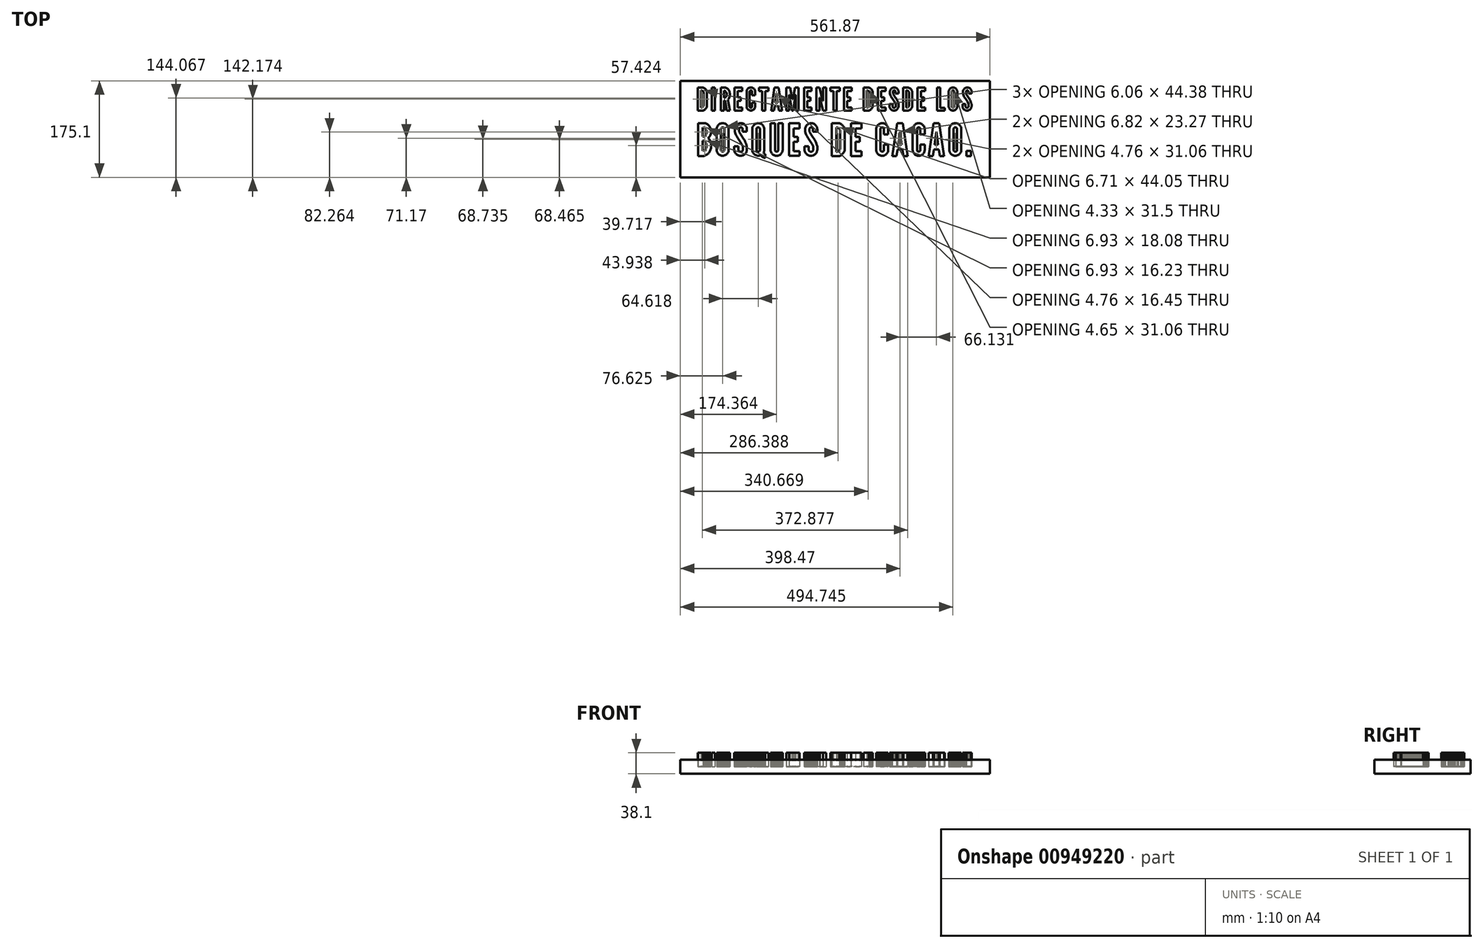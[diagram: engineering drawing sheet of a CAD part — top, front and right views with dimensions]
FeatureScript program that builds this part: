
annotation { "Feature Type Name" : "Feature", "Feature Type Description" : "" }
export const myFeature = defineFeature(function(context is Context, id is Id, definition is map)
    precondition{}
    {
        {
            var Q0;
            Q0=qCreatedBy(makeId("Top.planeOp"),FACE);
            var sketch = newSketch(context, id + "F0", { "sketchPlane" : qUnion([Q0])});
            skLineSegment(sketch, "E0", {"start": v(-116.2, -328.45) * mm, "end": v(-116.2, -376.5) * mm});
            skLineSegment(sketch, "E1", {"start": v(-116.2, -376.5) * mm, "end": v(-116.2, -377.7) * mm});
            skLineSegment(sketch, "E2", {"start": v(-116.2, -377.7) * mm, "end": v(-115.97, -378.89) * mm});
            skLineSegment(sketch, "E3", {"start": v(-115.97, -378.89) * mm, "end": v(-115.65, -379.97) * mm});
            skLineSegment(sketch, "E4", {"start": v(-115.65, -379.97) * mm, "end": v(-115.22, -381.05) * mm});
            skLineSegment(sketch, "E5", {"start": v(-115.22, -381.05) * mm, "end": v(-114.78, -382.02) * mm});
            skLineSegment(sketch, "E6", {"start": v(-114.78, -382.02) * mm, "end": v(-114.14, -383) * mm});
            skLineSegment(sketch, "E7", {"start": v(-114.14, -383) * mm, "end": v(-113.38, -383.86) * mm});
            skLineSegment(sketch, "E8", {"start": v(-113.38, -383.86) * mm, "end": v(-112.62, -384.73) * mm});
            skLineSegment(sketch, "E9", {"start": v(-112.62, -384.73) * mm, "end": v(-111.65, -385.49) * mm});
            skLineSegment(sketch, "E10", {"start": v(-111.65, -385.49) * mm, "end": v(-110.78, -386.03) * mm});
            skLineSegment(sketch, "E11", {"start": v(-110.78, -386.03) * mm, "end": v(-109.7, -386.57) * mm});
            skLineSegment(sketch, "E12", {"start": v(-109.7, -386.57) * mm, "end": v(-108.61, -387) * mm});
            skLineSegment(sketch, "E13", {"start": v(-108.61, -387) * mm, "end": v(-107.53, -387.33) * mm});
            skLineSegment(sketch, "E14", {"start": v(-107.53, -387.33) * mm, "end": v(-106.34, -387.44) * mm});
            skLineSegment(sketch, "E15", {"start": v(-106.34, -387.44) * mm, "end": v(-105.26, -387.54) * mm});
            skLineSegment(sketch, "E16", {"start": v(-105.26, -387.54) * mm, "end": v(-104.07, -387.44) * mm});
            skLineSegment(sketch, "E17", {"start": v(-104.07, -387.44) * mm, "end": v(-102.99, -387.33) * mm});
            skLineSegment(sketch, "E18", {"start": v(-102.99, -387.33) * mm, "end": v(-101.8, -387) * mm});
            skLineSegment(sketch, "E19", {"start": v(-101.8, -387) * mm, "end": v(-100.82, -386.57) * mm});
            skLineSegment(sketch, "E20", {"start": v(-100.82, -386.57) * mm, "end": v(-99.74, -386.03) * mm});
            skLineSegment(sketch, "E21", {"start": v(-99.74, -386.03) * mm, "end": v(-98.76, -385.49) * mm});
            skLineSegment(sketch, "E22", {"start": v(-98.76, -385.49) * mm, "end": v(-97.9, -384.73) * mm});
            skLineSegment(sketch, "E23", {"start": v(-97.9, -384.73) * mm, "end": v(-97.03, -383.86) * mm});
            skLineSegment(sketch, "E24", {"start": v(-97.03, -383.86) * mm, "end": v(-96.38, -383) * mm});
            skLineSegment(sketch, "E25", {"start": v(-96.38, -383) * mm, "end": v(-95.73, -382.02) * mm});
            skLineSegment(sketch, "E26", {"start": v(-95.73, -382.02) * mm, "end": v(-95.2, -381.05) * mm});
            skLineSegment(sketch, "E27", {"start": v(-95.2, -381.05) * mm, "end": v(-94.76, -379.97) * mm});
            skLineSegment(sketch, "E28", {"start": v(-94.76, -379.97) * mm, "end": v(-94.54, -378.89) * mm});
            skLineSegment(sketch, "E29", {"start": v(-94.54, -378.89) * mm, "end": v(-94.33, -377.7) * mm});
            skLineSegment(sketch, "E30", {"start": v(-94.33, -377.7) * mm, "end": v(-94.22, -376.5) * mm});
            skLineSegment(sketch, "E31", {"start": v(-94.22, -376.5) * mm, "end": v(-94.22, -328.45) * mm});
            skLineSegment(sketch, "E32", {"start": v(-94.22, -328.45) * mm, "end": v(-102.23, -328.45) * mm});
            skLineSegment(sketch, "E33", {"start": v(-102.23, -328.45) * mm, "end": v(-102.23, -377.15) * mm});
            skLineSegment(sketch, "E34", {"start": v(-108.3, -377.15) * mm, "end": v(-108.18, -377.8) * mm});
            skLineSegment(sketch, "E35", {"start": v(-108.18, -377.8) * mm, "end": v(-108.08, -378.34) * mm});
            skLineSegment(sketch, "E36", {"start": v(-108.08, -378.34) * mm, "end": v(-107.75, -378.89) * mm});
            skLineSegment(sketch, "E37", {"start": v(-107.75, -378.89) * mm, "end": v(-107.43, -379.32) * mm});
            skLineSegment(sketch, "E38", {"start": v(-107.43, -379.32) * mm, "end": v(-106.88, -379.75) * mm});
            skLineSegment(sketch, "E39", {"start": v(-106.88, -379.75) * mm, "end": v(-106.45, -379.97) * mm});
            skLineSegment(sketch, "E40", {"start": v(-106.45, -379.97) * mm, "end": v(-105.8, -380.18) * mm});
            skLineSegment(sketch, "E41", {"start": v(-105.8, -380.18) * mm, "end": v(-104.61, -380.18) * mm});
            skLineSegment(sketch, "E42", {"start": v(-104.61, -380.18) * mm, "end": v(-104.07, -379.97) * mm});
            skLineSegment(sketch, "E43", {"start": v(-104.07, -379.97) * mm, "end": v(-103.53, -379.75) * mm});
            skLineSegment(sketch, "E44", {"start": v(-103.53, -379.75) * mm, "end": v(-103.1, -379.32) * mm});
            skLineSegment(sketch, "E45", {"start": v(-103.1, -379.32) * mm, "end": v(-102.66, -378.89) * mm});
            skLineSegment(sketch, "E46", {"start": v(-102.66, -378.89) * mm, "end": v(-102.23, -377.8) * mm});
            skLineSegment(sketch, "E47", {"start": v(-102.23, -377.8) * mm, "end": v(-102.23, -377.15) * mm});
            skLineSegment(sketch, "E48", {"start": v(-108.3, -377.15) * mm, "end": v(-108.3, -328.45) * mm});
            skLineSegment(sketch, "E49", {"start": v(-108.3, -328.45) * mm, "end": v(-116.2, -328.45) * mm});
            skLineSegment(sketch, "E50", {"start": v(9.9, -341.44) * mm, "end": v(9.9, -375.1) * mm});
            skLineSegment(sketch, "E51", {"start": v(3.95, -380.3) * mm, "end": v(4.82, -380.18) * mm});
            skLineSegment(sketch, "E52", {"start": v(4.82, -380.18) * mm, "end": v(5.8, -379.97) * mm});
            skLineSegment(sketch, "E53", {"start": v(5.8, -379.97) * mm, "end": v(6.66, -379.54) * mm});
            skLineSegment(sketch, "E54", {"start": v(6.66, -379.54) * mm, "end": v(7.42, -379) * mm});
            skLineSegment(sketch, "E55", {"start": v(7.42, -379) * mm, "end": v(8.17, -378.45) * mm});
            skLineSegment(sketch, "E56", {"start": v(8.17, -378.45) * mm, "end": v(8.82, -377.7) * mm});
            skLineSegment(sketch, "E57", {"start": v(8.82, -377.7) * mm, "end": v(9.25, -376.94) * mm});
            skLineSegment(sketch, "E58", {"start": v(9.25, -376.94) * mm, "end": v(9.69, -376.07) * mm});
            skLineSegment(sketch, "E59", {"start": v(9.69, -376.07) * mm, "end": v(9.9, -375.1) * mm});
            skLineSegment(sketch, "E60", {"start": v(3.95, -380.3) * mm, "end": v(3.2, -380.3) * mm});
            skLineSegment(sketch, "E61", {"start": v(3.2, -380.3) * mm, "end": v(3.2, -336.24) * mm});
            skLineSegment(sketch, "E62", {"start": v(3.2, -336.24) * mm, "end": v(3.95, -336.24) * mm});
            skLineSegment(sketch, "E63", {"start": v(9.9, -341.44) * mm, "end": v(9.69, -340.46) * mm});
            skLineSegment(sketch, "E64", {"start": v(9.69, -340.46) * mm, "end": v(9.25, -339.6) * mm});
            skLineSegment(sketch, "E65", {"start": v(9.25, -339.6) * mm, "end": v(8.82, -338.84) * mm});
            skLineSegment(sketch, "E66", {"start": v(8.82, -338.84) * mm, "end": v(8.17, -338.08) * mm});
            skLineSegment(sketch, "E67", {"start": v(8.17, -338.08) * mm, "end": v(7.42, -337.43) * mm});
            skLineSegment(sketch, "E68", {"start": v(7.42, -337.43) * mm, "end": v(6.66, -337) * mm});
            skLineSegment(sketch, "E69", {"start": v(6.66, -337) * mm, "end": v(5.8, -336.56) * mm});
            skLineSegment(sketch, "E70", {"start": v(5.8, -336.56) * mm, "end": v(4.82, -336.35) * mm});
            skLineSegment(sketch, "E71", {"start": v(4.82, -336.35) * mm, "end": v(3.95, -336.24) * mm});
            skLineSegment(sketch, "E72", {"start": v(-5.36, -328.45) * mm, "end": v(-5.36, -387.98) * mm});
            skLineSegment(sketch, "E73", {"start": v(-5.36, -387.98) * mm, "end": v(8.6, -387.98) * mm});
            skLineSegment(sketch, "E74", {"start": v(8.6, -387.98) * mm, "end": v(9.9, -387.44) * mm});
            skLineSegment(sketch, "E75", {"start": v(9.9, -387.44) * mm, "end": v(11.2, -386.79) * mm});
            skLineSegment(sketch, "E76", {"start": v(11.2, -386.79) * mm, "end": v(12.4, -386.03) * mm});
            skLineSegment(sketch, "E77", {"start": v(12.4, -386.03) * mm, "end": v(13.48, -385.16) * mm});
            skLineSegment(sketch, "E78", {"start": v(13.48, -385.16) * mm, "end": v(14.45, -384.19) * mm});
            skLineSegment(sketch, "E79", {"start": v(14.45, -384.19) * mm, "end": v(15.42, -383.1) * mm});
            skLineSegment(sketch, "E80", {"start": v(15.42, -383.1) * mm, "end": v(16.3, -382.02) * mm});
            skLineSegment(sketch, "E81", {"start": v(16.3, -382.02) * mm, "end": v(16.94, -380.73) * mm});
            skLineSegment(sketch, "E82", {"start": v(16.94, -380.73) * mm, "end": v(17.59, -379.54) * mm});
            skLineSegment(sketch, "E83", {"start": v(17.59, -379.54) * mm, "end": v(18.13, -378.13) * mm});
            skLineSegment(sketch, "E84", {"start": v(18.13, -378.13) * mm, "end": v(18.46, -376.83) * mm});
            skLineSegment(sketch, "E85", {"start": v(18.46, -376.83) * mm, "end": v(18.46, -339.7) * mm});
            skLineSegment(sketch, "E86", {"start": v(18.46, -339.7) * mm, "end": v(18.13, -338.3) * mm});
            skLineSegment(sketch, "E87", {"start": v(18.13, -338.3) * mm, "end": v(17.59, -337) * mm});
            skLineSegment(sketch, "E88", {"start": v(17.59, -337) * mm, "end": v(16.94, -335.7) * mm});
            skLineSegment(sketch, "E89", {"start": v(16.94, -335.7) * mm, "end": v(16.3, -334.5) * mm});
            skLineSegment(sketch, "E90", {"start": v(16.3, -334.5) * mm, "end": v(15.42, -333.43) * mm});
            skLineSegment(sketch, "E91", {"start": v(15.42, -333.43) * mm, "end": v(14.45, -332.34) * mm});
            skLineSegment(sketch, "E92", {"start": v(14.45, -332.34) * mm, "end": v(13.48, -331.37) * mm});
            skLineSegment(sketch, "E93", {"start": v(13.48, -331.37) * mm, "end": v(12.4, -330.5) * mm});
            skLineSegment(sketch, "E94", {"start": v(12.4, -330.5) * mm, "end": v(11.2, -329.75) * mm});
            skLineSegment(sketch, "E95", {"start": v(11.2, -329.75) * mm, "end": v(9.9, -329.1) * mm});
            skLineSegment(sketch, "E96", {"start": v(9.9, -329.1) * mm, "end": v(8.6, -328.45) * mm});
            skLineSegment(sketch, "E97", {"start": v(8.6, -328.45) * mm, "end": v(-5.36, -328.45) * mm});
            skLineSegment(sketch, "E98", {"start": v(-135.57, -338.84) * mm, "end": v(-135.57, -377.15) * mm});
            skLineSegment(sketch, "E99", {"start": v(-141.63, -377.15) * mm, "end": v(-141.63, -377.8) * mm});
            skLineSegment(sketch, "E100", {"start": v(-141.63, -377.8) * mm, "end": v(-141.41, -378.34) * mm});
            skLineSegment(sketch, "E101", {"start": v(-141.41, -378.34) * mm, "end": v(-141.09, -378.89) * mm});
            skLineSegment(sketch, "E102", {"start": v(-141.09, -378.89) * mm, "end": v(-140.76, -379.32) * mm});
            skLineSegment(sketch, "E103", {"start": v(-140.76, -379.32) * mm, "end": v(-140.33, -379.75) * mm});
            skLineSegment(sketch, "E104", {"start": v(-140.33, -379.75) * mm, "end": v(-139.79, -379.97) * mm});
            skLineSegment(sketch, "E105", {"start": v(-139.79, -379.97) * mm, "end": v(-139.14, -380.18) * mm});
            skLineSegment(sketch, "E106", {"start": v(-139.14, -380.18) * mm, "end": v(-137.95, -380.18) * mm});
            skLineSegment(sketch, "E107", {"start": v(-137.95, -380.18) * mm, "end": v(-136.86, -379.75) * mm});
            skLineSegment(sketch, "E108", {"start": v(-136.86, -379.75) * mm, "end": v(-136, -378.89) * mm});
            skLineSegment(sketch, "E109", {"start": v(-136, -378.89) * mm, "end": v(-135.57, -377.8) * mm});
            skLineSegment(sketch, "E110", {"start": v(-135.57, -377.8) * mm, "end": v(-135.57, -377.15) * mm});
            skLineSegment(sketch, "E111", {"start": v(-141.63, -377.15) * mm, "end": v(-141.63, -338.84) * mm});
            skLineSegment(sketch, "E112", {"start": v(-135.57, -338.84) * mm, "end": v(-135.57, -338.3) * mm});
            skLineSegment(sketch, "E113", {"start": v(-135.57, -338.3) * mm, "end": v(-135.78, -337.65) * mm});
            skLineSegment(sketch, "E114", {"start": v(-135.78, -337.65) * mm, "end": v(-136, -337.21) * mm});
            skLineSegment(sketch, "E115", {"start": v(-136, -337.21) * mm, "end": v(-136.43, -336.67) * mm});
            skLineSegment(sketch, "E116", {"start": v(-136.43, -336.67) * mm, "end": v(-136.86, -336.35) * mm});
            skLineSegment(sketch, "E117", {"start": v(-136.86, -336.35) * mm, "end": v(-137.4, -336.02) * mm});
            skLineSegment(sketch, "E118", {"start": v(-137.4, -336.02) * mm, "end": v(-137.95, -335.91) * mm});
            skLineSegment(sketch, "E119", {"start": v(-137.95, -335.91) * mm, "end": v(-138.6, -335.8) * mm});
            skLineSegment(sketch, "E120", {"start": v(-138.6, -335.8) * mm, "end": v(-139.14, -335.91) * mm});
            skLineSegment(sketch, "E121", {"start": v(-139.14, -335.91) * mm, "end": v(-139.79, -336.02) * mm});
            skLineSegment(sketch, "E122", {"start": v(-139.79, -336.02) * mm, "end": v(-140.33, -336.35) * mm});
            skLineSegment(sketch, "E123", {"start": v(-140.33, -336.35) * mm, "end": v(-140.76, -336.67) * mm});
            skLineSegment(sketch, "E124", {"start": v(-140.76, -336.67) * mm, "end": v(-141.09, -337.21) * mm});
            skLineSegment(sketch, "E125", {"start": v(-141.09, -337.21) * mm, "end": v(-141.41, -337.65) * mm});
            skLineSegment(sketch, "E126", {"start": v(-141.41, -337.65) * mm, "end": v(-141.63, -338.3) * mm});
            skLineSegment(sketch, "E127", {"start": v(-141.63, -338.3) * mm, "end": v(-141.63, -338.84) * mm});
            skLineSegment(sketch, "E128", {"start": v(-149.53, -376.5) * mm, "end": v(-149.53, -339.49) * mm});
            skLineSegment(sketch, "E129", {"start": v(-127.55, -339.49) * mm, "end": v(-127.66, -338.3) * mm});
            skLineSegment(sketch, "E130", {"start": v(-127.66, -338.3) * mm, "end": v(-128.1, -336.13) * mm});
            skLineSegment(sketch, "E131", {"start": v(-128.1, -336.13) * mm, "end": v(-128.53, -335.05) * mm});
            skLineSegment(sketch, "E132", {"start": v(-128.53, -335.05) * mm, "end": v(-129.07, -333.97) * mm});
            skLineSegment(sketch, "E133", {"start": v(-129.07, -333.97) * mm, "end": v(-129.72, -333) * mm});
            skLineSegment(sketch, "E134", {"start": v(-129.72, -333) * mm, "end": v(-130.48, -332.13) * mm});
            skLineSegment(sketch, "E135", {"start": v(-130.48, -332.13) * mm, "end": v(-131.24, -331.37) * mm});
            skLineSegment(sketch, "E136", {"start": v(-131.24, -331.37) * mm, "end": v(-132.1, -330.61) * mm});
            skLineSegment(sketch, "E137", {"start": v(-132.1, -330.61) * mm, "end": v(-133.08, -329.96) * mm});
            skLineSegment(sketch, "E138", {"start": v(-133.08, -329.96) * mm, "end": v(-134.16, -329.42) * mm});
            skLineSegment(sketch, "E139", {"start": v(-134.16, -329.42) * mm, "end": v(-135.24, -328.99) * mm});
            skLineSegment(sketch, "E140", {"start": v(-135.24, -328.99) * mm, "end": v(-136.33, -328.77) * mm});
            skLineSegment(sketch, "E141", {"start": v(-136.33, -328.77) * mm, "end": v(-137.4, -328.56) * mm});
            skLineSegment(sketch, "E142", {"start": v(-137.4, -328.56) * mm, "end": v(-138.6, -328.45) * mm});
            skLineSegment(sketch, "E143", {"start": v(-138.6, -328.45) * mm, "end": v(-139.79, -328.56) * mm});
            skLineSegment(sketch, "E144", {"start": v(-139.79, -328.56) * mm, "end": v(-140.87, -328.77) * mm});
            skLineSegment(sketch, "E145", {"start": v(-140.87, -328.77) * mm, "end": v(-141.95, -328.99) * mm});
            skLineSegment(sketch, "E146", {"start": v(-141.95, -328.99) * mm, "end": v(-143.03, -329.42) * mm});
            skLineSegment(sketch, "E147", {"start": v(-143.03, -329.42) * mm, "end": v(-144.12, -329.96) * mm});
            skLineSegment(sketch, "E148", {"start": v(-144.12, -329.96) * mm, "end": v(-145.1, -330.61) * mm});
            skLineSegment(sketch, "E149", {"start": v(-145.1, -330.61) * mm, "end": v(-145.96, -331.37) * mm});
            skLineSegment(sketch, "E150", {"start": v(-145.96, -331.37) * mm, "end": v(-146.71, -332.13) * mm});
            skLineSegment(sketch, "E151", {"start": v(-146.71, -332.13) * mm, "end": v(-147.47, -333) * mm});
            skLineSegment(sketch, "E152", {"start": v(-147.47, -333) * mm, "end": v(-148.12, -333.97) * mm});
            skLineSegment(sketch, "E153", {"start": v(-148.12, -333.97) * mm, "end": v(-148.66, -335.05) * mm});
            skLineSegment(sketch, "E154", {"start": v(-148.66, -335.05) * mm, "end": v(-148.99, -336.13) * mm});
            skLineSegment(sketch, "E155", {"start": v(-148.99, -336.13) * mm, "end": v(-149.31, -337.21) * mm});
            skLineSegment(sketch, "E156", {"start": v(-149.31, -337.21) * mm, "end": v(-149.53, -338.3) * mm});
            skLineSegment(sketch, "E157", {"start": v(-149.53, -338.3) * mm, "end": v(-149.53, -339.49) * mm});
            skLineSegment(sketch, "E158", {"start": v(-127.55, -339.49) * mm, "end": v(-127.55, -376.5) * mm});
            skLineSegment(sketch, "E159", {"start": v(-129.29, -382.35) * mm, "end": v(-128.64, -381.27) * mm});
            skLineSegment(sketch, "E160", {"start": v(-128.64, -381.27) * mm, "end": v(-128.2, -380.08) * mm});
            skLineSegment(sketch, "E161", {"start": v(-128.2, -380.08) * mm, "end": v(-127.88, -379) * mm});
            skLineSegment(sketch, "E162", {"start": v(-127.88, -379) * mm, "end": v(-127.66, -377.8) * mm});
            skLineSegment(sketch, "E163", {"start": v(-127.66, -377.8) * mm, "end": v(-127.55, -376.5) * mm});
            skLineSegment(sketch, "E164", {"start": v(-129.29, -382.35) * mm, "end": v(-128.2, -383.43) * mm});
            skLineSegment(sketch, "E165", {"start": v(-128.2, -383.43) * mm, "end": v(-127.55, -383.97) * mm});
            skLineSegment(sketch, "E166", {"start": v(-127.55, -383.97) * mm, "end": v(-126.8, -384.3) * mm});
            skLineSegment(sketch, "E167", {"start": v(-126.8, -384.3) * mm, "end": v(-126.04, -384.51) * mm});
            skLineSegment(sketch, "E168", {"start": v(-126.04, -384.51) * mm, "end": v(-126.04, -391.55) * mm});
            skLineSegment(sketch, "E169", {"start": v(-134.05, -386.57) * mm, "end": v(-133.4, -387.44) * mm});
            skLineSegment(sketch, "E170", {"start": v(-133.4, -387.44) * mm, "end": v(-132.75, -388.3) * mm});
            skLineSegment(sketch, "E171", {"start": v(-132.75, -388.3) * mm, "end": v(-131.89, -389.06) * mm});
            skLineSegment(sketch, "E172", {"start": v(-131.89, -389.06) * mm, "end": v(-131.13, -389.7) * mm});
            skLineSegment(sketch, "E173", {"start": v(-131.13, -389.7) * mm, "end": v(-130.16, -390.25) * mm});
            skLineSegment(sketch, "E174", {"start": v(-130.16, -390.25) * mm, "end": v(-129.18, -390.8) * mm});
            skLineSegment(sketch, "E175", {"start": v(-129.18, -390.8) * mm, "end": v(-128.2, -391.12) * mm});
            skLineSegment(sketch, "E176", {"start": v(-128.2, -391.12) * mm, "end": v(-127.12, -391.33) * mm});
            skLineSegment(sketch, "E177", {"start": v(-127.12, -391.33) * mm, "end": v(-126.04, -391.55) * mm});
            skLineSegment(sketch, "E178", {"start": v(-149.53, -376.5) * mm, "end": v(-149.53, -377.7) * mm});
            skLineSegment(sketch, "E179", {"start": v(-149.53, -377.7) * mm, "end": v(-149.31, -378.89) * mm});
            skLineSegment(sketch, "E180", {"start": v(-149.31, -378.89) * mm, "end": v(-148.99, -379.97) * mm});
            skLineSegment(sketch, "E181", {"start": v(-148.99, -379.97) * mm, "end": v(-148.66, -381.05) * mm});
            skLineSegment(sketch, "E182", {"start": v(-148.66, -381.05) * mm, "end": v(-148.12, -382.02) * mm});
            skLineSegment(sketch, "E183", {"start": v(-148.12, -382.02) * mm, "end": v(-147.47, -383) * mm});
            skLineSegment(sketch, "E184", {"start": v(-147.47, -383) * mm, "end": v(-146.71, -383.97) * mm});
            skLineSegment(sketch, "E185", {"start": v(-146.71, -383.97) * mm, "end": v(-145.85, -384.73) * mm});
            skLineSegment(sketch, "E186", {"start": v(-145.85, -384.73) * mm, "end": v(-144.98, -385.49) * mm});
            skLineSegment(sketch, "E187", {"start": v(-144.98, -385.49) * mm, "end": v(-144, -386.14) * mm});
            skLineSegment(sketch, "E188", {"start": v(-144, -386.14) * mm, "end": v(-143.03, -386.57) * mm});
            skLineSegment(sketch, "E189", {"start": v(-143.03, -386.57) * mm, "end": v(-141.95, -387) * mm});
            skLineSegment(sketch, "E190", {"start": v(-141.95, -387) * mm, "end": v(-140.76, -387.33) * mm});
            skLineSegment(sketch, "E191", {"start": v(-140.76, -387.33) * mm, "end": v(-139.68, -387.44) * mm});
            skLineSegment(sketch, "E192", {"start": v(-139.68, -387.44) * mm, "end": v(-138.49, -387.54) * mm});
            skLineSegment(sketch, "E193", {"start": v(-138.49, -387.54) * mm, "end": v(-137.3, -387.44) * mm});
            skLineSegment(sketch, "E194", {"start": v(-137.3, -387.44) * mm, "end": v(-136.22, -387.33) * mm});
            skLineSegment(sketch, "E195", {"start": v(-136.22, -387.33) * mm, "end": v(-135.13, -387) * mm});
            skLineSegment(sketch, "E196", {"start": v(-135.13, -387) * mm, "end": v(-134.05, -386.57) * mm});
            skLineSegment(sketch, "E197", {"start": v(-167.06, -338.84) * mm, "end": v(-167.06, -343.7) * mm});
            skLineSegment(sketch, "E198", {"start": v(-167.06, -343.7) * mm, "end": v(-159.16, -343.7) * mm});
            skLineSegment(sketch, "E199", {"start": v(-159.16, -343.7) * mm, "end": v(-159.16, -339.49) * mm});
            skLineSegment(sketch, "E200", {"start": v(-159.16, -339.49) * mm, "end": v(-159.16, -338.3) * mm});
            skLineSegment(sketch, "E201", {"start": v(-159.16, -338.3) * mm, "end": v(-159.38, -337.21) * mm});
            skLineSegment(sketch, "E202", {"start": v(-159.38, -337.21) * mm, "end": v(-159.7, -336.13) * mm});
            skLineSegment(sketch, "E203", {"start": v(-159.7, -336.13) * mm, "end": v(-160.03, -335.05) * mm});
            skLineSegment(sketch, "E204", {"start": v(-160.03, -335.05) * mm, "end": v(-160.57, -333.97) * mm});
            skLineSegment(sketch, "E205", {"start": v(-160.57, -333.97) * mm, "end": v(-161.22, -333) * mm});
            skLineSegment(sketch, "E206", {"start": v(-161.22, -333) * mm, "end": v(-161.97, -332.13) * mm});
            skLineSegment(sketch, "E207", {"start": v(-161.97, -332.13) * mm, "end": v(-162.73, -331.37) * mm});
            skLineSegment(sketch, "E208", {"start": v(-162.73, -331.37) * mm, "end": v(-163.7, -330.61) * mm});
            skLineSegment(sketch, "E209", {"start": v(-163.7, -330.61) * mm, "end": v(-164.58, -329.96) * mm});
            skLineSegment(sketch, "E210", {"start": v(-164.58, -329.96) * mm, "end": v(-165.65, -329.42) * mm});
            skLineSegment(sketch, "E211", {"start": v(-165.65, -329.42) * mm, "end": v(-166.74, -328.99) * mm});
            skLineSegment(sketch, "E212", {"start": v(-166.74, -328.99) * mm, "end": v(-167.82, -328.77) * mm});
            skLineSegment(sketch, "E213", {"start": v(-167.82, -328.77) * mm, "end": v(-169.01, -328.56) * mm});
            skLineSegment(sketch, "E214", {"start": v(-169.01, -328.56) * mm, "end": v(-170.1, -328.45) * mm});
            skLineSegment(sketch, "E215", {"start": v(-170.1, -328.45) * mm, "end": v(-171.28, -328.56) * mm});
            skLineSegment(sketch, "E216", {"start": v(-171.28, -328.56) * mm, "end": v(-172.37, -328.77) * mm});
            skLineSegment(sketch, "E217", {"start": v(-172.37, -328.77) * mm, "end": v(-173.45, -328.99) * mm});
            skLineSegment(sketch, "E218", {"start": v(-173.45, -328.99) * mm, "end": v(-174.53, -329.42) * mm});
            skLineSegment(sketch, "E219", {"start": v(-174.53, -329.42) * mm, "end": v(-175.61, -329.96) * mm});
            skLineSegment(sketch, "E220", {"start": v(-175.61, -329.96) * mm, "end": v(-176.59, -330.61) * mm});
            skLineSegment(sketch, "E221", {"start": v(-176.59, -330.61) * mm, "end": v(-177.46, -331.37) * mm});
            skLineSegment(sketch, "E222", {"start": v(-177.46, -331.37) * mm, "end": v(-178.32, -332.13) * mm});
            skLineSegment(sketch, "E223", {"start": v(-178.32, -332.13) * mm, "end": v(-178.97, -333) * mm});
            skLineSegment(sketch, "E224", {"start": v(-178.97, -333) * mm, "end": v(-179.62, -333.97) * mm});
            skLineSegment(sketch, "E225", {"start": v(-179.62, -333.97) * mm, "end": v(-180.16, -335.05) * mm});
            skLineSegment(sketch, "E226", {"start": v(-180.16, -335.05) * mm, "end": v(-180.6, -336.13) * mm});
            skLineSegment(sketch, "E227", {"start": v(-180.6, -336.13) * mm, "end": v(-180.8, -337.21) * mm});
            skLineSegment(sketch, "E228", {"start": v(-180.8, -337.21) * mm, "end": v(-181.03, -338.3) * mm});
            skLineSegment(sketch, "E229", {"start": v(-181.03, -338.3) * mm, "end": v(-181.13, -339.49) * mm});
            skLineSegment(sketch, "E230", {"start": v(-181.13, -339.49) * mm, "end": v(-181.13, -343.7) * mm});
            skLineSegment(sketch, "E231", {"start": v(-181.13, -343.7) * mm, "end": v(-180.38, -346.09) * mm});
            skLineSegment(sketch, "E232", {"start": v(-180.38, -346.09) * mm, "end": v(-179.51, -348.36) * mm});
            skLineSegment(sketch, "E233", {"start": v(-179.51, -348.36) * mm, "end": v(-178.54, -350.63) * mm});
            skLineSegment(sketch, "E234", {"start": v(-178.54, -350.63) * mm, "end": v(-177.46, -352.8) * mm});
            skLineSegment(sketch, "E235", {"start": v(-177.46, -352.8) * mm, "end": v(-176.26, -354.96) * mm});
            skLineSegment(sketch, "E236", {"start": v(-176.26, -354.96) * mm, "end": v(-174.86, -357.02) * mm});
            skLineSegment(sketch, "E237", {"start": v(-174.86, -357.02) * mm, "end": v(-173.34, -358.97) * mm});
            skLineSegment(sketch, "E238", {"start": v(-166.52, -370.66) * mm, "end": v(-168.69, -366.65) * mm});
            skLineSegment(sketch, "E239", {"start": v(-168.69, -366.65) * mm, "end": v(-170.96, -362.87) * mm});
            skLineSegment(sketch, "E240", {"start": v(-170.96, -362.87) * mm, "end": v(-173.34, -358.97) * mm});
            skLineSegment(sketch, "E241", {"start": v(-166.52, -370.66) * mm, "end": v(-166.52, -376.18) * mm});
            skLineSegment(sketch, "E242", {"start": v(-174.53, -377.15) * mm, "end": v(-174.31, -377.8) * mm});
            skLineSegment(sketch, "E243", {"start": v(-174.31, -377.8) * mm, "end": v(-174, -378.45) * mm});
            skLineSegment(sketch, "E244", {"start": v(-174, -378.45) * mm, "end": v(-173.56, -379) * mm});
            skLineSegment(sketch, "E245", {"start": v(-173.56, -379) * mm, "end": v(-173.02, -379.43) * mm});
            skLineSegment(sketch, "E246", {"start": v(-173.02, -379.43) * mm, "end": v(-172.47, -379.86) * mm});
            skLineSegment(sketch, "E247", {"start": v(-172.47, -379.86) * mm, "end": v(-171.82, -380.08) * mm});
            skLineSegment(sketch, "E248", {"start": v(-171.82, -380.08) * mm, "end": v(-171.07, -380.3) * mm});
            skLineSegment(sketch, "E249", {"start": v(-171.07, -380.3) * mm, "end": v(-170.42, -380.3) * mm});
            skLineSegment(sketch, "E250", {"start": v(-170.42, -380.3) * mm, "end": v(-169.77, -380.18) * mm});
            skLineSegment(sketch, "E251", {"start": v(-169.77, -380.18) * mm, "end": v(-169.01, -379.97) * mm});
            skLineSegment(sketch, "E252", {"start": v(-169.01, -379.97) * mm, "end": v(-168.47, -379.75) * mm});
            skLineSegment(sketch, "E253", {"start": v(-168.47, -379.75) * mm, "end": v(-167.82, -379.32) * mm});
            skLineSegment(sketch, "E254", {"start": v(-167.82, -379.32) * mm, "end": v(-167.39, -378.78) * mm});
            skLineSegment(sketch, "E255", {"start": v(-167.39, -378.78) * mm, "end": v(-166.96, -378.23) * mm});
            skLineSegment(sketch, "E256", {"start": v(-166.96, -378.23) * mm, "end": v(-166.74, -377.59) * mm});
            skLineSegment(sketch, "E257", {"start": v(-166.74, -377.59) * mm, "end": v(-166.52, -376.94) * mm});
            skLineSegment(sketch, "E258", {"start": v(-166.52, -376.94) * mm, "end": v(-166.52, -376.18) * mm});
            skLineSegment(sketch, "E259", {"start": v(-174.53, -377.15) * mm, "end": v(-174.53, -370.66) * mm});
            skLineSegment(sketch, "E260", {"start": v(-174.53, -370.66) * mm, "end": v(-182.32, -370.66) * mm});
            skLineSegment(sketch, "E261", {"start": v(-182.32, -370.66) * mm, "end": v(-182.32, -376.5) * mm});
            skLineSegment(sketch, "E262", {"start": v(-182.32, -376.5) * mm, "end": v(-182.22, -377.8) * mm});
            skLineSegment(sketch, "E263", {"start": v(-182.22, -377.8) * mm, "end": v(-182, -379) * mm});
            skLineSegment(sketch, "E264", {"start": v(-182, -379) * mm, "end": v(-181.57, -380.08) * mm});
            skLineSegment(sketch, "E265", {"start": v(-181.57, -380.08) * mm, "end": v(-181.13, -381.27) * mm});
            skLineSegment(sketch, "E266", {"start": v(-181.13, -381.27) * mm, "end": v(-180.49, -382.24) * mm});
            skLineSegment(sketch, "E267", {"start": v(-180.49, -382.24) * mm, "end": v(-179.73, -383.21) * mm});
            skLineSegment(sketch, "E268", {"start": v(-179.73, -383.21) * mm, "end": v(-178.97, -384.19) * mm});
            skLineSegment(sketch, "E269", {"start": v(-178.97, -384.19) * mm, "end": v(-178.1, -384.95) * mm});
            skLineSegment(sketch, "E270", {"start": v(-178.1, -384.95) * mm, "end": v(-177.02, -385.7) * mm});
            skLineSegment(sketch, "E271", {"start": v(-177.02, -385.7) * mm, "end": v(-176.05, -386.25) * mm});
            skLineSegment(sketch, "E272", {"start": v(-176.05, -386.25) * mm, "end": v(-174.86, -386.79) * mm});
            skLineSegment(sketch, "E273", {"start": v(-174.86, -386.79) * mm, "end": v(-173.78, -387.11) * mm});
            skLineSegment(sketch, "E274", {"start": v(-173.78, -387.11) * mm, "end": v(-172.58, -387.44) * mm});
            skLineSegment(sketch, "E275", {"start": v(-172.58, -387.44) * mm, "end": v(-171.4, -387.54) * mm});
            skLineSegment(sketch, "E276", {"start": v(-171.4, -387.54) * mm, "end": v(-170.1, -387.54) * mm});
            skLineSegment(sketch, "E277", {"start": v(-170.1, -387.54) * mm, "end": v(-168.9, -387.44) * mm});
            skLineSegment(sketch, "E278", {"start": v(-168.9, -387.44) * mm, "end": v(-167.71, -387.11) * mm});
            skLineSegment(sketch, "E279", {"start": v(-167.71, -387.11) * mm, "end": v(-166.63, -386.79) * mm});
            skLineSegment(sketch, "E280", {"start": v(-166.63, -386.79) * mm, "end": v(-165.44, -386.25) * mm});
            skLineSegment(sketch, "E281", {"start": v(-165.44, -386.25) * mm, "end": v(-164.47, -385.7) * mm});
            skLineSegment(sketch, "E282", {"start": v(-164.47, -385.7) * mm, "end": v(-163.38, -384.95) * mm});
            skLineSegment(sketch, "E283", {"start": v(-163.38, -384.95) * mm, "end": v(-162.52, -384.19) * mm});
            skLineSegment(sketch, "E284", {"start": v(-162.52, -384.19) * mm, "end": v(-161.76, -383.21) * mm});
            skLineSegment(sketch, "E285", {"start": v(-161.76, -383.21) * mm, "end": v(-161, -382.24) * mm});
            skLineSegment(sketch, "E286", {"start": v(-161, -382.24) * mm, "end": v(-160.35, -381.27) * mm});
            skLineSegment(sketch, "E287", {"start": v(-160.35, -381.27) * mm, "end": v(-159.92, -380.08) * mm});
            skLineSegment(sketch, "E288", {"start": v(-159.92, -380.08) * mm, "end": v(-159.49, -379) * mm});
            skLineSegment(sketch, "E289", {"start": v(-159.49, -379) * mm, "end": v(-159.27, -377.8) * mm});
            skLineSegment(sketch, "E290", {"start": v(-159.27, -377.8) * mm, "end": v(-159.16, -376.5) * mm});
            skLineSegment(sketch, "E291", {"start": v(-159.16, -376.5) * mm, "end": v(-159.16, -370.66) * mm});
            skLineSegment(sketch, "E292", {"start": v(-159.16, -370.66) * mm, "end": v(-159.81, -368.06) * mm});
            skLineSegment(sketch, "E293", {"start": v(-159.81, -368.06) * mm, "end": v(-160.79, -365.57) * mm});
            skLineSegment(sketch, "E294", {"start": v(-160.79, -365.57) * mm, "end": v(-161.76, -363.2) * mm});
            skLineSegment(sketch, "E295", {"start": v(-161.76, -363.2) * mm, "end": v(-162.84, -360.8) * mm});
            skLineSegment(sketch, "E296", {"start": v(-162.84, -360.8) * mm, "end": v(-164.14, -358.54) * mm});
            skLineSegment(sketch, "E297", {"start": v(-164.14, -358.54) * mm, "end": v(-165.55, -356.37) * mm});
            skLineSegment(sketch, "E298", {"start": v(-165.55, -356.37) * mm, "end": v(-167.06, -354.2) * mm});
            skLineSegment(sketch, "E299", {"start": v(-173.12, -343.7) * mm, "end": v(-172.15, -345.87) * mm});
            skLineSegment(sketch, "E300", {"start": v(-172.15, -345.87) * mm, "end": v(-171.07, -348.04) * mm});
            skLineSegment(sketch, "E301", {"start": v(-171.07, -348.04) * mm, "end": v(-169.77, -350.2) * mm});
            skLineSegment(sketch, "E302", {"start": v(-169.77, -350.2) * mm, "end": v(-168.47, -352.26) * mm});
            skLineSegment(sketch, "E303", {"start": v(-168.47, -352.26) * mm, "end": v(-167.06, -354.2) * mm});
            skLineSegment(sketch, "E304", {"start": v(-173.12, -343.7) * mm, "end": v(-173.12, -338.84) * mm});
            skLineSegment(sketch, "E305", {"start": v(-167.06, -338.84) * mm, "end": v(-167.06, -338.3) * mm});
            skLineSegment(sketch, "E306", {"start": v(-167.06, -338.3) * mm, "end": v(-167.28, -337.65) * mm});
            skLineSegment(sketch, "E307", {"start": v(-167.28, -337.65) * mm, "end": v(-167.6, -337.21) * mm});
            skLineSegment(sketch, "E308", {"start": v(-167.6, -337.21) * mm, "end": v(-167.93, -336.67) * mm});
            skLineSegment(sketch, "E309", {"start": v(-167.93, -336.67) * mm, "end": v(-168.36, -336.35) * mm});
            skLineSegment(sketch, "E310", {"start": v(-168.36, -336.35) * mm, "end": v(-168.9, -336.02) * mm});
            skLineSegment(sketch, "E311", {"start": v(-168.9, -336.02) * mm, "end": v(-169.55, -335.91) * mm});
            skLineSegment(sketch, "E312", {"start": v(-169.55, -335.91) * mm, "end": v(-170.1, -335.8) * mm});
            skLineSegment(sketch, "E313", {"start": v(-170.1, -335.8) * mm, "end": v(-170.74, -335.91) * mm});
            skLineSegment(sketch, "E314", {"start": v(-170.74, -335.91) * mm, "end": v(-171.28, -336.02) * mm});
            skLineSegment(sketch, "E315", {"start": v(-171.28, -336.02) * mm, "end": v(-171.82, -336.35) * mm});
            skLineSegment(sketch, "E316", {"start": v(-171.82, -336.35) * mm, "end": v(-172.26, -336.67) * mm});
            skLineSegment(sketch, "E317", {"start": v(-172.26, -336.67) * mm, "end": v(-172.7, -337.21) * mm});
            skLineSegment(sketch, "E318", {"start": v(-172.7, -337.21) * mm, "end": v(-172.9, -337.65) * mm});
            skLineSegment(sketch, "E319", {"start": v(-172.9, -337.65) * mm, "end": v(-173.12, -338.3) * mm});
            skLineSegment(sketch, "E320", {"start": v(-173.12, -338.3) * mm, "end": v(-173.12, -338.84) * mm});
            skLineSegment(sketch, "E321", {"start": v(-39.34, -338.84) * mm, "end": v(-39.34, -343.7) * mm});
            skLineSegment(sketch, "E322", {"start": v(-39.34, -343.7) * mm, "end": v(-31.44, -343.7) * mm});
            skLineSegment(sketch, "E323", {"start": v(-31.44, -343.7) * mm, "end": v(-31.44, -339.49) * mm});
            skLineSegment(sketch, "E324", {"start": v(-31.44, -339.49) * mm, "end": v(-31.55, -338.3) * mm});
            skLineSegment(sketch, "E325", {"start": v(-31.55, -338.3) * mm, "end": v(-31.66, -337.21) * mm});
            skLineSegment(sketch, "E326", {"start": v(-31.66, -337.21) * mm, "end": v(-31.98, -336.13) * mm});
            skLineSegment(sketch, "E327", {"start": v(-31.98, -336.13) * mm, "end": v(-32.42, -335.05) * mm});
            skLineSegment(sketch, "E328", {"start": v(-32.42, -335.05) * mm, "end": v(-32.96, -333.97) * mm});
            skLineSegment(sketch, "E329", {"start": v(-32.96, -333.97) * mm, "end": v(-33.6, -333) * mm});
            skLineSegment(sketch, "E330", {"start": v(-33.6, -333) * mm, "end": v(-34.26, -332.13) * mm});
            skLineSegment(sketch, "E331", {"start": v(-34.26, -332.13) * mm, "end": v(-35.12, -331.37) * mm});
            skLineSegment(sketch, "E332", {"start": v(-35.12, -331.37) * mm, "end": v(-35.99, -330.61) * mm});
            skLineSegment(sketch, "E333", {"start": v(-35.99, -330.61) * mm, "end": v(-36.96, -329.96) * mm});
            skLineSegment(sketch, "E334", {"start": v(-36.96, -329.96) * mm, "end": v(-37.94, -329.42) * mm});
            skLineSegment(sketch, "E335", {"start": v(-37.94, -329.42) * mm, "end": v(-39.02, -328.99) * mm});
            skLineSegment(sketch, "E336", {"start": v(-39.02, -328.99) * mm, "end": v(-40.2, -328.77) * mm});
            skLineSegment(sketch, "E337", {"start": v(-40.2, -328.77) * mm, "end": v(-41.3, -328.56) * mm});
            skLineSegment(sketch, "E338", {"start": v(-41.3, -328.56) * mm, "end": v(-42.48, -328.45) * mm});
            skLineSegment(sketch, "E339", {"start": v(-42.48, -328.45) * mm, "end": v(-43.56, -328.56) * mm});
            skLineSegment(sketch, "E340", {"start": v(-43.56, -328.56) * mm, "end": v(-44.75, -328.77) * mm});
            skLineSegment(sketch, "E341", {"start": v(-44.75, -328.77) * mm, "end": v(-45.84, -328.99) * mm});
            skLineSegment(sketch, "E342", {"start": v(-45.84, -328.99) * mm, "end": v(-46.92, -329.42) * mm});
            skLineSegment(sketch, "E343", {"start": v(-46.92, -329.42) * mm, "end": v(-47.9, -329.96) * mm});
            skLineSegment(sketch, "E344", {"start": v(-47.9, -329.96) * mm, "end": v(-48.87, -330.61) * mm});
            skLineSegment(sketch, "E345", {"start": v(-48.87, -330.61) * mm, "end": v(-49.84, -331.37) * mm});
            skLineSegment(sketch, "E346", {"start": v(-49.84, -331.37) * mm, "end": v(-50.6, -332.13) * mm});
            skLineSegment(sketch, "E347", {"start": v(-50.6, -332.13) * mm, "end": v(-51.36, -333) * mm});
            skLineSegment(sketch, "E348", {"start": v(-51.36, -333) * mm, "end": v(-52, -333.97) * mm});
            skLineSegment(sketch, "E349", {"start": v(-52, -333.97) * mm, "end": v(-52.44, -335.05) * mm});
            skLineSegment(sketch, "E350", {"start": v(-52.44, -335.05) * mm, "end": v(-52.87, -336.13) * mm});
            skLineSegment(sketch, "E351", {"start": v(-52.87, -336.13) * mm, "end": v(-53.2, -337.21) * mm});
            skLineSegment(sketch, "E352", {"start": v(-53.2, -337.21) * mm, "end": v(-53.41, -338.3) * mm});
            skLineSegment(sketch, "E353", {"start": v(-53.41, -338.3) * mm, "end": v(-53.41, -339.49) * mm});
            skLineSegment(sketch, "E354", {"start": v(-53.41, -339.49) * mm, "end": v(-53.41, -343.7) * mm});
            skLineSegment(sketch, "E355", {"start": v(-53.41, -343.7) * mm, "end": v(-52.77, -346.09) * mm});
            skLineSegment(sketch, "E356", {"start": v(-52.77, -346.09) * mm, "end": v(-51.9, -348.36) * mm});
            skLineSegment(sketch, "E357", {"start": v(-51.9, -348.36) * mm, "end": v(-50.92, -350.63) * mm});
            skLineSegment(sketch, "E358", {"start": v(-50.92, -350.63) * mm, "end": v(-49.84, -352.8) * mm});
            skLineSegment(sketch, "E359", {"start": v(-49.84, -352.8) * mm, "end": v(-48.54, -354.96) * mm});
            skLineSegment(sketch, "E360", {"start": v(-48.54, -354.96) * mm, "end": v(-47.25, -357.02) * mm});
            skLineSegment(sketch, "E361", {"start": v(-47.25, -357.02) * mm, "end": v(-45.73, -358.97) * mm});
            skLineSegment(sketch, "E362", {"start": v(-38.8, -370.66) * mm, "end": v(-40.97, -366.65) * mm});
            skLineSegment(sketch, "E363", {"start": v(-40.97, -366.65) * mm, "end": v(-43.35, -362.87) * mm});
            skLineSegment(sketch, "E364", {"start": v(-43.35, -362.87) * mm, "end": v(-45.73, -358.97) * mm});
            skLineSegment(sketch, "E365", {"start": v(-38.8, -370.66) * mm, "end": v(-38.8, -376.18) * mm});
            skLineSegment(sketch, "E366", {"start": v(-46.81, -377.15) * mm, "end": v(-46.6, -377.8) * mm});
            skLineSegment(sketch, "E367", {"start": v(-46.6, -377.8) * mm, "end": v(-46.27, -378.45) * mm});
            skLineSegment(sketch, "E368", {"start": v(-46.27, -378.45) * mm, "end": v(-45.84, -379) * mm});
            skLineSegment(sketch, "E369", {"start": v(-45.84, -379) * mm, "end": v(-45.4, -379.43) * mm});
            skLineSegment(sketch, "E370", {"start": v(-45.4, -379.43) * mm, "end": v(-44.75, -379.86) * mm});
            skLineSegment(sketch, "E371", {"start": v(-44.75, -379.86) * mm, "end": v(-44.1, -380.08) * mm});
            skLineSegment(sketch, "E372", {"start": v(-44.1, -380.08) * mm, "end": v(-43.46, -380.3) * mm});
            skLineSegment(sketch, "E373", {"start": v(-43.46, -380.3) * mm, "end": v(-42.7, -380.3) * mm});
            skLineSegment(sketch, "E374", {"start": v(-42.7, -380.3) * mm, "end": v(-42.05, -380.18) * mm});
            skLineSegment(sketch, "E375", {"start": v(-42.05, -380.18) * mm, "end": v(-40.75, -379.75) * mm});
            skLineSegment(sketch, "E376", {"start": v(-40.75, -379.75) * mm, "end": v(-40.2, -379.32) * mm});
            skLineSegment(sketch, "E377", {"start": v(-40.2, -379.32) * mm, "end": v(-39.67, -378.78) * mm});
            skLineSegment(sketch, "E378", {"start": v(-39.67, -378.78) * mm, "end": v(-39.34, -378.23) * mm});
            skLineSegment(sketch, "E379", {"start": v(-39.34, -378.23) * mm, "end": v(-39.02, -377.59) * mm});
            skLineSegment(sketch, "E380", {"start": v(-39.02, -377.59) * mm, "end": v(-38.91, -376.94) * mm});
            skLineSegment(sketch, "E381", {"start": v(-38.91, -376.94) * mm, "end": v(-38.8, -376.18) * mm});
            skLineSegment(sketch, "E382", {"start": v(-46.81, -377.15) * mm, "end": v(-46.81, -370.66) * mm});
            skLineSegment(sketch, "E383", {"start": v(-46.81, -370.66) * mm, "end": v(-54.71, -370.66) * mm});
            skLineSegment(sketch, "E384", {"start": v(-54.71, -370.66) * mm, "end": v(-54.71, -376.5) * mm});
            skLineSegment(sketch, "E385", {"start": v(-54.71, -376.5) * mm, "end": v(-54.6, -377.8) * mm});
            skLineSegment(sketch, "E386", {"start": v(-54.6, -377.8) * mm, "end": v(-54.28, -379) * mm});
            skLineSegment(sketch, "E387", {"start": v(-54.28, -379) * mm, "end": v(-53.96, -380.08) * mm});
            skLineSegment(sketch, "E388", {"start": v(-53.96, -380.08) * mm, "end": v(-53.41, -381.27) * mm});
            skLineSegment(sketch, "E389", {"start": v(-53.41, -381.27) * mm, "end": v(-52.87, -382.24) * mm});
            skLineSegment(sketch, "E390", {"start": v(-52.87, -382.24) * mm, "end": v(-52.12, -383.21) * mm});
            skLineSegment(sketch, "E391", {"start": v(-52.12, -383.21) * mm, "end": v(-51.25, -384.19) * mm});
            skLineSegment(sketch, "E392", {"start": v(-51.25, -384.19) * mm, "end": v(-50.38, -384.95) * mm});
            skLineSegment(sketch, "E393", {"start": v(-50.38, -384.95) * mm, "end": v(-49.4, -385.7) * mm});
            skLineSegment(sketch, "E394", {"start": v(-49.4, -385.7) * mm, "end": v(-48.33, -386.25) * mm});
            skLineSegment(sketch, "E395", {"start": v(-48.33, -386.25) * mm, "end": v(-47.25, -386.79) * mm});
            skLineSegment(sketch, "E396", {"start": v(-47.25, -386.79) * mm, "end": v(-44.86, -387.44) * mm});
            skLineSegment(sketch, "E397", {"start": v(-44.86, -387.44) * mm, "end": v(-43.67, -387.54) * mm});
            skLineSegment(sketch, "E398", {"start": v(-43.67, -387.54) * mm, "end": v(-42.48, -387.54) * mm});
            skLineSegment(sketch, "E399", {"start": v(-42.48, -387.54) * mm, "end": v(-41.3, -387.44) * mm});
            skLineSegment(sketch, "E400", {"start": v(-41.3, -387.44) * mm, "end": v(-38.91, -386.79) * mm});
            skLineSegment(sketch, "E401", {"start": v(-38.91, -386.79) * mm, "end": v(-37.83, -386.25) * mm});
            skLineSegment(sketch, "E402", {"start": v(-37.83, -386.25) * mm, "end": v(-36.75, -385.7) * mm});
            skLineSegment(sketch, "E403", {"start": v(-36.75, -385.7) * mm, "end": v(-35.77, -384.95) * mm});
            skLineSegment(sketch, "E404", {"start": v(-35.77, -384.95) * mm, "end": v(-34.9, -384.19) * mm});
            skLineSegment(sketch, "E405", {"start": v(-34.9, -384.19) * mm, "end": v(-34.04, -383.21) * mm});
            skLineSegment(sketch, "E406", {"start": v(-34.04, -383.21) * mm, "end": v(-33.28, -382.24) * mm});
            skLineSegment(sketch, "E407", {"start": v(-33.28, -382.24) * mm, "end": v(-32.74, -381.27) * mm});
            skLineSegment(sketch, "E408", {"start": v(-32.74, -381.27) * mm, "end": v(-32.2, -380.08) * mm});
            skLineSegment(sketch, "E409", {"start": v(-32.2, -380.08) * mm, "end": v(-31.88, -379) * mm});
            skLineSegment(sketch, "E410", {"start": v(-31.88, -379) * mm, "end": v(-31.55, -377.8) * mm});
            skLineSegment(sketch, "E411", {"start": v(-31.55, -377.8) * mm, "end": v(-31.44, -376.5) * mm});
            skLineSegment(sketch, "E412", {"start": v(-31.44, -376.5) * mm, "end": v(-31.44, -370.66) * mm});
            skLineSegment(sketch, "E413", {"start": v(-31.44, -370.66) * mm, "end": v(-32.2, -368.06) * mm});
            skLineSegment(sketch, "E414", {"start": v(-32.2, -368.06) * mm, "end": v(-33.07, -365.57) * mm});
            skLineSegment(sketch, "E415", {"start": v(-33.07, -365.57) * mm, "end": v(-34.04, -363.2) * mm});
            skLineSegment(sketch, "E416", {"start": v(-34.04, -363.2) * mm, "end": v(-35.23, -360.8) * mm});
            skLineSegment(sketch, "E417", {"start": v(-35.23, -360.8) * mm, "end": v(-36.53, -358.54) * mm});
            skLineSegment(sketch, "E418", {"start": v(-36.53, -358.54) * mm, "end": v(-37.83, -356.37) * mm});
            skLineSegment(sketch, "E419", {"start": v(-37.83, -356.37) * mm, "end": v(-39.34, -354.2) * mm});
            skLineSegment(sketch, "E420", {"start": v(-45.51, -343.7) * mm, "end": v(-44.54, -345.87) * mm});
            skLineSegment(sketch, "E421", {"start": v(-44.54, -345.87) * mm, "end": v(-43.35, -348.04) * mm});
            skLineSegment(sketch, "E422", {"start": v(-43.35, -348.04) * mm, "end": v(-42.16, -350.2) * mm});
            skLineSegment(sketch, "E423", {"start": v(-42.16, -350.2) * mm, "end": v(-40.86, -352.26) * mm});
            skLineSegment(sketch, "E424", {"start": v(-40.86, -352.26) * mm, "end": v(-39.34, -354.2) * mm});
            skLineSegment(sketch, "E425", {"start": v(-45.51, -343.7) * mm, "end": v(-45.51, -338.84) * mm});
            skLineSegment(sketch, "E426", {"start": v(-39.34, -338.84) * mm, "end": v(-39.45, -338.3) * mm});
            skLineSegment(sketch, "E427", {"start": v(-39.45, -338.3) * mm, "end": v(-39.67, -337.65) * mm});
            skLineSegment(sketch, "E428", {"start": v(-39.67, -337.65) * mm, "end": v(-39.89, -337.21) * mm});
            skLineSegment(sketch, "E429", {"start": v(-39.89, -337.21) * mm, "end": v(-40.32, -336.67) * mm});
            skLineSegment(sketch, "E430", {"start": v(-40.32, -336.67) * mm, "end": v(-40.75, -336.35) * mm});
            skLineSegment(sketch, "E431", {"start": v(-40.75, -336.35) * mm, "end": v(-41.3, -336.02) * mm});
            skLineSegment(sketch, "E432", {"start": v(-41.3, -336.02) * mm, "end": v(-41.83, -335.91) * mm});
            skLineSegment(sketch, "E433", {"start": v(-41.83, -335.91) * mm, "end": v(-42.48, -335.8) * mm});
            skLineSegment(sketch, "E434", {"start": v(-42.48, -335.8) * mm, "end": v(-43.03, -335.91) * mm});
            skLineSegment(sketch, "E435", {"start": v(-43.03, -335.91) * mm, "end": v(-43.56, -336.02) * mm});
            skLineSegment(sketch, "E436", {"start": v(-43.56, -336.02) * mm, "end": v(-44.1, -336.35) * mm});
            skLineSegment(sketch, "E437", {"start": v(-44.1, -336.35) * mm, "end": v(-44.65, -336.67) * mm});
            skLineSegment(sketch, "E438", {"start": v(-44.65, -336.67) * mm, "end": v(-44.97, -337.21) * mm});
            skLineSegment(sketch, "E439", {"start": v(-44.97, -337.21) * mm, "end": v(-45.3, -337.65) * mm});
            skLineSegment(sketch, "E440", {"start": v(-45.3, -337.65) * mm, "end": v(-45.4, -338.3) * mm});
            skLineSegment(sketch, "E441", {"start": v(-45.4, -338.3) * mm, "end": v(-45.51, -338.84) * mm});
            skLineSegment(sketch, "E442", {"start": v(-234.06, -376.18) * mm, "end": v(-233.52, -374.88) * mm});
            skLineSegment(sketch, "E443", {"start": v(-233.52, -374.88) * mm, "end": v(-233.09, -373.47) * mm});
            skLineSegment(sketch, "E444", {"start": v(-233.09, -373.47) * mm, "end": v(-232.65, -372.07) * mm});
            skLineSegment(sketch, "E445", {"start": v(-232.65, -372.07) * mm, "end": v(-232.55, -370.66) * mm});
            skLineSegment(sketch, "E446", {"start": v(-232.55, -370.66) * mm, "end": v(-232.44, -369.25) * mm});
            skLineSegment(sketch, "E447", {"start": v(-232.44, -369.25) * mm, "end": v(-232.55, -367.84) * mm});
            skLineSegment(sketch, "E448", {"start": v(-232.55, -367.84) * mm, "end": v(-232.65, -366.44) * mm});
            skLineSegment(sketch, "E449", {"start": v(-232.65, -366.44) * mm, "end": v(-233.09, -365.03) * mm});
            skLineSegment(sketch, "E450", {"start": v(-233.09, -365.03) * mm, "end": v(-233.52, -363.73) * mm});
            skLineSegment(sketch, "E451", {"start": v(-233.52, -363.73) * mm, "end": v(-234.06, -362.43) * mm});
            skLineSegment(sketch, "E452", {"start": v(-239.37, -378.34) * mm, "end": v(-238.28, -378.13) * mm});
            skLineSegment(sketch, "E453", {"start": v(-238.28, -378.13) * mm, "end": v(-237.1, -377.91) * mm});
            skLineSegment(sketch, "E454", {"start": v(-237.1, -377.91) * mm, "end": v(-236.01, -377.48) * mm});
            skLineSegment(sketch, "E455", {"start": v(-236.01, -377.48) * mm, "end": v(-235.04, -376.83) * mm});
            skLineSegment(sketch, "E456", {"start": v(-235.04, -376.83) * mm, "end": v(-234.06, -376.18) * mm});
            skLineSegment(sketch, "E457", {"start": v(-239.37, -378.34) * mm, "end": v(-239.37, -360.27) * mm});
            skLineSegment(sketch, "E458", {"start": v(-234.06, -362.43) * mm, "end": v(-235.04, -361.68) * mm});
            skLineSegment(sketch, "E459", {"start": v(-235.04, -361.68) * mm, "end": v(-236.01, -361.13) * mm});
            skLineSegment(sketch, "E460", {"start": v(-236.01, -361.13) * mm, "end": v(-237.1, -360.7) * mm});
            skLineSegment(sketch, "E461", {"start": v(-237.1, -360.7) * mm, "end": v(-238.28, -360.38) * mm});
            skLineSegment(sketch, "E462", {"start": v(-238.28, -360.38) * mm, "end": v(-239.37, -360.27) * mm});
            skLineSegment(sketch, "E463", {"start": v(-234.06, -350.2) * mm, "end": v(-233.52, -349.12) * mm});
            skLineSegment(sketch, "E464", {"start": v(-233.52, -349.12) * mm, "end": v(-232.98, -348.04) * mm});
            skLineSegment(sketch, "E465", {"start": v(-232.98, -348.04) * mm, "end": v(-232.65, -346.85) * mm});
            skLineSegment(sketch, "E466", {"start": v(-232.65, -346.85) * mm, "end": v(-232.44, -345.66) * mm});
            skLineSegment(sketch, "E467", {"start": v(-232.44, -345.66) * mm, "end": v(-232.44, -343.17) * mm});
            skLineSegment(sketch, "E468", {"start": v(-232.44, -343.17) * mm, "end": v(-232.65, -341.98) * mm});
            skLineSegment(sketch, "E469", {"start": v(-232.65, -341.98) * mm, "end": v(-232.98, -340.79) * mm});
            skLineSegment(sketch, "E470", {"start": v(-232.98, -340.79) * mm, "end": v(-233.52, -339.6) * mm});
            skLineSegment(sketch, "E471", {"start": v(-233.52, -339.6) * mm, "end": v(-234.06, -338.62) * mm});
            skLineSegment(sketch, "E472", {"start": v(-239.37, -352.48) * mm, "end": v(-238.6, -352.58) * mm});
            skLineSegment(sketch, "E473", {"start": v(-238.6, -352.58) * mm, "end": v(-237.1, -352.37) * mm});
            skLineSegment(sketch, "E474", {"start": v(-237.1, -352.37) * mm, "end": v(-236.44, -352.15) * mm});
            skLineSegment(sketch, "E475", {"start": v(-236.44, -352.15) * mm, "end": v(-235.69, -351.82) * mm});
            skLineSegment(sketch, "E476", {"start": v(-235.69, -351.82) * mm, "end": v(-235.14, -351.4) * mm});
            skLineSegment(sketch, "E477", {"start": v(-235.14, -351.4) * mm, "end": v(-234.6, -350.85) * mm});
            skLineSegment(sketch, "E478", {"start": v(-234.6, -350.85) * mm, "end": v(-234.06, -350.2) * mm});
            skLineSegment(sketch, "E479", {"start": v(-239.37, -352.48) * mm, "end": v(-239.37, -336.35) * mm});
            skLineSegment(sketch, "E480", {"start": v(-234.06, -338.62) * mm, "end": v(-235.04, -337.86) * mm});
            skLineSegment(sketch, "E481", {"start": v(-235.04, -337.86) * mm, "end": v(-236.01, -337.32) * mm});
            skLineSegment(sketch, "E482", {"start": v(-236.01, -337.32) * mm, "end": v(-237.1, -336.78) * mm});
            skLineSegment(sketch, "E483", {"start": v(-237.1, -336.78) * mm, "end": v(-238.28, -336.56) * mm});
            skLineSegment(sketch, "E484", {"start": v(-238.28, -336.56) * mm, "end": v(-239.37, -336.35) * mm});
            skLineSegment(sketch, "E485", {"start": v(-247.7, -328.45) * mm, "end": v(-247.7, -387.98) * mm});
            skLineSegment(sketch, "E486", {"start": v(-247.7, -387.98) * mm, "end": v(-238.82, -387.98) * mm});
            skLineSegment(sketch, "E487", {"start": v(-238.82, -387.98) * mm, "end": v(-237.53, -387.87) * mm});
            skLineSegment(sketch, "E488", {"start": v(-237.53, -387.87) * mm, "end": v(-236.12, -387.54) * mm});
            skLineSegment(sketch, "E489", {"start": v(-236.12, -387.54) * mm, "end": v(-234.82, -387.11) * mm});
            skLineSegment(sketch, "E490", {"start": v(-234.82, -387.11) * mm, "end": v(-233.52, -386.57) * mm});
            skLineSegment(sketch, "E491", {"start": v(-233.52, -386.57) * mm, "end": v(-232.33, -385.92) * mm});
            skLineSegment(sketch, "E492", {"start": v(-232.33, -385.92) * mm, "end": v(-231.14, -385.16) * mm});
            skLineSegment(sketch, "E493", {"start": v(-231.14, -385.16) * mm, "end": v(-230.06, -384.3) * mm});
            skLineSegment(sketch, "E494", {"start": v(-230.06, -384.3) * mm, "end": v(-229.08, -383.32) * mm});
            skLineSegment(sketch, "E495", {"start": v(-229.08, -383.32) * mm, "end": v(-228.22, -382.24) * mm});
            skLineSegment(sketch, "E496", {"start": v(-228.22, -382.24) * mm, "end": v(-227.46, -381.16) * mm});
            skLineSegment(sketch, "E497", {"start": v(-227.46, -381.16) * mm, "end": v(-226.81, -379.97) * mm});
            skLineSegment(sketch, "E498", {"start": v(-226.81, -379.97) * mm, "end": v(-226.05, -378.34) * mm});
            skLineSegment(sketch, "E499", {"start": v(-226.05, -378.34) * mm, "end": v(-225.4, -376.83) * mm});
            skLineSegment(sketch, "E500", {"start": v(-225.4, -376.83) * mm, "end": v(-224.97, -375.2) * mm});
            skLineSegment(sketch, "E501", {"start": v(-224.97, -375.2) * mm, "end": v(-224.54, -373.47) * mm});
            skLineSegment(sketch, "E502", {"start": v(-224.54, -373.47) * mm, "end": v(-224.32, -371.85) * mm});
            skLineSegment(sketch, "E503", {"start": v(-224.32, -371.85) * mm, "end": v(-224.21, -370.12) * mm});
            skLineSegment(sketch, "E504", {"start": v(-224.21, -370.12) * mm, "end": v(-224.21, -368.39) * mm});
            skLineSegment(sketch, "E505", {"start": v(-224.21, -368.39) * mm, "end": v(-224.32, -366.76) * mm});
            skLineSegment(sketch, "E506", {"start": v(-224.32, -366.76) * mm, "end": v(-224.54, -365.03) * mm});
            skLineSegment(sketch, "E507", {"start": v(-224.54, -365.03) * mm, "end": v(-224.97, -363.4) * mm});
            skLineSegment(sketch, "E508", {"start": v(-224.97, -363.4) * mm, "end": v(-225.4, -361.78) * mm});
            skLineSegment(sketch, "E509", {"start": v(-225.4, -361.78) * mm, "end": v(-226.05, -360.16) * mm});
            skLineSegment(sketch, "E510", {"start": v(-226.05, -360.16) * mm, "end": v(-226.81, -358.64) * mm});
            skLineSegment(sketch, "E511", {"start": v(-226.81, -358.64) * mm, "end": v(-227.68, -357.45) * mm});
            skLineSegment(sketch, "E512", {"start": v(-227.68, -357.45) * mm, "end": v(-228.65, -356.48) * mm});
            skLineSegment(sketch, "E513", {"start": v(-228.65, -356.48) * mm, "end": v(-229.73, -355.5) * mm});
            skLineSegment(sketch, "E514", {"start": v(-229.73, -355.5) * mm, "end": v(-228.65, -354.53) * mm});
            skLineSegment(sketch, "E515", {"start": v(-228.65, -354.53) * mm, "end": v(-227.68, -353.56) * mm});
            skLineSegment(sketch, "E516", {"start": v(-227.68, -353.56) * mm, "end": v(-226.81, -352.37) * mm});
            skLineSegment(sketch, "E517", {"start": v(-226.81, -352.37) * mm, "end": v(-226.05, -351.18) * mm});
            skLineSegment(sketch, "E518", {"start": v(-226.05, -351.18) * mm, "end": v(-225.4, -349.88) * mm});
            skLineSegment(sketch, "E519", {"start": v(-225.4, -349.88) * mm, "end": v(-224.86, -348.47) * mm});
            skLineSegment(sketch, "E520", {"start": v(-224.86, -348.47) * mm, "end": v(-224.54, -347.06) * mm});
            skLineSegment(sketch, "E521", {"start": v(-224.54, -347.06) * mm, "end": v(-224.21, -345.66) * mm});
            skLineSegment(sketch, "E522", {"start": v(-224.21, -345.66) * mm, "end": v(-224.1, -344.25) * mm});
            skLineSegment(sketch, "E523", {"start": v(-224.1, -344.25) * mm, "end": v(-224.1, -342.84) * mm});
            skLineSegment(sketch, "E524", {"start": v(-224.1, -342.84) * mm, "end": v(-224.21, -341.33) * mm});
            skLineSegment(sketch, "E525", {"start": v(-224.21, -341.33) * mm, "end": v(-224.54, -339.92) * mm});
            skLineSegment(sketch, "E526", {"start": v(-224.54, -339.92) * mm, "end": v(-224.86, -338.51) * mm});
            skLineSegment(sketch, "E527", {"start": v(-224.86, -338.51) * mm, "end": v(-225.4, -337.21) * mm});
            skLineSegment(sketch, "E528", {"start": v(-225.4, -337.21) * mm, "end": v(-226.05, -335.91) * mm});
            skLineSegment(sketch, "E529", {"start": v(-226.05, -335.91) * mm, "end": v(-226.81, -334.62) * mm});
            skLineSegment(sketch, "E530", {"start": v(-226.81, -334.62) * mm, "end": v(-227.57, -333.53) * mm});
            skLineSegment(sketch, "E531", {"start": v(-227.57, -333.53) * mm, "end": v(-228.54, -332.45) * mm});
            skLineSegment(sketch, "E532", {"start": v(-228.54, -332.45) * mm, "end": v(-229.62, -331.37) * mm});
            skLineSegment(sketch, "E533", {"start": v(-229.62, -331.37) * mm, "end": v(-230.82, -330.5) * mm});
            skLineSegment(sketch, "E534", {"start": v(-230.82, -330.5) * mm, "end": v(-232, -329.75) * mm});
            skLineSegment(sketch, "E535", {"start": v(-232, -329.75) * mm, "end": v(-233.3, -329.1) * mm});
            skLineSegment(sketch, "E536", {"start": v(-233.3, -329.1) * mm, "end": v(-234.6, -328.45) * mm});
            skLineSegment(sketch, "E537", {"start": v(-234.6, -328.45) * mm, "end": v(-247.7, -328.45) * mm});
            skLineSegment(sketch, "E538", {"start": v(239.48, -378.67) * mm, "end": v(247.7, -378.67) * mm});
            skLineSegment(sketch, "E539", {"start": v(247.7, -378.67) * mm, "end": v(247.7, -387.98) * mm});
            skLineSegment(sketch, "E540", {"start": v(247.7, -387.98) * mm, "end": v(239.48, -387.98) * mm});
            skLineSegment(sketch, "E541", {"start": v(239.48, -387.98) * mm, "end": v(239.48, -378.67) * mm});
            skLineSegment(sketch, "E542", {"start": v(-237.74, -272.7) * mm, "end": v(-237.74, -296.4) * mm});
            skLineSegment(sketch, "E543", {"start": v(-241.96, -300.09) * mm, "end": v(-241.31, -299.98) * mm});
            skLineSegment(sketch, "E544", {"start": v(-241.31, -299.98) * mm, "end": v(-240.56, -299.76) * mm});
            skLineSegment(sketch, "E545", {"start": v(-240.56, -299.76) * mm, "end": v(-239.9, -299.44) * mm});
            skLineSegment(sketch, "E546", {"start": v(-239.9, -299.44) * mm, "end": v(-239.26, -299) * mm});
            skLineSegment(sketch, "E547", {"start": v(-239.26, -299) * mm, "end": v(-238.72, -298.46) * mm});
            skLineSegment(sketch, "E548", {"start": v(-238.72, -298.46) * mm, "end": v(-238.28, -297.81) * mm});
            skLineSegment(sketch, "E549", {"start": v(-238.28, -297.81) * mm, "end": v(-237.96, -297.17) * mm});
            skLineSegment(sketch, "E550", {"start": v(-237.96, -297.17) * mm, "end": v(-237.74, -296.4) * mm});
            skLineSegment(sketch, "E551", {"start": v(-241.96, -300.09) * mm, "end": v(-242.5, -300.09) * mm});
            skLineSegment(sketch, "E552", {"start": v(-242.5, -300.09) * mm, "end": v(-242.5, -269.02) * mm});
            skLineSegment(sketch, "E553", {"start": v(-242.5, -269.02) * mm, "end": v(-241.96, -269.02) * mm});
            skLineSegment(sketch, "E554", {"start": v(-237.74, -272.7) * mm, "end": v(-237.96, -271.95) * mm});
            skLineSegment(sketch, "E555", {"start": v(-237.96, -271.95) * mm, "end": v(-238.28, -271.3) * mm});
            skLineSegment(sketch, "E556", {"start": v(-238.28, -271.3) * mm, "end": v(-238.72, -270.65) * mm});
            skLineSegment(sketch, "E557", {"start": v(-238.72, -270.65) * mm, "end": v(-239.26, -270.1) * mm});
            skLineSegment(sketch, "E558", {"start": v(-239.26, -270.1) * mm, "end": v(-239.9, -269.67) * mm});
            skLineSegment(sketch, "E559", {"start": v(-239.9, -269.67) * mm, "end": v(-240.56, -269.35) * mm});
            skLineSegment(sketch, "E560", {"start": v(-240.56, -269.35) * mm, "end": v(-241.31, -269.13) * mm});
            skLineSegment(sketch, "E561", {"start": v(-241.31, -269.13) * mm, "end": v(-241.96, -269.02) * mm});
            skLineSegment(sketch, "E562", {"start": v(-248.57, -263.61) * mm, "end": v(-248.57, -305.5) * mm});
            skLineSegment(sketch, "E563", {"start": v(-248.57, -305.5) * mm, "end": v(-238.72, -305.5) * mm});
            skLineSegment(sketch, "E564", {"start": v(-238.72, -305.5) * mm, "end": v(-237.53, -305.07) * mm});
            skLineSegment(sketch, "E565", {"start": v(-237.53, -305.07) * mm, "end": v(-236.55, -304.42) * mm});
            skLineSegment(sketch, "E566", {"start": v(-236.55, -304.42) * mm, "end": v(-235.47, -303.77) * mm});
            skLineSegment(sketch, "E567", {"start": v(-235.47, -303.77) * mm, "end": v(-234.6, -302.9) * mm});
            skLineSegment(sketch, "E568", {"start": v(-234.6, -302.9) * mm, "end": v(-233.85, -302.04) * mm});
            skLineSegment(sketch, "E569", {"start": v(-233.85, -302.04) * mm, "end": v(-233.09, -301.06) * mm});
            skLineSegment(sketch, "E570", {"start": v(-233.09, -301.06) * mm, "end": v(-232.55, -299.98) * mm});
            skLineSegment(sketch, "E571", {"start": v(-232.55, -299.98) * mm, "end": v(-232, -298.79) * mm});
            skLineSegment(sketch, "E572", {"start": v(-232, -298.79) * mm, "end": v(-231.68, -297.7) * mm});
            skLineSegment(sketch, "E573", {"start": v(-231.68, -297.7) * mm, "end": v(-231.68, -271.4) * mm});
            skLineSegment(sketch, "E574", {"start": v(-231.68, -271.4) * mm, "end": v(-232, -270.32) * mm});
            skLineSegment(sketch, "E575", {"start": v(-232, -270.32) * mm, "end": v(-232.55, -269.13) * mm});
            skLineSegment(sketch, "E576", {"start": v(-232.55, -269.13) * mm, "end": v(-233.09, -268.05) * mm});
            skLineSegment(sketch, "E577", {"start": v(-233.09, -268.05) * mm, "end": v(-233.85, -267.08) * mm});
            skLineSegment(sketch, "E578", {"start": v(-233.85, -267.08) * mm, "end": v(-234.6, -266.2) * mm});
            skLineSegment(sketch, "E579", {"start": v(-234.6, -266.2) * mm, "end": v(-235.47, -265.34) * mm});
            skLineSegment(sketch, "E580", {"start": v(-235.47, -265.34) * mm, "end": v(-236.55, -264.7) * mm});
            skLineSegment(sketch, "E581", {"start": v(-236.55, -264.7) * mm, "end": v(-237.53, -264.04) * mm});
            skLineSegment(sketch, "E582", {"start": v(-237.53, -264.04) * mm, "end": v(-238.72, -263.61) * mm});
            skLineSegment(sketch, "E583", {"start": v(-238.72, -263.61) * mm, "end": v(-248.57, -263.61) * mm});
            skLineSegment(sketch, "E584", {"start": v(63.16, -272.7) * mm, "end": v(63.16, -296.4) * mm});
            skLineSegment(sketch, "E585", {"start": v(58.93, -300.09) * mm, "end": v(59.7, -299.98) * mm});
            skLineSegment(sketch, "E586", {"start": v(59.7, -299.98) * mm, "end": v(60.45, -299.76) * mm});
            skLineSegment(sketch, "E587", {"start": v(60.45, -299.76) * mm, "end": v(61.1, -299.44) * mm});
            skLineSegment(sketch, "E588", {"start": v(61.1, -299.44) * mm, "end": v(61.64, -299) * mm});
            skLineSegment(sketch, "E589", {"start": v(61.64, -299) * mm, "end": v(62.18, -298.46) * mm});
            skLineSegment(sketch, "E590", {"start": v(62.18, -298.46) * mm, "end": v(62.62, -297.81) * mm});
            skLineSegment(sketch, "E591", {"start": v(62.62, -297.81) * mm, "end": v(62.94, -297.17) * mm});
            skLineSegment(sketch, "E592", {"start": v(62.94, -297.17) * mm, "end": v(63.16, -296.4) * mm});
            skLineSegment(sketch, "E593", {"start": v(58.93, -300.09) * mm, "end": v(58.5, -300.09) * mm});
            skLineSegment(sketch, "E594", {"start": v(58.5, -300.09) * mm, "end": v(58.5, -269.02) * mm});
            skLineSegment(sketch, "E595", {"start": v(58.5, -269.02) * mm, "end": v(58.93, -269.02) * mm});
            skLineSegment(sketch, "E596", {"start": v(63.16, -272.7) * mm, "end": v(62.94, -271.95) * mm});
            skLineSegment(sketch, "E597", {"start": v(62.94, -271.95) * mm, "end": v(62.62, -271.3) * mm});
            skLineSegment(sketch, "E598", {"start": v(62.62, -271.3) * mm, "end": v(62.18, -270.65) * mm});
            skLineSegment(sketch, "E599", {"start": v(62.18, -270.65) * mm, "end": v(61.64, -270.1) * mm});
            skLineSegment(sketch, "E600", {"start": v(61.64, -270.1) * mm, "end": v(61.1, -269.67) * mm});
            skLineSegment(sketch, "E601", {"start": v(61.1, -269.67) * mm, "end": v(60.45, -269.35) * mm});
            skLineSegment(sketch, "E602", {"start": v(60.45, -269.35) * mm, "end": v(59.7, -269.13) * mm});
            skLineSegment(sketch, "E603", {"start": v(59.7, -269.13) * mm, "end": v(58.93, -269.02) * mm});
            skLineSegment(sketch, "E604", {"start": v(52.44, -263.61) * mm, "end": v(52.44, -305.5) * mm});
            skLineSegment(sketch, "E605", {"start": v(52.44, -305.5) * mm, "end": v(62.29, -305.5) * mm});
            skLineSegment(sketch, "E606", {"start": v(62.29, -305.5) * mm, "end": v(63.37, -305.07) * mm});
            skLineSegment(sketch, "E607", {"start": v(63.37, -305.07) * mm, "end": v(64.46, -304.42) * mm});
            skLineSegment(sketch, "E608", {"start": v(64.46, -304.42) * mm, "end": v(65.43, -303.77) * mm});
            skLineSegment(sketch, "E609", {"start": v(65.43, -303.77) * mm, "end": v(66.3, -302.9) * mm});
            skLineSegment(sketch, "E610", {"start": v(66.3, -302.9) * mm, "end": v(67.16, -302.04) * mm});
            skLineSegment(sketch, "E611", {"start": v(67.16, -302.04) * mm, "end": v(67.8, -301.06) * mm});
            skLineSegment(sketch, "E612", {"start": v(67.8, -301.06) * mm, "end": v(68.46, -299.98) * mm});
            skLineSegment(sketch, "E613", {"start": v(68.46, -299.98) * mm, "end": v(68.9, -298.79) * mm});
            skLineSegment(sketch, "E614", {"start": v(68.9, -298.79) * mm, "end": v(69.22, -297.7) * mm});
            skLineSegment(sketch, "E615", {"start": v(69.22, -297.7) * mm, "end": v(69.22, -271.4) * mm});
            skLineSegment(sketch, "E616", {"start": v(69.22, -271.4) * mm, "end": v(68.9, -270.32) * mm});
            skLineSegment(sketch, "E617", {"start": v(68.9, -270.32) * mm, "end": v(68.46, -269.13) * mm});
            skLineSegment(sketch, "E618", {"start": v(68.46, -269.13) * mm, "end": v(67.8, -268.05) * mm});
            skLineSegment(sketch, "E619", {"start": v(67.8, -268.05) * mm, "end": v(67.16, -267.08) * mm});
            skLineSegment(sketch, "E620", {"start": v(67.16, -267.08) * mm, "end": v(65.43, -265.34) * mm});
            skLineSegment(sketch, "E621", {"start": v(65.43, -265.34) * mm, "end": v(64.46, -264.7) * mm});
            skLineSegment(sketch, "E622", {"start": v(64.46, -264.7) * mm, "end": v(63.37, -264.04) * mm});
            skLineSegment(sketch, "E623", {"start": v(63.37, -264.04) * mm, "end": v(62.29, -263.61) * mm});
            skLineSegment(sketch, "E624", {"start": v(62.29, -263.61) * mm, "end": v(52.44, -263.61) * mm});
            skLineSegment(sketch, "E625", {"start": v(135.13, -272.7) * mm, "end": v(135.13, -296.4) * mm});
            skLineSegment(sketch, "E626", {"start": v(130.91, -300.09) * mm, "end": v(131.67, -299.98) * mm});
            skLineSegment(sketch, "E627", {"start": v(131.67, -299.98) * mm, "end": v(132.43, -299.76) * mm});
            skLineSegment(sketch, "E628", {"start": v(132.43, -299.76) * mm, "end": v(133.08, -299.44) * mm});
            skLineSegment(sketch, "E629", {"start": v(133.08, -299.44) * mm, "end": v(133.62, -299) * mm});
            skLineSegment(sketch, "E630", {"start": v(133.62, -299) * mm, "end": v(134.16, -298.46) * mm});
            skLineSegment(sketch, "E631", {"start": v(134.16, -298.46) * mm, "end": v(134.6, -297.81) * mm});
            skLineSegment(sketch, "E632", {"start": v(134.6, -297.81) * mm, "end": v(134.92, -297.17) * mm});
            skLineSegment(sketch, "E633", {"start": v(134.92, -297.17) * mm, "end": v(135.13, -296.4) * mm});
            skLineSegment(sketch, "E634", {"start": v(130.91, -300.09) * mm, "end": v(130.37, -300.09) * mm});
            skLineSegment(sketch, "E635", {"start": v(130.37, -300.09) * mm, "end": v(130.37, -269.02) * mm});
            skLineSegment(sketch, "E636", {"start": v(130.37, -269.02) * mm, "end": v(130.91, -269.02) * mm});
            skLineSegment(sketch, "E637", {"start": v(135.13, -272.7) * mm, "end": v(134.92, -271.95) * mm});
            skLineSegment(sketch, "E638", {"start": v(134.92, -271.95) * mm, "end": v(134.6, -271.3) * mm});
            skLineSegment(sketch, "E639", {"start": v(134.6, -271.3) * mm, "end": v(134.16, -270.65) * mm});
            skLineSegment(sketch, "E640", {"start": v(134.16, -270.65) * mm, "end": v(133.62, -270.1) * mm});
            skLineSegment(sketch, "E641", {"start": v(133.62, -270.1) * mm, "end": v(133.08, -269.67) * mm});
            skLineSegment(sketch, "E642", {"start": v(133.08, -269.67) * mm, "end": v(132.43, -269.35) * mm});
            skLineSegment(sketch, "E643", {"start": v(132.43, -269.35) * mm, "end": v(131.67, -269.13) * mm});
            skLineSegment(sketch, "E644", {"start": v(131.67, -269.13) * mm, "end": v(130.91, -269.02) * mm});
            skLineSegment(sketch, "E645", {"start": v(124.42, -263.61) * mm, "end": v(124.42, -305.5) * mm});
            skLineSegment(sketch, "E646", {"start": v(124.42, -305.5) * mm, "end": v(134.27, -305.5) * mm});
            skLineSegment(sketch, "E647", {"start": v(134.27, -305.5) * mm, "end": v(135.35, -305.07) * mm});
            skLineSegment(sketch, "E648", {"start": v(135.35, -305.07) * mm, "end": v(136.43, -304.42) * mm});
            skLineSegment(sketch, "E649", {"start": v(136.43, -304.42) * mm, "end": v(137.4, -303.77) * mm});
            skLineSegment(sketch, "E650", {"start": v(137.4, -303.77) * mm, "end": v(138.27, -302.9) * mm});
            skLineSegment(sketch, "E651", {"start": v(138.27, -302.9) * mm, "end": v(139.14, -302.04) * mm});
            skLineSegment(sketch, "E652", {"start": v(139.14, -302.04) * mm, "end": v(139.79, -301.06) * mm});
            skLineSegment(sketch, "E653", {"start": v(139.79, -301.06) * mm, "end": v(140.44, -299.98) * mm});
            skLineSegment(sketch, "E654", {"start": v(140.44, -299.98) * mm, "end": v(140.87, -298.79) * mm});
            skLineSegment(sketch, "E655", {"start": v(140.87, -298.79) * mm, "end": v(141.2, -297.7) * mm});
            skLineSegment(sketch, "E656", {"start": v(141.2, -297.7) * mm, "end": v(141.2, -271.4) * mm});
            skLineSegment(sketch, "E657", {"start": v(141.2, -271.4) * mm, "end": v(140.87, -270.32) * mm});
            skLineSegment(sketch, "E658", {"start": v(140.87, -270.32) * mm, "end": v(140.44, -269.13) * mm});
            skLineSegment(sketch, "E659", {"start": v(140.44, -269.13) * mm, "end": v(139.79, -268.05) * mm});
            skLineSegment(sketch, "E660", {"start": v(139.79, -268.05) * mm, "end": v(139.14, -267.08) * mm});
            skLineSegment(sketch, "E661", {"start": v(139.14, -267.08) * mm, "end": v(137.4, -265.34) * mm});
            skLineSegment(sketch, "E662", {"start": v(137.4, -265.34) * mm, "end": v(136.43, -264.7) * mm});
            skLineSegment(sketch, "E663", {"start": v(136.43, -264.7) * mm, "end": v(135.35, -264.04) * mm});
            skLineSegment(sketch, "E664", {"start": v(135.35, -264.04) * mm, "end": v(134.27, -263.61) * mm});
            skLineSegment(sketch, "E665", {"start": v(134.27, -263.61) * mm, "end": v(124.42, -263.61) * mm});
            skLineSegment(sketch, "E666", {"start": v(-223.02, -263.61) * mm, "end": v(-217.07, -263.61) * mm});
            skLineSegment(sketch, "E667", {"start": v(-217.07, -263.61) * mm, "end": v(-217.07, -305.5) * mm});
            skLineSegment(sketch, "E668", {"start": v(-217.07, -305.5) * mm, "end": v(-223.02, -305.5) * mm});
            skLineSegment(sketch, "E669", {"start": v(-223.02, -305.5) * mm, "end": v(-223.02, -263.61) * mm});
            skLineSegment(sketch, "E670", {"start": v(-197.15, -280.82) * mm, "end": v(-196.61, -279.85) * mm});
            skLineSegment(sketch, "E671", {"start": v(-196.61, -279.85) * mm, "end": v(-196.29, -278.76) * mm});
            skLineSegment(sketch, "E672", {"start": v(-196.29, -278.76) * mm, "end": v(-195.96, -277.68) * mm});
            skLineSegment(sketch, "E673", {"start": v(-195.96, -277.68) * mm, "end": v(-195.86, -276.5) * mm});
            skLineSegment(sketch, "E674", {"start": v(-195.86, -276.5) * mm, "end": v(-195.86, -275.4) * mm});
            skLineSegment(sketch, "E675", {"start": v(-195.86, -275.4) * mm, "end": v(-195.96, -274.22) * mm});
            skLineSegment(sketch, "E676", {"start": v(-195.96, -274.22) * mm, "end": v(-196.29, -273.14) * mm});
            skLineSegment(sketch, "E677", {"start": v(-196.29, -273.14) * mm, "end": v(-196.61, -272.05) * mm});
            skLineSegment(sketch, "E678", {"start": v(-196.61, -272.05) * mm, "end": v(-197.15, -271.08) * mm});
            skLineSegment(sketch, "E679", {"start": v(-200.83, -282.34) * mm, "end": v(-199.86, -282.23) * mm});
            skLineSegment(sketch, "E680", {"start": v(-199.86, -282.23) * mm, "end": v(-198.88, -281.9) * mm});
            skLineSegment(sketch, "E681", {"start": v(-198.88, -281.9) * mm, "end": v(-197.91, -281.47) * mm});
            skLineSegment(sketch, "E682", {"start": v(-197.91, -281.47) * mm, "end": v(-197.15, -280.82) * mm});
            skLineSegment(sketch, "E683", {"start": v(-200.83, -282.34) * mm, "end": v(-200.83, -269.57) * mm});
            skLineSegment(sketch, "E684", {"start": v(-197.15, -271.08) * mm, "end": v(-197.91, -270.43) * mm});
            skLineSegment(sketch, "E685", {"start": v(-197.91, -270.43) * mm, "end": v(-198.88, -270) * mm});
            skLineSegment(sketch, "E686", {"start": v(-198.88, -270) * mm, "end": v(-199.86, -269.67) * mm});
            skLineSegment(sketch, "E687", {"start": v(-199.86, -269.67) * mm, "end": v(-200.83, -269.57) * mm});
            skLineSegment(sketch, "E688", {"start": v(-200.83, -263.61) * mm, "end": v(-206.46, -263.61) * mm});
            skLineSegment(sketch, "E689", {"start": v(-206.46, -263.61) * mm, "end": v(-206.46, -305.5) * mm});
            skLineSegment(sketch, "E690", {"start": v(-206.46, -305.5) * mm, "end": v(-200.83, -305.5) * mm});
            skLineSegment(sketch, "E691", {"start": v(-200.83, -305.5) * mm, "end": v(-200.83, -287.2) * mm});
            skLineSegment(sketch, "E692", {"start": v(-200.83, -287.2) * mm, "end": v(-200.4, -287.42) * mm});
            skLineSegment(sketch, "E693", {"start": v(-200.4, -287.42) * mm, "end": v(-199.54, -287.42) * mm});
            skLineSegment(sketch, "E694", {"start": v(-199.54, -287.42) * mm, "end": v(-199.1, -287.2) * mm});
            skLineSegment(sketch, "E695", {"start": v(-199.1, -287.2) * mm, "end": v(-195.86, -305.5) * mm});
            skLineSegment(sketch, "E696", {"start": v(-195.86, -305.5) * mm, "end": v(-190, -305.5) * mm});
            skLineSegment(sketch, "E697", {"start": v(-190, -305.5) * mm, "end": v(-193.47, -285.58) * mm});
            skLineSegment(sketch, "E698", {"start": v(-193.47, -285.58) * mm, "end": v(-192.6, -284.4) * mm});
            skLineSegment(sketch, "E699", {"start": v(-192.6, -284.4) * mm, "end": v(-191.96, -283.1) * mm});
            skLineSegment(sketch, "E700", {"start": v(-191.96, -283.1) * mm, "end": v(-191.3, -281.8) * mm});
            skLineSegment(sketch, "E701", {"start": v(-191.3, -281.8) * mm, "end": v(-190.87, -280.39) * mm});
            skLineSegment(sketch, "E702", {"start": v(-190.87, -280.39) * mm, "end": v(-190.44, -278.87) * mm});
            skLineSegment(sketch, "E703", {"start": v(-190.44, -278.87) * mm, "end": v(-190.23, -277.47) * mm});
            skLineSegment(sketch, "E704", {"start": v(-190.23, -277.47) * mm, "end": v(-190.23, -274.44) * mm});
            skLineSegment(sketch, "E705", {"start": v(-190.23, -274.44) * mm, "end": v(-190.44, -273.03) * mm});
            skLineSegment(sketch, "E706", {"start": v(-190.44, -273.03) * mm, "end": v(-190.87, -271.51) * mm});
            skLineSegment(sketch, "E707", {"start": v(-190.87, -271.51) * mm, "end": v(-191.3, -270.1) * mm});
            skLineSegment(sketch, "E708", {"start": v(-191.3, -270.1) * mm, "end": v(-191.96, -268.8) * mm});
            skLineSegment(sketch, "E709", {"start": v(-191.96, -268.8) * mm, "end": v(-192.6, -267.5) * mm});
            skLineSegment(sketch, "E710", {"start": v(-192.6, -267.5) * mm, "end": v(-193.47, -266.32) * mm});
            skLineSegment(sketch, "E711", {"start": v(-193.47, -266.32) * mm, "end": v(-194.56, -265.56) * mm});
            skLineSegment(sketch, "E712", {"start": v(-194.56, -265.56) * mm, "end": v(-195.75, -264.91) * mm});
            skLineSegment(sketch, "E713", {"start": v(-195.75, -264.91) * mm, "end": v(-196.93, -264.37) * mm});
            skLineSegment(sketch, "E714", {"start": v(-196.93, -264.37) * mm, "end": v(-198.24, -263.94) * mm});
            skLineSegment(sketch, "E715", {"start": v(-198.24, -263.94) * mm, "end": v(-199.54, -263.72) * mm});
            skLineSegment(sketch, "E716", {"start": v(-199.54, -263.72) * mm, "end": v(-200.83, -263.61) * mm});
            skLineSegment(sketch, "E717", {"start": v(-167.82, -263.61) * mm, "end": v(-181.57, -263.61) * mm});
            skLineSegment(sketch, "E718", {"start": v(-181.57, -263.61) * mm, "end": v(-181.57, -305.5) * mm});
            skLineSegment(sketch, "E719", {"start": v(-181.57, -305.5) * mm, "end": v(-167.82, -305.5) * mm});
            skLineSegment(sketch, "E720", {"start": v(-167.82, -305.5) * mm, "end": v(-167.82, -299.65) * mm});
            skLineSegment(sketch, "E721", {"start": v(-167.82, -299.65) * mm, "end": v(-175.83, -299.65) * mm});
            skLineSegment(sketch, "E722", {"start": v(-175.83, -299.65) * mm, "end": v(-175.83, -287.64) * mm});
            skLineSegment(sketch, "E723", {"start": v(-175.83, -287.64) * mm, "end": v(-170.1, -287.64) * mm});
            skLineSegment(sketch, "E724", {"start": v(-170.1, -287.64) * mm, "end": v(-170.1, -281.36) * mm});
            skLineSegment(sketch, "E725", {"start": v(-170.1, -281.36) * mm, "end": v(-175.83, -281.36) * mm});
            skLineSegment(sketch, "E726", {"start": v(-175.83, -281.36) * mm, "end": v(-175.83, -270.32) * mm});
            skLineSegment(sketch, "E727", {"start": v(-175.83, -270.32) * mm, "end": v(-167.82, -270.32) * mm});
            skLineSegment(sketch, "E728", {"start": v(-167.82, -270.32) * mm, "end": v(-167.82, -263.61) * mm});
            skLineSegment(sketch, "E729", {"start": v(-41.72, -263.61) * mm, "end": v(-55.47, -263.61) * mm});
            skLineSegment(sketch, "E730", {"start": v(-55.47, -263.61) * mm, "end": v(-55.47, -305.5) * mm});
            skLineSegment(sketch, "E731", {"start": v(-55.47, -305.5) * mm, "end": v(-41.72, -305.5) * mm});
            skLineSegment(sketch, "E732", {"start": v(-41.72, -305.5) * mm, "end": v(-41.72, -299.65) * mm});
            skLineSegment(sketch, "E733", {"start": v(-41.72, -299.65) * mm, "end": v(-49.73, -299.65) * mm});
            skLineSegment(sketch, "E734", {"start": v(-49.73, -299.65) * mm, "end": v(-49.73, -287.64) * mm});
            skLineSegment(sketch, "E735", {"start": v(-49.73, -287.64) * mm, "end": v(-44, -287.64) * mm});
            skLineSegment(sketch, "E736", {"start": v(-44, -287.64) * mm, "end": v(-44, -281.36) * mm});
            skLineSegment(sketch, "E737", {"start": v(-44, -281.36) * mm, "end": v(-49.73, -281.36) * mm});
            skLineSegment(sketch, "E738", {"start": v(-49.73, -281.36) * mm, "end": v(-49.73, -270.32) * mm});
            skLineSegment(sketch, "E739", {"start": v(-49.73, -270.32) * mm, "end": v(-41.72, -270.32) * mm});
            skLineSegment(sketch, "E740", {"start": v(-41.72, -270.32) * mm, "end": v(-41.72, -263.61) * mm});
            skLineSegment(sketch, "E741", {"start": v(31.01, -263.61) * mm, "end": v(17.26, -263.61) * mm});
            skLineSegment(sketch, "E742", {"start": v(17.26, -263.61) * mm, "end": v(17.26, -305.5) * mm});
            skLineSegment(sketch, "E743", {"start": v(17.26, -305.5) * mm, "end": v(31.01, -305.5) * mm});
            skLineSegment(sketch, "E744", {"start": v(31.01, -305.5) * mm, "end": v(31.01, -299.65) * mm});
            skLineSegment(sketch, "E745", {"start": v(31.01, -299.65) * mm, "end": v(23, -299.65) * mm});
            skLineSegment(sketch, "E746", {"start": v(23, -299.65) * mm, "end": v(23, -287.64) * mm});
            skLineSegment(sketch, "E747", {"start": v(23, -287.64) * mm, "end": v(28.74, -287.64) * mm});
            skLineSegment(sketch, "E748", {"start": v(28.74, -287.64) * mm, "end": v(28.74, -281.36) * mm});
            skLineSegment(sketch, "E749", {"start": v(28.74, -281.36) * mm, "end": v(23, -281.36) * mm});
            skLineSegment(sketch, "E750", {"start": v(23, -281.36) * mm, "end": v(23, -270.32) * mm});
            skLineSegment(sketch, "E751", {"start": v(23, -270.32) * mm, "end": v(31.01, -270.32) * mm});
            skLineSegment(sketch, "E752", {"start": v(31.01, -270.32) * mm, "end": v(31.01, -263.61) * mm});
            skLineSegment(sketch, "E753", {"start": v(92.38, -263.61) * mm, "end": v(78.63, -263.61) * mm});
            skLineSegment(sketch, "E754", {"start": v(78.63, -263.61) * mm, "end": v(78.63, -305.5) * mm});
            skLineSegment(sketch, "E755", {"start": v(78.63, -305.5) * mm, "end": v(92.38, -305.5) * mm});
            skLineSegment(sketch, "E756", {"start": v(92.38, -305.5) * mm, "end": v(92.38, -299.65) * mm});
            skLineSegment(sketch, "E757", {"start": v(92.38, -299.65) * mm, "end": v(84.37, -299.65) * mm});
            skLineSegment(sketch, "E758", {"start": v(84.37, -299.65) * mm, "end": v(84.37, -287.64) * mm});
            skLineSegment(sketch, "E759", {"start": v(84.37, -287.64) * mm, "end": v(90.1, -287.64) * mm});
            skLineSegment(sketch, "E760", {"start": v(90.1, -287.64) * mm, "end": v(90.1, -281.36) * mm});
            skLineSegment(sketch, "E761", {"start": v(90.1, -281.36) * mm, "end": v(84.37, -281.36) * mm});
            skLineSegment(sketch, "E762", {"start": v(84.37, -281.36) * mm, "end": v(84.37, -270.32) * mm});
            skLineSegment(sketch, "E763", {"start": v(84.37, -270.32) * mm, "end": v(92.38, -270.32) * mm});
            skLineSegment(sketch, "E764", {"start": v(92.38, -270.32) * mm, "end": v(92.38, -263.61) * mm});
            skLineSegment(sketch, "E765", {"start": v(164.47, -263.61) * mm, "end": v(150.72, -263.61) * mm});
            skLineSegment(sketch, "E766", {"start": v(150.72, -263.61) * mm, "end": v(150.72, -305.5) * mm});
            skLineSegment(sketch, "E767", {"start": v(150.72, -305.5) * mm, "end": v(164.47, -305.5) * mm});
            skLineSegment(sketch, "E768", {"start": v(164.47, -305.5) * mm, "end": v(164.47, -299.65) * mm});
            skLineSegment(sketch, "E769", {"start": v(164.47, -299.65) * mm, "end": v(156.46, -299.65) * mm});
            skLineSegment(sketch, "E770", {"start": v(156.46, -299.65) * mm, "end": v(156.46, -287.64) * mm});
            skLineSegment(sketch, "E771", {"start": v(156.46, -287.64) * mm, "end": v(162.2, -287.64) * mm});
            skLineSegment(sketch, "E772", {"start": v(162.2, -287.64) * mm, "end": v(162.2, -281.36) * mm});
            skLineSegment(sketch, "E773", {"start": v(162.2, -281.36) * mm, "end": v(156.46, -281.36) * mm});
            skLineSegment(sketch, "E774", {"start": v(156.46, -281.36) * mm, "end": v(156.46, -270.32) * mm});
            skLineSegment(sketch, "E775", {"start": v(156.46, -270.32) * mm, "end": v(164.47, -270.32) * mm});
            skLineSegment(sketch, "E776", {"start": v(164.47, -270.32) * mm, "end": v(164.47, -263.61) * mm});
            skLineSegment(sketch, "E777", {"start": v(-159.7, -297.7) * mm, "end": v(-159.7, -298.79) * mm});
            skLineSegment(sketch, "E778", {"start": v(-159.7, -298.79) * mm, "end": v(-159.49, -299.76) * mm});
            skLineSegment(sketch, "E779", {"start": v(-159.49, -299.76) * mm, "end": v(-159.16, -300.74) * mm});
            skLineSegment(sketch, "E780", {"start": v(-159.16, -300.74) * mm, "end": v(-158.73, -301.6) * mm});
            skLineSegment(sketch, "E781", {"start": v(-158.73, -301.6) * mm, "end": v(-158.08, -302.47) * mm});
            skLineSegment(sketch, "E782", {"start": v(-158.08, -302.47) * mm, "end": v(-157.43, -303.23) * mm});
            skLineSegment(sketch, "E783", {"start": v(-157.43, -303.23) * mm, "end": v(-156.67, -303.98) * mm});
            skLineSegment(sketch, "E784", {"start": v(-156.67, -303.98) * mm, "end": v(-155.8, -304.53) * mm});
            skLineSegment(sketch, "E785", {"start": v(-155.8, -304.53) * mm, "end": v(-154.94, -304.96) * mm});
            skLineSegment(sketch, "E786", {"start": v(-154.94, -304.96) * mm, "end": v(-153.97, -305.28) * mm});
            skLineSegment(sketch, "E787", {"start": v(-153.97, -305.28) * mm, "end": v(-152.88, -305.5) * mm});
            skLineSegment(sketch, "E788", {"start": v(-152.88, -305.5) * mm, "end": v(-150.94, -305.5) * mm});
            skLineSegment(sketch, "E789", {"start": v(-150.94, -305.5) * mm, "end": v(-149.85, -305.28) * mm});
            skLineSegment(sketch, "E790", {"start": v(-149.85, -305.28) * mm, "end": v(-148.88, -304.96) * mm});
            skLineSegment(sketch, "E791", {"start": v(-148.88, -304.96) * mm, "end": v(-148.01, -304.53) * mm});
            skLineSegment(sketch, "E792", {"start": v(-148.01, -304.53) * mm, "end": v(-147.15, -303.98) * mm});
            skLineSegment(sketch, "E793", {"start": v(-147.15, -303.98) * mm, "end": v(-146.39, -303.23) * mm});
            skLineSegment(sketch, "E794", {"start": v(-146.39, -303.23) * mm, "end": v(-145.74, -302.47) * mm});
            skLineSegment(sketch, "E795", {"start": v(-145.74, -302.47) * mm, "end": v(-144.66, -300.74) * mm});
            skLineSegment(sketch, "E796", {"start": v(-144.66, -300.74) * mm, "end": v(-144.33, -299.76) * mm});
            skLineSegment(sketch, "E797", {"start": v(-144.33, -299.76) * mm, "end": v(-144.22, -298.79) * mm});
            skLineSegment(sketch, "E798", {"start": v(-144.22, -298.79) * mm, "end": v(-144.12, -297.7) * mm});
            skLineSegment(sketch, "E799", {"start": v(-144.12, -297.7) * mm, "end": v(-144.12, -291.21) * mm});
            skLineSegment(sketch, "E800", {"start": v(-144.12, -291.21) * mm, "end": v(-149.74, -291.21) * mm});
            skLineSegment(sketch, "E801", {"start": v(-149.74, -291.21) * mm, "end": v(-149.74, -298.14) * mm});
            skLineSegment(sketch, "E802", {"start": v(-154.07, -298.14) * mm, "end": v(-154.07, -298.68) * mm});
            skLineSegment(sketch, "E803", {"start": v(-154.07, -298.68) * mm, "end": v(-153.86, -299.11) * mm});
            skLineSegment(sketch, "E804", {"start": v(-153.86, -299.11) * mm, "end": v(-153.64, -299.55) * mm});
            skLineSegment(sketch, "E805", {"start": v(-153.64, -299.55) * mm, "end": v(-153.32, -299.87) * mm});
            skLineSegment(sketch, "E806", {"start": v(-153.32, -299.87) * mm, "end": v(-152.88, -300.09) * mm});
            skLineSegment(sketch, "E807", {"start": v(-152.88, -300.09) * mm, "end": v(-152.45, -300.3) * mm});
            skLineSegment(sketch, "E808", {"start": v(-152.45, -300.3) * mm, "end": v(-151.48, -300.3) * mm});
            skLineSegment(sketch, "E809", {"start": v(-151.48, -300.3) * mm, "end": v(-150.94, -300.09) * mm});
            skLineSegment(sketch, "E810", {"start": v(-150.94, -300.09) * mm, "end": v(-150.61, -299.87) * mm});
            skLineSegment(sketch, "E811", {"start": v(-150.61, -299.87) * mm, "end": v(-150.18, -299.55) * mm});
            skLineSegment(sketch, "E812", {"start": v(-150.18, -299.55) * mm, "end": v(-149.96, -299.11) * mm});
            skLineSegment(sketch, "E813", {"start": v(-149.96, -299.11) * mm, "end": v(-149.74, -298.68) * mm});
            skLineSegment(sketch, "E814", {"start": v(-149.74, -298.68) * mm, "end": v(-149.74, -298.14) * mm});
            skLineSegment(sketch, "E815", {"start": v(-154.07, -298.14) * mm, "end": v(-154.07, -270.97) * mm});
            skLineSegment(sketch, "E816", {"start": v(-149.74, -270.97) * mm, "end": v(-149.74, -270.43) * mm});
            skLineSegment(sketch, "E817", {"start": v(-149.74, -270.43) * mm, "end": v(-149.96, -270) * mm});
            skLineSegment(sketch, "E818", {"start": v(-149.96, -270) * mm, "end": v(-150.18, -269.57) * mm});
            skLineSegment(sketch, "E819", {"start": v(-150.18, -269.57) * mm, "end": v(-150.61, -269.24) * mm});
            skLineSegment(sketch, "E820", {"start": v(-150.61, -269.24) * mm, "end": v(-150.94, -269.02) * mm});
            skLineSegment(sketch, "E821", {"start": v(-150.94, -269.02) * mm, "end": v(-151.48, -268.8) * mm});
            skLineSegment(sketch, "E822", {"start": v(-151.48, -268.8) * mm, "end": v(-152.45, -268.8) * mm});
            skLineSegment(sketch, "E823", {"start": v(-152.45, -268.8) * mm, "end": v(-153.32, -269.24) * mm});
            skLineSegment(sketch, "E824", {"start": v(-153.32, -269.24) * mm, "end": v(-153.64, -269.57) * mm});
            skLineSegment(sketch, "E825", {"start": v(-153.64, -269.57) * mm, "end": v(-153.86, -270) * mm});
            skLineSegment(sketch, "E826", {"start": v(-153.86, -270) * mm, "end": v(-154.07, -270.43) * mm});
            skLineSegment(sketch, "E827", {"start": v(-154.07, -270.43) * mm, "end": v(-154.07, -270.97) * mm});
            skLineSegment(sketch, "E828", {"start": v(-149.74, -270.97) * mm, "end": v(-149.74, -277.9) * mm});
            skLineSegment(sketch, "E829", {"start": v(-149.74, -277.9) * mm, "end": v(-144.12, -277.9) * mm});
            skLineSegment(sketch, "E830", {"start": v(-144.12, -277.9) * mm, "end": v(-144.12, -271.4) * mm});
            skLineSegment(sketch, "E831", {"start": v(-144.12, -271.4) * mm, "end": v(-144.22, -270.32) * mm});
            skLineSegment(sketch, "E832", {"start": v(-144.22, -270.32) * mm, "end": v(-144.33, -269.35) * mm});
            skLineSegment(sketch, "E833", {"start": v(-144.33, -269.35) * mm, "end": v(-144.66, -268.37) * mm});
            skLineSegment(sketch, "E834", {"start": v(-144.66, -268.37) * mm, "end": v(-145.2, -267.5) * mm});
            skLineSegment(sketch, "E835", {"start": v(-145.2, -267.5) * mm, "end": v(-145.74, -266.64) * mm});
            skLineSegment(sketch, "E836", {"start": v(-145.74, -266.64) * mm, "end": v(-146.39, -265.88) * mm});
            skLineSegment(sketch, "E837", {"start": v(-146.39, -265.88) * mm, "end": v(-147.15, -265.13) * mm});
            skLineSegment(sketch, "E838", {"start": v(-147.15, -265.13) * mm, "end": v(-148.01, -264.59) * mm});
            skLineSegment(sketch, "E839", {"start": v(-148.01, -264.59) * mm, "end": v(-148.88, -264.15) * mm});
            skLineSegment(sketch, "E840", {"start": v(-148.88, -264.15) * mm, "end": v(-149.85, -263.83) * mm});
            skLineSegment(sketch, "E841", {"start": v(-149.85, -263.83) * mm, "end": v(-150.94, -263.61) * mm});
            skLineSegment(sketch, "E842", {"start": v(-150.94, -263.61) * mm, "end": v(-152.88, -263.61) * mm});
            skLineSegment(sketch, "E843", {"start": v(-152.88, -263.61) * mm, "end": v(-153.97, -263.83) * mm});
            skLineSegment(sketch, "E844", {"start": v(-153.97, -263.83) * mm, "end": v(-154.94, -264.15) * mm});
            skLineSegment(sketch, "E845", {"start": v(-154.94, -264.15) * mm, "end": v(-155.8, -264.59) * mm});
            skLineSegment(sketch, "E846", {"start": v(-155.8, -264.59) * mm, "end": v(-156.67, -265.13) * mm});
            skLineSegment(sketch, "E847", {"start": v(-156.67, -265.13) * mm, "end": v(-157.43, -265.88) * mm});
            skLineSegment(sketch, "E848", {"start": v(-157.43, -265.88) * mm, "end": v(-158.08, -266.64) * mm});
            skLineSegment(sketch, "E849", {"start": v(-158.08, -266.64) * mm, "end": v(-158.73, -267.5) * mm});
            skLineSegment(sketch, "E850", {"start": v(-158.73, -267.5) * mm, "end": v(-159.16, -268.37) * mm});
            skLineSegment(sketch, "E851", {"start": v(-159.16, -268.37) * mm, "end": v(-159.49, -269.35) * mm});
            skLineSegment(sketch, "E852", {"start": v(-159.49, -269.35) * mm, "end": v(-159.7, -270.32) * mm});
            skLineSegment(sketch, "E853", {"start": v(-159.7, -270.32) * mm, "end": v(-159.7, -271.4) * mm});
            skLineSegment(sketch, "E854", {"start": v(-159.7, -271.4) * mm, "end": v(-159.7, -297.7) * mm});
            skLineSegment(sketch, "E855", {"start": v(-119.87, -263.61) * mm, "end": v(-136.97, -263.61) * mm});
            skLineSegment(sketch, "E856", {"start": v(-136.97, -263.61) * mm, "end": v(-136.97, -270.32) * mm});
            skLineSegment(sketch, "E857", {"start": v(-136.97, -270.32) * mm, "end": v(-131.56, -270.32) * mm});
            skLineSegment(sketch, "E858", {"start": v(-131.56, -270.32) * mm, "end": v(-131.56, -305.5) * mm});
            skLineSegment(sketch, "E859", {"start": v(-131.56, -305.5) * mm, "end": v(-125.6, -305.5) * mm});
            skLineSegment(sketch, "E860", {"start": v(-125.6, -305.5) * mm, "end": v(-125.6, -270.32) * mm});
            skLineSegment(sketch, "E861", {"start": v(-125.6, -270.32) * mm, "end": v(-119.87, -270.32) * mm});
            skLineSegment(sketch, "E862", {"start": v(-119.87, -270.32) * mm, "end": v(-119.87, -263.61) * mm});
            skLineSegment(sketch, "E863", {"start": v(9.58, -263.61) * mm, "end": v(-7.52, -263.61) * mm});
            skLineSegment(sketch, "E864", {"start": v(-7.52, -263.61) * mm, "end": v(-7.52, -270.32) * mm});
            skLineSegment(sketch, "E865", {"start": v(-7.52, -270.32) * mm, "end": v(-2.1, -270.32) * mm});
            skLineSegment(sketch, "E866", {"start": v(-2.1, -270.32) * mm, "end": v(-2.1, -305.5) * mm});
            skLineSegment(sketch, "E867", {"start": v(-2.1, -305.5) * mm, "end": v(3.74, -305.5) * mm});
            skLineSegment(sketch, "E868", {"start": v(3.74, -305.5) * mm, "end": v(3.74, -270.32) * mm});
            skLineSegment(sketch, "E869", {"start": v(3.74, -270.32) * mm, "end": v(9.58, -270.32) * mm});
            skLineSegment(sketch, "E870", {"start": v(9.58, -270.32) * mm, "end": v(9.58, -263.61) * mm});
            skLineSegment(sketch, "E871", {"start": v(110.35, -270.97) * mm, "end": v(110.35, -274.33) * mm});
            skLineSegment(sketch, "E872", {"start": v(110.35, -274.33) * mm, "end": v(116.08, -274.33) * mm});
            skLineSegment(sketch, "E873", {"start": v(116.08, -274.33) * mm, "end": v(116.08, -271.4) * mm});
            skLineSegment(sketch, "E874", {"start": v(116.08, -271.4) * mm, "end": v(115.98, -270.32) * mm});
            skLineSegment(sketch, "E875", {"start": v(115.98, -270.32) * mm, "end": v(115.76, -269.35) * mm});
            skLineSegment(sketch, "E876", {"start": v(115.76, -269.35) * mm, "end": v(115.43, -268.37) * mm});
            skLineSegment(sketch, "E877", {"start": v(115.43, -268.37) * mm, "end": v(115, -267.5) * mm});
            skLineSegment(sketch, "E878", {"start": v(115, -267.5) * mm, "end": v(114.46, -266.64) * mm});
            skLineSegment(sketch, "E879", {"start": v(114.46, -266.64) * mm, "end": v(113.7, -265.88) * mm});
            skLineSegment(sketch, "E880", {"start": v(113.7, -265.88) * mm, "end": v(112.95, -265.24) * mm});
            skLineSegment(sketch, "E881", {"start": v(112.95, -265.24) * mm, "end": v(112.08, -264.59) * mm});
            skLineSegment(sketch, "E882", {"start": v(112.08, -264.59) * mm, "end": v(111.21, -264.15) * mm});
            skLineSegment(sketch, "E883", {"start": v(111.21, -264.15) * mm, "end": v(110.24, -263.83) * mm});
            skLineSegment(sketch, "E884", {"start": v(110.24, -263.83) * mm, "end": v(109.26, -263.61) * mm});
            skLineSegment(sketch, "E885", {"start": v(109.26, -263.61) * mm, "end": v(107.2, -263.61) * mm});
            skLineSegment(sketch, "E886", {"start": v(107.2, -263.61) * mm, "end": v(106.23, -263.83) * mm});
            skLineSegment(sketch, "E887", {"start": v(106.23, -263.83) * mm, "end": v(105.26, -264.15) * mm});
            skLineSegment(sketch, "E888", {"start": v(105.26, -264.15) * mm, "end": v(104.29, -264.59) * mm});
            skLineSegment(sketch, "E889", {"start": v(104.29, -264.59) * mm, "end": v(103.53, -265.24) * mm});
            skLineSegment(sketch, "E890", {"start": v(103.53, -265.24) * mm, "end": v(102.67, -265.88) * mm});
            skLineSegment(sketch, "E891", {"start": v(102.67, -265.88) * mm, "end": v(102.02, -266.64) * mm});
            skLineSegment(sketch, "E892", {"start": v(102.02, -266.64) * mm, "end": v(101.47, -267.5) * mm});
            skLineSegment(sketch, "E893", {"start": v(101.47, -267.5) * mm, "end": v(101.04, -268.37) * mm});
            skLineSegment(sketch, "E894", {"start": v(101.04, -268.37) * mm, "end": v(100.72, -269.35) * mm});
            skLineSegment(sketch, "E895", {"start": v(100.72, -269.35) * mm, "end": v(100.5, -270.32) * mm});
            skLineSegment(sketch, "E896", {"start": v(100.5, -270.32) * mm, "end": v(100.39, -271.4) * mm});
            skLineSegment(sketch, "E897", {"start": v(100.39, -271.4) * mm, "end": v(100.39, -274.33) * mm});
            skLineSegment(sketch, "E898", {"start": v(100.39, -274.33) * mm, "end": v(101.04, -276.28) * mm});
            skLineSegment(sketch, "E899", {"start": v(101.04, -276.28) * mm, "end": v(101.69, -278.22) * mm});
            skLineSegment(sketch, "E900", {"start": v(101.69, -278.22) * mm, "end": v(102.56, -280.06) * mm});
            skLineSegment(sketch, "E901", {"start": v(102.56, -280.06) * mm, "end": v(103.53, -281.9) * mm});
            skLineSegment(sketch, "E902", {"start": v(103.53, -281.9) * mm, "end": v(104.72, -283.64) * mm});
            skLineSegment(sketch, "E903", {"start": v(104.72, -283.64) * mm, "end": v(105.9, -285.26) * mm});
            skLineSegment(sketch, "E904", {"start": v(110.78, -293.49) * mm, "end": v(108.4, -289.37) * mm});
            skLineSegment(sketch, "E905", {"start": v(108.4, -289.37) * mm, "end": v(105.9, -285.26) * mm});
            skLineSegment(sketch, "E906", {"start": v(110.78, -293.49) * mm, "end": v(110.78, -297.49) * mm});
            skLineSegment(sketch, "E907", {"start": v(105.05, -298.14) * mm, "end": v(105.26, -298.68) * mm});
            skLineSegment(sketch, "E908", {"start": v(105.26, -298.68) * mm, "end": v(105.59, -299.22) * mm});
            skLineSegment(sketch, "E909", {"start": v(105.59, -299.22) * mm, "end": v(105.9, -299.65) * mm});
            skLineSegment(sketch, "E910", {"start": v(105.9, -299.65) * mm, "end": v(106.34, -299.98) * mm});
            skLineSegment(sketch, "E911", {"start": v(106.34, -299.98) * mm, "end": v(106.88, -300.2) * mm});
            skLineSegment(sketch, "E912", {"start": v(106.88, -300.2) * mm, "end": v(107.43, -300.3) * mm});
            skLineSegment(sketch, "E913", {"start": v(107.43, -300.3) * mm, "end": v(107.97, -300.41) * mm});
            skLineSegment(sketch, "E914", {"start": v(107.97, -300.41) * mm, "end": v(108.51, -300.3) * mm});
            skLineSegment(sketch, "E915", {"start": v(108.51, -300.3) * mm, "end": v(109.05, -300.2) * mm});
            skLineSegment(sketch, "E916", {"start": v(109.05, -300.2) * mm, "end": v(109.59, -299.87) * mm});
            skLineSegment(sketch, "E917", {"start": v(109.59, -299.87) * mm, "end": v(110.02, -299.55) * mm});
            skLineSegment(sketch, "E918", {"start": v(110.02, -299.55) * mm, "end": v(110.35, -299.11) * mm});
            skLineSegment(sketch, "E919", {"start": v(110.35, -299.11) * mm, "end": v(110.78, -298.03) * mm});
            skLineSegment(sketch, "E920", {"start": v(110.78, -298.03) * mm, "end": v(110.78, -297.49) * mm});
            skLineSegment(sketch, "E921", {"start": v(105.05, -298.14) * mm, "end": v(105.05, -293.49) * mm});
            skLineSegment(sketch, "E922", {"start": v(105.05, -293.49) * mm, "end": v(99.52, -293.49) * mm});
            skLineSegment(sketch, "E923", {"start": v(99.52, -293.49) * mm, "end": v(99.52, -297.7) * mm});
            skLineSegment(sketch, "E924", {"start": v(99.52, -297.7) * mm, "end": v(99.63, -298.68) * mm});
            skLineSegment(sketch, "E925", {"start": v(99.63, -298.68) * mm, "end": v(99.85, -299.65) * mm});
            skLineSegment(sketch, "E926", {"start": v(99.85, -299.65) * mm, "end": v(100.17, -300.63) * mm});
            skLineSegment(sketch, "E927", {"start": v(100.17, -300.63) * mm, "end": v(100.72, -301.5) * mm});
            skLineSegment(sketch, "E928", {"start": v(100.72, -301.5) * mm, "end": v(101.26, -302.36) * mm});
            skLineSegment(sketch, "E929", {"start": v(101.26, -302.36) * mm, "end": v(101.9, -303.12) * mm});
            skLineSegment(sketch, "E930", {"start": v(101.9, -303.12) * mm, "end": v(102.67, -303.77) * mm});
            skLineSegment(sketch, "E931", {"start": v(102.67, -303.77) * mm, "end": v(103.53, -304.3) * mm});
            skLineSegment(sketch, "E932", {"start": v(103.53, -304.3) * mm, "end": v(104.4, -304.85) * mm});
            skLineSegment(sketch, "E933", {"start": v(104.4, -304.85) * mm, "end": v(105.26, -305.18) * mm});
            skLineSegment(sketch, "E934", {"start": v(105.26, -305.18) * mm, "end": v(106.23, -305.4) * mm});
            skLineSegment(sketch, "E935", {"start": v(106.23, -305.4) * mm, "end": v(107.32, -305.5) * mm});
            skLineSegment(sketch, "E936", {"start": v(107.32, -305.5) * mm, "end": v(108.3, -305.5) * mm});
            skLineSegment(sketch, "E937", {"start": v(108.3, -305.5) * mm, "end": v(109.26, -305.4) * mm});
            skLineSegment(sketch, "E938", {"start": v(109.26, -305.4) * mm, "end": v(110.24, -305.18) * mm});
            skLineSegment(sketch, "E939", {"start": v(110.24, -305.18) * mm, "end": v(111.21, -304.85) * mm});
            skLineSegment(sketch, "E940", {"start": v(111.21, -304.85) * mm, "end": v(112.08, -304.3) * mm});
            skLineSegment(sketch, "E941", {"start": v(112.08, -304.3) * mm, "end": v(112.95, -303.77) * mm});
            skLineSegment(sketch, "E942", {"start": v(112.95, -303.77) * mm, "end": v(114.35, -302.36) * mm});
            skLineSegment(sketch, "E943", {"start": v(114.35, -302.36) * mm, "end": v(114.9, -301.5) * mm});
            skLineSegment(sketch, "E944", {"start": v(114.9, -301.5) * mm, "end": v(115.33, -300.63) * mm});
            skLineSegment(sketch, "E945", {"start": v(115.33, -300.63) * mm, "end": v(115.65, -299.65) * mm});
            skLineSegment(sketch, "E946", {"start": v(115.65, -299.65) * mm, "end": v(115.87, -298.68) * mm});
            skLineSegment(sketch, "E947", {"start": v(115.87, -298.68) * mm, "end": v(116.08, -297.7) * mm});
            skLineSegment(sketch, "E948", {"start": v(116.08, -297.7) * mm, "end": v(116.08, -293.49) * mm});
            skLineSegment(sketch, "E949", {"start": v(116.08, -293.49) * mm, "end": v(115.43, -291.43) * mm});
            skLineSegment(sketch, "E950", {"start": v(115.43, -291.43) * mm, "end": v(114.68, -289.37) * mm});
            skLineSegment(sketch, "E951", {"start": v(114.68, -289.37) * mm, "end": v(113.81, -287.42) * mm});
            skLineSegment(sketch, "E952", {"start": v(113.81, -287.42) * mm, "end": v(112.73, -285.48) * mm});
            skLineSegment(sketch, "E953", {"start": v(112.73, -285.48) * mm, "end": v(111.65, -283.64) * mm});
            skLineSegment(sketch, "E954", {"start": v(111.65, -283.64) * mm, "end": v(110.35, -281.9) * mm});
            skLineSegment(sketch, "E955", {"start": v(106.02, -274.33) * mm, "end": v(107, -276.38) * mm});
            skLineSegment(sketch, "E956", {"start": v(107, -276.38) * mm, "end": v(107.97, -278.22) * mm});
            skLineSegment(sketch, "E957", {"start": v(107.97, -278.22) * mm, "end": v(109.16, -280.06) * mm});
            skLineSegment(sketch, "E958", {"start": v(109.16, -280.06) * mm, "end": v(110.35, -281.9) * mm});
            skLineSegment(sketch, "E959", {"start": v(106.02, -274.33) * mm, "end": v(106.02, -270.97) * mm});
            skLineSegment(sketch, "E960", {"start": v(110.35, -270.97) * mm, "end": v(110.35, -270.43) * mm});
            skLineSegment(sketch, "E961", {"start": v(110.35, -270.43) * mm, "end": v(110.13, -270) * mm});
            skLineSegment(sketch, "E962", {"start": v(110.13, -270) * mm, "end": v(109.91, -269.57) * mm});
            skLineSegment(sketch, "E963", {"start": v(109.91, -269.57) * mm, "end": v(109.59, -269.24) * mm});
            skLineSegment(sketch, "E964", {"start": v(109.59, -269.24) * mm, "end": v(109.16, -269.02) * mm});
            skLineSegment(sketch, "E965", {"start": v(109.16, -269.02) * mm, "end": v(108.73, -268.8) * mm});
            skLineSegment(sketch, "E966", {"start": v(108.73, -268.8) * mm, "end": v(107.75, -268.8) * mm});
            skLineSegment(sketch, "E967", {"start": v(107.75, -268.8) * mm, "end": v(107.32, -269.02) * mm});
            skLineSegment(sketch, "E968", {"start": v(107.32, -269.02) * mm, "end": v(106.88, -269.24) * mm});
            skLineSegment(sketch, "E969", {"start": v(106.88, -269.24) * mm, "end": v(106.56, -269.57) * mm});
            skLineSegment(sketch, "E970", {"start": v(106.56, -269.57) * mm, "end": v(106.23, -270) * mm});
            skLineSegment(sketch, "E971", {"start": v(106.23, -270) * mm, "end": v(106.13, -270.43) * mm});
            skLineSegment(sketch, "E972", {"start": v(106.13, -270.43) * mm, "end": v(106.02, -270.97) * mm});
            skLineSegment(sketch, "E973", {"start": v(242.94, -270.97) * mm, "end": v(242.94, -274.33) * mm});
            skLineSegment(sketch, "E974", {"start": v(242.94, -274.33) * mm, "end": v(248.57, -274.33) * mm});
            skLineSegment(sketch, "E975", {"start": v(248.57, -274.33) * mm, "end": v(248.57, -271.4) * mm});
            skLineSegment(sketch, "E976", {"start": v(248.57, -271.4) * mm, "end": v(248.57, -270.32) * mm});
            skLineSegment(sketch, "E977", {"start": v(248.57, -270.32) * mm, "end": v(248.35, -269.35) * mm});
            skLineSegment(sketch, "E978", {"start": v(248.35, -269.35) * mm, "end": v(248.03, -268.37) * mm});
            skLineSegment(sketch, "E979", {"start": v(248.03, -268.37) * mm, "end": v(247.48, -267.5) * mm});
            skLineSegment(sketch, "E980", {"start": v(247.48, -267.5) * mm, "end": v(246.94, -266.64) * mm});
            skLineSegment(sketch, "E981", {"start": v(246.94, -266.64) * mm, "end": v(246.3, -265.88) * mm});
            skLineSegment(sketch, "E982", {"start": v(246.3, -265.88) * mm, "end": v(245.54, -265.24) * mm});
            skLineSegment(sketch, "E983", {"start": v(245.54, -265.24) * mm, "end": v(244.67, -264.59) * mm});
            skLineSegment(sketch, "E984", {"start": v(244.67, -264.59) * mm, "end": v(243.8, -264.15) * mm});
            skLineSegment(sketch, "E985", {"start": v(243.8, -264.15) * mm, "end": v(242.83, -263.83) * mm});
            skLineSegment(sketch, "E986", {"start": v(242.83, -263.83) * mm, "end": v(241.75, -263.61) * mm});
            skLineSegment(sketch, "E987", {"start": v(241.75, -263.61) * mm, "end": v(239.8, -263.61) * mm});
            skLineSegment(sketch, "E988", {"start": v(239.8, -263.61) * mm, "end": v(238.72, -263.83) * mm});
            skLineSegment(sketch, "E989", {"start": v(238.72, -263.83) * mm, "end": v(237.74, -264.15) * mm});
            skLineSegment(sketch, "E990", {"start": v(237.74, -264.15) * mm, "end": v(236.88, -264.59) * mm});
            skLineSegment(sketch, "E991", {"start": v(236.88, -264.59) * mm, "end": v(236.01, -265.24) * mm});
            skLineSegment(sketch, "E992", {"start": v(236.01, -265.24) * mm, "end": v(235.25, -265.88) * mm});
            skLineSegment(sketch, "E993", {"start": v(235.25, -265.88) * mm, "end": v(234.6, -266.64) * mm});
            skLineSegment(sketch, "E994", {"start": v(234.6, -266.64) * mm, "end": v(234.07, -267.5) * mm});
            skLineSegment(sketch, "E995", {"start": v(234.07, -267.5) * mm, "end": v(233.52, -268.37) * mm});
            skLineSegment(sketch, "E996", {"start": v(233.52, -268.37) * mm, "end": v(233.2, -269.35) * mm});
            skLineSegment(sketch, "E997", {"start": v(233.2, -269.35) * mm, "end": v(233.09, -270.32) * mm});
            skLineSegment(sketch, "E998", {"start": v(233.09, -270.32) * mm, "end": v(232.98, -271.4) * mm});
            skLineSegment(sketch, "E999", {"start": v(232.98, -271.4) * mm, "end": v(232.98, -274.33) * mm});
            skLineSegment(sketch, "E1000", {"start": v(232.98, -274.33) * mm, "end": v(233.52, -276.28) * mm});
            skLineSegment(sketch, "E1001", {"start": v(233.52, -276.28) * mm, "end": v(234.28, -278.22) * mm});
            skLineSegment(sketch, "E1002", {"start": v(234.28, -278.22) * mm, "end": v(235.14, -280.06) * mm});
            skLineSegment(sketch, "E1003", {"start": v(235.14, -280.06) * mm, "end": v(236.12, -281.9) * mm});
            skLineSegment(sketch, "E1004", {"start": v(236.12, -281.9) * mm, "end": v(237.2, -283.64) * mm});
            skLineSegment(sketch, "E1005", {"start": v(237.2, -283.64) * mm, "end": v(238.5, -285.26) * mm});
            skLineSegment(sketch, "E1006", {"start": v(243.37, -293.49) * mm, "end": v(241, -289.37) * mm});
            skLineSegment(sketch, "E1007", {"start": v(241, -289.37) * mm, "end": v(238.5, -285.26) * mm});
            skLineSegment(sketch, "E1008", {"start": v(243.37, -293.49) * mm, "end": v(243.37, -297.49) * mm});
            skLineSegment(sketch, "E1009", {"start": v(237.63, -298.14) * mm, "end": v(237.85, -298.68) * mm});
            skLineSegment(sketch, "E1010", {"start": v(237.85, -298.68) * mm, "end": v(238.07, -299.22) * mm});
            skLineSegment(sketch, "E1011", {"start": v(238.07, -299.22) * mm, "end": v(238.5, -299.65) * mm});
            skLineSegment(sketch, "E1012", {"start": v(238.5, -299.65) * mm, "end": v(238.93, -299.98) * mm});
            skLineSegment(sketch, "E1013", {"start": v(238.93, -299.98) * mm, "end": v(239.48, -300.2) * mm});
            skLineSegment(sketch, "E1014", {"start": v(239.48, -300.2) * mm, "end": v(240.02, -300.3) * mm});
            skLineSegment(sketch, "E1015", {"start": v(240.02, -300.3) * mm, "end": v(240.55, -300.41) * mm});
            skLineSegment(sketch, "E1016", {"start": v(240.55, -300.41) * mm, "end": v(241.1, -300.3) * mm});
            skLineSegment(sketch, "E1017", {"start": v(241.1, -300.3) * mm, "end": v(241.64, -300.2) * mm});
            skLineSegment(sketch, "E1018", {"start": v(241.64, -300.2) * mm, "end": v(242.07, -299.87) * mm});
            skLineSegment(sketch, "E1019", {"start": v(242.07, -299.87) * mm, "end": v(242.5, -299.55) * mm});
            skLineSegment(sketch, "E1020", {"start": v(242.5, -299.55) * mm, "end": v(242.94, -299.11) * mm});
            skLineSegment(sketch, "E1021", {"start": v(242.94, -299.11) * mm, "end": v(243.16, -298.57) * mm});
            skLineSegment(sketch, "E1022", {"start": v(243.16, -298.57) * mm, "end": v(243.37, -297.49) * mm});
            skLineSegment(sketch, "E1023", {"start": v(237.63, -298.14) * mm, "end": v(237.63, -293.49) * mm});
            skLineSegment(sketch, "E1024", {"start": v(237.63, -293.49) * mm, "end": v(232.12, -293.49) * mm});
            skLineSegment(sketch, "E1025", {"start": v(232.12, -293.49) * mm, "end": v(232.12, -297.7) * mm});
            skLineSegment(sketch, "E1026", {"start": v(232.12, -297.7) * mm, "end": v(232.22, -298.68) * mm});
            skLineSegment(sketch, "E1027", {"start": v(232.22, -298.68) * mm, "end": v(232.44, -299.65) * mm});
            skLineSegment(sketch, "E1028", {"start": v(232.44, -299.65) * mm, "end": v(232.76, -300.63) * mm});
            skLineSegment(sketch, "E1029", {"start": v(232.76, -300.63) * mm, "end": v(233.2, -301.5) * mm});
            skLineSegment(sketch, "E1030", {"start": v(233.2, -301.5) * mm, "end": v(233.85, -302.36) * mm});
            skLineSegment(sketch, "E1031", {"start": v(233.85, -302.36) * mm, "end": v(234.5, -303.12) * mm});
            skLineSegment(sketch, "E1032", {"start": v(234.5, -303.12) * mm, "end": v(235.25, -303.77) * mm});
            skLineSegment(sketch, "E1033", {"start": v(235.25, -303.77) * mm, "end": v(236.01, -304.3) * mm});
            skLineSegment(sketch, "E1034", {"start": v(236.01, -304.3) * mm, "end": v(236.88, -304.85) * mm});
            skLineSegment(sketch, "E1035", {"start": v(236.88, -304.85) * mm, "end": v(237.85, -305.18) * mm});
            skLineSegment(sketch, "E1036", {"start": v(237.85, -305.18) * mm, "end": v(238.83, -305.4) * mm});
            skLineSegment(sketch, "E1037", {"start": v(238.83, -305.4) * mm, "end": v(239.8, -305.5) * mm});
            skLineSegment(sketch, "E1038", {"start": v(239.8, -305.5) * mm, "end": v(240.77, -305.5) * mm});
            skLineSegment(sketch, "E1039", {"start": v(240.77, -305.5) * mm, "end": v(241.86, -305.4) * mm});
            skLineSegment(sketch, "E1040", {"start": v(241.86, -305.4) * mm, "end": v(242.83, -305.18) * mm});
            skLineSegment(sketch, "E1041", {"start": v(242.83, -305.18) * mm, "end": v(243.7, -304.85) * mm});
            skLineSegment(sketch, "E1042", {"start": v(243.7, -304.85) * mm, "end": v(244.67, -304.3) * mm});
            skLineSegment(sketch, "E1043", {"start": v(244.67, -304.3) * mm, "end": v(245.43, -303.77) * mm});
            skLineSegment(sketch, "E1044", {"start": v(245.43, -303.77) * mm, "end": v(246.19, -303.12) * mm});
            skLineSegment(sketch, "E1045", {"start": v(246.19, -303.12) * mm, "end": v(246.83, -302.36) * mm});
            skLineSegment(sketch, "E1046", {"start": v(246.83, -302.36) * mm, "end": v(247.38, -301.5) * mm});
            skLineSegment(sketch, "E1047", {"start": v(247.38, -301.5) * mm, "end": v(247.92, -300.63) * mm});
            skLineSegment(sketch, "E1048", {"start": v(247.92, -300.63) * mm, "end": v(248.24, -299.65) * mm});
            skLineSegment(sketch, "E1049", {"start": v(248.24, -299.65) * mm, "end": v(248.46, -298.68) * mm});
            skLineSegment(sketch, "E1050", {"start": v(248.46, -298.68) * mm, "end": v(248.57, -297.7) * mm});
            skLineSegment(sketch, "E1051", {"start": v(248.57, -297.7) * mm, "end": v(248.57, -293.49) * mm});
            skLineSegment(sketch, "E1052", {"start": v(248.57, -293.49) * mm, "end": v(247.92, -291.43) * mm});
            skLineSegment(sketch, "E1053", {"start": v(247.92, -291.43) * mm, "end": v(247.16, -289.37) * mm});
            skLineSegment(sketch, "E1054", {"start": v(247.16, -289.37) * mm, "end": v(246.3, -287.42) * mm});
            skLineSegment(sketch, "E1055", {"start": v(246.3, -287.42) * mm, "end": v(245.32, -285.48) * mm});
            skLineSegment(sketch, "E1056", {"start": v(245.32, -285.48) * mm, "end": v(244.24, -283.64) * mm});
            skLineSegment(sketch, "E1057", {"start": v(244.24, -283.64) * mm, "end": v(242.94, -281.9) * mm});
            skLineSegment(sketch, "E1058", {"start": v(238.6, -274.33) * mm, "end": v(239.48, -276.38) * mm});
            skLineSegment(sketch, "E1059", {"start": v(239.48, -276.38) * mm, "end": v(240.55, -278.22) * mm});
            skLineSegment(sketch, "E1060", {"start": v(240.55, -278.22) * mm, "end": v(241.64, -280.06) * mm});
            skLineSegment(sketch, "E1061", {"start": v(241.64, -280.06) * mm, "end": v(242.94, -281.9) * mm});
            skLineSegment(sketch, "E1062", {"start": v(238.6, -274.33) * mm, "end": v(238.6, -270.97) * mm});
            skLineSegment(sketch, "E1063", {"start": v(242.94, -270.97) * mm, "end": v(242.94, -270.43) * mm});
            skLineSegment(sketch, "E1064", {"start": v(242.94, -270.43) * mm, "end": v(242.72, -270) * mm});
            skLineSegment(sketch, "E1065", {"start": v(242.72, -270) * mm, "end": v(242.5, -269.57) * mm});
            skLineSegment(sketch, "E1066", {"start": v(242.5, -269.57) * mm, "end": v(242.18, -269.24) * mm});
            skLineSegment(sketch, "E1067", {"start": v(242.18, -269.24) * mm, "end": v(241.75, -269.02) * mm});
            skLineSegment(sketch, "E1068", {"start": v(241.75, -269.02) * mm, "end": v(241.2, -268.8) * mm});
            skLineSegment(sketch, "E1069", {"start": v(241.2, -268.8) * mm, "end": v(240.34, -268.8) * mm});
            skLineSegment(sketch, "E1070", {"start": v(240.34, -268.8) * mm, "end": v(239.8, -269.02) * mm});
            skLineSegment(sketch, "E1071", {"start": v(239.8, -269.02) * mm, "end": v(239.48, -269.24) * mm});
            skLineSegment(sketch, "E1072", {"start": v(239.48, -269.24) * mm, "end": v(239.04, -269.57) * mm});
            skLineSegment(sketch, "E1073", {"start": v(239.04, -269.57) * mm, "end": v(238.83, -270) * mm});
            skLineSegment(sketch, "E1074", {"start": v(238.83, -270) * mm, "end": v(238.6, -270.43) * mm});
            skLineSegment(sketch, "E1075", {"start": v(238.6, -270.43) * mm, "end": v(238.6, -270.97) * mm});
            skLineSegment(sketch, "E1076", {"start": v(-105.48, -274.44) * mm, "end": v(-103.1, -290.89) * mm});
            skLineSegment(sketch, "E1077", {"start": v(-103.1, -290.89) * mm, "end": v(-107.86, -290.89) * mm});
            skLineSegment(sketch, "E1078", {"start": v(-107.86, -290.89) * mm, "end": v(-105.48, -274.44) * mm});
            skLineSegment(sketch, "E1079", {"start": v(-101.8, -263.61) * mm, "end": v(-109.16, -263.61) * mm});
            skLineSegment(sketch, "E1080", {"start": v(-109.16, -263.61) * mm, "end": v(-115.22, -305.5) * mm});
            skLineSegment(sketch, "E1081", {"start": v(-115.22, -305.5) * mm, "end": v(-110.02, -305.5) * mm});
            skLineSegment(sketch, "E1082", {"start": v(-110.02, -305.5) * mm, "end": v(-108.72, -297.27) * mm});
            skLineSegment(sketch, "E1083", {"start": v(-108.72, -297.27) * mm, "end": v(-102.12, -297.27) * mm});
            skLineSegment(sketch, "E1084", {"start": v(-102.12, -297.27) * mm, "end": v(-100.93, -305.5) * mm});
            skLineSegment(sketch, "E1085", {"start": v(-100.93, -305.5) * mm, "end": v(-95.63, -305.5) * mm});
            skLineSegment(sketch, "E1086", {"start": v(-95.63, -305.5) * mm, "end": v(-101.8, -263.61) * mm});
            skLineSegment(sketch, "E1087", {"start": v(191.74, -263.61) * mm, "end": v(185.9, -263.61) * mm});
            skLineSegment(sketch, "E1088", {"start": v(185.9, -263.61) * mm, "end": v(185.9, -305.5) * mm});
            skLineSegment(sketch, "E1089", {"start": v(185.9, -305.5) * mm, "end": v(199.75, -305.5) * mm});
            skLineSegment(sketch, "E1090", {"start": v(199.75, -305.5) * mm, "end": v(199.75, -300.3) * mm});
            skLineSegment(sketch, "E1091", {"start": v(199.75, -300.3) * mm, "end": v(191.74, -300.3) * mm});
            skLineSegment(sketch, "E1092", {"start": v(191.74, -300.3) * mm, "end": v(191.74, -263.61) * mm});
            skLineSegment(sketch, "E1093", {"start": v(217.07, -270.97) * mm, "end": v(217.07, -298.14) * mm});
            skLineSegment(sketch, "E1094", {"start": v(212.74, -298.14) * mm, "end": v(212.74, -298.68) * mm});
            skLineSegment(sketch, "E1095", {"start": v(212.74, -298.68) * mm, "end": v(212.96, -299.11) * mm});
            skLineSegment(sketch, "E1096", {"start": v(212.96, -299.11) * mm, "end": v(213.17, -299.55) * mm});
            skLineSegment(sketch, "E1097", {"start": v(213.17, -299.55) * mm, "end": v(213.6, -299.87) * mm});
            skLineSegment(sketch, "E1098", {"start": v(213.6, -299.87) * mm, "end": v(213.93, -300.09) * mm});
            skLineSegment(sketch, "E1099", {"start": v(213.93, -300.09) * mm, "end": v(214.47, -300.3) * mm});
            skLineSegment(sketch, "E1100", {"start": v(214.47, -300.3) * mm, "end": v(215.45, -300.3) * mm});
            skLineSegment(sketch, "E1101", {"start": v(215.45, -300.3) * mm, "end": v(215.88, -300.09) * mm});
            skLineSegment(sketch, "E1102", {"start": v(215.88, -300.09) * mm, "end": v(216.31, -299.87) * mm});
            skLineSegment(sketch, "E1103", {"start": v(216.31, -299.87) * mm, "end": v(216.64, -299.55) * mm});
            skLineSegment(sketch, "E1104", {"start": v(216.64, -299.55) * mm, "end": v(216.85, -299.11) * mm});
            skLineSegment(sketch, "E1105", {"start": v(216.85, -299.11) * mm, "end": v(217.07, -298.68) * mm});
            skLineSegment(sketch, "E1106", {"start": v(217.07, -298.68) * mm, "end": v(217.07, -298.14) * mm});
            skLineSegment(sketch, "E1107", {"start": v(212.74, -298.14) * mm, "end": v(212.74, -270.97) * mm});
            skLineSegment(sketch, "E1108", {"start": v(217.07, -270.97) * mm, "end": v(217.07, -270.43) * mm});
            skLineSegment(sketch, "E1109", {"start": v(217.07, -270.43) * mm, "end": v(216.64, -269.57) * mm});
            skLineSegment(sketch, "E1110", {"start": v(216.64, -269.57) * mm, "end": v(216.31, -269.24) * mm});
            skLineSegment(sketch, "E1111", {"start": v(216.31, -269.24) * mm, "end": v(215.88, -269.02) * mm});
            skLineSegment(sketch, "E1112", {"start": v(215.88, -269.02) * mm, "end": v(215.45, -268.8) * mm});
            skLineSegment(sketch, "E1113", {"start": v(215.45, -268.8) * mm, "end": v(214.47, -268.8) * mm});
            skLineSegment(sketch, "E1114", {"start": v(214.47, -268.8) * mm, "end": v(213.93, -269.02) * mm});
            skLineSegment(sketch, "E1115", {"start": v(213.93, -269.02) * mm, "end": v(213.6, -269.24) * mm});
            skLineSegment(sketch, "E1116", {"start": v(213.6, -269.24) * mm, "end": v(213.17, -269.57) * mm});
            skLineSegment(sketch, "E1117", {"start": v(213.17, -269.57) * mm, "end": v(212.96, -270) * mm});
            skLineSegment(sketch, "E1118", {"start": v(212.96, -270) * mm, "end": v(212.74, -270.43) * mm});
            skLineSegment(sketch, "E1119", {"start": v(212.74, -270.43) * mm, "end": v(212.74, -270.97) * mm});
            skLineSegment(sketch, "E1120", {"start": v(207.11, -271.4) * mm, "end": v(207.11, -297.7) * mm});
            skLineSegment(sketch, "E1121", {"start": v(207.11, -297.7) * mm, "end": v(207.22, -298.79) * mm});
            skLineSegment(sketch, "E1122", {"start": v(207.22, -298.79) * mm, "end": v(207.33, -299.76) * mm});
            skLineSegment(sketch, "E1123", {"start": v(207.33, -299.76) * mm, "end": v(207.65, -300.74) * mm});
            skLineSegment(sketch, "E1124", {"start": v(207.65, -300.74) * mm, "end": v(208.74, -302.47) * mm});
            skLineSegment(sketch, "E1125", {"start": v(208.74, -302.47) * mm, "end": v(209.39, -303.23) * mm});
            skLineSegment(sketch, "E1126", {"start": v(209.39, -303.23) * mm, "end": v(210.14, -303.98) * mm});
            skLineSegment(sketch, "E1127", {"start": v(210.14, -303.98) * mm, "end": v(211, -304.53) * mm});
            skLineSegment(sketch, "E1128", {"start": v(211, -304.53) * mm, "end": v(211.87, -304.96) * mm});
            skLineSegment(sketch, "E1129", {"start": v(211.87, -304.96) * mm, "end": v(212.85, -305.28) * mm});
            skLineSegment(sketch, "E1130", {"start": v(212.85, -305.28) * mm, "end": v(213.93, -305.5) * mm});
            skLineSegment(sketch, "E1131", {"start": v(213.93, -305.5) * mm, "end": v(215.88, -305.5) * mm});
            skLineSegment(sketch, "E1132", {"start": v(215.88, -305.5) * mm, "end": v(216.96, -305.28) * mm});
            skLineSegment(sketch, "E1133", {"start": v(216.96, -305.28) * mm, "end": v(217.94, -304.96) * mm});
            skLineSegment(sketch, "E1134", {"start": v(217.94, -304.96) * mm, "end": v(218.8, -304.53) * mm});
            skLineSegment(sketch, "E1135", {"start": v(218.8, -304.53) * mm, "end": v(219.67, -303.98) * mm});
            skLineSegment(sketch, "E1136", {"start": v(219.67, -303.98) * mm, "end": v(220.43, -303.23) * mm});
            skLineSegment(sketch, "E1137", {"start": v(220.43, -303.23) * mm, "end": v(221.08, -302.47) * mm});
            skLineSegment(sketch, "E1138", {"start": v(221.08, -302.47) * mm, "end": v(221.72, -301.6) * mm});
            skLineSegment(sketch, "E1139", {"start": v(221.72, -301.6) * mm, "end": v(222.16, -300.74) * mm});
            skLineSegment(sketch, "E1140", {"start": v(222.16, -300.74) * mm, "end": v(222.48, -299.76) * mm});
            skLineSegment(sketch, "E1141", {"start": v(222.48, -299.76) * mm, "end": v(222.7, -298.79) * mm});
            skLineSegment(sketch, "E1142", {"start": v(222.7, -298.79) * mm, "end": v(222.7, -297.7) * mm});
            skLineSegment(sketch, "E1143", {"start": v(222.7, -297.7) * mm, "end": v(222.7, -271.4) * mm});
            skLineSegment(sketch, "E1144", {"start": v(222.7, -271.4) * mm, "end": v(222.7, -270.32) * mm});
            skLineSegment(sketch, "E1145", {"start": v(222.7, -270.32) * mm, "end": v(222.48, -269.35) * mm});
            skLineSegment(sketch, "E1146", {"start": v(222.48, -269.35) * mm, "end": v(222.16, -268.37) * mm});
            skLineSegment(sketch, "E1147", {"start": v(222.16, -268.37) * mm, "end": v(221.72, -267.5) * mm});
            skLineSegment(sketch, "E1148", {"start": v(221.72, -267.5) * mm, "end": v(221.08, -266.64) * mm});
            skLineSegment(sketch, "E1149", {"start": v(221.08, -266.64) * mm, "end": v(220.43, -265.88) * mm});
            skLineSegment(sketch, "E1150", {"start": v(220.43, -265.88) * mm, "end": v(219.67, -265.13) * mm});
            skLineSegment(sketch, "E1151", {"start": v(219.67, -265.13) * mm, "end": v(218.8, -264.59) * mm});
            skLineSegment(sketch, "E1152", {"start": v(218.8, -264.59) * mm, "end": v(217.94, -264.15) * mm});
            skLineSegment(sketch, "E1153", {"start": v(217.94, -264.15) * mm, "end": v(216.96, -263.83) * mm});
            skLineSegment(sketch, "E1154", {"start": v(216.96, -263.83) * mm, "end": v(215.88, -263.61) * mm});
            skLineSegment(sketch, "E1155", {"start": v(215.88, -263.61) * mm, "end": v(213.93, -263.61) * mm});
            skLineSegment(sketch, "E1156", {"start": v(213.93, -263.61) * mm, "end": v(212.85, -263.83) * mm});
            skLineSegment(sketch, "E1157", {"start": v(212.85, -263.83) * mm, "end": v(211.87, -264.15) * mm});
            skLineSegment(sketch, "E1158", {"start": v(211.87, -264.15) * mm, "end": v(211, -264.59) * mm});
            skLineSegment(sketch, "E1159", {"start": v(211, -264.59) * mm, "end": v(210.14, -265.13) * mm});
            skLineSegment(sketch, "E1160", {"start": v(210.14, -265.13) * mm, "end": v(209.39, -265.88) * mm});
            skLineSegment(sketch, "E1161", {"start": v(209.39, -265.88) * mm, "end": v(208.74, -266.64) * mm});
            skLineSegment(sketch, "E1162", {"start": v(208.74, -266.64) * mm, "end": v(208.2, -267.5) * mm});
            skLineSegment(sketch, "E1163", {"start": v(208.2, -267.5) * mm, "end": v(207.65, -268.37) * mm});
            skLineSegment(sketch, "E1164", {"start": v(207.65, -268.37) * mm, "end": v(207.33, -269.35) * mm});
            skLineSegment(sketch, "E1165", {"start": v(207.33, -269.35) * mm, "end": v(207.22, -270.32) * mm});
            skLineSegment(sketch, "E1166", {"start": v(207.22, -270.32) * mm, "end": v(207.11, -271.4) * mm});
            skLineSegment(sketch, "E1167", {"start": v(-80.58, -263.61) * mm, "end": v(-87.4, -263.61) * mm});
            skLineSegment(sketch, "E1168", {"start": v(-87.4, -263.61) * mm, "end": v(-87.4, -305.5) * mm});
            skLineSegment(sketch, "E1169", {"start": v(-87.4, -305.5) * mm, "end": v(-82.31, -305.5) * mm});
            skLineSegment(sketch, "E1170", {"start": v(-82.31, -305.5) * mm, "end": v(-82.31, -277.25) * mm});
            skLineSegment(sketch, "E1171", {"start": v(-82.31, -277.25) * mm, "end": v(-81.77, -277.25) * mm});
            skLineSegment(sketch, "E1172", {"start": v(-81.77, -277.25) * mm, "end": v(-77.55, -305.5) * mm});
            skLineSegment(sketch, "E1173", {"start": v(-77.55, -305.5) * mm, "end": v(-75.17, -305.5) * mm});
            skLineSegment(sketch, "E1174", {"start": v(-75.17, -305.5) * mm, "end": v(-70.95, -277.25) * mm});
            skLineSegment(sketch, "E1175", {"start": v(-70.95, -277.25) * mm, "end": v(-70.52, -277.25) * mm});
            skLineSegment(sketch, "E1176", {"start": v(-70.52, -277.25) * mm, "end": v(-70.52, -305.5) * mm});
            skLineSegment(sketch, "E1177", {"start": v(-70.52, -305.5) * mm, "end": v(-65.32, -305.5) * mm});
            skLineSegment(sketch, "E1178", {"start": v(-65.32, -305.5) * mm, "end": v(-65.32, -263.61) * mm});
            skLineSegment(sketch, "E1179", {"start": v(-65.32, -263.61) * mm, "end": v(-72.14, -263.61) * mm});
            skLineSegment(sketch, "E1180", {"start": v(-72.14, -263.61) * mm, "end": v(-75.93, -284.83) * mm});
            skLineSegment(sketch, "E1181", {"start": v(-75.93, -284.83) * mm, "end": v(-76.8, -284.83) * mm});
            skLineSegment(sketch, "E1182", {"start": v(-76.8, -284.83) * mm, "end": v(-80.58, -263.61) * mm});
            skLineSegment(sketch, "E1183", {"start": v(-27.65, -263.61) * mm, "end": v(-33.17, -263.61) * mm});
            skLineSegment(sketch, "E1184", {"start": v(-33.17, -263.61) * mm, "end": v(-33.17, -305.5) * mm});
            skLineSegment(sketch, "E1185", {"start": v(-33.17, -305.5) * mm, "end": v(-27.65, -305.5) * mm});
            skLineSegment(sketch, "E1186", {"start": v(-27.65, -305.5) * mm, "end": v(-27.65, -281.9) * mm});
            skLineSegment(sketch, "E1187", {"start": v(-27.65, -281.9) * mm, "end": v(-27, -281.9) * mm});
            skLineSegment(sketch, "E1188", {"start": v(-27, -281.9) * mm, "end": v(-20.73, -305.5) * mm});
            skLineSegment(sketch, "E1189", {"start": v(-20.73, -305.5) * mm, "end": v(-15.53, -305.5) * mm});
            skLineSegment(sketch, "E1190", {"start": v(-15.53, -305.5) * mm, "end": v(-15.53, -263.61) * mm});
            skLineSegment(sketch, "E1191", {"start": v(-15.53, -263.61) * mm, "end": v(-20.73, -263.61) * mm});
            skLineSegment(sketch, "E1192", {"start": v(-20.73, -263.61) * mm, "end": v(-20.73, -287.75) * mm});
            skLineSegment(sketch, "E1193", {"start": v(-20.73, -287.75) * mm, "end": v(-21.38, -287.75) * mm});
            skLineSegment(sketch, "E1194", {"start": v(-21.38, -287.75) * mm, "end": v(-27.65, -263.61) * mm});
            skLineSegment(sketch, "E1195", {"start": v(-0.05, 391.55) * mm, "end": v(-13.58, 391.55) * mm});
            skLineSegment(sketch, "E1196", {"start": v(-13.58, 391.55) * mm, "end": v(-13.58, 298.68) * mm});
            skLineSegment(sketch, "E1197", {"start": v(-13.58, 298.68) * mm, "end": v(-0.05, 298.68) * mm});
            skLineSegment(sketch, "E1198", {"start": v(-0.05, 298.68) * mm, "end": v(-0.05, 333.2) * mm});
            skLineSegment(sketch, "E1199", {"start": v(-0.05, 333.2) * mm, "end": v(3.84, 341.54) * mm});
            skLineSegment(sketch, "E1200", {"start": v(3.84, 341.54) * mm, "end": v(14.01, 298.68) * mm});
            skLineSegment(sketch, "E1201", {"start": v(14.01, 298.68) * mm, "end": v(27.22, 298.68) * mm});
            skLineSegment(sketch, "E1202", {"start": v(27.22, 298.68) * mm, "end": v(12.61, 360.16) * mm});
            skLineSegment(sketch, "E1203", {"start": v(12.61, 360.16) * mm, "end": v(25.17, 391.55) * mm});
            skLineSegment(sketch, "E1204", {"start": v(25.17, 391.55) * mm, "end": v(12.5, 391.55) * mm});
            skLineSegment(sketch, "E1205", {"start": v(12.5, 391.55) * mm, "end": v(-0.05, 357.34) * mm});
            skLineSegment(sketch, "E1206", {"start": v(-0.05, 357.34) * mm, "end": v(-0.05, 391.55) * mm});
            skLineSegment(sketch, "E1207", {"start": v(103.53, 391.55) * mm, "end": v(90.1, 391.55) * mm});
            skLineSegment(sketch, "E1208", {"start": v(90.1, 391.55) * mm, "end": v(90.1, 298.68) * mm});
            skLineSegment(sketch, "E1209", {"start": v(90.1, 298.68) * mm, "end": v(103.53, 298.68) * mm});
            skLineSegment(sketch, "E1210", {"start": v(103.53, 298.68) * mm, "end": v(103.53, 333.2) * mm});
            skLineSegment(sketch, "E1211", {"start": v(103.53, 333.2) * mm, "end": v(107.53, 341.54) * mm});
            skLineSegment(sketch, "E1212", {"start": v(107.53, 341.54) * mm, "end": v(117.6, 298.68) * mm});
            skLineSegment(sketch, "E1213", {"start": v(117.6, 298.68) * mm, "end": v(130.8, 298.68) * mm});
            skLineSegment(sketch, "E1214", {"start": v(130.8, 298.68) * mm, "end": v(116.3, 360.16) * mm});
            skLineSegment(sketch, "E1215", {"start": v(116.3, 360.16) * mm, "end": v(128.75, 391.55) * mm});
            skLineSegment(sketch, "E1216", {"start": v(128.75, 391.55) * mm, "end": v(116.08, 391.55) * mm});
            skLineSegment(sketch, "E1217", {"start": v(116.08, 391.55) * mm, "end": v(103.53, 357.34) * mm});
            skLineSegment(sketch, "E1218", {"start": v(103.53, 357.34) * mm, "end": v(103.53, 391.55) * mm});
            skLineSegment(sketch, "E1219", {"start": v(56.88, 367.4) * mm, "end": v(62.18, 331.15) * mm});
            skLineSegment(sketch, "E1220", {"start": v(62.18, 331.15) * mm, "end": v(51.69, 331.15) * mm});
            skLineSegment(sketch, "E1221", {"start": v(51.69, 331.15) * mm, "end": v(56.88, 367.4) * mm});
            skLineSegment(sketch, "E1222", {"start": v(65.1, 391.55) * mm, "end": v(48.76, 391.55) * mm});
            skLineSegment(sketch, "E1223", {"start": v(48.76, 391.55) * mm, "end": v(35.23, 298.68) * mm});
            skLineSegment(sketch, "E1224", {"start": v(35.23, 298.68) * mm, "end": v(46.92, 298.68) * mm});
            skLineSegment(sketch, "E1225", {"start": v(46.92, 298.68) * mm, "end": v(49.63, 317.08) * mm});
            skLineSegment(sketch, "E1226", {"start": v(49.63, 317.08) * mm, "end": v(64.24, 317.08) * mm});
            skLineSegment(sketch, "E1227", {"start": v(64.24, 317.08) * mm, "end": v(66.95, 298.68) * mm});
            skLineSegment(sketch, "E1228", {"start": v(66.95, 298.68) * mm, "end": v(78.63, 298.68) * mm});
            skLineSegment(sketch, "E1229", {"start": v(78.63, 298.68) * mm, "end": v(65.1, 391.55) * mm});
            skLineSegment(sketch, "E1230", {"start": v(159.92, 367.4) * mm, "end": v(165.23, 331.15) * mm});
            skLineSegment(sketch, "E1231", {"start": v(165.23, 331.15) * mm, "end": v(154.62, 331.15) * mm});
            skLineSegment(sketch, "E1232", {"start": v(154.62, 331.15) * mm, "end": v(159.92, 367.4) * mm});
            skLineSegment(sketch, "E1233", {"start": v(168.04, 391.55) * mm, "end": v(151.8, 391.55) * mm});
            skLineSegment(sketch, "E1234", {"start": v(151.8, 391.55) * mm, "end": v(138.16, 298.68) * mm});
            skLineSegment(sketch, "E1235", {"start": v(138.16, 298.68) * mm, "end": v(149.86, 298.68) * mm});
            skLineSegment(sketch, "E1236", {"start": v(149.86, 298.68) * mm, "end": v(152.56, 317.08) * mm});
            skLineSegment(sketch, "E1237", {"start": v(152.56, 317.08) * mm, "end": v(167.28, 317.08) * mm});
            skLineSegment(sketch, "E1238", {"start": v(167.28, 317.08) * mm, "end": v(169.88, 298.68) * mm});
            skLineSegment(sketch, "E1239", {"start": v(169.88, 298.68) * mm, "end": v(181.57, 298.68) * mm});
            skLineSegment(sketch, "E1240", {"start": v(181.57, 298.68) * mm, "end": v(168.04, 391.55) * mm});
            skLineSegment(sketch, "E1241", {"start": v(-78.42, 391.55) * mm, "end": v(-62.07, 391.55) * mm});
            skLineSegment(sketch, "E1242", {"start": v(-70.19, 367.4) * mm, "end": v(-64.89, 331.15) * mm});
            skLineSegment(sketch, "E1243", {"start": v(-64.89, 331.15) * mm, "end": v(-75.5, 331.15) * mm});
            skLineSegment(sketch, "E1244", {"start": v(-75.5, 331.15) * mm, "end": v(-70.19, 367.4) * mm});
            skLineSegment(sketch, "E1245", {"start": v(-62.07, 391.55) * mm, "end": v(-78.42, 391.55) * mm});
            skLineSegment(sketch, "E1246", {"start": v(-78.42, 391.55) * mm, "end": v(-91.95, 298.68) * mm});
            skLineSegment(sketch, "E1247", {"start": v(-91.95, 298.68) * mm, "end": v(-80.26, 298.68) * mm});
            skLineSegment(sketch, "E1248", {"start": v(-80.26, 298.68) * mm, "end": v(-77.55, 317.08) * mm});
            skLineSegment(sketch, "E1249", {"start": v(-77.55, 317.08) * mm, "end": v(-62.83, 317.08) * mm});
            skLineSegment(sketch, "E1250", {"start": v(-62.83, 317.08) * mm, "end": v(-60.23, 298.68) * mm});
            skLineSegment(sketch, "E1251", {"start": v(-60.23, 298.68) * mm, "end": v(-48.54, 298.68) * mm});
            skLineSegment(sketch, "E1252", {"start": v(-48.54, 298.68) * mm, "end": v(-62.07, 391.55) * mm});
            skLineSegment(sketch, "E1253", {"start": v(-171.5, 391.55) * mm, "end": v(-155.16, 391.55) * mm});
            skLineSegment(sketch, "E1254", {"start": v(-163.27, 367.4) * mm, "end": v(-158.08, 331.15) * mm});
            skLineSegment(sketch, "E1255", {"start": v(-158.08, 331.15) * mm, "end": v(-168.58, 331.15) * mm});
            skLineSegment(sketch, "E1256", {"start": v(-168.58, 331.15) * mm, "end": v(-163.27, 367.4) * mm});
            skLineSegment(sketch, "E1257", {"start": v(-155.16, 391.55) * mm, "end": v(-171.5, 391.55) * mm});
            skLineSegment(sketch, "E1258", {"start": v(-171.5, 391.55) * mm, "end": v(-185.03, 298.68) * mm});
            skLineSegment(sketch, "E1259", {"start": v(-185.03, 298.68) * mm, "end": v(-173.34, 298.68) * mm});
            skLineSegment(sketch, "E1260", {"start": v(-173.34, 298.68) * mm, "end": v(-170.64, 317.08) * mm});
            skLineSegment(sketch, "E1261", {"start": v(-170.64, 317.08) * mm, "end": v(-156.02, 317.08) * mm});
            skLineSegment(sketch, "E1262", {"start": v(-156.02, 317.08) * mm, "end": v(-153.32, 298.68) * mm});
            skLineSegment(sketch, "E1263", {"start": v(-153.32, 298.68) * mm, "end": v(-141.63, 298.68) * mm});
            skLineSegment(sketch, "E1264", {"start": v(-141.63, 298.68) * mm, "end": v(-155.16, 391.55) * mm});
            skLineSegment(sketch, "E1265", {"start": v(198.78, 391.55) * mm, "end": v(187.2, 391.55) * mm});
            skLineSegment(sketch, "E1266", {"start": v(187.2, 391.55) * mm, "end": v(199.53, 298.68) * mm});
            skLineSegment(sketch, "E1267", {"start": v(199.53, 298.68) * mm, "end": v(209.39, 298.68) * mm});
            skLineSegment(sketch, "E1268", {"start": v(209.39, 298.68) * mm, "end": v(216.85, 348.8) * mm});
            skLineSegment(sketch, "E1269", {"start": v(216.85, 348.8) * mm, "end": v(217.4, 348.8) * mm});
            skLineSegment(sketch, "E1270", {"start": v(217.4, 348.8) * mm, "end": v(224.86, 298.68) * mm});
            skLineSegment(sketch, "E1271", {"start": v(224.86, 298.68) * mm, "end": v(234.71, 298.68) * mm});
            skLineSegment(sketch, "E1272", {"start": v(234.71, 298.68) * mm, "end": v(246.94, 391.55) * mm});
            skLineSegment(sketch, "E1273", {"start": v(246.94, 391.55) * mm, "end": v(235.47, 391.55) * mm});
            skLineSegment(sketch, "E1274", {"start": v(235.47, 391.55) * mm, "end": v(229.3, 339.27) * mm});
            skLineSegment(sketch, "E1275", {"start": v(229.3, 339.27) * mm, "end": v(228.44, 339.27) * mm});
            skLineSegment(sketch, "E1276", {"start": v(228.44, 339.27) * mm, "end": v(221.94, 391.55) * mm});
            skLineSegment(sketch, "E1277", {"start": v(221.94, 391.55) * mm, "end": v(212.3, 391.55) * mm});
            skLineSegment(sketch, "E1278", {"start": v(212.3, 391.55) * mm, "end": v(205.81, 339.27) * mm});
            skLineSegment(sketch, "E1279", {"start": v(205.81, 339.27) * mm, "end": v(204.95, 339.27) * mm});
            skLineSegment(sketch, "E1280", {"start": v(204.95, 339.27) * mm, "end": v(198.78, 391.55) * mm});
            skLineSegment(sketch, "E1281", {"start": v(-96.82, 391.55) * mm, "end": v(-109.26, 391.55) * mm});
            skLineSegment(sketch, "E1282", {"start": v(-109.26, 391.55) * mm, "end": v(-116.4, 361.02) * mm});
            skLineSegment(sketch, "E1283", {"start": v(-116.4, 361.02) * mm, "end": v(-117.38, 361.02) * mm});
            skLineSegment(sketch, "E1284", {"start": v(-117.38, 361.02) * mm, "end": v(-124.85, 391.55) * mm});
            skLineSegment(sketch, "E1285", {"start": v(-124.85, 391.55) * mm, "end": v(-137.62, 391.55) * mm});
            skLineSegment(sketch, "E1286", {"start": v(-137.62, 391.55) * mm, "end": v(-124.1, 341) * mm});
            skLineSegment(sketch, "E1287", {"start": v(-124.1, 341) * mm, "end": v(-124.1, 298.68) * mm});
            skLineSegment(sketch, "E1288", {"start": v(-124.1, 298.68) * mm, "end": v(-110.24, 298.68) * mm});
            skLineSegment(sketch, "E1289", {"start": v(-110.24, 298.68) * mm, "end": v(-110.24, 341) * mm});
            skLineSegment(sketch, "E1290", {"start": v(-110.24, 341) * mm, "end": v(-96.82, 391.55) * mm});
            skLineSegment(sketch, "E1291", {"start": v(-231.36, 391.55) * mm, "end": v(-246.4, 391.55) * mm});
            skLineSegment(sketch, "E1292", {"start": v(-246.4, 391.55) * mm, "end": v(-246.4, 298.68) * mm});
            skLineSegment(sketch, "E1293", {"start": v(-246.4, 298.68) * mm, "end": v(-235.04, 298.68) * mm});
            skLineSegment(sketch, "E1294", {"start": v(-235.04, 298.68) * mm, "end": v(-235.04, 361.35) * mm});
            skLineSegment(sketch, "E1295", {"start": v(-235.04, 361.35) * mm, "end": v(-234.06, 361.35) * mm});
            skLineSegment(sketch, "E1296", {"start": v(-234.06, 361.35) * mm, "end": v(-224.75, 298.68) * mm});
            skLineSegment(sketch, "E1297", {"start": v(-224.75, 298.68) * mm, "end": v(-219.23, 298.68) * mm});
            skLineSegment(sketch, "E1298", {"start": v(-219.23, 298.68) * mm, "end": v(-209.93, 361.35) * mm});
            skLineSegment(sketch, "E1299", {"start": v(-209.93, 361.35) * mm, "end": v(-208.95, 361.35) * mm});
            skLineSegment(sketch, "E1300", {"start": v(-208.95, 361.35) * mm, "end": v(-208.95, 298.68) * mm});
            skLineSegment(sketch, "E1301", {"start": v(-208.95, 298.68) * mm, "end": v(-197.59, 298.68) * mm});
            skLineSegment(sketch, "E1302", {"start": v(-197.59, 298.68) * mm, "end": v(-197.59, 391.55) * mm});
            skLineSegment(sketch, "E1303", {"start": v(-197.59, 391.55) * mm, "end": v(-212.63, 391.55) * mm});
            skLineSegment(sketch, "E1304", {"start": v(-212.63, 391.55) * mm, "end": v(-221.07, 344.68) * mm});
            skLineSegment(sketch, "E1305", {"start": v(-221.07, 344.68) * mm, "end": v(-222.91, 344.68) * mm});
            skLineSegment(sketch, "E1306", {"start": v(-222.91, 344.68) * mm, "end": v(-231.36, 391.55) * mm});
            skLineSegment(sketch, "E1307", {"start": v(-202.13, 262.3) * mm, "end": v(-189.8, 262.3) * mm});
            skLineSegment(sketch, "E1308", {"start": v(-195.96, 244.02) * mm, "end": v(-192.07, 216.74) * mm});
            skLineSegment(sketch, "E1309", {"start": v(-192.07, 216.74) * mm, "end": v(-199.97, 216.74) * mm});
            skLineSegment(sketch, "E1310", {"start": v(-199.97, 216.74) * mm, "end": v(-195.96, 244.02) * mm});
            skLineSegment(sketch, "E1311", {"start": v(-189.8, 262.3) * mm, "end": v(-202.13, 262.3) * mm});
            skLineSegment(sketch, "E1312", {"start": v(-202.13, 262.3) * mm, "end": v(-212.41, 192.18) * mm});
            skLineSegment(sketch, "E1313", {"start": v(-212.41, 192.18) * mm, "end": v(-203.54, 192.18) * mm});
            skLineSegment(sketch, "E1314", {"start": v(-203.54, 192.18) * mm, "end": v(-201.6, 206.03) * mm});
            skLineSegment(sketch, "E1315", {"start": v(-201.6, 206.03) * mm, "end": v(-190.44, 206.03) * mm});
            skLineSegment(sketch, "E1316", {"start": v(-190.44, 206.03) * mm, "end": v(-188.39, 192.18) * mm});
            skLineSegment(sketch, "E1317", {"start": v(-188.39, 192.18) * mm, "end": v(-179.62, 192.18) * mm});
            skLineSegment(sketch, "E1318", {"start": v(-179.62, 192.18) * mm, "end": v(-189.8, 262.3) * mm});
            skLineSegment(sketch, "E1319", {"start": v(-124.96, 262.3) * mm, "end": v(-112.62, 262.3) * mm});
            skLineSegment(sketch, "E1320", {"start": v(-118.79, 244.02) * mm, "end": v(-114.78, 216.74) * mm});
            skLineSegment(sketch, "E1321", {"start": v(-114.78, 216.74) * mm, "end": v(-122.8, 216.74) * mm});
            skLineSegment(sketch, "E1322", {"start": v(-122.8, 216.74) * mm, "end": v(-118.79, 244.02) * mm});
            skLineSegment(sketch, "E1323", {"start": v(-112.62, 262.3) * mm, "end": v(-124.96, 262.3) * mm});
            skLineSegment(sketch, "E1324", {"start": v(-124.96, 262.3) * mm, "end": v(-135.13, 192.18) * mm});
            skLineSegment(sketch, "E1325", {"start": v(-135.13, 192.18) * mm, "end": v(-126.37, 192.18) * mm});
            skLineSegment(sketch, "E1326", {"start": v(-126.37, 192.18) * mm, "end": v(-124.3, 206.03) * mm});
            skLineSegment(sketch, "E1327", {"start": v(-124.3, 206.03) * mm, "end": v(-113.27, 206.03) * mm});
            skLineSegment(sketch, "E1328", {"start": v(-113.27, 206.03) * mm, "end": v(-111.21, 192.18) * mm});
            skLineSegment(sketch, "E1329", {"start": v(-111.21, 192.18) * mm, "end": v(-102.34, 192.18) * mm});
            skLineSegment(sketch, "E1330", {"start": v(-102.34, 192.18) * mm, "end": v(-112.62, 262.3) * mm});
            skLineSegment(sketch, "E1331", {"start": v(87.5, 262.3) * mm, "end": v(99.85, 262.3) * mm});
            skLineSegment(sketch, "E1332", {"start": v(93.68, 244.02) * mm, "end": v(97.68, 216.74) * mm});
            skLineSegment(sketch, "E1333", {"start": v(97.68, 216.74) * mm, "end": v(89.68, 216.74) * mm});
            skLineSegment(sketch, "E1334", {"start": v(89.68, 216.74) * mm, "end": v(93.68, 244.02) * mm});
            skLineSegment(sketch, "E1335", {"start": v(99.85, 262.3) * mm, "end": v(87.5, 262.3) * mm});
            skLineSegment(sketch, "E1336", {"start": v(87.5, 262.3) * mm, "end": v(77.33, 192.18) * mm});
            skLineSegment(sketch, "E1337", {"start": v(77.33, 192.18) * mm, "end": v(86.1, 192.18) * mm});
            skLineSegment(sketch, "E1338", {"start": v(86.1, 192.18) * mm, "end": v(88.16, 206.03) * mm});
            skLineSegment(sketch, "E1339", {"start": v(88.16, 206.03) * mm, "end": v(99.2, 206.03) * mm});
            skLineSegment(sketch, "E1340", {"start": v(99.2, 206.03) * mm, "end": v(101.26, 192.18) * mm});
            skLineSegment(sketch, "E1341", {"start": v(101.26, 192.18) * mm, "end": v(110.02, 192.18) * mm});
            skLineSegment(sketch, "E1342", {"start": v(110.02, 192.18) * mm, "end": v(99.85, 262.3) * mm});
            skLineSegment(sketch, "E1343", {"start": v(161.54, 262.3) * mm, "end": v(171.4, 262.3) * mm});
            skLineSegment(sketch, "E1344", {"start": v(171.4, 262.3) * mm, "end": v(171.4, 192.18) * mm});
            skLineSegment(sketch, "E1345", {"start": v(171.4, 192.18) * mm, "end": v(161.54, 192.18) * mm});
            skLineSegment(sketch, "E1346", {"start": v(161.54, 192.18) * mm, "end": v(161.54, 262.3) * mm});
            skLineSegment(sketch, "E1347", {"start": v(237.74, 249.97) * mm, "end": v(237.74, 204.51) * mm});
            skLineSegment(sketch, "E1348", {"start": v(230.5, 204.51) * mm, "end": v(230.5, 203.65) * mm});
            skLineSegment(sketch, "E1349", {"start": v(230.5, 203.65) * mm, "end": v(230.81, 202.89) * mm});
            skLineSegment(sketch, "E1350", {"start": v(230.81, 202.89) * mm, "end": v(231.25, 202.24) * mm});
            skLineSegment(sketch, "E1351", {"start": v(231.25, 202.24) * mm, "end": v(231.8, 201.6) * mm});
            skLineSegment(sketch, "E1352", {"start": v(231.8, 201.6) * mm, "end": v(232.44, 201.16) * mm});
            skLineSegment(sketch, "E1353", {"start": v(232.44, 201.16) * mm, "end": v(233.3, 200.94) * mm});
            skLineSegment(sketch, "E1354", {"start": v(233.3, 200.94) * mm, "end": v(234.07, 200.83) * mm});
            skLineSegment(sketch, "E1355", {"start": v(234.07, 200.83) * mm, "end": v(234.82, 200.94) * mm});
            skLineSegment(sketch, "E1356", {"start": v(234.82, 200.94) * mm, "end": v(235.69, 201.16) * mm});
            skLineSegment(sketch, "E1357", {"start": v(235.69, 201.16) * mm, "end": v(236.34, 201.6) * mm});
            skLineSegment(sketch, "E1358", {"start": v(236.34, 201.6) * mm, "end": v(236.88, 202.24) * mm});
            skLineSegment(sketch, "E1359", {"start": v(236.88, 202.24) * mm, "end": v(237.3, 202.89) * mm});
            skLineSegment(sketch, "E1360", {"start": v(237.3, 202.89) * mm, "end": v(237.63, 203.65) * mm});
            skLineSegment(sketch, "E1361", {"start": v(237.63, 203.65) * mm, "end": v(237.74, 204.51) * mm});
            skLineSegment(sketch, "E1362", {"start": v(230.5, 204.51) * mm, "end": v(230.5, 249.97) * mm});
            skLineSegment(sketch, "E1363", {"start": v(237.74, 249.97) * mm, "end": v(237.63, 250.84) * mm});
            skLineSegment(sketch, "E1364", {"start": v(237.63, 250.84) * mm, "end": v(237.3, 251.6) * mm});
            skLineSegment(sketch, "E1365", {"start": v(237.3, 251.6) * mm, "end": v(236.88, 252.25) * mm});
            skLineSegment(sketch, "E1366", {"start": v(236.88, 252.25) * mm, "end": v(236.34, 252.78) * mm});
            skLineSegment(sketch, "E1367", {"start": v(236.34, 252.78) * mm, "end": v(235.69, 253.22) * mm});
            skLineSegment(sketch, "E1368", {"start": v(235.69, 253.22) * mm, "end": v(234.82, 253.54) * mm});
            skLineSegment(sketch, "E1369", {"start": v(234.82, 253.54) * mm, "end": v(234.07, 253.65) * mm});
            skLineSegment(sketch, "E1370", {"start": v(234.07, 253.65) * mm, "end": v(233.3, 253.54) * mm});
            skLineSegment(sketch, "E1371", {"start": v(233.3, 253.54) * mm, "end": v(232.44, 253.22) * mm});
            skLineSegment(sketch, "E1372", {"start": v(232.44, 253.22) * mm, "end": v(231.8, 252.78) * mm});
            skLineSegment(sketch, "E1373", {"start": v(231.8, 252.78) * mm, "end": v(231.25, 252.25) * mm});
            skLineSegment(sketch, "E1374", {"start": v(231.25, 252.25) * mm, "end": v(230.81, 251.6) * mm});
            skLineSegment(sketch, "E1375", {"start": v(230.81, 251.6) * mm, "end": v(230.5, 250.84) * mm});
            skLineSegment(sketch, "E1376", {"start": v(230.5, 250.84) * mm, "end": v(230.5, 249.97) * mm});
            skLineSegment(sketch, "E1377", {"start": v(221.08, 249.22) * mm, "end": v(221.08, 205.16) * mm});
            skLineSegment(sketch, "E1378", {"start": v(221.08, 205.16) * mm, "end": v(221.08, 203.65) * mm});
            skLineSegment(sketch, "E1379", {"start": v(221.08, 203.65) * mm, "end": v(221.4, 202.13) * mm});
            skLineSegment(sketch, "E1380", {"start": v(221.4, 202.13) * mm, "end": v(221.83, 200.62) * mm});
            skLineSegment(sketch, "E1381", {"start": v(221.83, 200.62) * mm, "end": v(222.48, 199.1) * mm});
            skLineSegment(sketch, "E1382", {"start": v(222.48, 199.1) * mm, "end": v(223.35, 197.8) * mm});
            skLineSegment(sketch, "E1383", {"start": v(223.35, 197.8) * mm, "end": v(224.32, 196.61) * mm});
            skLineSegment(sketch, "E1384", {"start": v(224.32, 196.61) * mm, "end": v(225.4, 195.42) * mm});
            skLineSegment(sketch, "E1385", {"start": v(225.4, 195.42) * mm, "end": v(226.7, 194.45) * mm});
            skLineSegment(sketch, "E1386", {"start": v(226.7, 194.45) * mm, "end": v(228, 193.69) * mm});
            skLineSegment(sketch, "E1387", {"start": v(228, 193.69) * mm, "end": v(229.4, 193.04) * mm});
            skLineSegment(sketch, "E1388", {"start": v(229.4, 193.04) * mm, "end": v(230.92, 192.5) * mm});
            skLineSegment(sketch, "E1389", {"start": v(230.92, 192.5) * mm, "end": v(232.55, 192.28) * mm});
            skLineSegment(sketch, "E1390", {"start": v(232.55, 192.28) * mm, "end": v(234.07, 192.18) * mm});
            skLineSegment(sketch, "E1391", {"start": v(234.07, 192.18) * mm, "end": v(235.69, 192.28) * mm});
            skLineSegment(sketch, "E1392", {"start": v(235.69, 192.28) * mm, "end": v(237.2, 192.5) * mm});
            skLineSegment(sketch, "E1393", {"start": v(237.2, 192.5) * mm, "end": v(238.72, 193.04) * mm});
            skLineSegment(sketch, "E1394", {"start": v(238.72, 193.04) * mm, "end": v(240.13, 193.69) * mm});
            skLineSegment(sketch, "E1395", {"start": v(240.13, 193.69) * mm, "end": v(241.42, 194.45) * mm});
            skLineSegment(sketch, "E1396", {"start": v(241.42, 194.45) * mm, "end": v(242.72, 195.42) * mm});
            skLineSegment(sketch, "E1397", {"start": v(242.72, 195.42) * mm, "end": v(243.8, 196.61) * mm});
            skLineSegment(sketch, "E1398", {"start": v(243.8, 196.61) * mm, "end": v(244.78, 197.8) * mm});
            skLineSegment(sketch, "E1399", {"start": v(244.78, 197.8) * mm, "end": v(245.64, 199.1) * mm});
            skLineSegment(sketch, "E1400", {"start": v(245.64, 199.1) * mm, "end": v(246.3, 200.62) * mm});
            skLineSegment(sketch, "E1401", {"start": v(246.3, 200.62) * mm, "end": v(246.72, 202.13) * mm});
            skLineSegment(sketch, "E1402", {"start": v(246.72, 202.13) * mm, "end": v(247.05, 203.65) * mm});
            skLineSegment(sketch, "E1403", {"start": v(247.05, 203.65) * mm, "end": v(247.16, 205.16) * mm});
            skLineSegment(sketch, "E1404", {"start": v(247.16, 205.16) * mm, "end": v(247.16, 249.22) * mm});
            skLineSegment(sketch, "E1405", {"start": v(247.16, 249.22) * mm, "end": v(247.05, 250.84) * mm});
            skLineSegment(sketch, "E1406", {"start": v(247.05, 250.84) * mm, "end": v(246.72, 252.36) * mm});
            skLineSegment(sketch, "E1407", {"start": v(246.72, 252.36) * mm, "end": v(246.3, 253.87) * mm});
            skLineSegment(sketch, "E1408", {"start": v(246.3, 253.87) * mm, "end": v(245.64, 255.28) * mm});
            skLineSegment(sketch, "E1409", {"start": v(245.64, 255.28) * mm, "end": v(244.78, 256.68) * mm});
            skLineSegment(sketch, "E1410", {"start": v(244.78, 256.68) * mm, "end": v(243.8, 257.87) * mm});
            skLineSegment(sketch, "E1411", {"start": v(243.8, 257.87) * mm, "end": v(242.72, 258.96) * mm});
            skLineSegment(sketch, "E1412", {"start": v(242.72, 258.96) * mm, "end": v(241.42, 259.93) * mm});
            skLineSegment(sketch, "E1413", {"start": v(241.42, 259.93) * mm, "end": v(240.13, 260.8) * mm});
            skLineSegment(sketch, "E1414", {"start": v(240.13, 260.8) * mm, "end": v(238.72, 261.45) * mm});
            skLineSegment(sketch, "E1415", {"start": v(238.72, 261.45) * mm, "end": v(237.2, 261.88) * mm});
            skLineSegment(sketch, "E1416", {"start": v(237.2, 261.88) * mm, "end": v(235.69, 262.2) * mm});
            skLineSegment(sketch, "E1417", {"start": v(235.69, 262.2) * mm, "end": v(234.07, 262.3) * mm});
            skLineSegment(sketch, "E1418", {"start": v(234.07, 262.3) * mm, "end": v(232.55, 262.2) * mm});
            skLineSegment(sketch, "E1419", {"start": v(232.55, 262.2) * mm, "end": v(230.92, 261.88) * mm});
            skLineSegment(sketch, "E1420", {"start": v(230.92, 261.88) * mm, "end": v(229.4, 261.45) * mm});
            skLineSegment(sketch, "E1421", {"start": v(229.4, 261.45) * mm, "end": v(228, 260.8) * mm});
            skLineSegment(sketch, "E1422", {"start": v(228, 260.8) * mm, "end": v(226.7, 259.93) * mm});
            skLineSegment(sketch, "E1423", {"start": v(226.7, 259.93) * mm, "end": v(225.4, 258.96) * mm});
            skLineSegment(sketch, "E1424", {"start": v(225.4, 258.96) * mm, "end": v(224.32, 257.87) * mm});
            skLineSegment(sketch, "E1425", {"start": v(224.32, 257.87) * mm, "end": v(223.35, 256.68) * mm});
            skLineSegment(sketch, "E1426", {"start": v(223.35, 256.68) * mm, "end": v(222.48, 255.28) * mm});
            skLineSegment(sketch, "E1427", {"start": v(222.48, 255.28) * mm, "end": v(221.83, 253.87) * mm});
            skLineSegment(sketch, "E1428", {"start": v(221.83, 253.87) * mm, "end": v(221.4, 252.36) * mm});
            skLineSegment(sketch, "E1429", {"start": v(221.4, 252.36) * mm, "end": v(221.08, 250.84) * mm});
            skLineSegment(sketch, "E1430", {"start": v(221.08, 250.84) * mm, "end": v(221.08, 249.22) * mm});
            skLineSegment(sketch, "E1431", {"start": v(183.84, 205.16) * mm, "end": v(183.95, 203.65) * mm});
            skLineSegment(sketch, "E1432", {"start": v(183.95, 203.65) * mm, "end": v(184.17, 202.13) * mm});
            skLineSegment(sketch, "E1433", {"start": v(184.17, 202.13) * mm, "end": v(184.7, 200.62) * mm});
            skLineSegment(sketch, "E1434", {"start": v(184.7, 200.62) * mm, "end": v(185.36, 199.1) * mm});
            skLineSegment(sketch, "E1435", {"start": v(185.36, 199.1) * mm, "end": v(186.11, 197.8) * mm});
            skLineSegment(sketch, "E1436", {"start": v(186.11, 197.8) * mm, "end": v(187.09, 196.61) * mm});
            skLineSegment(sketch, "E1437", {"start": v(187.09, 196.61) * mm, "end": v(188.17, 195.42) * mm});
            skLineSegment(sketch, "E1438", {"start": v(188.17, 195.42) * mm, "end": v(189.47, 194.45) * mm});
            skLineSegment(sketch, "E1439", {"start": v(189.47, 194.45) * mm, "end": v(190.77, 193.69) * mm});
            skLineSegment(sketch, "E1440", {"start": v(190.77, 193.69) * mm, "end": v(192.18, 193.04) * mm});
            skLineSegment(sketch, "E1441", {"start": v(192.18, 193.04) * mm, "end": v(193.7, 192.5) * mm});
            skLineSegment(sketch, "E1442", {"start": v(193.7, 192.5) * mm, "end": v(195.31, 192.28) * mm});
            skLineSegment(sketch, "E1443", {"start": v(195.31, 192.28) * mm, "end": v(196.83, 192.18) * mm});
            skLineSegment(sketch, "E1444", {"start": v(196.83, 192.18) * mm, "end": v(198.45, 192.28) * mm});
            skLineSegment(sketch, "E1445", {"start": v(198.45, 192.28) * mm, "end": v(199.97, 192.5) * mm});
            skLineSegment(sketch, "E1446", {"start": v(199.97, 192.5) * mm, "end": v(201.48, 193.04) * mm});
            skLineSegment(sketch, "E1447", {"start": v(201.48, 193.04) * mm, "end": v(202.9, 193.69) * mm});
            skLineSegment(sketch, "E1448", {"start": v(202.9, 193.69) * mm, "end": v(204.3, 194.45) * mm});
            skLineSegment(sketch, "E1449", {"start": v(204.3, 194.45) * mm, "end": v(205.5, 195.42) * mm});
            skLineSegment(sketch, "E1450", {"start": v(205.5, 195.42) * mm, "end": v(206.57, 196.61) * mm});
            skLineSegment(sketch, "E1451", {"start": v(206.57, 196.61) * mm, "end": v(207.54, 197.8) * mm});
            skLineSegment(sketch, "E1452", {"start": v(207.54, 197.8) * mm, "end": v(208.41, 199.1) * mm});
            skLineSegment(sketch, "E1453", {"start": v(208.41, 199.1) * mm, "end": v(209.06, 200.62) * mm});
            skLineSegment(sketch, "E1454", {"start": v(209.06, 200.62) * mm, "end": v(209.5, 202.13) * mm});
            skLineSegment(sketch, "E1455", {"start": v(209.5, 202.13) * mm, "end": v(209.82, 203.65) * mm});
            skLineSegment(sketch, "E1456", {"start": v(209.82, 203.65) * mm, "end": v(209.93, 205.16) * mm});
            skLineSegment(sketch, "E1457", {"start": v(209.93, 205.16) * mm, "end": v(209.93, 216.2) * mm});
            skLineSegment(sketch, "E1458", {"start": v(209.93, 216.2) * mm, "end": v(200.51, 216.2) * mm});
            skLineSegment(sketch, "E1459", {"start": v(200.51, 216.2) * mm, "end": v(200.51, 204.51) * mm});
            skLineSegment(sketch, "E1460", {"start": v(193.26, 204.51) * mm, "end": v(193.37, 203.65) * mm});
            skLineSegment(sketch, "E1461", {"start": v(193.37, 203.65) * mm, "end": v(193.58, 202.89) * mm});
            skLineSegment(sketch, "E1462", {"start": v(193.58, 202.89) * mm, "end": v(194.02, 202.24) * mm});
            skLineSegment(sketch, "E1463", {"start": v(194.02, 202.24) * mm, "end": v(194.56, 201.6) * mm});
            skLineSegment(sketch, "E1464", {"start": v(194.56, 201.6) * mm, "end": v(195.31, 201.16) * mm});
            skLineSegment(sketch, "E1465", {"start": v(195.31, 201.16) * mm, "end": v(196.07, 200.94) * mm});
            skLineSegment(sketch, "E1466", {"start": v(196.07, 200.94) * mm, "end": v(196.83, 200.83) * mm});
            skLineSegment(sketch, "E1467", {"start": v(196.83, 200.83) * mm, "end": v(197.7, 200.94) * mm});
            skLineSegment(sketch, "E1468", {"start": v(197.7, 200.94) * mm, "end": v(198.45, 201.16) * mm});
            skLineSegment(sketch, "E1469", {"start": v(198.45, 201.16) * mm, "end": v(199.1, 201.6) * mm});
            skLineSegment(sketch, "E1470", {"start": v(199.1, 201.6) * mm, "end": v(199.64, 202.24) * mm});
            skLineSegment(sketch, "E1471", {"start": v(199.64, 202.24) * mm, "end": v(200.08, 202.89) * mm});
            skLineSegment(sketch, "E1472", {"start": v(200.08, 202.89) * mm, "end": v(200.4, 203.65) * mm});
            skLineSegment(sketch, "E1473", {"start": v(200.4, 203.65) * mm, "end": v(200.51, 204.51) * mm});
            skLineSegment(sketch, "E1474", {"start": v(193.26, 204.51) * mm, "end": v(193.26, 249.97) * mm});
            skLineSegment(sketch, "E1475", {"start": v(200.51, 249.97) * mm, "end": v(200.4, 250.84) * mm});
            skLineSegment(sketch, "E1476", {"start": v(200.4, 250.84) * mm, "end": v(200.08, 251.6) * mm});
            skLineSegment(sketch, "E1477", {"start": v(200.08, 251.6) * mm, "end": v(199.64, 252.25) * mm});
            skLineSegment(sketch, "E1478", {"start": v(199.64, 252.25) * mm, "end": v(199.1, 252.78) * mm});
            skLineSegment(sketch, "E1479", {"start": v(199.1, 252.78) * mm, "end": v(198.45, 253.22) * mm});
            skLineSegment(sketch, "E1480", {"start": v(198.45, 253.22) * mm, "end": v(197.7, 253.54) * mm});
            skLineSegment(sketch, "E1481", {"start": v(197.7, 253.54) * mm, "end": v(196.83, 253.65) * mm});
            skLineSegment(sketch, "E1482", {"start": v(196.83, 253.65) * mm, "end": v(196.07, 253.54) * mm});
            skLineSegment(sketch, "E1483", {"start": v(196.07, 253.54) * mm, "end": v(195.31, 253.22) * mm});
            skLineSegment(sketch, "E1484", {"start": v(195.31, 253.22) * mm, "end": v(194.56, 252.78) * mm});
            skLineSegment(sketch, "E1485", {"start": v(194.56, 252.78) * mm, "end": v(194.02, 252.25) * mm});
            skLineSegment(sketch, "E1486", {"start": v(194.02, 252.25) * mm, "end": v(193.58, 251.6) * mm});
            skLineSegment(sketch, "E1487", {"start": v(193.58, 251.6) * mm, "end": v(193.37, 250.84) * mm});
            skLineSegment(sketch, "E1488", {"start": v(193.37, 250.84) * mm, "end": v(193.26, 249.97) * mm});
            skLineSegment(sketch, "E1489", {"start": v(200.51, 249.97) * mm, "end": v(200.51, 238.28) * mm});
            skLineSegment(sketch, "E1490", {"start": v(200.51, 238.28) * mm, "end": v(209.93, 238.28) * mm});
            skLineSegment(sketch, "E1491", {"start": v(209.93, 238.28) * mm, "end": v(209.93, 249.22) * mm});
            skLineSegment(sketch, "E1492", {"start": v(209.93, 249.22) * mm, "end": v(209.82, 250.84) * mm});
            skLineSegment(sketch, "E1493", {"start": v(209.82, 250.84) * mm, "end": v(209.5, 252.36) * mm});
            skLineSegment(sketch, "E1494", {"start": v(209.5, 252.36) * mm, "end": v(209.06, 253.87) * mm});
            skLineSegment(sketch, "E1495", {"start": v(209.06, 253.87) * mm, "end": v(208.41, 255.28) * mm});
            skLineSegment(sketch, "E1496", {"start": v(208.41, 255.28) * mm, "end": v(207.54, 256.68) * mm});
            skLineSegment(sketch, "E1497", {"start": v(207.54, 256.68) * mm, "end": v(206.57, 257.87) * mm});
            skLineSegment(sketch, "E1498", {"start": v(206.57, 257.87) * mm, "end": v(205.5, 258.96) * mm});
            skLineSegment(sketch, "E1499", {"start": v(205.5, 258.96) * mm, "end": v(204.3, 259.93) * mm});
            skLineSegment(sketch, "E1500", {"start": v(204.3, 259.93) * mm, "end": v(202.9, 260.8) * mm});
            skLineSegment(sketch, "E1501", {"start": v(202.9, 260.8) * mm, "end": v(201.48, 261.45) * mm});
            skLineSegment(sketch, "E1502", {"start": v(201.48, 261.45) * mm, "end": v(199.97, 261.88) * mm});
            skLineSegment(sketch, "E1503", {"start": v(199.97, 261.88) * mm, "end": v(198.45, 262.2) * mm});
            skLineSegment(sketch, "E1504", {"start": v(198.45, 262.2) * mm, "end": v(196.83, 262.3) * mm});
            skLineSegment(sketch, "E1505", {"start": v(196.83, 262.3) * mm, "end": v(195.31, 262.2) * mm});
            skLineSegment(sketch, "E1506", {"start": v(195.31, 262.2) * mm, "end": v(193.7, 261.88) * mm});
            skLineSegment(sketch, "E1507", {"start": v(193.7, 261.88) * mm, "end": v(192.18, 261.45) * mm});
            skLineSegment(sketch, "E1508", {"start": v(192.18, 261.45) * mm, "end": v(190.77, 260.8) * mm});
            skLineSegment(sketch, "E1509", {"start": v(190.77, 260.8) * mm, "end": v(189.47, 259.93) * mm});
            skLineSegment(sketch, "E1510", {"start": v(189.47, 259.93) * mm, "end": v(188.17, 258.96) * mm});
            skLineSegment(sketch, "E1511", {"start": v(188.17, 258.96) * mm, "end": v(187.09, 257.87) * mm});
            skLineSegment(sketch, "E1512", {"start": v(187.09, 257.87) * mm, "end": v(186.11, 256.68) * mm});
            skLineSegment(sketch, "E1513", {"start": v(186.11, 256.68) * mm, "end": v(185.36, 255.28) * mm});
            skLineSegment(sketch, "E1514", {"start": v(185.36, 255.28) * mm, "end": v(184.7, 253.87) * mm});
            skLineSegment(sketch, "E1515", {"start": v(184.7, 253.87) * mm, "end": v(184.17, 252.36) * mm});
            skLineSegment(sketch, "E1516", {"start": v(184.17, 252.36) * mm, "end": v(183.95, 250.84) * mm});
            skLineSegment(sketch, "E1517", {"start": v(183.95, 250.84) * mm, "end": v(183.84, 249.22) * mm});
            skLineSegment(sketch, "E1518", {"start": v(183.84, 249.22) * mm, "end": v(183.84, 205.16) * mm});
            skLineSegment(sketch, "E1519", {"start": v(-19.1, 249.97) * mm, "end": v(-19.1, 204.51) * mm});
            skLineSegment(sketch, "E1520", {"start": v(-26.35, 204.51) * mm, "end": v(-26.25, 203.65) * mm});
            skLineSegment(sketch, "E1521", {"start": v(-26.25, 203.65) * mm, "end": v(-25.92, 202.89) * mm});
            skLineSegment(sketch, "E1522", {"start": v(-25.92, 202.89) * mm, "end": v(-25.49, 202.24) * mm});
            skLineSegment(sketch, "E1523", {"start": v(-25.49, 202.24) * mm, "end": v(-24.95, 201.6) * mm});
            skLineSegment(sketch, "E1524", {"start": v(-24.95, 201.6) * mm, "end": v(-24.3, 201.16) * mm});
            skLineSegment(sketch, "E1525", {"start": v(-24.3, 201.16) * mm, "end": v(-23.54, 200.94) * mm});
            skLineSegment(sketch, "E1526", {"start": v(-23.54, 200.94) * mm, "end": v(-22.67, 200.83) * mm});
            skLineSegment(sketch, "E1527", {"start": v(-22.67, 200.83) * mm, "end": v(-21.92, 200.94) * mm});
            skLineSegment(sketch, "E1528", {"start": v(-21.92, 200.94) * mm, "end": v(-21.16, 201.16) * mm});
            skLineSegment(sketch, "E1529", {"start": v(-21.16, 201.16) * mm, "end": v(-20.4, 201.6) * mm});
            skLineSegment(sketch, "E1530", {"start": v(-20.4, 201.6) * mm, "end": v(-19.86, 202.24) * mm});
            skLineSegment(sketch, "E1531", {"start": v(-19.86, 202.24) * mm, "end": v(-19.43, 202.89) * mm});
            skLineSegment(sketch, "E1532", {"start": v(-19.43, 202.89) * mm, "end": v(-19.1, 203.65) * mm});
            skLineSegment(sketch, "E1533", {"start": v(-19.1, 203.65) * mm, "end": v(-19.1, 204.51) * mm});
            skLineSegment(sketch, "E1534", {"start": v(-26.35, 204.51) * mm, "end": v(-26.35, 249.97) * mm});
            skLineSegment(sketch, "E1535", {"start": v(-19.1, 249.97) * mm, "end": v(-19.1, 250.84) * mm});
            skLineSegment(sketch, "E1536", {"start": v(-19.1, 250.84) * mm, "end": v(-19.43, 251.6) * mm});
            skLineSegment(sketch, "E1537", {"start": v(-19.43, 251.6) * mm, "end": v(-19.86, 252.25) * mm});
            skLineSegment(sketch, "E1538", {"start": v(-19.86, 252.25) * mm, "end": v(-20.4, 252.78) * mm});
            skLineSegment(sketch, "E1539", {"start": v(-20.4, 252.78) * mm, "end": v(-21.16, 253.22) * mm});
            skLineSegment(sketch, "E1540", {"start": v(-21.16, 253.22) * mm, "end": v(-21.92, 253.54) * mm});
            skLineSegment(sketch, "E1541", {"start": v(-21.92, 253.54) * mm, "end": v(-22.67, 253.65) * mm});
            skLineSegment(sketch, "E1542", {"start": v(-22.67, 253.65) * mm, "end": v(-23.54, 253.54) * mm});
            skLineSegment(sketch, "E1543", {"start": v(-23.54, 253.54) * mm, "end": v(-24.3, 253.22) * mm});
            skLineSegment(sketch, "E1544", {"start": v(-24.3, 253.22) * mm, "end": v(-24.95, 252.78) * mm});
            skLineSegment(sketch, "E1545", {"start": v(-24.95, 252.78) * mm, "end": v(-25.49, 252.25) * mm});
            skLineSegment(sketch, "E1546", {"start": v(-25.49, 252.25) * mm, "end": v(-25.92, 251.6) * mm});
            skLineSegment(sketch, "E1547", {"start": v(-25.92, 251.6) * mm, "end": v(-26.25, 250.84) * mm});
            skLineSegment(sketch, "E1548", {"start": v(-26.25, 250.84) * mm, "end": v(-26.35, 249.97) * mm});
            skLineSegment(sketch, "E1549", {"start": v(-35.77, 249.22) * mm, "end": v(-35.77, 205.16) * mm});
            skLineSegment(sketch, "E1550", {"start": v(-35.77, 205.16) * mm, "end": v(-35.66, 203.65) * mm});
            skLineSegment(sketch, "E1551", {"start": v(-35.66, 203.65) * mm, "end": v(-35.34, 202.13) * mm});
            skLineSegment(sketch, "E1552", {"start": v(-35.34, 202.13) * mm, "end": v(-34.9, 200.62) * mm});
            skLineSegment(sketch, "E1553", {"start": v(-34.9, 200.62) * mm, "end": v(-34.26, 199.1) * mm});
            skLineSegment(sketch, "E1554", {"start": v(-34.26, 199.1) * mm, "end": v(-33.4, 197.8) * mm});
            skLineSegment(sketch, "E1555", {"start": v(-33.4, 197.8) * mm, "end": v(-32.42, 196.61) * mm});
            skLineSegment(sketch, "E1556", {"start": v(-32.42, 196.61) * mm, "end": v(-31.33, 195.42) * mm});
            skLineSegment(sketch, "E1557", {"start": v(-31.33, 195.42) * mm, "end": v(-30.14, 194.45) * mm});
            skLineSegment(sketch, "E1558", {"start": v(-30.14, 194.45) * mm, "end": v(-28.74, 193.69) * mm});
            skLineSegment(sketch, "E1559", {"start": v(-28.74, 193.69) * mm, "end": v(-27.33, 193.04) * mm});
            skLineSegment(sketch, "E1560", {"start": v(-27.33, 193.04) * mm, "end": v(-25.81, 192.5) * mm});
            skLineSegment(sketch, "E1561", {"start": v(-25.81, 192.5) * mm, "end": v(-24.3, 192.28) * mm});
            skLineSegment(sketch, "E1562", {"start": v(-24.3, 192.28) * mm, "end": v(-22.67, 192.18) * mm});
            skLineSegment(sketch, "E1563", {"start": v(-22.67, 192.18) * mm, "end": v(-21.16, 192.28) * mm});
            skLineSegment(sketch, "E1564", {"start": v(-21.16, 192.28) * mm, "end": v(-19.54, 192.5) * mm});
            skLineSegment(sketch, "E1565", {"start": v(-19.54, 192.5) * mm, "end": v(-18.02, 193.04) * mm});
            skLineSegment(sketch, "E1566", {"start": v(-18.02, 193.04) * mm, "end": v(-16.61, 193.69) * mm});
            skLineSegment(sketch, "E1567", {"start": v(-16.61, 193.69) * mm, "end": v(-15.31, 194.45) * mm});
            skLineSegment(sketch, "E1568", {"start": v(-15.31, 194.45) * mm, "end": v(-14.02, 195.42) * mm});
            skLineSegment(sketch, "E1569", {"start": v(-14.02, 195.42) * mm, "end": v(-12.93, 196.61) * mm});
            skLineSegment(sketch, "E1570", {"start": v(-12.93, 196.61) * mm, "end": v(-11.96, 197.8) * mm});
            skLineSegment(sketch, "E1571", {"start": v(-11.96, 197.8) * mm, "end": v(-11.1, 199.1) * mm});
            skLineSegment(sketch, "E1572", {"start": v(-11.1, 199.1) * mm, "end": v(-10.45, 200.62) * mm});
            skLineSegment(sketch, "E1573", {"start": v(-10.45, 200.62) * mm, "end": v(-10.01, 202.13) * mm});
            skLineSegment(sketch, "E1574", {"start": v(-10.01, 202.13) * mm, "end": v(-9.69, 203.65) * mm});
            skLineSegment(sketch, "E1575", {"start": v(-9.69, 203.65) * mm, "end": v(-9.69, 205.16) * mm});
            skLineSegment(sketch, "E1576", {"start": v(-9.69, 205.16) * mm, "end": v(-9.69, 249.22) * mm});
            skLineSegment(sketch, "E1577", {"start": v(-9.69, 249.22) * mm, "end": v(-9.69, 250.84) * mm});
            skLineSegment(sketch, "E1578", {"start": v(-9.69, 250.84) * mm, "end": v(-10.01, 252.36) * mm});
            skLineSegment(sketch, "E1579", {"start": v(-10.01, 252.36) * mm, "end": v(-10.45, 253.87) * mm});
            skLineSegment(sketch, "E1580", {"start": v(-10.45, 253.87) * mm, "end": v(-11.1, 255.28) * mm});
            skLineSegment(sketch, "E1581", {"start": v(-11.1, 255.28) * mm, "end": v(-11.96, 256.68) * mm});
            skLineSegment(sketch, "E1582", {"start": v(-11.96, 256.68) * mm, "end": v(-12.93, 257.87) * mm});
            skLineSegment(sketch, "E1583", {"start": v(-12.93, 257.87) * mm, "end": v(-14.02, 258.96) * mm});
            skLineSegment(sketch, "E1584", {"start": v(-14.02, 258.96) * mm, "end": v(-15.31, 259.93) * mm});
            skLineSegment(sketch, "E1585", {"start": v(-15.31, 259.93) * mm, "end": v(-16.61, 260.8) * mm});
            skLineSegment(sketch, "E1586", {"start": v(-16.61, 260.8) * mm, "end": v(-18.02, 261.45) * mm});
            skLineSegment(sketch, "E1587", {"start": v(-18.02, 261.45) * mm, "end": v(-19.54, 261.88) * mm});
            skLineSegment(sketch, "E1588", {"start": v(-19.54, 261.88) * mm, "end": v(-21.16, 262.2) * mm});
            skLineSegment(sketch, "E1589", {"start": v(-21.16, 262.2) * mm, "end": v(-22.67, 262.3) * mm});
            skLineSegment(sketch, "E1590", {"start": v(-22.67, 262.3) * mm, "end": v(-24.3, 262.2) * mm});
            skLineSegment(sketch, "E1591", {"start": v(-24.3, 262.2) * mm, "end": v(-25.81, 261.88) * mm});
            skLineSegment(sketch, "E1592", {"start": v(-25.81, 261.88) * mm, "end": v(-27.33, 261.45) * mm});
            skLineSegment(sketch, "E1593", {"start": v(-27.33, 261.45) * mm, "end": v(-28.74, 260.8) * mm});
            skLineSegment(sketch, "E1594", {"start": v(-28.74, 260.8) * mm, "end": v(-30.14, 259.93) * mm});
            skLineSegment(sketch, "E1595", {"start": v(-30.14, 259.93) * mm, "end": v(-31.33, 258.96) * mm});
            skLineSegment(sketch, "E1596", {"start": v(-31.33, 258.96) * mm, "end": v(-32.42, 257.87) * mm});
            skLineSegment(sketch, "E1597", {"start": v(-32.42, 257.87) * mm, "end": v(-33.4, 256.68) * mm});
            skLineSegment(sketch, "E1598", {"start": v(-33.4, 256.68) * mm, "end": v(-34.26, 255.28) * mm});
            skLineSegment(sketch, "E1599", {"start": v(-34.26, 255.28) * mm, "end": v(-34.9, 253.87) * mm});
            skLineSegment(sketch, "E1600", {"start": v(-34.9, 253.87) * mm, "end": v(-35.34, 252.36) * mm});
            skLineSegment(sketch, "E1601", {"start": v(-35.34, 252.36) * mm, "end": v(-35.66, 250.84) * mm});
            skLineSegment(sketch, "E1602", {"start": v(-35.66, 250.84) * mm, "end": v(-35.77, 249.22) * mm});
            skLineSegment(sketch, "E1603", {"start": v(-76.58, 249.97) * mm, "end": v(-76.58, 204.51) * mm});
            skLineSegment(sketch, "E1604", {"start": v(-83.83, 204.51) * mm, "end": v(-83.72, 203.65) * mm});
            skLineSegment(sketch, "E1605", {"start": v(-83.72, 203.65) * mm, "end": v(-83.5, 202.89) * mm});
            skLineSegment(sketch, "E1606", {"start": v(-83.5, 202.89) * mm, "end": v(-83.07, 202.24) * mm});
            skLineSegment(sketch, "E1607", {"start": v(-83.07, 202.24) * mm, "end": v(-82.53, 201.6) * mm});
            skLineSegment(sketch, "E1608", {"start": v(-82.53, 201.6) * mm, "end": v(-81.77, 201.16) * mm});
            skLineSegment(sketch, "E1609", {"start": v(-81.77, 201.16) * mm, "end": v(-81.01, 200.94) * mm});
            skLineSegment(sketch, "E1610", {"start": v(-81.01, 200.94) * mm, "end": v(-80.26, 200.83) * mm});
            skLineSegment(sketch, "E1611", {"start": v(-80.26, 200.83) * mm, "end": v(-79.39, 200.94) * mm});
            skLineSegment(sketch, "E1612", {"start": v(-79.39, 200.94) * mm, "end": v(-78.63, 201.16) * mm});
            skLineSegment(sketch, "E1613", {"start": v(-78.63, 201.16) * mm, "end": v(-77.98, 201.6) * mm});
            skLineSegment(sketch, "E1614", {"start": v(-77.98, 201.6) * mm, "end": v(-77.44, 202.24) * mm});
            skLineSegment(sketch, "E1615", {"start": v(-77.44, 202.24) * mm, "end": v(-77.01, 202.89) * mm});
            skLineSegment(sketch, "E1616", {"start": v(-77.01, 202.89) * mm, "end": v(-76.68, 203.65) * mm});
            skLineSegment(sketch, "E1617", {"start": v(-76.68, 203.65) * mm, "end": v(-76.58, 204.51) * mm});
            skLineSegment(sketch, "E1618", {"start": v(-83.83, 204.51) * mm, "end": v(-83.83, 249.97) * mm});
            skLineSegment(sketch, "E1619", {"start": v(-76.58, 249.97) * mm, "end": v(-76.68, 250.84) * mm});
            skLineSegment(sketch, "E1620", {"start": v(-76.68, 250.84) * mm, "end": v(-77.01, 251.6) * mm});
            skLineSegment(sketch, "E1621", {"start": v(-77.01, 251.6) * mm, "end": v(-77.44, 252.25) * mm});
            skLineSegment(sketch, "E1622", {"start": v(-77.44, 252.25) * mm, "end": v(-77.98, 252.78) * mm});
            skLineSegment(sketch, "E1623", {"start": v(-77.98, 252.78) * mm, "end": v(-78.63, 253.22) * mm});
            skLineSegment(sketch, "E1624", {"start": v(-78.63, 253.22) * mm, "end": v(-79.39, 253.54) * mm});
            skLineSegment(sketch, "E1625", {"start": v(-79.39, 253.54) * mm, "end": v(-80.26, 253.65) * mm});
            skLineSegment(sketch, "E1626", {"start": v(-80.26, 253.65) * mm, "end": v(-81.01, 253.54) * mm});
            skLineSegment(sketch, "E1627", {"start": v(-81.01, 253.54) * mm, "end": v(-81.77, 253.22) * mm});
            skLineSegment(sketch, "E1628", {"start": v(-81.77, 253.22) * mm, "end": v(-82.53, 252.78) * mm});
            skLineSegment(sketch, "E1629", {"start": v(-82.53, 252.78) * mm, "end": v(-83.07, 252.25) * mm});
            skLineSegment(sketch, "E1630", {"start": v(-83.07, 252.25) * mm, "end": v(-83.5, 251.6) * mm});
            skLineSegment(sketch, "E1631", {"start": v(-83.5, 251.6) * mm, "end": v(-83.72, 250.84) * mm});
            skLineSegment(sketch, "E1632", {"start": v(-83.72, 250.84) * mm, "end": v(-83.83, 249.97) * mm});
            skLineSegment(sketch, "E1633", {"start": v(-93.25, 249.22) * mm, "end": v(-93.25, 205.16) * mm});
            skLineSegment(sketch, "E1634", {"start": v(-93.25, 205.16) * mm, "end": v(-93.14, 203.65) * mm});
            skLineSegment(sketch, "E1635", {"start": v(-93.14, 203.65) * mm, "end": v(-92.92, 202.13) * mm});
            skLineSegment(sketch, "E1636", {"start": v(-92.92, 202.13) * mm, "end": v(-92.38, 200.62) * mm});
            skLineSegment(sketch, "E1637", {"start": v(-92.38, 200.62) * mm, "end": v(-91.84, 199.1) * mm});
            skLineSegment(sketch, "E1638", {"start": v(-91.84, 199.1) * mm, "end": v(-90.97, 197.8) * mm});
            skLineSegment(sketch, "E1639", {"start": v(-90.97, 197.8) * mm, "end": v(-90, 196.61) * mm});
            skLineSegment(sketch, "E1640", {"start": v(-90, 196.61) * mm, "end": v(-88.91, 195.42) * mm});
            skLineSegment(sketch, "E1641", {"start": v(-88.91, 195.42) * mm, "end": v(-87.62, 194.45) * mm});
            skLineSegment(sketch, "E1642", {"start": v(-87.62, 194.45) * mm, "end": v(-86.32, 193.69) * mm});
            skLineSegment(sketch, "E1643", {"start": v(-86.32, 193.69) * mm, "end": v(-84.91, 193.04) * mm});
            skLineSegment(sketch, "E1644", {"start": v(-84.91, 193.04) * mm, "end": v(-83.4, 192.5) * mm});
            skLineSegment(sketch, "E1645", {"start": v(-83.4, 192.5) * mm, "end": v(-81.77, 192.28) * mm});
            skLineSegment(sketch, "E1646", {"start": v(-81.77, 192.28) * mm, "end": v(-80.26, 192.18) * mm});
            skLineSegment(sketch, "E1647", {"start": v(-80.26, 192.18) * mm, "end": v(-78.63, 192.28) * mm});
            skLineSegment(sketch, "E1648", {"start": v(-78.63, 192.28) * mm, "end": v(-77.12, 192.5) * mm});
            skLineSegment(sketch, "E1649", {"start": v(-77.12, 192.5) * mm, "end": v(-75.6, 193.04) * mm});
            skLineSegment(sketch, "E1650", {"start": v(-75.6, 193.04) * mm, "end": v(-74.2, 193.69) * mm});
            skLineSegment(sketch, "E1651", {"start": v(-74.2, 193.69) * mm, "end": v(-72.79, 194.45) * mm});
            skLineSegment(sketch, "E1652", {"start": v(-72.79, 194.45) * mm, "end": v(-71.6, 195.42) * mm});
            skLineSegment(sketch, "E1653", {"start": v(-71.6, 195.42) * mm, "end": v(-70.52, 196.61) * mm});
            skLineSegment(sketch, "E1654", {"start": v(-70.52, 196.61) * mm, "end": v(-69.54, 197.8) * mm});
            skLineSegment(sketch, "E1655", {"start": v(-69.54, 197.8) * mm, "end": v(-68.67, 199.1) * mm});
            skLineSegment(sketch, "E1656", {"start": v(-68.67, 199.1) * mm, "end": v(-68.03, 200.62) * mm});
            skLineSegment(sketch, "E1657", {"start": v(-68.03, 200.62) * mm, "end": v(-67.6, 202.13) * mm});
            skLineSegment(sketch, "E1658", {"start": v(-67.6, 202.13) * mm, "end": v(-67.27, 203.65) * mm});
            skLineSegment(sketch, "E1659", {"start": v(-67.27, 203.65) * mm, "end": v(-67.16, 205.16) * mm});
            skLineSegment(sketch, "E1660", {"start": v(-67.16, 205.16) * mm, "end": v(-67.16, 249.22) * mm});
            skLineSegment(sketch, "E1661", {"start": v(-67.16, 249.22) * mm, "end": v(-67.27, 250.84) * mm});
            skLineSegment(sketch, "E1662", {"start": v(-67.27, 250.84) * mm, "end": v(-67.6, 252.36) * mm});
            skLineSegment(sketch, "E1663", {"start": v(-67.6, 252.36) * mm, "end": v(-68.03, 253.87) * mm});
            skLineSegment(sketch, "E1664", {"start": v(-68.03, 253.87) * mm, "end": v(-68.67, 255.28) * mm});
            skLineSegment(sketch, "E1665", {"start": v(-68.67, 255.28) * mm, "end": v(-69.54, 256.68) * mm});
            skLineSegment(sketch, "E1666", {"start": v(-69.54, 256.68) * mm, "end": v(-70.52, 257.87) * mm});
            skLineSegment(sketch, "E1667", {"start": v(-70.52, 257.87) * mm, "end": v(-71.6, 258.96) * mm});
            skLineSegment(sketch, "E1668", {"start": v(-71.6, 258.96) * mm, "end": v(-72.79, 259.93) * mm});
            skLineSegment(sketch, "E1669", {"start": v(-72.79, 259.93) * mm, "end": v(-74.2, 260.8) * mm});
            skLineSegment(sketch, "E1670", {"start": v(-74.2, 260.8) * mm, "end": v(-75.6, 261.45) * mm});
            skLineSegment(sketch, "E1671", {"start": v(-75.6, 261.45) * mm, "end": v(-77.12, 261.88) * mm});
            skLineSegment(sketch, "E1672", {"start": v(-77.12, 261.88) * mm, "end": v(-78.63, 262.2) * mm});
            skLineSegment(sketch, "E1673", {"start": v(-78.63, 262.2) * mm, "end": v(-80.26, 262.3) * mm});
            skLineSegment(sketch, "E1674", {"start": v(-80.26, 262.3) * mm, "end": v(-81.77, 262.2) * mm});
            skLineSegment(sketch, "E1675", {"start": v(-81.77, 262.2) * mm, "end": v(-83.4, 261.88) * mm});
            skLineSegment(sketch, "E1676", {"start": v(-83.4, 261.88) * mm, "end": v(-84.91, 261.45) * mm});
            skLineSegment(sketch, "E1677", {"start": v(-84.91, 261.45) * mm, "end": v(-86.32, 260.8) * mm});
            skLineSegment(sketch, "E1678", {"start": v(-86.32, 260.8) * mm, "end": v(-87.62, 259.93) * mm});
            skLineSegment(sketch, "E1679", {"start": v(-87.62, 259.93) * mm, "end": v(-88.91, 258.96) * mm});
            skLineSegment(sketch, "E1680", {"start": v(-88.91, 258.96) * mm, "end": v(-90, 257.87) * mm});
            skLineSegment(sketch, "E1681", {"start": v(-90, 257.87) * mm, "end": v(-90.97, 256.68) * mm});
            skLineSegment(sketch, "E1682", {"start": v(-90.97, 256.68) * mm, "end": v(-91.84, 255.28) * mm});
            skLineSegment(sketch, "E1683", {"start": v(-91.84, 255.28) * mm, "end": v(-92.38, 253.87) * mm});
            skLineSegment(sketch, "E1684", {"start": v(-92.38, 253.87) * mm, "end": v(-92.92, 252.36) * mm});
            skLineSegment(sketch, "E1685", {"start": v(-92.92, 252.36) * mm, "end": v(-93.14, 250.84) * mm});
            skLineSegment(sketch, "E1686", {"start": v(-93.14, 250.84) * mm, "end": v(-93.25, 249.22) * mm});
            skLineSegment(sketch, "E1687", {"start": v(-246.72, 205.16) * mm, "end": v(-246.62, 203.65) * mm});
            skLineSegment(sketch, "E1688", {"start": v(-246.62, 203.65) * mm, "end": v(-246.3, 202.13) * mm});
            skLineSegment(sketch, "E1689", {"start": v(-246.3, 202.13) * mm, "end": v(-245.86, 200.62) * mm});
            skLineSegment(sketch, "E1690", {"start": v(-245.86, 200.62) * mm, "end": v(-245.21, 199.1) * mm});
            skLineSegment(sketch, "E1691", {"start": v(-245.21, 199.1) * mm, "end": v(-244.34, 197.8) * mm});
            skLineSegment(sketch, "E1692", {"start": v(-244.34, 197.8) * mm, "end": v(-243.37, 196.61) * mm});
            skLineSegment(sketch, "E1693", {"start": v(-243.37, 196.61) * mm, "end": v(-242.29, 195.42) * mm});
            skLineSegment(sketch, "E1694", {"start": v(-242.29, 195.42) * mm, "end": v(-240.99, 194.45) * mm});
            skLineSegment(sketch, "E1695", {"start": v(-240.99, 194.45) * mm, "end": v(-239.69, 193.69) * mm});
            skLineSegment(sketch, "E1696", {"start": v(-239.69, 193.69) * mm, "end": v(-238.28, 193.04) * mm});
            skLineSegment(sketch, "E1697", {"start": v(-238.28, 193.04) * mm, "end": v(-236.77, 192.5) * mm});
            skLineSegment(sketch, "E1698", {"start": v(-236.77, 192.5) * mm, "end": v(-235.25, 192.28) * mm});
            skLineSegment(sketch, "E1699", {"start": v(-235.25, 192.28) * mm, "end": v(-233.63, 192.18) * mm});
            skLineSegment(sketch, "E1700", {"start": v(-233.63, 192.18) * mm, "end": v(-232.11, 192.28) * mm});
            skLineSegment(sketch, "E1701", {"start": v(-232.11, 192.28) * mm, "end": v(-230.49, 192.5) * mm});
            skLineSegment(sketch, "E1702", {"start": v(-230.49, 192.5) * mm, "end": v(-228.97, 193.04) * mm});
            skLineSegment(sketch, "E1703", {"start": v(-228.97, 193.04) * mm, "end": v(-227.57, 193.69) * mm});
            skLineSegment(sketch, "E1704", {"start": v(-227.57, 193.69) * mm, "end": v(-226.27, 194.45) * mm});
            skLineSegment(sketch, "E1705", {"start": v(-226.27, 194.45) * mm, "end": v(-224.97, 195.42) * mm});
            skLineSegment(sketch, "E1706", {"start": v(-224.97, 195.42) * mm, "end": v(-223.89, 196.61) * mm});
            skLineSegment(sketch, "E1707", {"start": v(-223.89, 196.61) * mm, "end": v(-222.91, 197.8) * mm});
            skLineSegment(sketch, "E1708", {"start": v(-222.91, 197.8) * mm, "end": v(-222.05, 199.1) * mm});
            skLineSegment(sketch, "E1709", {"start": v(-222.05, 199.1) * mm, "end": v(-221.4, 200.62) * mm});
            skLineSegment(sketch, "E1710", {"start": v(-221.4, 200.62) * mm, "end": v(-220.96, 202.13) * mm});
            skLineSegment(sketch, "E1711", {"start": v(-220.96, 202.13) * mm, "end": v(-220.64, 203.65) * mm});
            skLineSegment(sketch, "E1712", {"start": v(-220.64, 203.65) * mm, "end": v(-220.64, 205.16) * mm});
            skLineSegment(sketch, "E1713", {"start": v(-220.64, 205.16) * mm, "end": v(-220.64, 216.2) * mm});
            skLineSegment(sketch, "E1714", {"start": v(-220.64, 216.2) * mm, "end": v(-230.06, 216.2) * mm});
            skLineSegment(sketch, "E1715", {"start": v(-230.06, 216.2) * mm, "end": v(-230.06, 204.51) * mm});
            skLineSegment(sketch, "E1716", {"start": v(-237.3, 204.51) * mm, "end": v(-237.2, 203.65) * mm});
            skLineSegment(sketch, "E1717", {"start": v(-237.2, 203.65) * mm, "end": v(-236.88, 202.89) * mm});
            skLineSegment(sketch, "E1718", {"start": v(-236.88, 202.89) * mm, "end": v(-236.44, 202.24) * mm});
            skLineSegment(sketch, "E1719", {"start": v(-236.44, 202.24) * mm, "end": v(-235.9, 201.6) * mm});
            skLineSegment(sketch, "E1720", {"start": v(-235.9, 201.6) * mm, "end": v(-235.25, 201.16) * mm});
            skLineSegment(sketch, "E1721", {"start": v(-235.25, 201.16) * mm, "end": v(-234.39, 200.94) * mm});
            skLineSegment(sketch, "E1722", {"start": v(-234.39, 200.94) * mm, "end": v(-233.63, 200.83) * mm});
            skLineSegment(sketch, "E1723", {"start": v(-233.63, 200.83) * mm, "end": v(-232.87, 200.94) * mm});
            skLineSegment(sketch, "E1724", {"start": v(-232.87, 200.94) * mm, "end": v(-232.11, 201.16) * mm});
            skLineSegment(sketch, "E1725", {"start": v(-232.11, 201.16) * mm, "end": v(-231.36, 201.6) * mm});
            skLineSegment(sketch, "E1726", {"start": v(-231.36, 201.6) * mm, "end": v(-230.82, 202.24) * mm});
            skLineSegment(sketch, "E1727", {"start": v(-230.82, 202.24) * mm, "end": v(-230.38, 202.89) * mm});
            skLineSegment(sketch, "E1728", {"start": v(-230.38, 202.89) * mm, "end": v(-230.06, 203.65) * mm});
            skLineSegment(sketch, "E1729", {"start": v(-230.06, 203.65) * mm, "end": v(-230.06, 204.51) * mm});
            skLineSegment(sketch, "E1730", {"start": v(-237.3, 204.51) * mm, "end": v(-237.3, 249.97) * mm});
            skLineSegment(sketch, "E1731", {"start": v(-230.06, 249.97) * mm, "end": v(-230.06, 250.84) * mm});
            skLineSegment(sketch, "E1732", {"start": v(-230.06, 250.84) * mm, "end": v(-230.38, 251.6) * mm});
            skLineSegment(sketch, "E1733", {"start": v(-230.38, 251.6) * mm, "end": v(-230.82, 252.25) * mm});
            skLineSegment(sketch, "E1734", {"start": v(-230.82, 252.25) * mm, "end": v(-231.36, 252.78) * mm});
            skLineSegment(sketch, "E1735", {"start": v(-231.36, 252.78) * mm, "end": v(-232.11, 253.22) * mm});
            skLineSegment(sketch, "E1736", {"start": v(-232.11, 253.22) * mm, "end": v(-232.87, 253.54) * mm});
            skLineSegment(sketch, "E1737", {"start": v(-232.87, 253.54) * mm, "end": v(-233.63, 253.65) * mm});
            skLineSegment(sketch, "E1738", {"start": v(-233.63, 253.65) * mm, "end": v(-234.39, 253.54) * mm});
            skLineSegment(sketch, "E1739", {"start": v(-234.39, 253.54) * mm, "end": v(-235.25, 253.22) * mm});
            skLineSegment(sketch, "E1740", {"start": v(-235.25, 253.22) * mm, "end": v(-235.9, 252.78) * mm});
            skLineSegment(sketch, "E1741", {"start": v(-235.9, 252.78) * mm, "end": v(-236.44, 252.25) * mm});
            skLineSegment(sketch, "E1742", {"start": v(-236.44, 252.25) * mm, "end": v(-236.88, 251.6) * mm});
            skLineSegment(sketch, "E1743", {"start": v(-236.88, 251.6) * mm, "end": v(-237.2, 250.84) * mm});
            skLineSegment(sketch, "E1744", {"start": v(-237.2, 250.84) * mm, "end": v(-237.3, 249.97) * mm});
            skLineSegment(sketch, "E1745", {"start": v(-230.06, 249.97) * mm, "end": v(-230.06, 238.28) * mm});
            skLineSegment(sketch, "E1746", {"start": v(-230.06, 238.28) * mm, "end": v(-220.64, 238.28) * mm});
            skLineSegment(sketch, "E1747", {"start": v(-220.64, 238.28) * mm, "end": v(-220.64, 249.22) * mm});
            skLineSegment(sketch, "E1748", {"start": v(-220.64, 249.22) * mm, "end": v(-220.64, 250.84) * mm});
            skLineSegment(sketch, "E1749", {"start": v(-220.64, 250.84) * mm, "end": v(-220.96, 252.36) * mm});
            skLineSegment(sketch, "E1750", {"start": v(-220.96, 252.36) * mm, "end": v(-221.4, 253.87) * mm});
            skLineSegment(sketch, "E1751", {"start": v(-221.4, 253.87) * mm, "end": v(-222.05, 255.28) * mm});
            skLineSegment(sketch, "E1752", {"start": v(-222.05, 255.28) * mm, "end": v(-222.91, 256.68) * mm});
            skLineSegment(sketch, "E1753", {"start": v(-222.91, 256.68) * mm, "end": v(-223.89, 257.87) * mm});
            skLineSegment(sketch, "E1754", {"start": v(-223.89, 257.87) * mm, "end": v(-224.97, 258.96) * mm});
            skLineSegment(sketch, "E1755", {"start": v(-224.97, 258.96) * mm, "end": v(-226.27, 259.93) * mm});
            skLineSegment(sketch, "E1756", {"start": v(-226.27, 259.93) * mm, "end": v(-227.57, 260.8) * mm});
            skLineSegment(sketch, "E1757", {"start": v(-227.57, 260.8) * mm, "end": v(-228.97, 261.45) * mm});
            skLineSegment(sketch, "E1758", {"start": v(-228.97, 261.45) * mm, "end": v(-230.49, 261.88) * mm});
            skLineSegment(sketch, "E1759", {"start": v(-230.49, 261.88) * mm, "end": v(-232.11, 262.2) * mm});
            skLineSegment(sketch, "E1760", {"start": v(-232.11, 262.2) * mm, "end": v(-233.63, 262.3) * mm});
            skLineSegment(sketch, "E1761", {"start": v(-233.63, 262.3) * mm, "end": v(-235.25, 262.2) * mm});
            skLineSegment(sketch, "E1762", {"start": v(-235.25, 262.2) * mm, "end": v(-236.77, 261.88) * mm});
            skLineSegment(sketch, "E1763", {"start": v(-236.77, 261.88) * mm, "end": v(-238.28, 261.45) * mm});
            skLineSegment(sketch, "E1764", {"start": v(-238.28, 261.45) * mm, "end": v(-239.69, 260.8) * mm});
            skLineSegment(sketch, "E1765", {"start": v(-239.69, 260.8) * mm, "end": v(-240.99, 259.93) * mm});
            skLineSegment(sketch, "E1766", {"start": v(-240.99, 259.93) * mm, "end": v(-242.29, 258.96) * mm});
            skLineSegment(sketch, "E1767", {"start": v(-242.29, 258.96) * mm, "end": v(-243.37, 257.87) * mm});
            skLineSegment(sketch, "E1768", {"start": v(-243.37, 257.87) * mm, "end": v(-244.34, 256.68) * mm});
            skLineSegment(sketch, "E1769", {"start": v(-244.34, 256.68) * mm, "end": v(-245.21, 255.28) * mm});
            skLineSegment(sketch, "E1770", {"start": v(-245.21, 255.28) * mm, "end": v(-245.86, 253.87) * mm});
            skLineSegment(sketch, "E1771", {"start": v(-245.86, 253.87) * mm, "end": v(-246.3, 252.36) * mm});
            skLineSegment(sketch, "E1772", {"start": v(-246.3, 252.36) * mm, "end": v(-246.62, 250.84) * mm});
            skLineSegment(sketch, "E1773", {"start": v(-246.62, 250.84) * mm, "end": v(-246.72, 249.22) * mm});
            skLineSegment(sketch, "E1774", {"start": v(-246.72, 249.22) * mm, "end": v(-246.72, 205.16) * mm});
            skLineSegment(sketch, "E1775", {"start": v(-169.99, 205.16) * mm, "end": v(-169.88, 203.65) * mm});
            skLineSegment(sketch, "E1776", {"start": v(-169.88, 203.65) * mm, "end": v(-169.66, 202.13) * mm});
            skLineSegment(sketch, "E1777", {"start": v(-169.66, 202.13) * mm, "end": v(-169.12, 200.62) * mm});
            skLineSegment(sketch, "E1778", {"start": v(-169.12, 200.62) * mm, "end": v(-168.47, 199.1) * mm});
            skLineSegment(sketch, "E1779", {"start": v(-168.47, 199.1) * mm, "end": v(-167.71, 197.8) * mm});
            skLineSegment(sketch, "E1780", {"start": v(-167.71, 197.8) * mm, "end": v(-166.74, 196.61) * mm});
            skLineSegment(sketch, "E1781", {"start": v(-166.74, 196.61) * mm, "end": v(-165.55, 195.42) * mm});
            skLineSegment(sketch, "E1782", {"start": v(-165.55, 195.42) * mm, "end": v(-164.36, 194.45) * mm});
            skLineSegment(sketch, "E1783", {"start": v(-164.36, 194.45) * mm, "end": v(-163.06, 193.69) * mm});
            skLineSegment(sketch, "E1784", {"start": v(-163.06, 193.69) * mm, "end": v(-161.54, 193.04) * mm});
            skLineSegment(sketch, "E1785", {"start": v(-161.54, 193.04) * mm, "end": v(-160.03, 192.5) * mm});
            skLineSegment(sketch, "E1786", {"start": v(-160.03, 192.5) * mm, "end": v(-158.51, 192.28) * mm});
            skLineSegment(sketch, "E1787", {"start": v(-158.51, 192.28) * mm, "end": v(-157, 192.18) * mm});
            skLineSegment(sketch, "E1788", {"start": v(-157, 192.18) * mm, "end": v(-155.37, 192.28) * mm});
            skLineSegment(sketch, "E1789", {"start": v(-155.37, 192.28) * mm, "end": v(-153.86, 192.5) * mm});
            skLineSegment(sketch, "E1790", {"start": v(-153.86, 192.5) * mm, "end": v(-152.34, 193.04) * mm});
            skLineSegment(sketch, "E1791", {"start": v(-152.34, 193.04) * mm, "end": v(-150.94, 193.69) * mm});
            skLineSegment(sketch, "E1792", {"start": v(-150.94, 193.69) * mm, "end": v(-149.53, 194.45) * mm});
            skLineSegment(sketch, "E1793", {"start": v(-149.53, 194.45) * mm, "end": v(-148.34, 195.42) * mm});
            skLineSegment(sketch, "E1794", {"start": v(-148.34, 195.42) * mm, "end": v(-147.15, 196.61) * mm});
            skLineSegment(sketch, "E1795", {"start": v(-147.15, 196.61) * mm, "end": v(-146.17, 197.8) * mm});
            skLineSegment(sketch, "E1796", {"start": v(-146.17, 197.8) * mm, "end": v(-145.42, 199.1) * mm});
            skLineSegment(sketch, "E1797", {"start": v(-145.42, 199.1) * mm, "end": v(-144.77, 200.62) * mm});
            skLineSegment(sketch, "E1798", {"start": v(-144.77, 200.62) * mm, "end": v(-144.33, 202.13) * mm});
            skLineSegment(sketch, "E1799", {"start": v(-144.33, 202.13) * mm, "end": v(-144, 203.65) * mm});
            skLineSegment(sketch, "E1800", {"start": v(-144, 203.65) * mm, "end": v(-143.9, 205.16) * mm});
            skLineSegment(sketch, "E1801", {"start": v(-143.9, 205.16) * mm, "end": v(-143.9, 216.2) * mm});
            skLineSegment(sketch, "E1802", {"start": v(-143.9, 216.2) * mm, "end": v(-153.32, 216.2) * mm});
            skLineSegment(sketch, "E1803", {"start": v(-153.32, 216.2) * mm, "end": v(-153.32, 204.51) * mm});
            skLineSegment(sketch, "E1804", {"start": v(-160.57, 204.51) * mm, "end": v(-160.46, 203.65) * mm});
            skLineSegment(sketch, "E1805", {"start": v(-160.46, 203.65) * mm, "end": v(-160.24, 202.89) * mm});
            skLineSegment(sketch, "E1806", {"start": v(-160.24, 202.89) * mm, "end": v(-159.81, 202.24) * mm});
            skLineSegment(sketch, "E1807", {"start": v(-159.81, 202.24) * mm, "end": v(-159.16, 201.6) * mm});
            skLineSegment(sketch, "E1808", {"start": v(-159.16, 201.6) * mm, "end": v(-158.51, 201.16) * mm});
            skLineSegment(sketch, "E1809", {"start": v(-158.51, 201.16) * mm, "end": v(-157.76, 200.94) * mm});
            skLineSegment(sketch, "E1810", {"start": v(-157.76, 200.94) * mm, "end": v(-157, 200.83) * mm});
            skLineSegment(sketch, "E1811", {"start": v(-157, 200.83) * mm, "end": v(-156.13, 200.94) * mm});
            skLineSegment(sketch, "E1812", {"start": v(-156.13, 200.94) * mm, "end": v(-155.37, 201.16) * mm});
            skLineSegment(sketch, "E1813", {"start": v(-155.37, 201.16) * mm, "end": v(-154.73, 201.6) * mm});
            skLineSegment(sketch, "E1814", {"start": v(-154.73, 201.6) * mm, "end": v(-154.07, 202.24) * mm});
            skLineSegment(sketch, "E1815", {"start": v(-154.07, 202.24) * mm, "end": v(-153.64, 202.89) * mm});
            skLineSegment(sketch, "E1816", {"start": v(-153.64, 202.89) * mm, "end": v(-153.42, 203.65) * mm});
            skLineSegment(sketch, "E1817", {"start": v(-153.42, 203.65) * mm, "end": v(-153.32, 204.51) * mm});
            skLineSegment(sketch, "E1818", {"start": v(-160.57, 204.51) * mm, "end": v(-160.57, 249.97) * mm});
            skLineSegment(sketch, "E1819", {"start": v(-153.32, 249.97) * mm, "end": v(-153.42, 250.84) * mm});
            skLineSegment(sketch, "E1820", {"start": v(-153.42, 250.84) * mm, "end": v(-153.64, 251.6) * mm});
            skLineSegment(sketch, "E1821", {"start": v(-153.64, 251.6) * mm, "end": v(-154.07, 252.25) * mm});
            skLineSegment(sketch, "E1822", {"start": v(-154.07, 252.25) * mm, "end": v(-154.73, 252.78) * mm});
            skLineSegment(sketch, "E1823", {"start": v(-154.73, 252.78) * mm, "end": v(-155.37, 253.22) * mm});
            skLineSegment(sketch, "E1824", {"start": v(-155.37, 253.22) * mm, "end": v(-156.13, 253.54) * mm});
            skLineSegment(sketch, "E1825", {"start": v(-156.13, 253.54) * mm, "end": v(-157, 253.65) * mm});
            skLineSegment(sketch, "E1826", {"start": v(-157, 253.65) * mm, "end": v(-157.76, 253.54) * mm});
            skLineSegment(sketch, "E1827", {"start": v(-157.76, 253.54) * mm, "end": v(-158.51, 253.22) * mm});
            skLineSegment(sketch, "E1828", {"start": v(-158.51, 253.22) * mm, "end": v(-159.16, 252.78) * mm});
            skLineSegment(sketch, "E1829", {"start": v(-159.16, 252.78) * mm, "end": v(-159.81, 252.25) * mm});
            skLineSegment(sketch, "E1830", {"start": v(-159.81, 252.25) * mm, "end": v(-160.24, 251.6) * mm});
            skLineSegment(sketch, "E1831", {"start": v(-160.24, 251.6) * mm, "end": v(-160.46, 250.84) * mm});
            skLineSegment(sketch, "E1832", {"start": v(-160.46, 250.84) * mm, "end": v(-160.57, 249.97) * mm});
            skLineSegment(sketch, "E1833", {"start": v(-153.32, 249.97) * mm, "end": v(-153.32, 238.28) * mm});
            skLineSegment(sketch, "E1834", {"start": v(-153.32, 238.28) * mm, "end": v(-143.9, 238.28) * mm});
            skLineSegment(sketch, "E1835", {"start": v(-143.9, 238.28) * mm, "end": v(-143.9, 249.22) * mm});
            skLineSegment(sketch, "E1836", {"start": v(-143.9, 249.22) * mm, "end": v(-144, 250.84) * mm});
            skLineSegment(sketch, "E1837", {"start": v(-144, 250.84) * mm, "end": v(-144.33, 252.36) * mm});
            skLineSegment(sketch, "E1838", {"start": v(-144.33, 252.36) * mm, "end": v(-144.77, 253.87) * mm});
            skLineSegment(sketch, "E1839", {"start": v(-144.77, 253.87) * mm, "end": v(-145.42, 255.28) * mm});
            skLineSegment(sketch, "E1840", {"start": v(-145.42, 255.28) * mm, "end": v(-146.17, 256.68) * mm});
            skLineSegment(sketch, "E1841", {"start": v(-146.17, 256.68) * mm, "end": v(-147.15, 257.87) * mm});
            skLineSegment(sketch, "E1842", {"start": v(-147.15, 257.87) * mm, "end": v(-148.34, 258.96) * mm});
            skLineSegment(sketch, "E1843", {"start": v(-148.34, 258.96) * mm, "end": v(-149.53, 259.93) * mm});
            skLineSegment(sketch, "E1844", {"start": v(-149.53, 259.93) * mm, "end": v(-150.94, 260.8) * mm});
            skLineSegment(sketch, "E1845", {"start": v(-150.94, 260.8) * mm, "end": v(-152.34, 261.45) * mm});
            skLineSegment(sketch, "E1846", {"start": v(-152.34, 261.45) * mm, "end": v(-153.86, 261.88) * mm});
            skLineSegment(sketch, "E1847", {"start": v(-153.86, 261.88) * mm, "end": v(-155.37, 262.2) * mm});
            skLineSegment(sketch, "E1848", {"start": v(-155.37, 262.2) * mm, "end": v(-157, 262.3) * mm});
            skLineSegment(sketch, "E1849", {"start": v(-157, 262.3) * mm, "end": v(-158.51, 262.2) * mm});
            skLineSegment(sketch, "E1850", {"start": v(-158.51, 262.2) * mm, "end": v(-160.03, 261.88) * mm});
            skLineSegment(sketch, "E1851", {"start": v(-160.03, 261.88) * mm, "end": v(-161.54, 261.45) * mm});
            skLineSegment(sketch, "E1852", {"start": v(-161.54, 261.45) * mm, "end": v(-163.06, 260.8) * mm});
            skLineSegment(sketch, "E1853", {"start": v(-163.06, 260.8) * mm, "end": v(-164.36, 259.93) * mm});
            skLineSegment(sketch, "E1854", {"start": v(-164.36, 259.93) * mm, "end": v(-165.55, 258.96) * mm});
            skLineSegment(sketch, "E1855", {"start": v(-165.55, 258.96) * mm, "end": v(-166.74, 257.87) * mm});
            skLineSegment(sketch, "E1856", {"start": v(-166.74, 257.87) * mm, "end": v(-167.71, 256.68) * mm});
            skLineSegment(sketch, "E1857", {"start": v(-167.71, 256.68) * mm, "end": v(-168.47, 255.28) * mm});
            skLineSegment(sketch, "E1858", {"start": v(-168.47, 255.28) * mm, "end": v(-169.12, 253.87) * mm});
            skLineSegment(sketch, "E1859", {"start": v(-169.12, 253.87) * mm, "end": v(-169.66, 252.36) * mm});
            skLineSegment(sketch, "E1860", {"start": v(-169.66, 252.36) * mm, "end": v(-169.88, 250.84) * mm});
            skLineSegment(sketch, "E1861", {"start": v(-169.88, 250.84) * mm, "end": v(-169.99, 249.22) * mm});
            skLineSegment(sketch, "E1862", {"start": v(-169.99, 249.22) * mm, "end": v(-169.99, 205.16) * mm});
            skLineSegment(sketch, "E1863", {"start": v(129.07, 262.3) * mm, "end": v(119.77, 262.3) * mm});
            skLineSegment(sketch, "E1864", {"start": v(119.77, 262.3) * mm, "end": v(119.77, 192.18) * mm});
            skLineSegment(sketch, "E1865", {"start": v(119.77, 192.18) * mm, "end": v(129.07, 192.18) * mm});
            skLineSegment(sketch, "E1866", {"start": v(129.07, 192.18) * mm, "end": v(129.07, 231.79) * mm});
            skLineSegment(sketch, "E1867", {"start": v(129.07, 231.79) * mm, "end": v(130.05, 231.79) * mm});
            skLineSegment(sketch, "E1868", {"start": v(130.05, 231.79) * mm, "end": v(140.54, 192.18) * mm});
            skLineSegment(sketch, "E1869", {"start": v(140.54, 192.18) * mm, "end": v(149.31, 192.18) * mm});
            skLineSegment(sketch, "E1870", {"start": v(149.31, 192.18) * mm, "end": v(149.31, 262.3) * mm});
            skLineSegment(sketch, "E1871", {"start": v(149.31, 262.3) * mm, "end": v(140.54, 262.3) * mm});
            skLineSegment(sketch, "E1872", {"start": v(140.54, 262.3) * mm, "end": v(140.54, 221.83) * mm});
            skLineSegment(sketch, "E1873", {"start": v(140.54, 221.83) * mm, "end": v(139.36, 221.83) * mm});
            skLineSegment(sketch, "E1874", {"start": v(139.36, 221.83) * mm, "end": v(129.07, 262.3) * mm});
            skLineSegment(sketch, "E1875", {"start": v(57.53, 249.97) * mm, "end": v(57.53, 238.28) * mm});
            skLineSegment(sketch, "E1876", {"start": v(57.53, 238.28) * mm, "end": v(66.95, 238.28) * mm});
            skLineSegment(sketch, "E1877", {"start": v(66.95, 238.28) * mm, "end": v(66.95, 249.22) * mm});
            skLineSegment(sketch, "E1878", {"start": v(66.95, 249.22) * mm, "end": v(66.84, 250.84) * mm});
            skLineSegment(sketch, "E1879", {"start": v(66.84, 250.84) * mm, "end": v(66.62, 252.36) * mm});
            skLineSegment(sketch, "E1880", {"start": v(66.62, 252.36) * mm, "end": v(66.08, 253.87) * mm});
            skLineSegment(sketch, "E1881", {"start": v(66.08, 253.87) * mm, "end": v(65.43, 255.28) * mm});
            skLineSegment(sketch, "E1882", {"start": v(65.43, 255.28) * mm, "end": v(64.67, 256.68) * mm});
            skLineSegment(sketch, "E1883", {"start": v(64.67, 256.68) * mm, "end": v(63.7, 257.87) * mm});
            skLineSegment(sketch, "E1884", {"start": v(63.7, 257.87) * mm, "end": v(62.5, 258.96) * mm});
            skLineSegment(sketch, "E1885", {"start": v(62.5, 258.96) * mm, "end": v(61.31, 259.93) * mm});
            skLineSegment(sketch, "E1886", {"start": v(61.31, 259.93) * mm, "end": v(60.02, 260.8) * mm});
            skLineSegment(sketch, "E1887", {"start": v(60.02, 260.8) * mm, "end": v(58.5, 261.45) * mm});
            skLineSegment(sketch, "E1888", {"start": v(58.5, 261.45) * mm, "end": v(56.99, 261.88) * mm});
            skLineSegment(sketch, "E1889", {"start": v(56.99, 261.88) * mm, "end": v(55.47, 262.2) * mm});
            skLineSegment(sketch, "E1890", {"start": v(55.47, 262.2) * mm, "end": v(53.96, 262.3) * mm});
            skLineSegment(sketch, "E1891", {"start": v(53.96, 262.3) * mm, "end": v(52.33, 262.2) * mm});
            skLineSegment(sketch, "E1892", {"start": v(52.33, 262.2) * mm, "end": v(50.82, 261.88) * mm});
            skLineSegment(sketch, "E1893", {"start": v(50.82, 261.88) * mm, "end": v(49.3, 261.45) * mm});
            skLineSegment(sketch, "E1894", {"start": v(49.3, 261.45) * mm, "end": v(47.9, 260.8) * mm});
            skLineSegment(sketch, "E1895", {"start": v(47.9, 260.8) * mm, "end": v(46.49, 259.93) * mm});
            skLineSegment(sketch, "E1896", {"start": v(46.49, 259.93) * mm, "end": v(45.3, 258.96) * mm});
            skLineSegment(sketch, "E1897", {"start": v(45.3, 258.96) * mm, "end": v(44.1, 257.87) * mm});
            skLineSegment(sketch, "E1898", {"start": v(44.1, 257.87) * mm, "end": v(43.13, 256.68) * mm});
            skLineSegment(sketch, "E1899", {"start": v(43.13, 256.68) * mm, "end": v(42.37, 255.28) * mm});
            skLineSegment(sketch, "E1900", {"start": v(42.37, 255.28) * mm, "end": v(41.73, 253.87) * mm});
            skLineSegment(sketch, "E1901", {"start": v(41.73, 253.87) * mm, "end": v(41.19, 252.36) * mm});
            skLineSegment(sketch, "E1902", {"start": v(41.19, 252.36) * mm, "end": v(40.97, 250.84) * mm});
            skLineSegment(sketch, "E1903", {"start": v(40.97, 250.84) * mm, "end": v(40.86, 249.22) * mm});
            skLineSegment(sketch, "E1904", {"start": v(40.86, 249.22) * mm, "end": v(40.86, 205.16) * mm});
            skLineSegment(sketch, "E1905", {"start": v(40.86, 205.16) * mm, "end": v(40.97, 203.65) * mm});
            skLineSegment(sketch, "E1906", {"start": v(40.97, 203.65) * mm, "end": v(41.19, 202.13) * mm});
            skLineSegment(sketch, "E1907", {"start": v(41.19, 202.13) * mm, "end": v(41.73, 200.62) * mm});
            skLineSegment(sketch, "E1908", {"start": v(41.73, 200.62) * mm, "end": v(42.37, 199.1) * mm});
            skLineSegment(sketch, "E1909", {"start": v(42.37, 199.1) * mm, "end": v(43.13, 197.8) * mm});
            skLineSegment(sketch, "E1910", {"start": v(43.13, 197.8) * mm, "end": v(44.1, 196.61) * mm});
            skLineSegment(sketch, "E1911", {"start": v(44.1, 196.61) * mm, "end": v(45.3, 195.42) * mm});
            skLineSegment(sketch, "E1912", {"start": v(45.3, 195.42) * mm, "end": v(46.49, 194.45) * mm});
            skLineSegment(sketch, "E1913", {"start": v(46.49, 194.45) * mm, "end": v(47.9, 193.69) * mm});
            skLineSegment(sketch, "E1914", {"start": v(47.9, 193.69) * mm, "end": v(49.3, 193.04) * mm});
            skLineSegment(sketch, "E1915", {"start": v(49.3, 193.04) * mm, "end": v(50.82, 192.5) * mm});
            skLineSegment(sketch, "E1916", {"start": v(50.82, 192.5) * mm, "end": v(52.33, 192.28) * mm});
            skLineSegment(sketch, "E1917", {"start": v(52.33, 192.28) * mm, "end": v(53.96, 192.18) * mm});
            skLineSegment(sketch, "E1918", {"start": v(53.96, 192.18) * mm, "end": v(55.04, 192.4) * mm});
            skLineSegment(sketch, "E1919", {"start": v(55.04, 192.4) * mm, "end": v(56.23, 192.71) * mm});
            skLineSegment(sketch, "E1920", {"start": v(56.23, 192.71) * mm, "end": v(57.2, 193.25) * mm});
            skLineSegment(sketch, "E1921", {"start": v(57.2, 193.25) * mm, "end": v(58.18, 194.01) * mm});
            skLineSegment(sketch, "E1922", {"start": v(58.18, 194.01) * mm, "end": v(59.04, 194.88) * mm});
            skLineSegment(sketch, "E1923", {"start": v(59.04, 194.88) * mm, "end": v(59.7, 195.85) * mm});
            skLineSegment(sketch, "E1924", {"start": v(59.7, 195.85) * mm, "end": v(61.42, 194.66) * mm});
            skLineSegment(sketch, "E1925", {"start": v(61.42, 194.66) * mm, "end": v(61.42, 192.18) * mm});
            skLineSegment(sketch, "E1926", {"start": v(61.42, 192.18) * mm, "end": v(66.95, 192.18) * mm});
            skLineSegment(sketch, "E1927", {"start": v(66.95, 192.18) * mm, "end": v(66.95, 226.7) * mm});
            skLineSegment(sketch, "E1928", {"start": v(66.95, 226.7) * mm, "end": v(53.74, 226.7) * mm});
            skLineSegment(sketch, "E1929", {"start": v(53.74, 226.7) * mm, "end": v(53.74, 218.37) * mm});
            skLineSegment(sketch, "E1930", {"start": v(53.74, 218.37) * mm, "end": v(57.53, 218.37) * mm});
            skLineSegment(sketch, "E1931", {"start": v(57.53, 218.37) * mm, "end": v(57.53, 204.51) * mm});
            skLineSegment(sketch, "E1932", {"start": v(50.28, 204.51) * mm, "end": v(50.38, 203.65) * mm});
            skLineSegment(sketch, "E1933", {"start": v(50.38, 203.65) * mm, "end": v(50.6, 202.89) * mm});
            skLineSegment(sketch, "E1934", {"start": v(50.6, 202.89) * mm, "end": v(51.04, 202.24) * mm});
            skLineSegment(sketch, "E1935", {"start": v(51.04, 202.24) * mm, "end": v(51.69, 201.6) * mm});
            skLineSegment(sketch, "E1936", {"start": v(51.69, 201.6) * mm, "end": v(52.33, 201.16) * mm});
            skLineSegment(sketch, "E1937", {"start": v(52.33, 201.16) * mm, "end": v(53.1, 200.94) * mm});
            skLineSegment(sketch, "E1938", {"start": v(53.1, 200.94) * mm, "end": v(53.96, 200.83) * mm});
            skLineSegment(sketch, "E1939", {"start": v(53.96, 200.83) * mm, "end": v(54.72, 200.94) * mm});
            skLineSegment(sketch, "E1940", {"start": v(54.72, 200.94) * mm, "end": v(55.47, 201.16) * mm});
            skLineSegment(sketch, "E1941", {"start": v(55.47, 201.16) * mm, "end": v(56.12, 201.6) * mm});
            skLineSegment(sketch, "E1942", {"start": v(56.12, 201.6) * mm, "end": v(56.77, 202.24) * mm});
            skLineSegment(sketch, "E1943", {"start": v(56.77, 202.24) * mm, "end": v(57.2, 202.89) * mm});
            skLineSegment(sketch, "E1944", {"start": v(57.2, 202.89) * mm, "end": v(57.42, 203.65) * mm});
            skLineSegment(sketch, "E1945", {"start": v(57.42, 203.65) * mm, "end": v(57.53, 204.51) * mm});
            skLineSegment(sketch, "E1946", {"start": v(50.28, 204.51) * mm, "end": v(50.28, 249.97) * mm});
            skLineSegment(sketch, "E1947", {"start": v(57.53, 249.97) * mm, "end": v(57.42, 250.84) * mm});
            skLineSegment(sketch, "E1948", {"start": v(57.42, 250.84) * mm, "end": v(57.2, 251.6) * mm});
            skLineSegment(sketch, "E1949", {"start": v(57.2, 251.6) * mm, "end": v(56.77, 252.25) * mm});
            skLineSegment(sketch, "E1950", {"start": v(56.77, 252.25) * mm, "end": v(56.12, 252.78) * mm});
            skLineSegment(sketch, "E1951", {"start": v(56.12, 252.78) * mm, "end": v(55.47, 253.22) * mm});
            skLineSegment(sketch, "E1952", {"start": v(55.47, 253.22) * mm, "end": v(54.72, 253.54) * mm});
            skLineSegment(sketch, "E1953", {"start": v(54.72, 253.54) * mm, "end": v(53.96, 253.65) * mm});
            skLineSegment(sketch, "E1954", {"start": v(53.96, 253.65) * mm, "end": v(53.1, 253.54) * mm});
            skLineSegment(sketch, "E1955", {"start": v(53.1, 253.54) * mm, "end": v(52.33, 253.22) * mm});
            skLineSegment(sketch, "E1956", {"start": v(52.33, 253.22) * mm, "end": v(51.69, 252.78) * mm});
            skLineSegment(sketch, "E1957", {"start": v(51.69, 252.78) * mm, "end": v(51.04, 252.25) * mm});
            skLineSegment(sketch, "E1958", {"start": v(51.04, 252.25) * mm, "end": v(50.6, 251.6) * mm});
            skLineSegment(sketch, "E1959", {"start": v(50.6, 251.6) * mm, "end": v(50.38, 250.84) * mm});
            skLineSegment(sketch, "E1960", {"start": v(50.38, 250.84) * mm, "end": v(50.28, 249.97) * mm});
            skLineSegment(sketch, "E1961", {"start": v(18.35, 233.41) * mm, "end": v(19.21, 235.14) * mm});
            skLineSegment(sketch, "E1962", {"start": v(19.21, 235.14) * mm, "end": v(19.86, 236.87) * mm});
            skLineSegment(sketch, "E1963", {"start": v(19.86, 236.87) * mm, "end": v(20.18, 238.72) * mm});
            skLineSegment(sketch, "E1964", {"start": v(20.18, 238.72) * mm, "end": v(20.4, 240.66) * mm});
            skLineSegment(sketch, "E1965", {"start": v(20.4, 240.66) * mm, "end": v(20.4, 242.5) * mm});
            skLineSegment(sketch, "E1966", {"start": v(20.4, 242.5) * mm, "end": v(20.18, 244.45) * mm});
            skLineSegment(sketch, "E1967", {"start": v(20.18, 244.45) * mm, "end": v(19.86, 246.3) * mm});
            skLineSegment(sketch, "E1968", {"start": v(19.86, 246.3) * mm, "end": v(19.21, 248.13) * mm});
            skLineSegment(sketch, "E1969", {"start": v(19.21, 248.13) * mm, "end": v(18.35, 249.75) * mm});
            skLineSegment(sketch, "E1970", {"start": v(12.07, 230.81) * mm, "end": v(13.8, 231.14) * mm});
            skLineSegment(sketch, "E1971", {"start": v(13.8, 231.14) * mm, "end": v(15.42, 231.57) * mm});
            skLineSegment(sketch, "E1972", {"start": v(15.42, 231.57) * mm, "end": v(16.94, 232.44) * mm});
            skLineSegment(sketch, "E1973", {"start": v(16.94, 232.44) * mm, "end": v(18.35, 233.41) * mm});
            skLineSegment(sketch, "E1974", {"start": v(12.07, 230.81) * mm, "end": v(12.07, 252.36) * mm});
            skLineSegment(sketch, "E1975", {"start": v(18.35, 249.75) * mm, "end": v(16.94, 250.84) * mm});
            skLineSegment(sketch, "E1976", {"start": v(16.94, 250.84) * mm, "end": v(15.42, 251.6) * mm});
            skLineSegment(sketch, "E1977", {"start": v(15.42, 251.6) * mm, "end": v(13.8, 252.14) * mm});
            skLineSegment(sketch, "E1978", {"start": v(13.8, 252.14) * mm, "end": v(12.07, 252.36) * mm});
            skLineSegment(sketch, "E1979", {"start": v(12.07, 262.3) * mm, "end": v(2.76, 262.3) * mm});
            skLineSegment(sketch, "E1980", {"start": v(2.76, 262.3) * mm, "end": v(2.76, 192.18) * mm});
            skLineSegment(sketch, "E1981", {"start": v(2.76, 192.18) * mm, "end": v(12.07, 192.18) * mm});
            skLineSegment(sketch, "E1982", {"start": v(12.07, 192.18) * mm, "end": v(12.07, 222.8) * mm});
            skLineSegment(sketch, "E1983", {"start": v(12.07, 222.8) * mm, "end": v(12.83, 222.48) * mm});
            skLineSegment(sketch, "E1984", {"start": v(12.83, 222.48) * mm, "end": v(13.59, 222.37) * mm});
            skLineSegment(sketch, "E1985", {"start": v(13.59, 222.37) * mm, "end": v(14.34, 222.48) * mm});
            skLineSegment(sketch, "E1986", {"start": v(14.34, 222.48) * mm, "end": v(15, 222.8) * mm});
            skLineSegment(sketch, "E1987", {"start": v(15, 222.8) * mm, "end": v(20.4, 192.18) * mm});
            skLineSegment(sketch, "E1988", {"start": v(20.4, 192.18) * mm, "end": v(30.14, 192.18) * mm});
            skLineSegment(sketch, "E1989", {"start": v(30.14, 192.18) * mm, "end": v(24.4, 225.5) * mm});
            skLineSegment(sketch, "E1990", {"start": v(24.4, 225.5) * mm, "end": v(25.7, 227.35) * mm});
            skLineSegment(sketch, "E1991", {"start": v(25.7, 227.35) * mm, "end": v(26.9, 229.4) * mm});
            skLineSegment(sketch, "E1992", {"start": v(26.9, 229.4) * mm, "end": v(27.87, 231.46) * mm});
            skLineSegment(sketch, "E1993", {"start": v(27.87, 231.46) * mm, "end": v(28.63, 233.63) * mm});
            skLineSegment(sketch, "E1994", {"start": v(28.63, 233.63) * mm, "end": v(29.28, 235.9) * mm});
            skLineSegment(sketch, "E1995", {"start": v(29.28, 235.9) * mm, "end": v(29.6, 238.17) * mm});
            skLineSegment(sketch, "E1996", {"start": v(29.6, 238.17) * mm, "end": v(29.82, 240.45) * mm});
            skLineSegment(sketch, "E1997", {"start": v(29.82, 240.45) * mm, "end": v(29.82, 242.72) * mm});
            skLineSegment(sketch, "E1998", {"start": v(29.82, 242.72) * mm, "end": v(29.6, 245.1) * mm});
            skLineSegment(sketch, "E1999", {"start": v(29.6, 245.1) * mm, "end": v(29.28, 247.37) * mm});
            skLineSegment(sketch, "E2000", {"start": v(29.28, 247.37) * mm, "end": v(28.63, 249.54) * mm});
            skLineSegment(sketch, "E2001", {"start": v(28.63, 249.54) * mm, "end": v(27.87, 251.7) * mm});
            skLineSegment(sketch, "E2002", {"start": v(27.87, 251.7) * mm, "end": v(26.9, 253.87) * mm});
            skLineSegment(sketch, "E2003", {"start": v(26.9, 253.87) * mm, "end": v(25.7, 255.82) * mm});
            skLineSegment(sketch, "E2004", {"start": v(25.7, 255.82) * mm, "end": v(24.4, 257.77) * mm});
            skLineSegment(sketch, "E2005", {"start": v(24.4, 257.77) * mm, "end": v(22.9, 258.85) * mm});
            skLineSegment(sketch, "E2006", {"start": v(22.9, 258.85) * mm, "end": v(21.16, 259.82) * mm});
            skLineSegment(sketch, "E2007", {"start": v(21.16, 259.82) * mm, "end": v(19.54, 260.69) * mm});
            skLineSegment(sketch, "E2008", {"start": v(19.54, 260.69) * mm, "end": v(17.7, 261.34) * mm});
            skLineSegment(sketch, "E2009", {"start": v(17.7, 261.34) * mm, "end": v(15.86, 261.77) * mm});
            skLineSegment(sketch, "E2010", {"start": v(15.86, 261.77) * mm, "end": v(14.01, 262.1) * mm});
            skLineSegment(sketch, "E2011", {"start": v(14.01, 262.1) * mm, "end": v(12.07, 262.3) * mm});
            skLineSegment(sketch, "E2012", {"start": v(-50.5, 170.52) * mm, "end": v(-40.1, 170.52) * mm});
            skLineSegment(sketch, "E2013", {"start": v(-45.3, 155.16) * mm, "end": v(-41.94, 132.1) * mm});
            skLineSegment(sketch, "E2014", {"start": v(-41.94, 132.1) * mm, "end": v(-48.65, 132.1) * mm});
            skLineSegment(sketch, "E2015", {"start": v(-48.65, 132.1) * mm, "end": v(-45.3, 155.16) * mm});
            skLineSegment(sketch, "E2016", {"start": v(-40.1, 170.52) * mm, "end": v(-50.5, 170.52) * mm});
            skLineSegment(sketch, "E2017", {"start": v(-50.5, 170.52) * mm, "end": v(-59.15, 111.54) * mm});
            skLineSegment(sketch, "E2018", {"start": v(-59.15, 111.54) * mm, "end": v(-51.68, 111.54) * mm});
            skLineSegment(sketch, "E2019", {"start": v(-51.68, 111.54) * mm, "end": v(-49.95, 123.23) * mm});
            skLineSegment(sketch, "E2020", {"start": v(-49.95, 123.23) * mm, "end": v(-40.64, 123.23) * mm});
            skLineSegment(sketch, "E2021", {"start": v(-40.64, 123.23) * mm, "end": v(-38.91, 111.54) * mm});
            skLineSegment(sketch, "E2022", {"start": v(-38.91, 111.54) * mm, "end": v(-31.55, 111.54) * mm});
            skLineSegment(sketch, "E2023", {"start": v(-31.55, 111.54) * mm, "end": v(-40.1, 170.52) * mm});
            skLineSegment(sketch, "E2024", {"start": v(56.55, 170.52) * mm, "end": v(66.95, 170.52) * mm});
            skLineSegment(sketch, "E2025", {"start": v(61.75, 155.16) * mm, "end": v(65.1, 132.1) * mm});
            skLineSegment(sketch, "E2026", {"start": v(65.1, 132.1) * mm, "end": v(58.4, 132.1) * mm});
            skLineSegment(sketch, "E2027", {"start": v(58.4, 132.1) * mm, "end": v(61.75, 155.16) * mm});
            skLineSegment(sketch, "E2028", {"start": v(66.95, 170.52) * mm, "end": v(56.55, 170.52) * mm});
            skLineSegment(sketch, "E2029", {"start": v(56.55, 170.52) * mm, "end": v(48, 111.54) * mm});
            skLineSegment(sketch, "E2030", {"start": v(48, 111.54) * mm, "end": v(55.36, 111.54) * mm});
            skLineSegment(sketch, "E2031", {"start": v(55.36, 111.54) * mm, "end": v(57.1, 123.23) * mm});
            skLineSegment(sketch, "E2032", {"start": v(57.1, 123.23) * mm, "end": v(66.4, 123.23) * mm});
            skLineSegment(sketch, "E2033", {"start": v(66.4, 123.23) * mm, "end": v(68.13, 111.54) * mm});
            skLineSegment(sketch, "E2034", {"start": v(68.13, 111.54) * mm, "end": v(75.6, 111.54) * mm});
            skLineSegment(sketch, "E2035", {"start": v(75.6, 111.54) * mm, "end": v(66.95, 170.52) * mm});
            skLineSegment(sketch, "E2036", {"start": v(133.73, 170.52) * mm, "end": v(144.12, 170.52) * mm});
            skLineSegment(sketch, "E2037", {"start": v(138.92, 155.16) * mm, "end": v(142.28, 132.1) * mm});
            skLineSegment(sketch, "E2038", {"start": v(142.28, 132.1) * mm, "end": v(135.57, 132.1) * mm});
            skLineSegment(sketch, "E2039", {"start": v(135.57, 132.1) * mm, "end": v(138.92, 155.16) * mm});
            skLineSegment(sketch, "E2040", {"start": v(144.12, 170.52) * mm, "end": v(133.73, 170.52) * mm});
            skLineSegment(sketch, "E2041", {"start": v(133.73, 170.52) * mm, "end": v(125.18, 111.54) * mm});
            skLineSegment(sketch, "E2042", {"start": v(125.18, 111.54) * mm, "end": v(132.54, 111.54) * mm});
            skLineSegment(sketch, "E2043", {"start": v(132.54, 111.54) * mm, "end": v(134.27, 123.23) * mm});
            skLineSegment(sketch, "E2044", {"start": v(134.27, 123.23) * mm, "end": v(143.58, 123.23) * mm});
            skLineSegment(sketch, "E2045", {"start": v(143.58, 123.23) * mm, "end": v(145.3, 111.54) * mm});
            skLineSegment(sketch, "E2046", {"start": v(145.3, 111.54) * mm, "end": v(152.78, 111.54) * mm});
            skLineSegment(sketch, "E2047", {"start": v(152.78, 111.54) * mm, "end": v(144.12, 170.52) * mm});
            skLineSegment(sketch, "E2048", {"start": v(-248.03, 122.47) * mm, "end": v(-247.92, 121.06) * mm});
            skLineSegment(sketch, "E2049", {"start": v(-247.92, 121.06) * mm, "end": v(-247.6, 119.65) * mm});
            skLineSegment(sketch, "E2050", {"start": v(-247.6, 119.65) * mm, "end": v(-247.16, 118.25) * mm});
            skLineSegment(sketch, "E2051", {"start": v(-247.16, 118.25) * mm, "end": v(-246.5, 116.95) * mm});
            skLineSegment(sketch, "E2052", {"start": v(-246.5, 116.95) * mm, "end": v(-245.75, 115.76) * mm});
            skLineSegment(sketch, "E2053", {"start": v(-245.75, 115.76) * mm, "end": v(-244.78, 114.68) * mm});
            skLineSegment(sketch, "E2054", {"start": v(-244.78, 114.68) * mm, "end": v(-243.7, 113.8) * mm});
            skLineSegment(sketch, "E2055", {"start": v(-243.7, 113.8) * mm, "end": v(-242.5, 112.95) * mm});
            skLineSegment(sketch, "E2056", {"start": v(-242.5, 112.95) * mm, "end": v(-241.2, 112.3) * mm});
            skLineSegment(sketch, "E2057", {"start": v(-241.2, 112.3) * mm, "end": v(-239.9, 111.86) * mm});
            skLineSegment(sketch, "E2058", {"start": v(-239.9, 111.86) * mm, "end": v(-238.5, 111.54) * mm});
            skLineSegment(sketch, "E2059", {"start": v(-238.5, 111.54) * mm, "end": v(-235.58, 111.54) * mm});
            skLineSegment(sketch, "E2060", {"start": v(-235.58, 111.54) * mm, "end": v(-234.17, 111.86) * mm});
            skLineSegment(sketch, "E2061", {"start": v(-234.17, 111.86) * mm, "end": v(-232.87, 112.3) * mm});
            skLineSegment(sketch, "E2062", {"start": v(-232.87, 112.3) * mm, "end": v(-231.57, 112.95) * mm});
            skLineSegment(sketch, "E2063", {"start": v(-231.57, 112.95) * mm, "end": v(-230.38, 113.8) * mm});
            skLineSegment(sketch, "E2064", {"start": v(-230.38, 113.8) * mm, "end": v(-229.3, 114.68) * mm});
            skLineSegment(sketch, "E2065", {"start": v(-229.3, 114.68) * mm, "end": v(-228.33, 115.76) * mm});
            skLineSegment(sketch, "E2066", {"start": v(-228.33, 115.76) * mm, "end": v(-227.57, 116.95) * mm});
            skLineSegment(sketch, "E2067", {"start": v(-227.57, 116.95) * mm, "end": v(-226.92, 118.25) * mm});
            skLineSegment(sketch, "E2068", {"start": v(-226.92, 118.25) * mm, "end": v(-226.38, 119.65) * mm});
            skLineSegment(sketch, "E2069", {"start": v(-226.38, 119.65) * mm, "end": v(-226.16, 121.06) * mm});
            skLineSegment(sketch, "E2070", {"start": v(-226.16, 121.06) * mm, "end": v(-226.05, 122.47) * mm});
            skLineSegment(sketch, "E2071", {"start": v(-226.05, 122.47) * mm, "end": v(-226.05, 131.67) * mm});
            skLineSegment(sketch, "E2072", {"start": v(-226.05, 131.67) * mm, "end": v(-233.95, 131.67) * mm});
            skLineSegment(sketch, "E2073", {"start": v(-233.95, 131.67) * mm, "end": v(-233.95, 121.82) * mm});
            skLineSegment(sketch, "E2074", {"start": v(-240.12, 121.82) * mm, "end": v(-240.01, 121.06) * mm});
            skLineSegment(sketch, "E2075", {"start": v(-240.01, 121.06) * mm, "end": v(-239.69, 120.3) * mm});
            skLineSegment(sketch, "E2076", {"start": v(-239.69, 120.3) * mm, "end": v(-239.15, 119.65) * mm});
            skLineSegment(sketch, "E2077", {"start": v(-239.15, 119.65) * mm, "end": v(-238.5, 119.22) * mm});
            skLineSegment(sketch, "E2078", {"start": v(-238.5, 119.22) * mm, "end": v(-237.85, 118.9) * mm});
            skLineSegment(sketch, "E2079", {"start": v(-237.85, 118.9) * mm, "end": v(-236.98, 118.79) * mm});
            skLineSegment(sketch, "E2080", {"start": v(-236.98, 118.79) * mm, "end": v(-236.23, 118.9) * mm});
            skLineSegment(sketch, "E2081", {"start": v(-236.23, 118.9) * mm, "end": v(-235.47, 119.22) * mm});
            skLineSegment(sketch, "E2082", {"start": v(-235.47, 119.22) * mm, "end": v(-234.82, 119.65) * mm});
            skLineSegment(sketch, "E2083", {"start": v(-234.82, 119.65) * mm, "end": v(-234.39, 120.3) * mm});
            skLineSegment(sketch, "E2084", {"start": v(-234.39, 120.3) * mm, "end": v(-234.06, 121.06) * mm});
            skLineSegment(sketch, "E2085", {"start": v(-234.06, 121.06) * mm, "end": v(-233.95, 121.82) * mm});
            skLineSegment(sketch, "E2086", {"start": v(-240.12, 121.82) * mm, "end": v(-240.12, 160.14) * mm});
            skLineSegment(sketch, "E2087", {"start": v(-233.95, 160.14) * mm, "end": v(-234.06, 161) * mm});
            skLineSegment(sketch, "E2088", {"start": v(-234.06, 161) * mm, "end": v(-234.39, 161.65) * mm});
            skLineSegment(sketch, "E2089", {"start": v(-234.39, 161.65) * mm, "end": v(-234.82, 162.3) * mm});
            skLineSegment(sketch, "E2090", {"start": v(-234.82, 162.3) * mm, "end": v(-235.47, 162.84) * mm});
            skLineSegment(sketch, "E2091", {"start": v(-235.47, 162.84) * mm, "end": v(-236.23, 163.17) * mm});
            skLineSegment(sketch, "E2092", {"start": v(-236.23, 163.17) * mm, "end": v(-237.85, 163.17) * mm});
            skLineSegment(sketch, "E2093", {"start": v(-237.85, 163.17) * mm, "end": v(-238.5, 162.84) * mm});
            skLineSegment(sketch, "E2094", {"start": v(-238.5, 162.84) * mm, "end": v(-239.15, 162.3) * mm});
            skLineSegment(sketch, "E2095", {"start": v(-239.15, 162.3) * mm, "end": v(-239.69, 161.65) * mm});
            skLineSegment(sketch, "E2096", {"start": v(-239.69, 161.65) * mm, "end": v(-240.01, 161) * mm});
            skLineSegment(sketch, "E2097", {"start": v(-240.01, 161) * mm, "end": v(-240.12, 160.14) * mm});
            skLineSegment(sketch, "E2098", {"start": v(-233.95, 160.14) * mm, "end": v(-233.95, 150.29) * mm});
            skLineSegment(sketch, "E2099", {"start": v(-233.95, 150.29) * mm, "end": v(-226.05, 150.29) * mm});
            skLineSegment(sketch, "E2100", {"start": v(-226.05, 150.29) * mm, "end": v(-226.05, 159.6) * mm});
            skLineSegment(sketch, "E2101", {"start": v(-226.05, 159.6) * mm, "end": v(-226.16, 161) * mm});
            skLineSegment(sketch, "E2102", {"start": v(-226.16, 161) * mm, "end": v(-226.38, 162.4) * mm});
            skLineSegment(sketch, "E2103", {"start": v(-226.38, 162.4) * mm, "end": v(-226.92, 163.7) * mm});
            skLineSegment(sketch, "E2104", {"start": v(-226.92, 163.7) * mm, "end": v(-227.57, 165) * mm});
            skLineSegment(sketch, "E2105", {"start": v(-227.57, 165) * mm, "end": v(-228.33, 166.2) * mm});
            skLineSegment(sketch, "E2106", {"start": v(-228.33, 166.2) * mm, "end": v(-229.3, 167.28) * mm});
            skLineSegment(sketch, "E2107", {"start": v(-229.3, 167.28) * mm, "end": v(-230.38, 168.25) * mm});
            skLineSegment(sketch, "E2108", {"start": v(-230.38, 168.25) * mm, "end": v(-231.57, 169.01) * mm});
            skLineSegment(sketch, "E2109", {"start": v(-231.57, 169.01) * mm, "end": v(-232.87, 169.66) * mm});
            skLineSegment(sketch, "E2110", {"start": v(-232.87, 169.66) * mm, "end": v(-234.17, 170.2) * mm});
            skLineSegment(sketch, "E2111", {"start": v(-234.17, 170.2) * mm, "end": v(-235.58, 170.42) * mm});
            skLineSegment(sketch, "E2112", {"start": v(-235.58, 170.42) * mm, "end": v(-236.98, 170.52) * mm});
            skLineSegment(sketch, "E2113", {"start": v(-236.98, 170.52) * mm, "end": v(-238.5, 170.42) * mm});
            skLineSegment(sketch, "E2114", {"start": v(-238.5, 170.42) * mm, "end": v(-239.9, 170.2) * mm});
            skLineSegment(sketch, "E2115", {"start": v(-239.9, 170.2) * mm, "end": v(-241.2, 169.66) * mm});
            skLineSegment(sketch, "E2116", {"start": v(-241.2, 169.66) * mm, "end": v(-242.5, 169.01) * mm});
            skLineSegment(sketch, "E2117", {"start": v(-242.5, 169.01) * mm, "end": v(-243.7, 168.25) * mm});
            skLineSegment(sketch, "E2118", {"start": v(-243.7, 168.25) * mm, "end": v(-244.78, 167.28) * mm});
            skLineSegment(sketch, "E2119", {"start": v(-244.78, 167.28) * mm, "end": v(-245.75, 166.2) * mm});
            skLineSegment(sketch, "E2120", {"start": v(-245.75, 166.2) * mm, "end": v(-246.5, 165) * mm});
            skLineSegment(sketch, "E2121", {"start": v(-246.5, 165) * mm, "end": v(-247.16, 163.7) * mm});
            skLineSegment(sketch, "E2122", {"start": v(-247.16, 163.7) * mm, "end": v(-247.6, 162.4) * mm});
            skLineSegment(sketch, "E2123", {"start": v(-247.6, 162.4) * mm, "end": v(-247.92, 161) * mm});
            skLineSegment(sketch, "E2124", {"start": v(-247.92, 161) * mm, "end": v(-248.03, 159.6) * mm});
            skLineSegment(sketch, "E2125", {"start": v(-248.03, 159.6) * mm, "end": v(-248.03, 122.47) * mm});
            skLineSegment(sketch, "E2126", {"start": v(-149.64, 122.47) * mm, "end": v(-149.53, 121.06) * mm});
            skLineSegment(sketch, "E2127", {"start": v(-149.53, 121.06) * mm, "end": v(-149.2, 119.65) * mm});
            skLineSegment(sketch, "E2128", {"start": v(-149.2, 119.65) * mm, "end": v(-148.77, 118.25) * mm});
            skLineSegment(sketch, "E2129", {"start": v(-148.77, 118.25) * mm, "end": v(-148.12, 116.95) * mm});
            skLineSegment(sketch, "E2130", {"start": v(-148.12, 116.95) * mm, "end": v(-147.36, 115.76) * mm});
            skLineSegment(sketch, "E2131", {"start": v(-147.36, 115.76) * mm, "end": v(-146.39, 114.68) * mm});
            skLineSegment(sketch, "E2132", {"start": v(-146.39, 114.68) * mm, "end": v(-145.3, 113.8) * mm});
            skLineSegment(sketch, "E2133", {"start": v(-145.3, 113.8) * mm, "end": v(-144.12, 112.95) * mm});
            skLineSegment(sketch, "E2134", {"start": v(-144.12, 112.95) * mm, "end": v(-142.82, 112.3) * mm});
            skLineSegment(sketch, "E2135", {"start": v(-142.82, 112.3) * mm, "end": v(-141.41, 111.86) * mm});
            skLineSegment(sketch, "E2136", {"start": v(-141.41, 111.86) * mm, "end": v(-140, 111.54) * mm});
            skLineSegment(sketch, "E2137", {"start": v(-140, 111.54) * mm, "end": v(-137.19, 111.54) * mm});
            skLineSegment(sketch, "E2138", {"start": v(-137.19, 111.54) * mm, "end": v(-135.78, 111.86) * mm});
            skLineSegment(sketch, "E2139", {"start": v(-135.78, 111.86) * mm, "end": v(-134.37, 112.3) * mm});
            skLineSegment(sketch, "E2140", {"start": v(-134.37, 112.3) * mm, "end": v(-133.08, 112.95) * mm});
            skLineSegment(sketch, "E2141", {"start": v(-133.08, 112.95) * mm, "end": v(-131.89, 113.8) * mm});
            skLineSegment(sketch, "E2142", {"start": v(-131.89, 113.8) * mm, "end": v(-130.8, 114.68) * mm});
            skLineSegment(sketch, "E2143", {"start": v(-130.8, 114.68) * mm, "end": v(-129.94, 115.76) * mm});
            skLineSegment(sketch, "E2144", {"start": v(-129.94, 115.76) * mm, "end": v(-129.07, 116.95) * mm});
            skLineSegment(sketch, "E2145", {"start": v(-129.07, 116.95) * mm, "end": v(-128.42, 118.25) * mm});
            skLineSegment(sketch, "E2146", {"start": v(-128.42, 118.25) * mm, "end": v(-127.99, 119.65) * mm});
            skLineSegment(sketch, "E2147", {"start": v(-127.99, 119.65) * mm, "end": v(-127.77, 121.06) * mm});
            skLineSegment(sketch, "E2148", {"start": v(-127.77, 121.06) * mm, "end": v(-127.66, 122.47) * mm});
            skLineSegment(sketch, "E2149", {"start": v(-127.66, 122.47) * mm, "end": v(-127.66, 131.67) * mm});
            skLineSegment(sketch, "E2150", {"start": v(-127.66, 131.67) * mm, "end": v(-135.57, 131.67) * mm});
            skLineSegment(sketch, "E2151", {"start": v(-135.57, 131.67) * mm, "end": v(-135.57, 121.82) * mm});
            skLineSegment(sketch, "E2152", {"start": v(-141.63, 121.82) * mm, "end": v(-141.52, 121.06) * mm});
            skLineSegment(sketch, "E2153", {"start": v(-141.52, 121.06) * mm, "end": v(-141.3, 120.3) * mm});
            skLineSegment(sketch, "E2154", {"start": v(-141.3, 120.3) * mm, "end": v(-140.76, 119.65) * mm});
            skLineSegment(sketch, "E2155", {"start": v(-140.76, 119.65) * mm, "end": v(-140.11, 119.22) * mm});
            skLineSegment(sketch, "E2156", {"start": v(-140.11, 119.22) * mm, "end": v(-139.36, 118.9) * mm});
            skLineSegment(sketch, "E2157", {"start": v(-139.36, 118.9) * mm, "end": v(-138.6, 118.79) * mm});
            skLineSegment(sketch, "E2158", {"start": v(-138.6, 118.79) * mm, "end": v(-137.84, 118.9) * mm});
            skLineSegment(sketch, "E2159", {"start": v(-137.84, 118.9) * mm, "end": v(-137.08, 119.22) * mm});
            skLineSegment(sketch, "E2160", {"start": v(-137.08, 119.22) * mm, "end": v(-136.43, 119.65) * mm});
            skLineSegment(sketch, "E2161", {"start": v(-136.43, 119.65) * mm, "end": v(-136, 120.3) * mm});
            skLineSegment(sketch, "E2162", {"start": v(-136, 120.3) * mm, "end": v(-135.68, 121.06) * mm});
            skLineSegment(sketch, "E2163", {"start": v(-135.68, 121.06) * mm, "end": v(-135.57, 121.82) * mm});
            skLineSegment(sketch, "E2164", {"start": v(-141.63, 121.82) * mm, "end": v(-141.63, 160.14) * mm});
            skLineSegment(sketch, "E2165", {"start": v(-135.57, 160.14) * mm, "end": v(-135.68, 161) * mm});
            skLineSegment(sketch, "E2166", {"start": v(-135.68, 161) * mm, "end": v(-136, 161.65) * mm});
            skLineSegment(sketch, "E2167", {"start": v(-136, 161.65) * mm, "end": v(-136.43, 162.3) * mm});
            skLineSegment(sketch, "E2168", {"start": v(-136.43, 162.3) * mm, "end": v(-137.08, 162.84) * mm});
            skLineSegment(sketch, "E2169", {"start": v(-137.08, 162.84) * mm, "end": v(-137.84, 163.17) * mm});
            skLineSegment(sketch, "E2170", {"start": v(-137.84, 163.17) * mm, "end": v(-139.36, 163.17) * mm});
            skLineSegment(sketch, "E2171", {"start": v(-139.36, 163.17) * mm, "end": v(-140.11, 162.84) * mm});
            skLineSegment(sketch, "E2172", {"start": v(-140.11, 162.84) * mm, "end": v(-140.76, 162.3) * mm});
            skLineSegment(sketch, "E2173", {"start": v(-140.76, 162.3) * mm, "end": v(-141.3, 161.65) * mm});
            skLineSegment(sketch, "E2174", {"start": v(-141.3, 161.65) * mm, "end": v(-141.52, 161) * mm});
            skLineSegment(sketch, "E2175", {"start": v(-141.52, 161) * mm, "end": v(-141.63, 160.14) * mm});
            skLineSegment(sketch, "E2176", {"start": v(-135.57, 160.14) * mm, "end": v(-135.57, 150.29) * mm});
            skLineSegment(sketch, "E2177", {"start": v(-135.57, 150.29) * mm, "end": v(-127.66, 150.29) * mm});
            skLineSegment(sketch, "E2178", {"start": v(-127.66, 150.29) * mm, "end": v(-127.66, 159.6) * mm});
            skLineSegment(sketch, "E2179", {"start": v(-127.66, 159.6) * mm, "end": v(-127.77, 161) * mm});
            skLineSegment(sketch, "E2180", {"start": v(-127.77, 161) * mm, "end": v(-127.99, 162.4) * mm});
            skLineSegment(sketch, "E2181", {"start": v(-127.99, 162.4) * mm, "end": v(-128.42, 163.7) * mm});
            skLineSegment(sketch, "E2182", {"start": v(-128.42, 163.7) * mm, "end": v(-129.07, 165) * mm});
            skLineSegment(sketch, "E2183", {"start": v(-129.07, 165) * mm, "end": v(-129.94, 166.2) * mm});
            skLineSegment(sketch, "E2184", {"start": v(-129.94, 166.2) * mm, "end": v(-130.8, 167.28) * mm});
            skLineSegment(sketch, "E2185", {"start": v(-130.8, 167.28) * mm, "end": v(-131.89, 168.25) * mm});
            skLineSegment(sketch, "E2186", {"start": v(-131.89, 168.25) * mm, "end": v(-133.08, 169.01) * mm});
            skLineSegment(sketch, "E2187", {"start": v(-133.08, 169.01) * mm, "end": v(-134.37, 169.66) * mm});
            skLineSegment(sketch, "E2188", {"start": v(-134.37, 169.66) * mm, "end": v(-135.78, 170.2) * mm});
            skLineSegment(sketch, "E2189", {"start": v(-135.78, 170.2) * mm, "end": v(-137.19, 170.42) * mm});
            skLineSegment(sketch, "E2190", {"start": v(-137.19, 170.42) * mm, "end": v(-138.6, 170.52) * mm});
            skLineSegment(sketch, "E2191", {"start": v(-138.6, 170.52) * mm, "end": v(-140, 170.42) * mm});
            skLineSegment(sketch, "E2192", {"start": v(-140, 170.42) * mm, "end": v(-141.41, 170.2) * mm});
            skLineSegment(sketch, "E2193", {"start": v(-141.41, 170.2) * mm, "end": v(-142.82, 169.66) * mm});
            skLineSegment(sketch, "E2194", {"start": v(-142.82, 169.66) * mm, "end": v(-144.12, 169.01) * mm});
            skLineSegment(sketch, "E2195", {"start": v(-144.12, 169.01) * mm, "end": v(-145.3, 168.25) * mm});
            skLineSegment(sketch, "E2196", {"start": v(-145.3, 168.25) * mm, "end": v(-146.39, 167.28) * mm});
            skLineSegment(sketch, "E2197", {"start": v(-146.39, 167.28) * mm, "end": v(-147.36, 166.2) * mm});
            skLineSegment(sketch, "E2198", {"start": v(-147.36, 166.2) * mm, "end": v(-148.12, 165) * mm});
            skLineSegment(sketch, "E2199", {"start": v(-148.12, 165) * mm, "end": v(-148.77, 163.7) * mm});
            skLineSegment(sketch, "E2200", {"start": v(-148.77, 163.7) * mm, "end": v(-149.2, 162.4) * mm});
            skLineSegment(sketch, "E2201", {"start": v(-149.2, 162.4) * mm, "end": v(-149.53, 161) * mm});
            skLineSegment(sketch, "E2202", {"start": v(-149.53, 161) * mm, "end": v(-149.64, 159.6) * mm});
            skLineSegment(sketch, "E2203", {"start": v(-149.64, 159.6) * mm, "end": v(-149.64, 122.47) * mm});
            skLineSegment(sketch, "E2204", {"start": v(-167.93, 160.14) * mm, "end": v(-167.93, 121.82) * mm});
            skLineSegment(sketch, "E2205", {"start": v(-174.1, 121.82) * mm, "end": v(-174, 121.06) * mm});
            skLineSegment(sketch, "E2206", {"start": v(-174, 121.06) * mm, "end": v(-173.67, 120.3) * mm});
            skLineSegment(sketch, "E2207", {"start": v(-173.67, 120.3) * mm, "end": v(-173.23, 119.65) * mm});
            skLineSegment(sketch, "E2208", {"start": v(-173.23, 119.65) * mm, "end": v(-172.58, 119.22) * mm});
            skLineSegment(sketch, "E2209", {"start": v(-172.58, 119.22) * mm, "end": v(-171.82, 118.9) * mm});
            skLineSegment(sketch, "E2210", {"start": v(-171.82, 118.9) * mm, "end": v(-171.07, 118.79) * mm});
            skLineSegment(sketch, "E2211", {"start": v(-171.07, 118.79) * mm, "end": v(-170.2, 118.9) * mm});
            skLineSegment(sketch, "E2212", {"start": v(-170.2, 118.9) * mm, "end": v(-169.55, 119.22) * mm});
            skLineSegment(sketch, "E2213", {"start": v(-169.55, 119.22) * mm, "end": v(-168.9, 119.65) * mm});
            skLineSegment(sketch, "E2214", {"start": v(-168.9, 119.65) * mm, "end": v(-168.36, 120.3) * mm});
            skLineSegment(sketch, "E2215", {"start": v(-168.36, 120.3) * mm, "end": v(-168.04, 121.06) * mm});
            skLineSegment(sketch, "E2216", {"start": v(-168.04, 121.06) * mm, "end": v(-167.93, 121.82) * mm});
            skLineSegment(sketch, "E2217", {"start": v(-174.1, 121.82) * mm, "end": v(-174.1, 160.14) * mm});
            skLineSegment(sketch, "E2218", {"start": v(-167.93, 160.14) * mm, "end": v(-168.04, 161) * mm});
            skLineSegment(sketch, "E2219", {"start": v(-168.04, 161) * mm, "end": v(-168.36, 161.65) * mm});
            skLineSegment(sketch, "E2220", {"start": v(-168.36, 161.65) * mm, "end": v(-168.9, 162.3) * mm});
            skLineSegment(sketch, "E2221", {"start": v(-168.9, 162.3) * mm, "end": v(-169.55, 162.84) * mm});
            skLineSegment(sketch, "E2222", {"start": v(-169.55, 162.84) * mm, "end": v(-170.2, 163.17) * mm});
            skLineSegment(sketch, "E2223", {"start": v(-170.2, 163.17) * mm, "end": v(-171.82, 163.17) * mm});
            skLineSegment(sketch, "E2224", {"start": v(-171.82, 163.17) * mm, "end": v(-172.58, 162.84) * mm});
            skLineSegment(sketch, "E2225", {"start": v(-172.58, 162.84) * mm, "end": v(-173.23, 162.3) * mm});
            skLineSegment(sketch, "E2226", {"start": v(-173.23, 162.3) * mm, "end": v(-173.67, 161.65) * mm});
            skLineSegment(sketch, "E2227", {"start": v(-173.67, 161.65) * mm, "end": v(-174, 161) * mm});
            skLineSegment(sketch, "E2228", {"start": v(-174, 161) * mm, "end": v(-174.1, 160.14) * mm});
            skLineSegment(sketch, "E2229", {"start": v(-182, 159.6) * mm, "end": v(-182, 122.47) * mm});
            skLineSegment(sketch, "E2230", {"start": v(-182, 122.47) * mm, "end": v(-181.9, 121.06) * mm});
            skLineSegment(sketch, "E2231", {"start": v(-181.9, 121.06) * mm, "end": v(-181.67, 119.65) * mm});
            skLineSegment(sketch, "E2232", {"start": v(-181.67, 119.65) * mm, "end": v(-181.13, 118.25) * mm});
            skLineSegment(sketch, "E2233", {"start": v(-181.13, 118.25) * mm, "end": v(-180.49, 116.95) * mm});
            skLineSegment(sketch, "E2234", {"start": v(-180.49, 116.95) * mm, "end": v(-179.73, 115.76) * mm});
            skLineSegment(sketch, "E2235", {"start": v(-179.73, 115.76) * mm, "end": v(-178.75, 114.68) * mm});
            skLineSegment(sketch, "E2236", {"start": v(-178.75, 114.68) * mm, "end": v(-177.67, 113.8) * mm});
            skLineSegment(sketch, "E2237", {"start": v(-177.67, 113.8) * mm, "end": v(-176.48, 112.95) * mm});
            skLineSegment(sketch, "E2238", {"start": v(-176.48, 112.95) * mm, "end": v(-175.18, 112.3) * mm});
            skLineSegment(sketch, "E2239", {"start": v(-175.18, 112.3) * mm, "end": v(-173.88, 111.86) * mm});
            skLineSegment(sketch, "E2240", {"start": v(-173.88, 111.86) * mm, "end": v(-172.47, 111.54) * mm});
            skLineSegment(sketch, "E2241", {"start": v(-172.47, 111.54) * mm, "end": v(-169.55, 111.54) * mm});
            skLineSegment(sketch, "E2242", {"start": v(-169.55, 111.54) * mm, "end": v(-168.14, 111.86) * mm});
            skLineSegment(sketch, "E2243", {"start": v(-168.14, 111.86) * mm, "end": v(-166.85, 112.3) * mm});
            skLineSegment(sketch, "E2244", {"start": v(-166.85, 112.3) * mm, "end": v(-165.55, 112.95) * mm});
            skLineSegment(sketch, "E2245", {"start": v(-165.55, 112.95) * mm, "end": v(-164.36, 113.8) * mm});
            skLineSegment(sketch, "E2246", {"start": v(-164.36, 113.8) * mm, "end": v(-163.27, 114.68) * mm});
            skLineSegment(sketch, "E2247", {"start": v(-163.27, 114.68) * mm, "end": v(-162.3, 115.76) * mm});
            skLineSegment(sketch, "E2248", {"start": v(-162.3, 115.76) * mm, "end": v(-161.54, 116.95) * mm});
            skLineSegment(sketch, "E2249", {"start": v(-161.54, 116.95) * mm, "end": v(-160.9, 118.25) * mm});
            skLineSegment(sketch, "E2250", {"start": v(-160.9, 118.25) * mm, "end": v(-160.46, 119.65) * mm});
            skLineSegment(sketch, "E2251", {"start": v(-160.46, 119.65) * mm, "end": v(-160.14, 121.06) * mm});
            skLineSegment(sketch, "E2252", {"start": v(-160.14, 121.06) * mm, "end": v(-160.03, 122.47) * mm});
            skLineSegment(sketch, "E2253", {"start": v(-160.03, 122.47) * mm, "end": v(-160.03, 159.6) * mm});
            skLineSegment(sketch, "E2254", {"start": v(-160.03, 159.6) * mm, "end": v(-160.14, 161) * mm});
            skLineSegment(sketch, "E2255", {"start": v(-160.14, 161) * mm, "end": v(-160.46, 162.4) * mm});
            skLineSegment(sketch, "E2256", {"start": v(-160.46, 162.4) * mm, "end": v(-160.9, 163.7) * mm});
            skLineSegment(sketch, "E2257", {"start": v(-160.9, 163.7) * mm, "end": v(-161.54, 165) * mm});
            skLineSegment(sketch, "E2258", {"start": v(-161.54, 165) * mm, "end": v(-162.3, 166.2) * mm});
            skLineSegment(sketch, "E2259", {"start": v(-162.3, 166.2) * mm, "end": v(-163.27, 167.28) * mm});
            skLineSegment(sketch, "E2260", {"start": v(-163.27, 167.28) * mm, "end": v(-164.36, 168.25) * mm});
            skLineSegment(sketch, "E2261", {"start": v(-164.36, 168.25) * mm, "end": v(-165.55, 169.01) * mm});
            skLineSegment(sketch, "E2262", {"start": v(-165.55, 169.01) * mm, "end": v(-166.85, 169.66) * mm});
            skLineSegment(sketch, "E2263", {"start": v(-166.85, 169.66) * mm, "end": v(-168.14, 170.2) * mm});
            skLineSegment(sketch, "E2264", {"start": v(-168.14, 170.2) * mm, "end": v(-169.55, 170.42) * mm});
            skLineSegment(sketch, "E2265", {"start": v(-169.55, 170.42) * mm, "end": v(-171.07, 170.52) * mm});
            skLineSegment(sketch, "E2266", {"start": v(-171.07, 170.52) * mm, "end": v(-172.47, 170.42) * mm});
            skLineSegment(sketch, "E2267", {"start": v(-172.47, 170.42) * mm, "end": v(-173.88, 170.2) * mm});
            skLineSegment(sketch, "E2268", {"start": v(-173.88, 170.2) * mm, "end": v(-175.18, 169.66) * mm});
            skLineSegment(sketch, "E2269", {"start": v(-175.18, 169.66) * mm, "end": v(-176.48, 169.01) * mm});
            skLineSegment(sketch, "E2270", {"start": v(-176.48, 169.01) * mm, "end": v(-177.67, 168.25) * mm});
            skLineSegment(sketch, "E2271", {"start": v(-177.67, 168.25) * mm, "end": v(-178.75, 167.28) * mm});
            skLineSegment(sketch, "E2272", {"start": v(-178.75, 167.28) * mm, "end": v(-179.73, 166.2) * mm});
            skLineSegment(sketch, "E2273", {"start": v(-179.73, 166.2) * mm, "end": v(-180.49, 165) * mm});
            skLineSegment(sketch, "E2274", {"start": v(-180.49, 165) * mm, "end": v(-181.13, 163.7) * mm});
            skLineSegment(sketch, "E2275", {"start": v(-181.13, 163.7) * mm, "end": v(-181.67, 162.4) * mm});
            skLineSegment(sketch, "E2276", {"start": v(-181.67, 162.4) * mm, "end": v(-181.9, 161) * mm});
            skLineSegment(sketch, "E2277", {"start": v(-181.9, 161) * mm, "end": v(-182, 159.6) * mm});
            skLineSegment(sketch, "E2278", {"start": v(-103.85, 160.14) * mm, "end": v(-103.85, 121.82) * mm});
            skLineSegment(sketch, "E2279", {"start": v(-110.02, 121.82) * mm, "end": v(-109.91, 121.06) * mm});
            skLineSegment(sketch, "E2280", {"start": v(-109.91, 121.06) * mm, "end": v(-109.59, 120.3) * mm});
            skLineSegment(sketch, "E2281", {"start": v(-109.59, 120.3) * mm, "end": v(-109.05, 119.65) * mm});
            skLineSegment(sketch, "E2282", {"start": v(-109.05, 119.65) * mm, "end": v(-108.4, 119.22) * mm});
            skLineSegment(sketch, "E2283", {"start": v(-108.4, 119.22) * mm, "end": v(-107.75, 118.9) * mm});
            skLineSegment(sketch, "E2284", {"start": v(-107.75, 118.9) * mm, "end": v(-106.88, 118.79) * mm});
            skLineSegment(sketch, "E2285", {"start": v(-106.88, 118.79) * mm, "end": v(-106.13, 118.9) * mm});
            skLineSegment(sketch, "E2286", {"start": v(-106.13, 118.9) * mm, "end": v(-105.37, 119.22) * mm});
            skLineSegment(sketch, "E2287", {"start": v(-105.37, 119.22) * mm, "end": v(-104.72, 119.65) * mm});
            skLineSegment(sketch, "E2288", {"start": v(-104.72, 119.65) * mm, "end": v(-104.29, 120.3) * mm});
            skLineSegment(sketch, "E2289", {"start": v(-104.29, 120.3) * mm, "end": v(-103.96, 121.06) * mm});
            skLineSegment(sketch, "E2290", {"start": v(-103.96, 121.06) * mm, "end": v(-103.85, 121.82) * mm});
            skLineSegment(sketch, "E2291", {"start": v(-110.02, 121.82) * mm, "end": v(-110.02, 160.14) * mm});
            skLineSegment(sketch, "E2292", {"start": v(-103.85, 160.14) * mm, "end": v(-103.96, 161) * mm});
            skLineSegment(sketch, "E2293", {"start": v(-103.96, 161) * mm, "end": v(-104.29, 161.65) * mm});
            skLineSegment(sketch, "E2294", {"start": v(-104.29, 161.65) * mm, "end": v(-104.72, 162.3) * mm});
            skLineSegment(sketch, "E2295", {"start": v(-104.72, 162.3) * mm, "end": v(-105.37, 162.84) * mm});
            skLineSegment(sketch, "E2296", {"start": v(-105.37, 162.84) * mm, "end": v(-106.13, 163.17) * mm});
            skLineSegment(sketch, "E2297", {"start": v(-106.13, 163.17) * mm, "end": v(-107.75, 163.17) * mm});
            skLineSegment(sketch, "E2298", {"start": v(-107.75, 163.17) * mm, "end": v(-108.4, 162.84) * mm});
            skLineSegment(sketch, "E2299", {"start": v(-108.4, 162.84) * mm, "end": v(-109.05, 162.3) * mm});
            skLineSegment(sketch, "E2300", {"start": v(-109.05, 162.3) * mm, "end": v(-109.59, 161.65) * mm});
            skLineSegment(sketch, "E2301", {"start": v(-109.59, 161.65) * mm, "end": v(-109.91, 161) * mm});
            skLineSegment(sketch, "E2302", {"start": v(-109.91, 161) * mm, "end": v(-110.02, 160.14) * mm});
            skLineSegment(sketch, "E2303", {"start": v(-117.92, 159.6) * mm, "end": v(-117.92, 122.47) * mm});
            skLineSegment(sketch, "E2304", {"start": v(-117.92, 122.47) * mm, "end": v(-117.82, 121.06) * mm});
            skLineSegment(sketch, "E2305", {"start": v(-117.82, 121.06) * mm, "end": v(-117.5, 119.65) * mm});
            skLineSegment(sketch, "E2306", {"start": v(-117.5, 119.65) * mm, "end": v(-117.06, 118.25) * mm});
            skLineSegment(sketch, "E2307", {"start": v(-117.06, 118.25) * mm, "end": v(-116.4, 116.95) * mm});
            skLineSegment(sketch, "E2308", {"start": v(-116.4, 116.95) * mm, "end": v(-115.65, 115.76) * mm});
            skLineSegment(sketch, "E2309", {"start": v(-115.65, 115.76) * mm, "end": v(-114.68, 114.68) * mm});
            skLineSegment(sketch, "E2310", {"start": v(-114.68, 114.68) * mm, "end": v(-113.6, 113.8) * mm});
            skLineSegment(sketch, "E2311", {"start": v(-113.6, 113.8) * mm, "end": v(-112.4, 112.95) * mm});
            skLineSegment(sketch, "E2312", {"start": v(-112.4, 112.95) * mm, "end": v(-111.1, 112.3) * mm});
            skLineSegment(sketch, "E2313", {"start": v(-111.1, 112.3) * mm, "end": v(-109.8, 111.86) * mm});
            skLineSegment(sketch, "E2314", {"start": v(-109.8, 111.86) * mm, "end": v(-108.4, 111.54) * mm});
            skLineSegment(sketch, "E2315", {"start": v(-108.4, 111.54) * mm, "end": v(-105.48, 111.54) * mm});
            skLineSegment(sketch, "E2316", {"start": v(-105.48, 111.54) * mm, "end": v(-104.07, 111.86) * mm});
            skLineSegment(sketch, "E2317", {"start": v(-104.07, 111.86) * mm, "end": v(-102.66, 112.3) * mm});
            skLineSegment(sketch, "E2318", {"start": v(-102.66, 112.3) * mm, "end": v(-101.47, 112.95) * mm});
            skLineSegment(sketch, "E2319", {"start": v(-101.47, 112.95) * mm, "end": v(-100.28, 113.8) * mm});
            skLineSegment(sketch, "E2320", {"start": v(-100.28, 113.8) * mm, "end": v(-99.2, 114.68) * mm});
            skLineSegment(sketch, "E2321", {"start": v(-99.2, 114.68) * mm, "end": v(-98.23, 115.76) * mm});
            skLineSegment(sketch, "E2322", {"start": v(-98.23, 115.76) * mm, "end": v(-97.36, 116.95) * mm});
            skLineSegment(sketch, "E2323", {"start": v(-97.36, 116.95) * mm, "end": v(-96.82, 118.25) * mm});
            skLineSegment(sketch, "E2324", {"start": v(-96.82, 118.25) * mm, "end": v(-96.28, 119.65) * mm});
            skLineSegment(sketch, "E2325", {"start": v(-96.28, 119.65) * mm, "end": v(-96.06, 121.06) * mm});
            skLineSegment(sketch, "E2326", {"start": v(-96.06, 121.06) * mm, "end": v(-95.95, 122.47) * mm});
            skLineSegment(sketch, "E2327", {"start": v(-95.95, 122.47) * mm, "end": v(-95.95, 159.6) * mm});
            skLineSegment(sketch, "E2328", {"start": v(-95.95, 159.6) * mm, "end": v(-96.06, 161) * mm});
            skLineSegment(sketch, "E2329", {"start": v(-96.06, 161) * mm, "end": v(-96.28, 162.4) * mm});
            skLineSegment(sketch, "E2330", {"start": v(-96.28, 162.4) * mm, "end": v(-96.82, 163.7) * mm});
            skLineSegment(sketch, "E2331", {"start": v(-96.82, 163.7) * mm, "end": v(-97.36, 165) * mm});
            skLineSegment(sketch, "E2332", {"start": v(-97.36, 165) * mm, "end": v(-98.23, 166.2) * mm});
            skLineSegment(sketch, "E2333", {"start": v(-98.23, 166.2) * mm, "end": v(-99.2, 167.28) * mm});
            skLineSegment(sketch, "E2334", {"start": v(-99.2, 167.28) * mm, "end": v(-100.28, 168.25) * mm});
            skLineSegment(sketch, "E2335", {"start": v(-100.28, 168.25) * mm, "end": v(-101.47, 169.01) * mm});
            skLineSegment(sketch, "E2336", {"start": v(-101.47, 169.01) * mm, "end": v(-102.66, 169.66) * mm});
            skLineSegment(sketch, "E2337", {"start": v(-102.66, 169.66) * mm, "end": v(-104.07, 170.2) * mm});
            skLineSegment(sketch, "E2338", {"start": v(-104.07, 170.2) * mm, "end": v(-105.48, 170.42) * mm});
            skLineSegment(sketch, "E2339", {"start": v(-105.48, 170.42) * mm, "end": v(-106.88, 170.52) * mm});
            skLineSegment(sketch, "E2340", {"start": v(-106.88, 170.52) * mm, "end": v(-108.4, 170.42) * mm});
            skLineSegment(sketch, "E2341", {"start": v(-108.4, 170.42) * mm, "end": v(-109.8, 170.2) * mm});
            skLineSegment(sketch, "E2342", {"start": v(-109.8, 170.2) * mm, "end": v(-111.1, 169.66) * mm});
            skLineSegment(sketch, "E2343", {"start": v(-111.1, 169.66) * mm, "end": v(-112.4, 169.01) * mm});
            skLineSegment(sketch, "E2344", {"start": v(-112.4, 169.01) * mm, "end": v(-113.6, 168.25) * mm});
            skLineSegment(sketch, "E2345", {"start": v(-113.6, 168.25) * mm, "end": v(-114.68, 167.28) * mm});
            skLineSegment(sketch, "E2346", {"start": v(-114.68, 167.28) * mm, "end": v(-115.65, 166.2) * mm});
            skLineSegment(sketch, "E2347", {"start": v(-115.65, 166.2) * mm, "end": v(-116.4, 165) * mm});
            skLineSegment(sketch, "E2348", {"start": v(-116.4, 165) * mm, "end": v(-117.06, 163.7) * mm});
            skLineSegment(sketch, "E2349", {"start": v(-117.06, 163.7) * mm, "end": v(-117.5, 162.4) * mm});
            skLineSegment(sketch, "E2350", {"start": v(-117.5, 162.4) * mm, "end": v(-117.82, 161) * mm});
            skLineSegment(sketch, "E2351", {"start": v(-117.82, 161) * mm, "end": v(-117.92, 159.6) * mm});
            skLineSegment(sketch, "E2352", {"start": v(240.55, 160.14) * mm, "end": v(240.55, 121.82) * mm});
            skLineSegment(sketch, "E2353", {"start": v(234.5, 121.82) * mm, "end": v(234.6, 121.06) * mm});
            skLineSegment(sketch, "E2354", {"start": v(234.6, 121.06) * mm, "end": v(234.93, 120.3) * mm});
            skLineSegment(sketch, "E2355", {"start": v(234.93, 120.3) * mm, "end": v(235.36, 119.65) * mm});
            skLineSegment(sketch, "E2356", {"start": v(235.36, 119.65) * mm, "end": v(236.01, 119.22) * mm});
            skLineSegment(sketch, "E2357", {"start": v(236.01, 119.22) * mm, "end": v(236.77, 118.9) * mm});
            skLineSegment(sketch, "E2358", {"start": v(236.77, 118.9) * mm, "end": v(237.52, 118.79) * mm});
            skLineSegment(sketch, "E2359", {"start": v(237.52, 118.79) * mm, "end": v(238.4, 118.9) * mm});
            skLineSegment(sketch, "E2360", {"start": v(238.4, 118.9) * mm, "end": v(239.04, 119.22) * mm});
            skLineSegment(sketch, "E2361", {"start": v(239.04, 119.22) * mm, "end": v(239.7, 119.65) * mm});
            skLineSegment(sketch, "E2362", {"start": v(239.7, 119.65) * mm, "end": v(240.23, 120.3) * mm});
            skLineSegment(sketch, "E2363", {"start": v(240.23, 120.3) * mm, "end": v(240.55, 121.06) * mm});
            skLineSegment(sketch, "E2364", {"start": v(240.55, 121.06) * mm, "end": v(240.55, 121.82) * mm});
            skLineSegment(sketch, "E2365", {"start": v(234.5, 121.82) * mm, "end": v(234.5, 160.14) * mm});
            skLineSegment(sketch, "E2366", {"start": v(240.55, 160.14) * mm, "end": v(240.55, 161) * mm});
            skLineSegment(sketch, "E2367", {"start": v(240.55, 161) * mm, "end": v(240.23, 161.65) * mm});
            skLineSegment(sketch, "E2368", {"start": v(240.23, 161.65) * mm, "end": v(239.7, 162.3) * mm});
            skLineSegment(sketch, "E2369", {"start": v(239.7, 162.3) * mm, "end": v(239.04, 162.84) * mm});
            skLineSegment(sketch, "E2370", {"start": v(239.04, 162.84) * mm, "end": v(238.4, 163.17) * mm});
            skLineSegment(sketch, "E2371", {"start": v(238.4, 163.17) * mm, "end": v(236.77, 163.17) * mm});
            skLineSegment(sketch, "E2372", {"start": v(236.77, 163.17) * mm, "end": v(236.01, 162.84) * mm});
            skLineSegment(sketch, "E2373", {"start": v(236.01, 162.84) * mm, "end": v(235.36, 162.3) * mm});
            skLineSegment(sketch, "E2374", {"start": v(235.36, 162.3) * mm, "end": v(234.93, 161.65) * mm});
            skLineSegment(sketch, "E2375", {"start": v(234.93, 161.65) * mm, "end": v(234.6, 161) * mm});
            skLineSegment(sketch, "E2376", {"start": v(234.6, 161) * mm, "end": v(234.5, 160.14) * mm});
            skLineSegment(sketch, "E2377", {"start": v(226.6, 159.6) * mm, "end": v(226.6, 122.47) * mm});
            skLineSegment(sketch, "E2378", {"start": v(226.6, 122.47) * mm, "end": v(226.7, 121.06) * mm});
            skLineSegment(sketch, "E2379", {"start": v(226.7, 121.06) * mm, "end": v(226.92, 119.65) * mm});
            skLineSegment(sketch, "E2380", {"start": v(226.92, 119.65) * mm, "end": v(227.46, 118.25) * mm});
            skLineSegment(sketch, "E2381", {"start": v(227.46, 118.25) * mm, "end": v(228, 116.95) * mm});
            skLineSegment(sketch, "E2382", {"start": v(228, 116.95) * mm, "end": v(228.87, 115.76) * mm});
            skLineSegment(sketch, "E2383", {"start": v(228.87, 115.76) * mm, "end": v(229.84, 114.68) * mm});
            skLineSegment(sketch, "E2384", {"start": v(229.84, 114.68) * mm, "end": v(230.92, 113.8) * mm});
            skLineSegment(sketch, "E2385", {"start": v(230.92, 113.8) * mm, "end": v(232.12, 112.95) * mm});
            skLineSegment(sketch, "E2386", {"start": v(232.12, 112.95) * mm, "end": v(233.3, 112.3) * mm});
            skLineSegment(sketch, "E2387", {"start": v(233.3, 112.3) * mm, "end": v(234.71, 111.86) * mm});
            skLineSegment(sketch, "E2388", {"start": v(234.71, 111.86) * mm, "end": v(236.12, 111.54) * mm});
            skLineSegment(sketch, "E2389", {"start": v(236.12, 111.54) * mm, "end": v(239.04, 111.54) * mm});
            skLineSegment(sketch, "E2390", {"start": v(239.04, 111.54) * mm, "end": v(240.45, 111.86) * mm});
            skLineSegment(sketch, "E2391", {"start": v(240.45, 111.86) * mm, "end": v(241.75, 112.3) * mm});
            skLineSegment(sketch, "E2392", {"start": v(241.75, 112.3) * mm, "end": v(243.05, 112.95) * mm});
            skLineSegment(sketch, "E2393", {"start": v(243.05, 112.95) * mm, "end": v(244.24, 113.8) * mm});
            skLineSegment(sketch, "E2394", {"start": v(244.24, 113.8) * mm, "end": v(245.32, 114.68) * mm});
            skLineSegment(sketch, "E2395", {"start": v(245.32, 114.68) * mm, "end": v(246.3, 115.76) * mm});
            skLineSegment(sketch, "E2396", {"start": v(246.3, 115.76) * mm, "end": v(247.05, 116.95) * mm});
            skLineSegment(sketch, "E2397", {"start": v(247.05, 116.95) * mm, "end": v(247.7, 118.25) * mm});
            skLineSegment(sketch, "E2398", {"start": v(247.7, 118.25) * mm, "end": v(248.14, 119.65) * mm});
            skLineSegment(sketch, "E2399", {"start": v(248.14, 119.65) * mm, "end": v(248.46, 121.06) * mm});
            skLineSegment(sketch, "E2400", {"start": v(248.46, 121.06) * mm, "end": v(248.57, 122.47) * mm});
            skLineSegment(sketch, "E2401", {"start": v(248.57, 122.47) * mm, "end": v(248.57, 159.6) * mm});
            skLineSegment(sketch, "E2402", {"start": v(248.57, 159.6) * mm, "end": v(248.46, 161) * mm});
            skLineSegment(sketch, "E2403", {"start": v(248.46, 161) * mm, "end": v(248.14, 162.4) * mm});
            skLineSegment(sketch, "E2404", {"start": v(248.14, 162.4) * mm, "end": v(247.7, 163.7) * mm});
            skLineSegment(sketch, "E2405", {"start": v(247.7, 163.7) * mm, "end": v(247.05, 165) * mm});
            skLineSegment(sketch, "E2406", {"start": v(247.05, 165) * mm, "end": v(246.3, 166.2) * mm});
            skLineSegment(sketch, "E2407", {"start": v(246.3, 166.2) * mm, "end": v(245.32, 167.28) * mm});
            skLineSegment(sketch, "E2408", {"start": v(245.32, 167.28) * mm, "end": v(244.24, 168.25) * mm});
            skLineSegment(sketch, "E2409", {"start": v(244.24, 168.25) * mm, "end": v(243.05, 169.01) * mm});
            skLineSegment(sketch, "E2410", {"start": v(243.05, 169.01) * mm, "end": v(241.75, 169.66) * mm});
            skLineSegment(sketch, "E2411", {"start": v(241.75, 169.66) * mm, "end": v(240.45, 170.2) * mm});
            skLineSegment(sketch, "E2412", {"start": v(240.45, 170.2) * mm, "end": v(239.04, 170.42) * mm});
            skLineSegment(sketch, "E2413", {"start": v(239.04, 170.42) * mm, "end": v(237.52, 170.52) * mm});
            skLineSegment(sketch, "E2414", {"start": v(237.52, 170.52) * mm, "end": v(236.12, 170.42) * mm});
            skLineSegment(sketch, "E2415", {"start": v(236.12, 170.42) * mm, "end": v(234.71, 170.2) * mm});
            skLineSegment(sketch, "E2416", {"start": v(234.71, 170.2) * mm, "end": v(233.3, 169.66) * mm});
            skLineSegment(sketch, "E2417", {"start": v(233.3, 169.66) * mm, "end": v(232.12, 169.01) * mm});
            skLineSegment(sketch, "E2418", {"start": v(232.12, 169.01) * mm, "end": v(230.92, 168.25) * mm});
            skLineSegment(sketch, "E2419", {"start": v(230.92, 168.25) * mm, "end": v(229.84, 167.28) * mm});
            skLineSegment(sketch, "E2420", {"start": v(229.84, 167.28) * mm, "end": v(228.87, 166.2) * mm});
            skLineSegment(sketch, "E2421", {"start": v(228.87, 166.2) * mm, "end": v(228, 165) * mm});
            skLineSegment(sketch, "E2422", {"start": v(228, 165) * mm, "end": v(227.46, 163.7) * mm});
            skLineSegment(sketch, "E2423", {"start": v(227.46, 163.7) * mm, "end": v(226.92, 162.4) * mm});
            skLineSegment(sketch, "E2424", {"start": v(226.92, 162.4) * mm, "end": v(226.7, 161) * mm});
            skLineSegment(sketch, "E2425", {"start": v(226.7, 161) * mm, "end": v(226.6, 159.6) * mm});
            skLineSegment(sketch, "E2426", {"start": v(-192.93, 170.52) * mm, "end": v(-200.94, 170.52) * mm});
            skLineSegment(sketch, "E2427", {"start": v(-200.94, 170.52) * mm, "end": v(-200.94, 145.63) * mm});
            skLineSegment(sketch, "E2428", {"start": v(-200.94, 145.63) * mm, "end": v(-208.2, 145.63) * mm});
            skLineSegment(sketch, "E2429", {"start": v(-208.2, 145.63) * mm, "end": v(-208.2, 170.52) * mm});
            skLineSegment(sketch, "E2430", {"start": v(-208.2, 170.52) * mm, "end": v(-215.88, 170.52) * mm});
            skLineSegment(sketch, "E2431", {"start": v(-215.88, 170.52) * mm, "end": v(-215.88, 111.54) * mm});
            skLineSegment(sketch, "E2432", {"start": v(-215.88, 111.54) * mm, "end": v(-208.2, 111.54) * mm});
            skLineSegment(sketch, "E2433", {"start": v(-208.2, 111.54) * mm, "end": v(-208.2, 137.2) * mm});
            skLineSegment(sketch, "E2434", {"start": v(-208.2, 137.2) * mm, "end": v(-200.94, 137.2) * mm});
            skLineSegment(sketch, "E2435", {"start": v(-200.94, 137.2) * mm, "end": v(-200.94, 111.54) * mm});
            skLineSegment(sketch, "E2436", {"start": v(-200.94, 111.54) * mm, "end": v(-192.93, 111.54) * mm});
            skLineSegment(sketch, "E2437", {"start": v(-192.93, 111.54) * mm, "end": v(-192.93, 170.52) * mm});
            skLineSegment(sketch, "E2438", {"start": v(-77.23, 170.52) * mm, "end": v(-85.35, 170.52) * mm});
            skLineSegment(sketch, "E2439", {"start": v(-85.35, 170.52) * mm, "end": v(-85.35, 111.54) * mm});
            skLineSegment(sketch, "E2440", {"start": v(-85.35, 111.54) * mm, "end": v(-65.86, 111.54) * mm});
            skLineSegment(sketch, "E2441", {"start": v(-65.86, 111.54) * mm, "end": v(-65.86, 118.9) * mm});
            skLineSegment(sketch, "E2442", {"start": v(-65.86, 118.9) * mm, "end": v(-77.23, 118.9) * mm});
            skLineSegment(sketch, "E2443", {"start": v(-77.23, 118.9) * mm, "end": v(-77.23, 170.52) * mm});
            skLineSegment(sketch, "E2444", {"start": v(24.3, 170.52) * mm, "end": v(5.03, 170.52) * mm});
            skLineSegment(sketch, "E2445", {"start": v(5.03, 170.52) * mm, "end": v(5.03, 111.54) * mm});
            skLineSegment(sketch, "E2446", {"start": v(5.03, 111.54) * mm, "end": v(24.3, 111.54) * mm});
            skLineSegment(sketch, "E2447", {"start": v(24.3, 111.54) * mm, "end": v(24.3, 119.65) * mm});
            skLineSegment(sketch, "E2448", {"start": v(24.3, 119.65) * mm, "end": v(13.04, 119.65) * mm});
            skLineSegment(sketch, "E2449", {"start": v(13.04, 119.65) * mm, "end": v(13.04, 136.76) * mm});
            skLineSegment(sketch, "E2450", {"start": v(13.04, 136.76) * mm, "end": v(21.16, 136.76) * mm});
            skLineSegment(sketch, "E2451", {"start": v(21.16, 136.76) * mm, "end": v(21.16, 145.52) * mm});
            skLineSegment(sketch, "E2452", {"start": v(21.16, 145.52) * mm, "end": v(13.04, 145.52) * mm});
            skLineSegment(sketch, "E2453", {"start": v(13.04, 145.52) * mm, "end": v(13.04, 161) * mm});
            skLineSegment(sketch, "E2454", {"start": v(13.04, 161) * mm, "end": v(24.3, 161) * mm});
            skLineSegment(sketch, "E2455", {"start": v(24.3, 161) * mm, "end": v(24.3, 170.52) * mm});
            skLineSegment(sketch, "E2456", {"start": v(-3.08, 170.52) * mm, "end": v(-27.11, 170.52) * mm});
            skLineSegment(sketch, "E2457", {"start": v(-27.11, 170.52) * mm, "end": v(-27.11, 161) * mm});
            skLineSegment(sketch, "E2458", {"start": v(-27.11, 161) * mm, "end": v(-19.54, 161) * mm});
            skLineSegment(sketch, "E2459", {"start": v(-19.54, 161) * mm, "end": v(-19.54, 111.54) * mm});
            skLineSegment(sketch, "E2460", {"start": v(-19.54, 111.54) * mm, "end": v(-11.2, 111.54) * mm});
            skLineSegment(sketch, "E2461", {"start": v(-11.2, 111.54) * mm, "end": v(-11.2, 161) * mm});
            skLineSegment(sketch, "E2462", {"start": v(-11.2, 161) * mm, "end": v(-3.08, 161) * mm});
            skLineSegment(sketch, "E2463", {"start": v(-3.08, 161) * mm, "end": v(-3.08, 170.52) * mm});
            skLineSegment(sketch, "E2464", {"start": v(94.65, 170.52) * mm, "end": v(85.02, 170.52) * mm});
            skLineSegment(sketch, "E2465", {"start": v(85.02, 170.52) * mm, "end": v(85.02, 111.54) * mm});
            skLineSegment(sketch, "E2466", {"start": v(85.02, 111.54) * mm, "end": v(92.27, 111.54) * mm});
            skLineSegment(sketch, "E2467", {"start": v(92.27, 111.54) * mm, "end": v(92.27, 151.26) * mm});
            skLineSegment(sketch, "E2468", {"start": v(92.27, 151.26) * mm, "end": v(92.92, 151.26) * mm});
            skLineSegment(sketch, "E2469", {"start": v(92.92, 151.26) * mm, "end": v(98.88, 111.54) * mm});
            skLineSegment(sketch, "E2470", {"start": v(98.88, 111.54) * mm, "end": v(102.34, 111.54) * mm});
            skLineSegment(sketch, "E2471", {"start": v(102.34, 111.54) * mm, "end": v(108.18, 151.26) * mm});
            skLineSegment(sketch, "E2472", {"start": v(108.18, 151.26) * mm, "end": v(108.83, 151.26) * mm});
            skLineSegment(sketch, "E2473", {"start": v(108.83, 151.26) * mm, "end": v(108.83, 111.54) * mm});
            skLineSegment(sketch, "E2474", {"start": v(108.83, 111.54) * mm, "end": v(116.08, 111.54) * mm});
            skLineSegment(sketch, "E2475", {"start": v(116.08, 111.54) * mm, "end": v(116.08, 170.52) * mm});
            skLineSegment(sketch, "E2476", {"start": v(116.08, 170.52) * mm, "end": v(106.45, 170.52) * mm});
            skLineSegment(sketch, "E2477", {"start": v(106.45, 170.52) * mm, "end": v(101.15, 140.65) * mm});
            skLineSegment(sketch, "E2478", {"start": v(101.15, 140.65) * mm, "end": v(99.96, 140.65) * mm});
            skLineSegment(sketch, "E2479", {"start": v(99.96, 140.65) * mm, "end": v(94.65, 170.52) * mm});
            skLineSegment(sketch, "E2480", {"start": v(208.09, 160.14) * mm, "end": v(208.09, 150.29) * mm});
            skLineSegment(sketch, "E2481", {"start": v(208.09, 150.29) * mm, "end": v(215.99, 150.29) * mm});
            skLineSegment(sketch, "E2482", {"start": v(215.99, 150.29) * mm, "end": v(215.99, 159.6) * mm});
            skLineSegment(sketch, "E2483", {"start": v(215.99, 159.6) * mm, "end": v(215.88, 161) * mm});
            skLineSegment(sketch, "E2484", {"start": v(215.88, 161) * mm, "end": v(215.66, 162.4) * mm});
            skLineSegment(sketch, "E2485", {"start": v(215.66, 162.4) * mm, "end": v(215.12, 163.7) * mm});
            skLineSegment(sketch, "E2486", {"start": v(215.12, 163.7) * mm, "end": v(214.58, 165) * mm});
            skLineSegment(sketch, "E2487", {"start": v(214.58, 165) * mm, "end": v(213.71, 166.2) * mm});
            skLineSegment(sketch, "E2488", {"start": v(213.71, 166.2) * mm, "end": v(212.74, 167.28) * mm});
            skLineSegment(sketch, "E2489", {"start": v(212.74, 167.28) * mm, "end": v(211.77, 168.25) * mm});
            skLineSegment(sketch, "E2490", {"start": v(211.77, 168.25) * mm, "end": v(210.47, 169.01) * mm});
            skLineSegment(sketch, "E2491", {"start": v(210.47, 169.01) * mm, "end": v(209.28, 169.66) * mm});
            skLineSegment(sketch, "E2492", {"start": v(209.28, 169.66) * mm, "end": v(207.87, 170.2) * mm});
            skLineSegment(sketch, "E2493", {"start": v(207.87, 170.2) * mm, "end": v(206.46, 170.42) * mm});
            skLineSegment(sketch, "E2494", {"start": v(206.46, 170.42) * mm, "end": v(205.06, 170.52) * mm});
            skLineSegment(sketch, "E2495", {"start": v(205.06, 170.52) * mm, "end": v(203.54, 170.42) * mm});
            skLineSegment(sketch, "E2496", {"start": v(203.54, 170.42) * mm, "end": v(202.13, 170.2) * mm});
            skLineSegment(sketch, "E2497", {"start": v(202.13, 170.2) * mm, "end": v(200.83, 169.66) * mm});
            skLineSegment(sketch, "E2498", {"start": v(200.83, 169.66) * mm, "end": v(199.53, 169.01) * mm});
            skLineSegment(sketch, "E2499", {"start": v(199.53, 169.01) * mm, "end": v(198.35, 168.25) * mm});
            skLineSegment(sketch, "E2500", {"start": v(198.35, 168.25) * mm, "end": v(197.26, 167.28) * mm});
            skLineSegment(sketch, "E2501", {"start": v(197.26, 167.28) * mm, "end": v(196.29, 166.2) * mm});
            skLineSegment(sketch, "E2502", {"start": v(196.29, 166.2) * mm, "end": v(195.53, 165) * mm});
            skLineSegment(sketch, "E2503", {"start": v(195.53, 165) * mm, "end": v(194.88, 163.7) * mm});
            skLineSegment(sketch, "E2504", {"start": v(194.88, 163.7) * mm, "end": v(194.45, 162.4) * mm});
            skLineSegment(sketch, "E2505", {"start": v(194.45, 162.4) * mm, "end": v(194.12, 161) * mm});
            skLineSegment(sketch, "E2506", {"start": v(194.12, 161) * mm, "end": v(194.02, 159.6) * mm});
            skLineSegment(sketch, "E2507", {"start": v(194.02, 159.6) * mm, "end": v(194.02, 122.47) * mm});
            skLineSegment(sketch, "E2508", {"start": v(194.02, 122.47) * mm, "end": v(194.12, 121.06) * mm});
            skLineSegment(sketch, "E2509", {"start": v(194.12, 121.06) * mm, "end": v(194.45, 119.65) * mm});
            skLineSegment(sketch, "E2510", {"start": v(194.45, 119.65) * mm, "end": v(194.88, 118.25) * mm});
            skLineSegment(sketch, "E2511", {"start": v(194.88, 118.25) * mm, "end": v(195.53, 116.95) * mm});
            skLineSegment(sketch, "E2512", {"start": v(195.53, 116.95) * mm, "end": v(196.29, 115.76) * mm});
            skLineSegment(sketch, "E2513", {"start": v(196.29, 115.76) * mm, "end": v(197.26, 114.68) * mm});
            skLineSegment(sketch, "E2514", {"start": v(197.26, 114.68) * mm, "end": v(198.35, 113.8) * mm});
            skLineSegment(sketch, "E2515", {"start": v(198.35, 113.8) * mm, "end": v(199.53, 112.95) * mm});
            skLineSegment(sketch, "E2516", {"start": v(199.53, 112.95) * mm, "end": v(200.83, 112.3) * mm});
            skLineSegment(sketch, "E2517", {"start": v(200.83, 112.3) * mm, "end": v(202.13, 111.86) * mm});
            skLineSegment(sketch, "E2518", {"start": v(202.13, 111.86) * mm, "end": v(203.54, 111.54) * mm});
            skLineSegment(sketch, "E2519", {"start": v(203.54, 111.54) * mm, "end": v(205.06, 111.54) * mm});
            skLineSegment(sketch, "E2520", {"start": v(205.06, 111.54) * mm, "end": v(206.25, 111.76) * mm});
            skLineSegment(sketch, "E2521", {"start": v(206.25, 111.76) * mm, "end": v(207.33, 112.19) * mm});
            skLineSegment(sketch, "E2522", {"start": v(207.33, 112.19) * mm, "end": v(208.3, 112.84) * mm});
            skLineSegment(sketch, "E2523", {"start": v(208.3, 112.84) * mm, "end": v(209.17, 113.6) * mm});
            skLineSegment(sketch, "E2524", {"start": v(209.17, 113.6) * mm, "end": v(209.93, 114.57) * mm});
            skLineSegment(sketch, "E2525", {"start": v(209.93, 114.57) * mm, "end": v(211.33, 113.6) * mm});
            skLineSegment(sketch, "E2526", {"start": v(211.33, 113.6) * mm, "end": v(211.33, 111.54) * mm});
            skLineSegment(sketch, "E2527", {"start": v(211.33, 111.54) * mm, "end": v(215.99, 111.54) * mm});
            skLineSegment(sketch, "E2528", {"start": v(215.99, 111.54) * mm, "end": v(215.99, 140.54) * mm});
            skLineSegment(sketch, "E2529", {"start": v(215.99, 140.54) * mm, "end": v(204.84, 140.54) * mm});
            skLineSegment(sketch, "E2530", {"start": v(204.84, 140.54) * mm, "end": v(204.84, 133.62) * mm});
            skLineSegment(sketch, "E2531", {"start": v(204.84, 133.62) * mm, "end": v(208.09, 133.62) * mm});
            skLineSegment(sketch, "E2532", {"start": v(208.09, 133.62) * mm, "end": v(208.09, 121.82) * mm});
            skLineSegment(sketch, "E2533", {"start": v(202.03, 121.82) * mm, "end": v(202.03, 121.06) * mm});
            skLineSegment(sketch, "E2534", {"start": v(202.03, 121.06) * mm, "end": v(202.35, 120.3) * mm});
            skLineSegment(sketch, "E2535", {"start": v(202.35, 120.3) * mm, "end": v(202.9, 119.65) * mm});
            skLineSegment(sketch, "E2536", {"start": v(202.9, 119.65) * mm, "end": v(203.54, 119.22) * mm});
            skLineSegment(sketch, "E2537", {"start": v(203.54, 119.22) * mm, "end": v(204.19, 118.9) * mm});
            skLineSegment(sketch, "E2538", {"start": v(204.19, 118.9) * mm, "end": v(205.06, 118.79) * mm});
            skLineSegment(sketch, "E2539", {"start": v(205.06, 118.79) * mm, "end": v(205.81, 118.9) * mm});
            skLineSegment(sketch, "E2540", {"start": v(205.81, 118.9) * mm, "end": v(206.57, 119.22) * mm});
            skLineSegment(sketch, "E2541", {"start": v(206.57, 119.22) * mm, "end": v(207.22, 119.65) * mm});
            skLineSegment(sketch, "E2542", {"start": v(207.22, 119.65) * mm, "end": v(207.65, 120.3) * mm});
            skLineSegment(sketch, "E2543", {"start": v(207.65, 120.3) * mm, "end": v(207.98, 121.06) * mm});
            skLineSegment(sketch, "E2544", {"start": v(207.98, 121.06) * mm, "end": v(208.09, 121.82) * mm});
            skLineSegment(sketch, "E2545", {"start": v(202.03, 121.82) * mm, "end": v(202.03, 160.14) * mm});
            skLineSegment(sketch, "E2546", {"start": v(208.09, 160.14) * mm, "end": v(207.98, 161) * mm});
            skLineSegment(sketch, "E2547", {"start": v(207.98, 161) * mm, "end": v(207.65, 161.65) * mm});
            skLineSegment(sketch, "E2548", {"start": v(207.65, 161.65) * mm, "end": v(207.22, 162.3) * mm});
            skLineSegment(sketch, "E2549", {"start": v(207.22, 162.3) * mm, "end": v(206.57, 162.84) * mm});
            skLineSegment(sketch, "E2550", {"start": v(206.57, 162.84) * mm, "end": v(205.81, 163.17) * mm});
            skLineSegment(sketch, "E2551", {"start": v(205.81, 163.17) * mm, "end": v(204.19, 163.17) * mm});
            skLineSegment(sketch, "E2552", {"start": v(204.19, 163.17) * mm, "end": v(203.54, 162.84) * mm});
            skLineSegment(sketch, "E2553", {"start": v(203.54, 162.84) * mm, "end": v(202.9, 162.3) * mm});
            skLineSegment(sketch, "E2554", {"start": v(202.9, 162.3) * mm, "end": v(202.35, 161.65) * mm});
            skLineSegment(sketch, "E2555", {"start": v(202.35, 161.65) * mm, "end": v(202.03, 161) * mm});
            skLineSegment(sketch, "E2556", {"start": v(202.03, 161) * mm, "end": v(202.03, 160.14) * mm});
            skLineSegment(sketch, "E2557", {"start": v(175.07, 146.17) * mm, "end": v(175.83, 147.8) * mm});
            skLineSegment(sketch, "E2558", {"start": v(175.83, 147.8) * mm, "end": v(176.48, 149.53) * mm});
            skLineSegment(sketch, "E2559", {"start": v(176.48, 149.53) * mm, "end": v(176.8, 151.26) * mm});
            skLineSegment(sketch, "E2560", {"start": v(176.8, 151.26) * mm, "end": v(176.92, 153.1) * mm});
            skLineSegment(sketch, "E2561", {"start": v(176.92, 153.1) * mm, "end": v(176.8, 154.94) * mm});
            skLineSegment(sketch, "E2562", {"start": v(176.8, 154.94) * mm, "end": v(176.48, 156.67) * mm});
            skLineSegment(sketch, "E2563", {"start": v(176.48, 156.67) * mm, "end": v(175.83, 158.4) * mm});
            skLineSegment(sketch, "E2564", {"start": v(175.83, 158.4) * mm, "end": v(175.07, 160.03) * mm});
            skLineSegment(sketch, "E2565", {"start": v(169.88, 144) * mm, "end": v(171.29, 144.23) * mm});
            skLineSegment(sketch, "E2566", {"start": v(171.29, 144.23) * mm, "end": v(172.7, 144.66) * mm});
            skLineSegment(sketch, "E2567", {"start": v(172.7, 144.66) * mm, "end": v(173.88, 145.3) * mm});
            skLineSegment(sketch, "E2568", {"start": v(173.88, 145.3) * mm, "end": v(175.07, 146.17) * mm});
            skLineSegment(sketch, "E2569", {"start": v(169.88, 144) * mm, "end": v(169.88, 162.2) * mm});
            skLineSegment(sketch, "E2570", {"start": v(175.07, 160.03) * mm, "end": v(173.88, 160.9) * mm});
            skLineSegment(sketch, "E2571", {"start": v(173.88, 160.9) * mm, "end": v(172.7, 161.54) * mm});
            skLineSegment(sketch, "E2572", {"start": v(172.7, 161.54) * mm, "end": v(171.29, 161.98) * mm});
            skLineSegment(sketch, "E2573", {"start": v(171.29, 161.98) * mm, "end": v(169.88, 162.2) * mm});
            skLineSegment(sketch, "E2574", {"start": v(169.88, 170.52) * mm, "end": v(161.98, 170.52) * mm});
            skLineSegment(sketch, "E2575", {"start": v(161.98, 170.52) * mm, "end": v(161.98, 111.54) * mm});
            skLineSegment(sketch, "E2576", {"start": v(161.98, 111.54) * mm, "end": v(169.88, 111.54) * mm});
            skLineSegment(sketch, "E2577", {"start": v(169.88, 111.54) * mm, "end": v(169.88, 137.3) * mm});
            skLineSegment(sketch, "E2578", {"start": v(169.88, 137.3) * mm, "end": v(170.42, 136.97) * mm});
            skLineSegment(sketch, "E2579", {"start": v(170.42, 136.97) * mm, "end": v(171.72, 136.97) * mm});
            skLineSegment(sketch, "E2580", {"start": v(171.72, 136.97) * mm, "end": v(172.26, 137.3) * mm});
            skLineSegment(sketch, "E2581", {"start": v(172.26, 137.3) * mm, "end": v(176.8, 111.54) * mm});
            skLineSegment(sketch, "E2582", {"start": v(176.8, 111.54) * mm, "end": v(185.03, 111.54) * mm});
            skLineSegment(sketch, "E2583", {"start": v(185.03, 111.54) * mm, "end": v(180.16, 139.57) * mm});
            skLineSegment(sketch, "E2584", {"start": v(180.16, 139.57) * mm, "end": v(181.46, 141.41) * mm});
            skLineSegment(sketch, "E2585", {"start": v(181.46, 141.41) * mm, "end": v(182.54, 143.36) * mm});
            skLineSegment(sketch, "E2586", {"start": v(182.54, 143.36) * mm, "end": v(183.4, 145.41) * mm});
            skLineSegment(sketch, "E2587", {"start": v(183.4, 145.41) * mm, "end": v(184.06, 147.58) * mm});
            skLineSegment(sketch, "E2588", {"start": v(184.06, 147.58) * mm, "end": v(184.5, 149.74) * mm});
            skLineSegment(sketch, "E2589", {"start": v(184.5, 149.74) * mm, "end": v(184.82, 152.02) * mm});
            skLineSegment(sketch, "E2590", {"start": v(184.82, 152.02) * mm, "end": v(184.82, 154.18) * mm});
            skLineSegment(sketch, "E2591", {"start": v(184.82, 154.18) * mm, "end": v(184.5, 156.46) * mm});
            skLineSegment(sketch, "E2592", {"start": v(184.5, 156.46) * mm, "end": v(184.06, 158.62) * mm});
            skLineSegment(sketch, "E2593", {"start": v(184.06, 158.62) * mm, "end": v(183.4, 160.78) * mm});
            skLineSegment(sketch, "E2594", {"start": v(183.4, 160.78) * mm, "end": v(182.54, 162.84) * mm});
            skLineSegment(sketch, "E2595", {"start": v(182.54, 162.84) * mm, "end": v(181.46, 164.79) * mm});
            skLineSegment(sketch, "E2596", {"start": v(181.46, 164.79) * mm, "end": v(180.16, 166.63) * mm});
            skLineSegment(sketch, "E2597", {"start": v(180.16, 166.63) * mm, "end": v(178.64, 167.82) * mm});
            skLineSegment(sketch, "E2598", {"start": v(178.64, 167.82) * mm, "end": v(177.02, 168.69) * mm});
            skLineSegment(sketch, "E2599", {"start": v(177.02, 168.69) * mm, "end": v(175.3, 169.44) * mm});
            skLineSegment(sketch, "E2600", {"start": v(175.3, 169.44) * mm, "end": v(173.56, 169.99) * mm});
            skLineSegment(sketch, "E2601", {"start": v(173.56, 169.99) * mm, "end": v(171.72, 170.3) * mm});
            skLineSegment(sketch, "E2602", {"start": v(171.72, 170.3) * mm, "end": v(169.88, 170.52) * mm});
            skLineSegment(sketch, "E2603", {"start": v(89.68, 268.37) * mm, "end": v(94.87, 277.03) * mm});
            skLineSegment(sketch, "E2604", {"start": v(94.87, 277.03) * mm, "end": v(104.18, 277.03) * mm});
            skLineSegment(sketch, "E2605", {"start": v(104.18, 277.03) * mm, "end": v(97.03, 268.37) * mm});
            skLineSegment(sketch, "E2606", {"start": v(97.03, 268.37) * mm, "end": v(89.68, 268.37) * mm});
            skLineSegment(sketch, "E2607", {"start": v(223.02, 86) * mm, "end": v(195.2, 86) * mm});
            skLineSegment(sketch, "E2608", {"start": v(195.2, 86) * mm, "end": v(76.04, -238.18) * mm});
            skLineSegment(sketch, "E2609", {"start": v(76.04, -238.18) * mm, "end": v(106.02, -238.18) * mm});
            skLineSegment(sketch, "E2610", {"start": v(106.02, -238.18) * mm, "end": v(223.02, 86) * mm});
            skLineSegment(sketch, "E2611", {"start": v(-127.77, 86) * mm, "end": v(-247.8, 86) * mm});
            skLineSegment(sketch, "E2612", {"start": v(-247.8, 86) * mm, "end": v(-247.8, 38.26) * mm});
            skLineSegment(sketch, "E2613", {"start": v(-247.8, 38.26) * mm, "end": v(-175.83, 38.26) * mm});
            skLineSegment(sketch, "E2614", {"start": v(-175.83, 38.26) * mm, "end": v(-223.67, -238.18) * mm});
            skLineSegment(sketch, "E2615", {"start": v(-223.67, -238.18) * mm, "end": v(-175.18, -238.18) * mm});
            skLineSegment(sketch, "E2616", {"start": v(-175.18, -238.18) * mm, "end": v(-127.77, 36.1) * mm});
            skLineSegment(sketch, "E2617", {"start": v(-127.77, 36.1) * mm, "end": v(-127.77, 86) * mm});
            skLineSegment(sketch, "E2618", {"start": v(-22.57, 31.66) * mm, "end": v(-22.57, -182.65) * mm});
            skLineSegment(sketch, "E2619", {"start": v(-56.66, -182.65) * mm, "end": v(-56.55, -184.6) * mm});
            skLineSegment(sketch, "E2620", {"start": v(-56.55, -184.6) * mm, "end": v(-56.23, -186.44) * mm});
            skLineSegment(sketch, "E2621", {"start": v(-56.23, -186.44) * mm, "end": v(-55.69, -188.28) * mm});
            skLineSegment(sketch, "E2622", {"start": v(-55.69, -188.28) * mm, "end": v(-55.04, -190.12) * mm});
            skLineSegment(sketch, "E2623", {"start": v(-55.04, -190.12) * mm, "end": v(-54.06, -191.74) * mm});
            skLineSegment(sketch, "E2624", {"start": v(-54.06, -191.74) * mm, "end": v(-52.98, -193.26) * mm});
            skLineSegment(sketch, "E2625", {"start": v(-52.98, -193.26) * mm, "end": v(-51.68, -194.77) * mm});
            skLineSegment(sketch, "E2626", {"start": v(-51.68, -194.77) * mm, "end": v(-50.28, -195.96) * mm});
            skLineSegment(sketch, "E2627", {"start": v(-50.28, -195.96) * mm, "end": v(-48.65, -197.16) * mm});
            skLineSegment(sketch, "E2628", {"start": v(-48.65, -197.16) * mm, "end": v(-47.03, -198.02) * mm});
            skLineSegment(sketch, "E2629", {"start": v(-47.03, -198.02) * mm, "end": v(-45.3, -198.78) * mm});
            skLineSegment(sketch, "E2630", {"start": v(-45.3, -198.78) * mm, "end": v(-43.46, -199.32) * mm});
            skLineSegment(sketch, "E2631", {"start": v(-43.46, -199.32) * mm, "end": v(-41.5, -199.64) * mm});
            skLineSegment(sketch, "E2632", {"start": v(-41.5, -199.64) * mm, "end": v(-39.56, -199.75) * mm});
            skLineSegment(sketch, "E2633", {"start": v(-39.56, -199.75) * mm, "end": v(-37.72, -199.64) * mm});
            skLineSegment(sketch, "E2634", {"start": v(-37.72, -199.64) * mm, "end": v(-35.77, -199.32) * mm});
            skLineSegment(sketch, "E2635", {"start": v(-35.77, -199.32) * mm, "end": v(-33.93, -198.78) * mm});
            skLineSegment(sketch, "E2636", {"start": v(-33.93, -198.78) * mm, "end": v(-32.2, -198.02) * mm});
            skLineSegment(sketch, "E2637", {"start": v(-32.2, -198.02) * mm, "end": v(-30.57, -197.16) * mm});
            skLineSegment(sketch, "E2638", {"start": v(-30.57, -197.16) * mm, "end": v(-28.95, -195.96) * mm});
            skLineSegment(sketch, "E2639", {"start": v(-28.95, -195.96) * mm, "end": v(-27.54, -194.77) * mm});
            skLineSegment(sketch, "E2640", {"start": v(-27.54, -194.77) * mm, "end": v(-26.25, -193.26) * mm});
            skLineSegment(sketch, "E2641", {"start": v(-26.25, -193.26) * mm, "end": v(-25.16, -191.74) * mm});
            skLineSegment(sketch, "E2642", {"start": v(-25.16, -191.74) * mm, "end": v(-24.2, -190.12) * mm});
            skLineSegment(sketch, "E2643", {"start": v(-24.2, -190.12) * mm, "end": v(-23.54, -188.28) * mm});
            skLineSegment(sketch, "E2644", {"start": v(-23.54, -188.28) * mm, "end": v(-23, -186.44) * mm});
            skLineSegment(sketch, "E2645", {"start": v(-23, -186.44) * mm, "end": v(-22.67, -184.6) * mm});
            skLineSegment(sketch, "E2646", {"start": v(-22.67, -184.6) * mm, "end": v(-22.57, -182.65) * mm});
            skLineSegment(sketch, "E2647", {"start": v(-56.66, -182.65) * mm, "end": v(-56.66, 31.66) * mm});
            skLineSegment(sketch, "E2648", {"start": v(-22.57, 31.66) * mm, "end": v(-22.67, 33.5) * mm});
            skLineSegment(sketch, "E2649", {"start": v(-22.67, 33.5) * mm, "end": v(-23, 35.45) * mm});
            skLineSegment(sketch, "E2650", {"start": v(-23, 35.45) * mm, "end": v(-23.54, 37.28) * mm});
            skLineSegment(sketch, "E2651", {"start": v(-23.54, 37.28) * mm, "end": v(-24.2, 39.02) * mm});
            skLineSegment(sketch, "E2652", {"start": v(-24.2, 39.02) * mm, "end": v(-25.16, 40.75) * mm});
            skLineSegment(sketch, "E2653", {"start": v(-25.16, 40.75) * mm, "end": v(-26.25, 42.26) * mm});
            skLineSegment(sketch, "E2654", {"start": v(-26.25, 42.26) * mm, "end": v(-27.54, 43.67) * mm});
            skLineSegment(sketch, "E2655", {"start": v(-27.54, 43.67) * mm, "end": v(-28.95, 44.97) * mm});
            skLineSegment(sketch, "E2656", {"start": v(-28.95, 44.97) * mm, "end": v(-30.57, 46.05) * mm});
            skLineSegment(sketch, "E2657", {"start": v(-30.57, 46.05) * mm, "end": v(-32.2, 47.03) * mm});
            skLineSegment(sketch, "E2658", {"start": v(-32.2, 47.03) * mm, "end": v(-33.93, 47.79) * mm});
            skLineSegment(sketch, "E2659", {"start": v(-33.93, 47.79) * mm, "end": v(-35.77, 48.22) * mm});
            skLineSegment(sketch, "E2660", {"start": v(-35.77, 48.22) * mm, "end": v(-37.72, 48.55) * mm});
            skLineSegment(sketch, "E2661", {"start": v(-37.72, 48.55) * mm, "end": v(-39.56, 48.65) * mm});
            skLineSegment(sketch, "E2662", {"start": v(-39.56, 48.65) * mm, "end": v(-41.5, 48.55) * mm});
            skLineSegment(sketch, "E2663", {"start": v(-41.5, 48.55) * mm, "end": v(-43.46, 48.22) * mm});
            skLineSegment(sketch, "E2664", {"start": v(-43.46, 48.22) * mm, "end": v(-45.3, 47.79) * mm});
            skLineSegment(sketch, "E2665", {"start": v(-45.3, 47.79) * mm, "end": v(-47.03, 47.03) * mm});
            skLineSegment(sketch, "E2666", {"start": v(-47.03, 47.03) * mm, "end": v(-48.65, 46.05) * mm});
            skLineSegment(sketch, "E2667", {"start": v(-48.65, 46.05) * mm, "end": v(-50.28, 44.97) * mm});
            skLineSegment(sketch, "E2668", {"start": v(-50.28, 44.97) * mm, "end": v(-51.68, 43.67) * mm});
            skLineSegment(sketch, "E2669", {"start": v(-51.68, 43.67) * mm, "end": v(-52.98, 42.26) * mm});
            skLineSegment(sketch, "E2670", {"start": v(-52.98, 42.26) * mm, "end": v(-54.06, 40.75) * mm});
            skLineSegment(sketch, "E2671", {"start": v(-54.06, 40.75) * mm, "end": v(-55.04, 39.02) * mm});
            skLineSegment(sketch, "E2672", {"start": v(-55.04, 39.02) * mm, "end": v(-55.69, 37.28) * mm});
            skLineSegment(sketch, "E2673", {"start": v(-55.69, 37.28) * mm, "end": v(-56.23, 35.45) * mm});
            skLineSegment(sketch, "E2674", {"start": v(-56.23, 35.45) * mm, "end": v(-56.55, 33.5) * mm});
            skLineSegment(sketch, "E2675", {"start": v(-56.55, 33.5) * mm, "end": v(-56.66, 31.66) * mm});
            skLineSegment(sketch, "E2676", {"start": v(-101.04, 28.09) * mm, "end": v(-101.04, -179.19) * mm});
            skLineSegment(sketch, "E2677", {"start": v(-101.04, -179.19) * mm, "end": v(-100.93, -182.76) * mm});
            skLineSegment(sketch, "E2678", {"start": v(-100.93, -182.76) * mm, "end": v(-100.6, -186.33) * mm});
            skLineSegment(sketch, "E2679", {"start": v(-100.6, -186.33) * mm, "end": v(-100.07, -189.8) * mm});
            skLineSegment(sketch, "E2680", {"start": v(-100.07, -189.8) * mm, "end": v(-99.41, -193.37) * mm});
            skLineSegment(sketch, "E2681", {"start": v(-99.41, -193.37) * mm, "end": v(-98.44, -196.83) * mm});
            skLineSegment(sketch, "E2682", {"start": v(-98.44, -196.83) * mm, "end": v(-97.36, -200.19) * mm});
            skLineSegment(sketch, "E2683", {"start": v(-97.36, -200.19) * mm, "end": v(-95.95, -203.54) * mm});
            skLineSegment(sketch, "E2684", {"start": v(-95.95, -203.54) * mm, "end": v(-94.54, -206.79) * mm});
            skLineSegment(sketch, "E2685", {"start": v(-94.54, -206.79) * mm, "end": v(-92.81, -209.93) * mm});
            skLineSegment(sketch, "E2686", {"start": v(-92.81, -209.93) * mm, "end": v(-90.97, -212.96) * mm});
            skLineSegment(sketch, "E2687", {"start": v(-90.97, -212.96) * mm, "end": v(-88.91, -215.88) * mm});
            skLineSegment(sketch, "E2688", {"start": v(-88.91, -215.88) * mm, "end": v(-86.64, -218.7) * mm});
            skLineSegment(sketch, "E2689", {"start": v(-86.64, -218.7) * mm, "end": v(-84.26, -221.3) * mm});
            skLineSegment(sketch, "E2690", {"start": v(-84.26, -221.3) * mm, "end": v(-81.77, -223.89) * mm});
            skLineSegment(sketch, "E2691", {"start": v(-81.77, -223.89) * mm, "end": v(-79.07, -226.27) * mm});
            skLineSegment(sketch, "E2692", {"start": v(-79.07, -226.27) * mm, "end": v(-76.25, -228.43) * mm});
            skLineSegment(sketch, "E2693", {"start": v(-76.25, -228.43) * mm, "end": v(-73.33, -230.5) * mm});
            skLineSegment(sketch, "E2694", {"start": v(-73.33, -230.5) * mm, "end": v(-70.3, -232.33) * mm});
            skLineSegment(sketch, "E2695", {"start": v(-70.3, -232.33) * mm, "end": v(-67.16, -234.06) * mm});
            skLineSegment(sketch, "E2696", {"start": v(-67.16, -234.06) * mm, "end": v(-63.91, -235.58) * mm});
            skLineSegment(sketch, "E2697", {"start": v(-63.91, -235.58) * mm, "end": v(-60.66, -236.88) * mm});
            skLineSegment(sketch, "E2698", {"start": v(-60.66, -236.88) * mm, "end": v(-57.2, -238.07) * mm});
            skLineSegment(sketch, "E2699", {"start": v(-57.2, -238.07) * mm, "end": v(-53.74, -238.93) * mm});
            skLineSegment(sketch, "E2700", {"start": v(-53.74, -238.93) * mm, "end": v(-50.28, -239.7) * mm});
            skLineSegment(sketch, "E2701", {"start": v(-50.28, -239.7) * mm, "end": v(-46.7, -240.23) * mm});
            skLineSegment(sketch, "E2702", {"start": v(-46.7, -240.23) * mm, "end": v(-43.13, -240.45) * mm});
            skLineSegment(sketch, "E2703", {"start": v(-43.13, -240.45) * mm, "end": v(-39.56, -240.56) * mm});
            skLineSegment(sketch, "E2704", {"start": v(-39.56, -240.56) * mm, "end": v(-36.1, -240.45) * mm});
            skLineSegment(sketch, "E2705", {"start": v(-36.1, -240.45) * mm, "end": v(-32.52, -240.23) * mm});
            skLineSegment(sketch, "E2706", {"start": v(-32.52, -240.23) * mm, "end": v(-28.95, -239.7) * mm});
            skLineSegment(sketch, "E2707", {"start": v(-28.95, -239.7) * mm, "end": v(-25.49, -238.93) * mm});
            skLineSegment(sketch, "E2708", {"start": v(-25.49, -238.93) * mm, "end": v(-22.03, -238.07) * mm});
            skLineSegment(sketch, "E2709", {"start": v(-22.03, -238.07) * mm, "end": v(-18.56, -236.88) * mm});
            skLineSegment(sketch, "E2710", {"start": v(-18.56, -236.88) * mm, "end": v(-15.31, -235.58) * mm});
            skLineSegment(sketch, "E2711", {"start": v(-15.31, -235.58) * mm, "end": v(-12.07, -234.06) * mm});
            skLineSegment(sketch, "E2712", {"start": v(-12.07, -234.06) * mm, "end": v(-8.93, -232.33) * mm});
            skLineSegment(sketch, "E2713", {"start": v(-8.93, -232.33) * mm, "end": v(-5.9, -230.5) * mm});
            skLineSegment(sketch, "E2714", {"start": v(-5.9, -230.5) * mm, "end": v(-2.98, -228.43) * mm});
            skLineSegment(sketch, "E2715", {"start": v(-2.98, -228.43) * mm, "end": v(-0.16, -226.27) * mm});
            skLineSegment(sketch, "E2716", {"start": v(-0.16, -226.27) * mm, "end": v(2.55, -223.89) * mm});
            skLineSegment(sketch, "E2717", {"start": v(2.55, -223.89) * mm, "end": v(5.03, -221.3) * mm});
            skLineSegment(sketch, "E2718", {"start": v(5.03, -221.3) * mm, "end": v(7.42, -218.7) * mm});
            skLineSegment(sketch, "E2719", {"start": v(7.42, -218.7) * mm, "end": v(9.69, -215.88) * mm});
            skLineSegment(sketch, "E2720", {"start": v(9.69, -215.88) * mm, "end": v(11.74, -212.96) * mm});
            skLineSegment(sketch, "E2721", {"start": v(11.74, -212.96) * mm, "end": v(13.59, -209.93) * mm});
            skLineSegment(sketch, "E2722", {"start": v(13.59, -209.93) * mm, "end": v(15.32, -206.79) * mm});
            skLineSegment(sketch, "E2723", {"start": v(15.32, -206.79) * mm, "end": v(16.72, -203.54) * mm});
            skLineSegment(sketch, "E2724", {"start": v(16.72, -203.54) * mm, "end": v(18.13, -200.19) * mm});
            skLineSegment(sketch, "E2725", {"start": v(18.13, -200.19) * mm, "end": v(19.21, -196.83) * mm});
            skLineSegment(sketch, "E2726", {"start": v(19.21, -196.83) * mm, "end": v(20.18, -193.37) * mm});
            skLineSegment(sketch, "E2727", {"start": v(20.18, -193.37) * mm, "end": v(20.84, -189.8) * mm});
            skLineSegment(sketch, "E2728", {"start": v(20.84, -189.8) * mm, "end": v(21.38, -186.33) * mm});
            skLineSegment(sketch, "E2729", {"start": v(21.38, -186.33) * mm, "end": v(21.7, -182.76) * mm});
            skLineSegment(sketch, "E2730", {"start": v(21.7, -182.76) * mm, "end": v(21.81, -179.19) * mm});
            skLineSegment(sketch, "E2731", {"start": v(21.81, -179.19) * mm, "end": v(21.81, 28.09) * mm});
            skLineSegment(sketch, "E2732", {"start": v(21.81, 28.09) * mm, "end": v(21.7, 31.66) * mm});
            skLineSegment(sketch, "E2733", {"start": v(21.7, 31.66) * mm, "end": v(21.38, 35.23) * mm});
            skLineSegment(sketch, "E2734", {"start": v(21.38, 35.23) * mm, "end": v(20.84, 38.8) * mm});
            skLineSegment(sketch, "E2735", {"start": v(20.84, 38.8) * mm, "end": v(20.18, 42.26) * mm});
            skLineSegment(sketch, "E2736", {"start": v(20.18, 42.26) * mm, "end": v(19.21, 45.73) * mm});
            skLineSegment(sketch, "E2737", {"start": v(19.21, 45.73) * mm, "end": v(18.13, 49.08) * mm});
            skLineSegment(sketch, "E2738", {"start": v(18.13, 49.08) * mm, "end": v(16.72, 52.44) * mm});
            skLineSegment(sketch, "E2739", {"start": v(16.72, 52.44) * mm, "end": v(15.32, 55.69) * mm});
            skLineSegment(sketch, "E2740", {"start": v(15.32, 55.69) * mm, "end": v(13.59, 58.83) * mm});
            skLineSegment(sketch, "E2741", {"start": v(13.59, 58.83) * mm, "end": v(11.74, 61.86) * mm});
            skLineSegment(sketch, "E2742", {"start": v(11.74, 61.86) * mm, "end": v(9.69, 64.78) * mm});
            skLineSegment(sketch, "E2743", {"start": v(9.69, 64.78) * mm, "end": v(7.42, 67.6) * mm});
            skLineSegment(sketch, "E2744", {"start": v(7.42, 67.6) * mm, "end": v(5.03, 70.3) * mm});
            skLineSegment(sketch, "E2745", {"start": v(5.03, 70.3) * mm, "end": v(2.55, 72.79) * mm});
            skLineSegment(sketch, "E2746", {"start": v(2.55, 72.79) * mm, "end": v(-0.16, 75.17) * mm});
            skLineSegment(sketch, "E2747", {"start": v(-0.16, 75.17) * mm, "end": v(-2.98, 77.44) * mm});
            skLineSegment(sketch, "E2748", {"start": v(-2.98, 77.44) * mm, "end": v(-5.9, 79.5) * mm});
            skLineSegment(sketch, "E2749", {"start": v(-5.9, 79.5) * mm, "end": v(-8.93, 81.34) * mm});
            skLineSegment(sketch, "E2750", {"start": v(-8.93, 81.34) * mm, "end": v(-12.07, 83.07) * mm});
            skLineSegment(sketch, "E2751", {"start": v(-12.07, 83.07) * mm, "end": v(-15.31, 84.48) * mm});
            skLineSegment(sketch, "E2752", {"start": v(-15.31, 84.48) * mm, "end": v(-18.56, 85.89) * mm});
            skLineSegment(sketch, "E2753", {"start": v(-18.56, 85.89) * mm, "end": v(-22.03, 86.97) * mm});
            skLineSegment(sketch, "E2754", {"start": v(-22.03, 86.97) * mm, "end": v(-25.49, 87.94) * mm});
            skLineSegment(sketch, "E2755", {"start": v(-25.49, 87.94) * mm, "end": v(-28.95, 88.6) * mm});
            skLineSegment(sketch, "E2756", {"start": v(-28.95, 88.6) * mm, "end": v(-32.52, 89.13) * mm});
            skLineSegment(sketch, "E2757", {"start": v(-32.52, 89.13) * mm, "end": v(-36.1, 89.46) * mm});
            skLineSegment(sketch, "E2758", {"start": v(-36.1, 89.46) * mm, "end": v(-39.56, 89.57) * mm});
            skLineSegment(sketch, "E2759", {"start": v(-39.56, 89.57) * mm, "end": v(-43.13, 89.46) * mm});
            skLineSegment(sketch, "E2760", {"start": v(-43.13, 89.46) * mm, "end": v(-46.7, 89.13) * mm});
            skLineSegment(sketch, "E2761", {"start": v(-46.7, 89.13) * mm, "end": v(-50.28, 88.6) * mm});
            skLineSegment(sketch, "E2762", {"start": v(-50.28, 88.6) * mm, "end": v(-53.74, 87.94) * mm});
            skLineSegment(sketch, "E2763", {"start": v(-53.74, 87.94) * mm, "end": v(-57.2, 86.97) * mm});
            skLineSegment(sketch, "E2764", {"start": v(-57.2, 86.97) * mm, "end": v(-60.66, 85.89) * mm});
            skLineSegment(sketch, "E2765", {"start": v(-60.66, 85.89) * mm, "end": v(-63.91, 84.48) * mm});
            skLineSegment(sketch, "E2766", {"start": v(-63.91, 84.48) * mm, "end": v(-67.16, 83.07) * mm});
            skLineSegment(sketch, "E2767", {"start": v(-67.16, 83.07) * mm, "end": v(-70.3, 81.34) * mm});
            skLineSegment(sketch, "E2768", {"start": v(-70.3, 81.34) * mm, "end": v(-73.33, 79.5) * mm});
            skLineSegment(sketch, "E2769", {"start": v(-73.33, 79.5) * mm, "end": v(-76.25, 77.44) * mm});
            skLineSegment(sketch, "E2770", {"start": v(-76.25, 77.44) * mm, "end": v(-79.07, 75.17) * mm});
            skLineSegment(sketch, "E2771", {"start": v(-79.07, 75.17) * mm, "end": v(-81.77, 72.79) * mm});
            skLineSegment(sketch, "E2772", {"start": v(-81.77, 72.79) * mm, "end": v(-84.26, 70.3) * mm});
            skLineSegment(sketch, "E2773", {"start": v(-84.26, 70.3) * mm, "end": v(-86.64, 67.6) * mm});
            skLineSegment(sketch, "E2774", {"start": v(-86.64, 67.6) * mm, "end": v(-88.91, 64.78) * mm});
            skLineSegment(sketch, "E2775", {"start": v(-88.91, 64.78) * mm, "end": v(-90.97, 61.86) * mm});
            skLineSegment(sketch, "E2776", {"start": v(-90.97, 61.86) * mm, "end": v(-92.81, 58.83) * mm});
            skLineSegment(sketch, "E2777", {"start": v(-92.81, 58.83) * mm, "end": v(-94.54, 55.69) * mm});
            skLineSegment(sketch, "E2778", {"start": v(-94.54, 55.69) * mm, "end": v(-95.95, 52.44) * mm});
            skLineSegment(sketch, "E2779", {"start": v(-95.95, 52.44) * mm, "end": v(-97.36, 49.08) * mm});
            skLineSegment(sketch, "E2780", {"start": v(-97.36, 49.08) * mm, "end": v(-98.44, 45.73) * mm});
            skLineSegment(sketch, "E2781", {"start": v(-98.44, 45.73) * mm, "end": v(-99.41, 42.26) * mm});
            skLineSegment(sketch, "E2782", {"start": v(-99.41, 42.26) * mm, "end": v(-100.07, 38.8) * mm});
            skLineSegment(sketch, "E2783", {"start": v(-100.07, 38.8) * mm, "end": v(-100.6, 35.23) * mm});
            skLineSegment(sketch, "E2784", {"start": v(-100.6, 35.23) * mm, "end": v(-100.93, 31.66) * mm});
            skLineSegment(sketch, "E2785", {"start": v(-100.93, 31.66) * mm, "end": v(-101.04, 28.09) * mm});
            skLineSegment(sketch, "E2786", {"start": v(220.75, -101.9) * mm, "end": v(220.75, -211.12) * mm});
            skLineSegment(sketch, "E2787", {"start": v(203.33, -211.12) * mm, "end": v(203.43, -212.42) * mm});
            skLineSegment(sketch, "E2788", {"start": v(203.43, -212.42) * mm, "end": v(203.76, -213.82) * mm});
            skLineSegment(sketch, "E2789", {"start": v(203.76, -213.82) * mm, "end": v(204.3, -215.01) * mm});
            skLineSegment(sketch, "E2790", {"start": v(204.3, -215.01) * mm, "end": v(205.06, -216.2) * mm});
            skLineSegment(sketch, "E2791", {"start": v(205.06, -216.2) * mm, "end": v(205.92, -217.29) * mm});
            skLineSegment(sketch, "E2792", {"start": v(205.92, -217.29) * mm, "end": v(206.9, -218.15) * mm});
            skLineSegment(sketch, "E2793", {"start": v(206.9, -218.15) * mm, "end": v(208.09, -218.8) * mm});
            skLineSegment(sketch, "E2794", {"start": v(208.09, -218.8) * mm, "end": v(209.39, -219.35) * mm});
            skLineSegment(sketch, "E2795", {"start": v(209.39, -219.35) * mm, "end": v(210.68, -219.67) * mm});
            skLineSegment(sketch, "E2796", {"start": v(210.68, -219.67) * mm, "end": v(212.09, -219.78) * mm});
            skLineSegment(sketch, "E2797", {"start": v(212.09, -219.78) * mm, "end": v(213.4, -219.67) * mm});
            skLineSegment(sketch, "E2798", {"start": v(213.4, -219.67) * mm, "end": v(214.69, -219.35) * mm});
            skLineSegment(sketch, "E2799", {"start": v(214.69, -219.35) * mm, "end": v(215.99, -218.8) * mm});
            skLineSegment(sketch, "E2800", {"start": v(215.99, -218.8) * mm, "end": v(217.18, -218.15) * mm});
            skLineSegment(sketch, "E2801", {"start": v(217.18, -218.15) * mm, "end": v(218.15, -217.29) * mm});
            skLineSegment(sketch, "E2802", {"start": v(218.15, -217.29) * mm, "end": v(219.13, -216.2) * mm});
            skLineSegment(sketch, "E2803", {"start": v(219.13, -216.2) * mm, "end": v(219.78, -215.01) * mm});
            skLineSegment(sketch, "E2804", {"start": v(219.78, -215.01) * mm, "end": v(220.32, -213.82) * mm});
            skLineSegment(sketch, "E2805", {"start": v(220.32, -213.82) * mm, "end": v(220.64, -212.42) * mm});
            skLineSegment(sketch, "E2806", {"start": v(220.64, -212.42) * mm, "end": v(220.75, -211.12) * mm});
            skLineSegment(sketch, "E2807", {"start": v(203.33, -211.12) * mm, "end": v(203.33, -101.9) * mm});
            skLineSegment(sketch, "E2808", {"start": v(220.75, -101.9) * mm, "end": v(220.64, -100.5) * mm});
            skLineSegment(sketch, "E2809", {"start": v(220.64, -100.5) * mm, "end": v(220.32, -99.2) * mm});
            skLineSegment(sketch, "E2810", {"start": v(220.32, -99.2) * mm, "end": v(219.78, -97.9) * mm});
            skLineSegment(sketch, "E2811", {"start": v(219.78, -97.9) * mm, "end": v(219.13, -96.82) * mm});
            skLineSegment(sketch, "E2812", {"start": v(219.13, -96.82) * mm, "end": v(218.15, -95.74) * mm});
            skLineSegment(sketch, "E2813", {"start": v(218.15, -95.74) * mm, "end": v(217.18, -94.87) * mm});
            skLineSegment(sketch, "E2814", {"start": v(217.18, -94.87) * mm, "end": v(215.99, -94.12) * mm});
            skLineSegment(sketch, "E2815", {"start": v(215.99, -94.12) * mm, "end": v(214.69, -93.57) * mm});
            skLineSegment(sketch, "E2816", {"start": v(214.69, -93.57) * mm, "end": v(213.4, -93.25) * mm});
            skLineSegment(sketch, "E2817", {"start": v(213.4, -93.25) * mm, "end": v(212.09, -93.14) * mm});
            skLineSegment(sketch, "E2818", {"start": v(212.09, -93.14) * mm, "end": v(210.68, -93.25) * mm});
            skLineSegment(sketch, "E2819", {"start": v(210.68, -93.25) * mm, "end": v(209.39, -93.57) * mm});
            skLineSegment(sketch, "E2820", {"start": v(209.39, -93.57) * mm, "end": v(208.09, -94.12) * mm});
            skLineSegment(sketch, "E2821", {"start": v(208.09, -94.12) * mm, "end": v(206.9, -94.87) * mm});
            skLineSegment(sketch, "E2822", {"start": v(206.9, -94.87) * mm, "end": v(205.92, -95.74) * mm});
            skLineSegment(sketch, "E2823", {"start": v(205.92, -95.74) * mm, "end": v(205.06, -96.82) * mm});
            skLineSegment(sketch, "E2824", {"start": v(205.06, -96.82) * mm, "end": v(204.3, -97.9) * mm});
            skLineSegment(sketch, "E2825", {"start": v(204.3, -97.9) * mm, "end": v(203.76, -99.2) * mm});
            skLineSegment(sketch, "E2826", {"start": v(203.76, -99.2) * mm, "end": v(203.43, -100.5) * mm});
            skLineSegment(sketch, "E2827", {"start": v(203.43, -100.5) * mm, "end": v(203.33, -101.9) * mm});
            skLineSegment(sketch, "E2828", {"start": v(180.7, -103.64) * mm, "end": v(180.7, -209.28) * mm});
            skLineSegment(sketch, "E2829", {"start": v(180.7, -209.28) * mm, "end": v(180.81, -211.88) * mm});
            skLineSegment(sketch, "E2830", {"start": v(180.81, -211.88) * mm, "end": v(181.14, -214.47) * mm});
            skLineSegment(sketch, "E2831", {"start": v(181.14, -214.47) * mm, "end": v(181.68, -216.96) * mm});
            skLineSegment(sketch, "E2832", {"start": v(181.68, -216.96) * mm, "end": v(182.43, -219.45) * mm});
            skLineSegment(sketch, "E2833", {"start": v(182.43, -219.45) * mm, "end": v(183.4, -221.83) * mm});
            skLineSegment(sketch, "E2834", {"start": v(183.4, -221.83) * mm, "end": v(184.5, -224.21) * mm});
            skLineSegment(sketch, "E2835", {"start": v(184.5, -224.21) * mm, "end": v(185.79, -226.38) * mm});
            skLineSegment(sketch, "E2836", {"start": v(185.79, -226.38) * mm, "end": v(187.3, -228.54) * mm});
            skLineSegment(sketch, "E2837", {"start": v(187.3, -228.54) * mm, "end": v(189.04, -230.5) * mm});
            skLineSegment(sketch, "E2838", {"start": v(189.04, -230.5) * mm, "end": v(190.88, -232.33) * mm});
            skLineSegment(sketch, "E2839", {"start": v(190.88, -232.33) * mm, "end": v(192.82, -233.96) * mm});
            skLineSegment(sketch, "E2840", {"start": v(192.82, -233.96) * mm, "end": v(194.88, -235.47) * mm});
            skLineSegment(sketch, "E2841", {"start": v(194.88, -235.47) * mm, "end": v(197.16, -236.88) * mm});
            skLineSegment(sketch, "E2842", {"start": v(197.16, -236.88) * mm, "end": v(199.43, -237.96) * mm});
            skLineSegment(sketch, "E2843", {"start": v(199.43, -237.96) * mm, "end": v(201.92, -238.93) * mm});
            skLineSegment(sketch, "E2844", {"start": v(201.92, -238.93) * mm, "end": v(204.4, -239.7) * mm});
            skLineSegment(sketch, "E2845", {"start": v(204.4, -239.7) * mm, "end": v(206.9, -240.12) * mm});
            skLineSegment(sketch, "E2846", {"start": v(206.9, -240.12) * mm, "end": v(209.5, -240.45) * mm});
            skLineSegment(sketch, "E2847", {"start": v(209.5, -240.45) * mm, "end": v(212.09, -240.56) * mm});
            skLineSegment(sketch, "E2848", {"start": v(212.09, -240.56) * mm, "end": v(214.58, -240.45) * mm});
            skLineSegment(sketch, "E2849", {"start": v(214.58, -240.45) * mm, "end": v(217.18, -240.12) * mm});
            skLineSegment(sketch, "E2850", {"start": v(217.18, -240.12) * mm, "end": v(219.78, -239.7) * mm});
            skLineSegment(sketch, "E2851", {"start": v(219.78, -239.7) * mm, "end": v(222.16, -238.93) * mm});
            skLineSegment(sketch, "E2852", {"start": v(222.16, -238.93) * mm, "end": v(224.64, -237.96) * mm});
            skLineSegment(sketch, "E2853", {"start": v(224.64, -237.96) * mm, "end": v(226.92, -236.88) * mm});
            skLineSegment(sketch, "E2854", {"start": v(226.92, -236.88) * mm, "end": v(229.2, -235.47) * mm});
            skLineSegment(sketch, "E2855", {"start": v(229.2, -235.47) * mm, "end": v(231.25, -233.96) * mm});
            skLineSegment(sketch, "E2856", {"start": v(231.25, -233.96) * mm, "end": v(233.2, -232.33) * mm});
            skLineSegment(sketch, "E2857", {"start": v(233.2, -232.33) * mm, "end": v(235.04, -230.5) * mm});
            skLineSegment(sketch, "E2858", {"start": v(235.04, -230.5) * mm, "end": v(236.77, -228.54) * mm});
            skLineSegment(sketch, "E2859", {"start": v(236.77, -228.54) * mm, "end": v(238.28, -226.38) * mm});
            skLineSegment(sketch, "E2860", {"start": v(238.28, -226.38) * mm, "end": v(239.58, -224.21) * mm});
            skLineSegment(sketch, "E2861", {"start": v(239.58, -224.21) * mm, "end": v(240.66, -221.83) * mm});
            skLineSegment(sketch, "E2862", {"start": v(240.66, -221.83) * mm, "end": v(241.64, -219.45) * mm});
            skLineSegment(sketch, "E2863", {"start": v(241.64, -219.45) * mm, "end": v(242.4, -216.96) * mm});
            skLineSegment(sketch, "E2864", {"start": v(242.4, -216.96) * mm, "end": v(242.94, -214.47) * mm});
            skLineSegment(sketch, "E2865", {"start": v(242.94, -214.47) * mm, "end": v(243.26, -211.88) * mm});
            skLineSegment(sketch, "E2866", {"start": v(243.26, -211.88) * mm, "end": v(243.37, -209.28) * mm});
            skLineSegment(sketch, "E2867", {"start": v(243.37, -209.28) * mm, "end": v(243.37, -103.64) * mm});
            skLineSegment(sketch, "E2868", {"start": v(243.37, -103.64) * mm, "end": v(243.26, -101.04) * mm});
            skLineSegment(sketch, "E2869", {"start": v(243.26, -101.04) * mm, "end": v(242.94, -98.55) * mm});
            skLineSegment(sketch, "E2870", {"start": v(242.94, -98.55) * mm, "end": v(242.4, -95.95) * mm});
            skLineSegment(sketch, "E2871", {"start": v(242.4, -95.95) * mm, "end": v(241.64, -93.47) * mm});
            skLineSegment(sketch, "E2872", {"start": v(241.64, -93.47) * mm, "end": v(240.66, -91.09) * mm});
            skLineSegment(sketch, "E2873", {"start": v(240.66, -91.09) * mm, "end": v(239.58, -88.8) * mm});
            skLineSegment(sketch, "E2874", {"start": v(239.58, -88.8) * mm, "end": v(238.28, -86.54) * mm});
            skLineSegment(sketch, "E2875", {"start": v(238.28, -86.54) * mm, "end": v(236.77, -84.48) * mm});
            skLineSegment(sketch, "E2876", {"start": v(236.77, -84.48) * mm, "end": v(235.04, -82.42) * mm});
            skLineSegment(sketch, "E2877", {"start": v(235.04, -82.42) * mm, "end": v(233.2, -80.7) * mm});
            skLineSegment(sketch, "E2878", {"start": v(233.2, -80.7) * mm, "end": v(231.25, -78.96) * mm});
            skLineSegment(sketch, "E2879", {"start": v(231.25, -78.96) * mm, "end": v(229.2, -77.45) * mm});
            skLineSegment(sketch, "E2880", {"start": v(229.2, -77.45) * mm, "end": v(226.92, -76.15) * mm});
            skLineSegment(sketch, "E2881", {"start": v(226.92, -76.15) * mm, "end": v(224.64, -74.96) * mm});
            skLineSegment(sketch, "E2882", {"start": v(224.64, -74.96) * mm, "end": v(222.16, -74.09) * mm});
            skLineSegment(sketch, "E2883", {"start": v(222.16, -74.09) * mm, "end": v(219.78, -73.33) * mm});
            skLineSegment(sketch, "E2884", {"start": v(219.78, -73.33) * mm, "end": v(217.18, -72.79) * mm});
            skLineSegment(sketch, "E2885", {"start": v(217.18, -72.79) * mm, "end": v(214.58, -72.46) * mm});
            skLineSegment(sketch, "E2886", {"start": v(214.58, -72.46) * mm, "end": v(212.09, -72.36) * mm});
            skLineSegment(sketch, "E2887", {"start": v(212.09, -72.36) * mm, "end": v(209.5, -72.46) * mm});
            skLineSegment(sketch, "E2888", {"start": v(209.5, -72.46) * mm, "end": v(206.9, -72.79) * mm});
            skLineSegment(sketch, "E2889", {"start": v(206.9, -72.79) * mm, "end": v(204.4, -73.33) * mm});
            skLineSegment(sketch, "E2890", {"start": v(204.4, -73.33) * mm, "end": v(201.92, -74.09) * mm});
            skLineSegment(sketch, "E2891", {"start": v(201.92, -74.09) * mm, "end": v(199.43, -74.96) * mm});
            skLineSegment(sketch, "E2892", {"start": v(199.43, -74.96) * mm, "end": v(197.16, -76.15) * mm});
            skLineSegment(sketch, "E2893", {"start": v(197.16, -76.15) * mm, "end": v(194.88, -77.45) * mm});
            skLineSegment(sketch, "E2894", {"start": v(194.88, -77.45) * mm, "end": v(192.82, -78.96) * mm});
            skLineSegment(sketch, "E2895", {"start": v(192.82, -78.96) * mm, "end": v(190.88, -80.7) * mm});
            skLineSegment(sketch, "E2896", {"start": v(190.88, -80.7) * mm, "end": v(189.04, -82.42) * mm});
            skLineSegment(sketch, "E2897", {"start": v(189.04, -82.42) * mm, "end": v(187.3, -84.48) * mm});
            skLineSegment(sketch, "E2898", {"start": v(187.3, -84.48) * mm, "end": v(185.79, -86.54) * mm});
            skLineSegment(sketch, "E2899", {"start": v(185.79, -86.54) * mm, "end": v(184.5, -88.8) * mm});
            skLineSegment(sketch, "E2900", {"start": v(184.5, -88.8) * mm, "end": v(183.4, -91.09) * mm});
            skLineSegment(sketch, "E2901", {"start": v(183.4, -91.09) * mm, "end": v(182.43, -93.47) * mm});
            skLineSegment(sketch, "E2902", {"start": v(182.43, -93.47) * mm, "end": v(181.68, -95.95) * mm});
            skLineSegment(sketch, "E2903", {"start": v(181.68, -95.95) * mm, "end": v(181.14, -98.55) * mm});
            skLineSegment(sketch, "E2904", {"start": v(181.14, -98.55) * mm, "end": v(180.81, -101.04) * mm});
            skLineSegment(sketch, "E2905", {"start": v(180.81, -101.04) * mm, "end": v(180.7, -103.64) * mm});
            skLineSegment(sketch, "E2906", {"start": v(96.93, 60.02) * mm, "end": v(96.93, -49.2) * mm});
            skLineSegment(sketch, "E2907", {"start": v(79.5, -49.2) * mm, "end": v(79.61, -50.5) * mm});
            skLineSegment(sketch, "E2908", {"start": v(79.61, -50.5) * mm, "end": v(79.94, -51.9) * mm});
            skLineSegment(sketch, "E2909", {"start": v(79.94, -51.9) * mm, "end": v(80.47, -53.09) * mm});
            skLineSegment(sketch, "E2910", {"start": v(80.47, -53.09) * mm, "end": v(81.12, -54.28) * mm});
            skLineSegment(sketch, "E2911", {"start": v(81.12, -54.28) * mm, "end": v(81.99, -55.37) * mm});
            skLineSegment(sketch, "E2912", {"start": v(81.99, -55.37) * mm, "end": v(83.07, -56.23) * mm});
            skLineSegment(sketch, "E2913", {"start": v(83.07, -56.23) * mm, "end": v(84.26, -56.88) * mm});
            skLineSegment(sketch, "E2914", {"start": v(84.26, -56.88) * mm, "end": v(85.45, -57.42) * mm});
            skLineSegment(sketch, "E2915", {"start": v(85.45, -57.42) * mm, "end": v(86.86, -57.75) * mm});
            skLineSegment(sketch, "E2916", {"start": v(86.86, -57.75) * mm, "end": v(88.16, -57.85) * mm});
            skLineSegment(sketch, "E2917", {"start": v(88.16, -57.85) * mm, "end": v(89.57, -57.75) * mm});
            skLineSegment(sketch, "E2918", {"start": v(89.57, -57.75) * mm, "end": v(90.86, -57.42) * mm});
            skLineSegment(sketch, "E2919", {"start": v(90.86, -57.42) * mm, "end": v(92.16, -56.88) * mm});
            skLineSegment(sketch, "E2920", {"start": v(92.16, -56.88) * mm, "end": v(93.24, -56.23) * mm});
            skLineSegment(sketch, "E2921", {"start": v(93.24, -56.23) * mm, "end": v(94.33, -55.37) * mm});
            skLineSegment(sketch, "E2922", {"start": v(94.33, -55.37) * mm, "end": v(95.2, -54.28) * mm});
            skLineSegment(sketch, "E2923", {"start": v(95.2, -54.28) * mm, "end": v(95.95, -53.09) * mm});
            skLineSegment(sketch, "E2924", {"start": v(95.95, -53.09) * mm, "end": v(96.5, -51.9) * mm});
            skLineSegment(sketch, "E2925", {"start": v(96.5, -51.9) * mm, "end": v(96.82, -50.5) * mm});
            skLineSegment(sketch, "E2926", {"start": v(96.82, -50.5) * mm, "end": v(96.93, -49.2) * mm});
            skLineSegment(sketch, "E2927", {"start": v(79.5, -49.2) * mm, "end": v(79.5, 60.02) * mm});
            skLineSegment(sketch, "E2928", {"start": v(96.93, 60.02) * mm, "end": v(96.82, 61.42) * mm});
            skLineSegment(sketch, "E2929", {"start": v(96.82, 61.42) * mm, "end": v(96.5, 62.72) * mm});
            skLineSegment(sketch, "E2930", {"start": v(96.5, 62.72) * mm, "end": v(95.95, 64.02) * mm});
            skLineSegment(sketch, "E2931", {"start": v(95.95, 64.02) * mm, "end": v(95.2, 65.1) * mm});
            skLineSegment(sketch, "E2932", {"start": v(95.2, 65.1) * mm, "end": v(94.33, 66.18) * mm});
            skLineSegment(sketch, "E2933", {"start": v(94.33, 66.18) * mm, "end": v(93.24, 67.05) * mm});
            skLineSegment(sketch, "E2934", {"start": v(93.24, 67.05) * mm, "end": v(92.16, 67.8) * mm});
            skLineSegment(sketch, "E2935", {"start": v(92.16, 67.8) * mm, "end": v(90.86, 68.35) * mm});
            skLineSegment(sketch, "E2936", {"start": v(90.86, 68.35) * mm, "end": v(89.57, 68.68) * mm});
            skLineSegment(sketch, "E2937", {"start": v(89.57, 68.68) * mm, "end": v(88.16, 68.78) * mm});
            skLineSegment(sketch, "E2938", {"start": v(88.16, 68.78) * mm, "end": v(86.86, 68.68) * mm});
            skLineSegment(sketch, "E2939", {"start": v(86.86, 68.68) * mm, "end": v(85.45, 68.35) * mm});
            skLineSegment(sketch, "E2940", {"start": v(85.45, 68.35) * mm, "end": v(84.26, 67.8) * mm});
            skLineSegment(sketch, "E2941", {"start": v(84.26, 67.8) * mm, "end": v(83.07, 67.05) * mm});
            skLineSegment(sketch, "E2942", {"start": v(83.07, 67.05) * mm, "end": v(81.99, 66.18) * mm});
            skLineSegment(sketch, "E2943", {"start": v(81.99, 66.18) * mm, "end": v(81.12, 65.1) * mm});
            skLineSegment(sketch, "E2944", {"start": v(81.12, 65.1) * mm, "end": v(80.47, 64.02) * mm});
            skLineSegment(sketch, "E2945", {"start": v(80.47, 64.02) * mm, "end": v(79.94, 62.72) * mm});
            skLineSegment(sketch, "E2946", {"start": v(79.94, 62.72) * mm, "end": v(79.61, 61.42) * mm});
            skLineSegment(sketch, "E2947", {"start": v(79.61, 61.42) * mm, "end": v(79.5, 60.02) * mm});
            skLineSegment(sketch, "E2948", {"start": v(56.88, 58.28) * mm, "end": v(56.88, -47.35) * mm});
            skLineSegment(sketch, "E2949", {"start": v(56.88, -47.35) * mm, "end": v(56.99, -49.96) * mm});
            skLineSegment(sketch, "E2950", {"start": v(56.99, -49.96) * mm, "end": v(57.31, -52.55) * mm});
            skLineSegment(sketch, "E2951", {"start": v(57.31, -52.55) * mm, "end": v(57.86, -55.04) * mm});
            skLineSegment(sketch, "E2952", {"start": v(57.86, -55.04) * mm, "end": v(58.6, -57.53) * mm});
            skLineSegment(sketch, "E2953", {"start": v(58.6, -57.53) * mm, "end": v(59.48, -59.9) * mm});
            skLineSegment(sketch, "E2954", {"start": v(59.48, -59.9) * mm, "end": v(60.67, -62.29) * mm});
            skLineSegment(sketch, "E2955", {"start": v(60.67, -62.29) * mm, "end": v(61.97, -64.46) * mm});
            skLineSegment(sketch, "E2956", {"start": v(61.97, -64.46) * mm, "end": v(63.48, -66.62) * mm});
            skLineSegment(sketch, "E2957", {"start": v(63.48, -66.62) * mm, "end": v(65.21, -68.57) * mm});
            skLineSegment(sketch, "E2958", {"start": v(65.21, -68.57) * mm, "end": v(66.95, -70.4) * mm});
            skLineSegment(sketch, "E2959", {"start": v(66.95, -70.4) * mm, "end": v(69, -72.04) * mm});
            skLineSegment(sketch, "E2960", {"start": v(69, -72.04) * mm, "end": v(71.06, -73.55) * mm});
            skLineSegment(sketch, "E2961", {"start": v(71.06, -73.55) * mm, "end": v(73.33, -74.96) * mm});
            skLineSegment(sketch, "E2962", {"start": v(73.33, -74.96) * mm, "end": v(75.6, -76.04) * mm});
            skLineSegment(sketch, "E2963", {"start": v(75.6, -76.04) * mm, "end": v(77.98, -77.01) * mm});
            skLineSegment(sketch, "E2964", {"start": v(77.98, -77.01) * mm, "end": v(80.47, -77.77) * mm});
            skLineSegment(sketch, "E2965", {"start": v(80.47, -77.77) * mm, "end": v(83.07, -78.3) * mm});
            skLineSegment(sketch, "E2966", {"start": v(83.07, -78.3) * mm, "end": v(85.56, -78.53) * mm});
            skLineSegment(sketch, "E2967", {"start": v(85.56, -78.53) * mm, "end": v(88.16, -78.63) * mm});
            skLineSegment(sketch, "E2968", {"start": v(88.16, -78.63) * mm, "end": v(90.76, -78.53) * mm});
            skLineSegment(sketch, "E2969", {"start": v(90.76, -78.53) * mm, "end": v(93.35, -78.3) * mm});
            skLineSegment(sketch, "E2970", {"start": v(93.35, -78.3) * mm, "end": v(95.85, -77.77) * mm});
            skLineSegment(sketch, "E2971", {"start": v(95.85, -77.77) * mm, "end": v(98.33, -77.01) * mm});
            skLineSegment(sketch, "E2972", {"start": v(98.33, -77.01) * mm, "end": v(100.72, -76.04) * mm});
            skLineSegment(sketch, "E2973", {"start": v(100.72, -76.04) * mm, "end": v(103.1, -74.96) * mm});
            skLineSegment(sketch, "E2974", {"start": v(103.1, -74.96) * mm, "end": v(105.26, -73.55) * mm});
            skLineSegment(sketch, "E2975", {"start": v(105.26, -73.55) * mm, "end": v(107.43, -72.04) * mm});
            skLineSegment(sketch, "E2976", {"start": v(107.43, -72.04) * mm, "end": v(109.37, -70.4) * mm});
            skLineSegment(sketch, "E2977", {"start": v(109.37, -70.4) * mm, "end": v(111.21, -68.57) * mm});
            skLineSegment(sketch, "E2978", {"start": v(111.21, -68.57) * mm, "end": v(112.84, -66.62) * mm});
            skLineSegment(sketch, "E2979", {"start": v(112.84, -66.62) * mm, "end": v(114.35, -64.46) * mm});
            skLineSegment(sketch, "E2980", {"start": v(114.35, -64.46) * mm, "end": v(115.76, -62.29) * mm});
            skLineSegment(sketch, "E2981", {"start": v(115.76, -62.29) * mm, "end": v(116.84, -59.9) * mm});
            skLineSegment(sketch, "E2982", {"start": v(116.84, -59.9) * mm, "end": v(117.82, -57.53) * mm});
            skLineSegment(sketch, "E2983", {"start": v(117.82, -57.53) * mm, "end": v(118.57, -55.04) * mm});
            skLineSegment(sketch, "E2984", {"start": v(118.57, -55.04) * mm, "end": v(119, -52.55) * mm});
            skLineSegment(sketch, "E2985", {"start": v(119, -52.55) * mm, "end": v(119.33, -49.96) * mm});
            skLineSegment(sketch, "E2986", {"start": v(119.33, -49.96) * mm, "end": v(119.44, -47.35) * mm});
            skLineSegment(sketch, "E2987", {"start": v(119.44, -47.35) * mm, "end": v(119.44, 58.28) * mm});
            skLineSegment(sketch, "E2988", {"start": v(119.44, 58.28) * mm, "end": v(119.33, 60.88) * mm});
            skLineSegment(sketch, "E2989", {"start": v(119.33, 60.88) * mm, "end": v(119, 63.37) * mm});
            skLineSegment(sketch, "E2990", {"start": v(119, 63.37) * mm, "end": v(118.57, 65.97) * mm});
            skLineSegment(sketch, "E2991", {"start": v(118.57, 65.97) * mm, "end": v(117.82, 68.46) * mm});
            skLineSegment(sketch, "E2992", {"start": v(117.82, 68.46) * mm, "end": v(116.84, 70.84) * mm});
            skLineSegment(sketch, "E2993", {"start": v(116.84, 70.84) * mm, "end": v(115.76, 73.11) * mm});
            skLineSegment(sketch, "E2994", {"start": v(115.76, 73.11) * mm, "end": v(114.35, 75.38) * mm});
            skLineSegment(sketch, "E2995", {"start": v(114.35, 75.38) * mm, "end": v(112.84, 77.44) * mm});
            skLineSegment(sketch, "E2996", {"start": v(112.84, 77.44) * mm, "end": v(111.21, 79.5) * mm});
            skLineSegment(sketch, "E2997", {"start": v(111.21, 79.5) * mm, "end": v(109.37, 81.23) * mm});
            skLineSegment(sketch, "E2998", {"start": v(109.37, 81.23) * mm, "end": v(107.43, 82.96) * mm});
            skLineSegment(sketch, "E2999", {"start": v(107.43, 82.96) * mm, "end": v(105.26, 84.48) * mm});
            skLineSegment(sketch, "E3000", {"start": v(105.26, 84.48) * mm, "end": v(103.1, 85.78) * mm});
            skLineSegment(sketch, "E3001", {"start": v(103.1, 85.78) * mm, "end": v(100.72, 86.97) * mm});
            skLineSegment(sketch, "E3002", {"start": v(100.72, 86.97) * mm, "end": v(98.33, 87.83) * mm});
            skLineSegment(sketch, "E3003", {"start": v(98.33, 87.83) * mm, "end": v(95.85, 88.6) * mm});
            skLineSegment(sketch, "E3004", {"start": v(95.85, 88.6) * mm, "end": v(93.35, 89.13) * mm});
            skLineSegment(sketch, "E3005", {"start": v(93.35, 89.13) * mm, "end": v(90.76, 89.46) * mm});
            skLineSegment(sketch, "E3006", {"start": v(90.76, 89.46) * mm, "end": v(88.16, 89.57) * mm});
            skLineSegment(sketch, "E3007", {"start": v(88.16, 89.57) * mm, "end": v(85.56, 89.46) * mm});
            skLineSegment(sketch, "E3008", {"start": v(85.56, 89.46) * mm, "end": v(83.07, 89.13) * mm});
            skLineSegment(sketch, "E3009", {"start": v(83.07, 89.13) * mm, "end": v(80.47, 88.6) * mm});
            skLineSegment(sketch, "E3010", {"start": v(80.47, 88.6) * mm, "end": v(77.98, 87.83) * mm});
            skLineSegment(sketch, "E3011", {"start": v(77.98, 87.83) * mm, "end": v(75.6, 86.97) * mm});
            skLineSegment(sketch, "E3012", {"start": v(75.6, 86.97) * mm, "end": v(73.33, 85.78) * mm});
            skLineSegment(sketch, "E3013", {"start": v(73.33, 85.78) * mm, "end": v(71.06, 84.48) * mm});
            skLineSegment(sketch, "E3014", {"start": v(71.06, 84.48) * mm, "end": v(69, 82.96) * mm});
            skLineSegment(sketch, "E3015", {"start": v(69, 82.96) * mm, "end": v(66.95, 81.23) * mm});
            skLineSegment(sketch, "E3016", {"start": v(66.95, 81.23) * mm, "end": v(65.21, 79.5) * mm});
            skLineSegment(sketch, "E3017", {"start": v(65.21, 79.5) * mm, "end": v(63.48, 77.44) * mm});
            skLineSegment(sketch, "E3018", {"start": v(63.48, 77.44) * mm, "end": v(61.97, 75.38) * mm});
            skLineSegment(sketch, "E3019", {"start": v(61.97, 75.38) * mm, "end": v(60.67, 73.11) * mm});
            skLineSegment(sketch, "E3020", {"start": v(60.67, 73.11) * mm, "end": v(59.48, 70.84) * mm});
            skLineSegment(sketch, "E3021", {"start": v(59.48, 70.84) * mm, "end": v(58.6, 68.46) * mm});
            skLineSegment(sketch, "E3022", {"start": v(58.6, 68.46) * mm, "end": v(57.86, 65.97) * mm});
            skLineSegment(sketch, "E3023", {"start": v(57.86, 65.97) * mm, "end": v(57.31, 63.37) * mm});
            skLineSegment(sketch, "E3024", {"start": v(57.31, 63.37) * mm, "end": v(56.99, 60.88) * mm});
            skLineSegment(sketch, "E3025", {"start": v(56.99, 60.88) * mm, "end": v(56.88, 58.28) * mm});
            skLineSegment(sketch, "E3026", {"start": v(-63.26, -328.45) * mm, "end": v(-82.64, -328.45) * mm});
            skLineSegment(sketch, "E3027", {"start": v(-82.64, -328.45) * mm, "end": v(-82.64, -387.54) * mm});
            skLineSegment(sketch, "E3028", {"start": v(-82.64, -387.54) * mm, "end": v(-63.26, -387.54) * mm});
            skLineSegment(sketch, "E3029", {"start": v(-63.26, -387.54) * mm, "end": v(-63.26, -379.32) * mm});
            skLineSegment(sketch, "E3030", {"start": v(-63.26, -379.32) * mm, "end": v(-74.63, -379.32) * mm});
            skLineSegment(sketch, "E3031", {"start": v(-74.63, -379.32) * mm, "end": v(-74.63, -362.33) * mm});
            skLineSegment(sketch, "E3032", {"start": v(-74.63, -362.33) * mm, "end": v(-66.51, -362.33) * mm});
            skLineSegment(sketch, "E3033", {"start": v(-66.51, -362.33) * mm, "end": v(-66.51, -353.45) * mm});
            skLineSegment(sketch, "E3034", {"start": v(-66.51, -353.45) * mm, "end": v(-74.63, -353.45) * mm});
            skLineSegment(sketch, "E3035", {"start": v(-74.63, -353.45) * mm, "end": v(-74.63, -338.08) * mm});
            skLineSegment(sketch, "E3036", {"start": v(-74.63, -338.08) * mm, "end": v(-63.26, -338.08) * mm});
            skLineSegment(sketch, "E3037", {"start": v(-63.26, -338.08) * mm, "end": v(-63.26, -328.45) * mm});
            skLineSegment(sketch, "E3038", {"start": v(48.98, -328.45) * mm, "end": v(29.6, -328.45) * mm});
            skLineSegment(sketch, "E3039", {"start": v(29.6, -328.45) * mm, "end": v(29.6, -387.98) * mm});
            skLineSegment(sketch, "E3040", {"start": v(29.6, -387.98) * mm, "end": v(48.98, -387.98) * mm});
            skLineSegment(sketch, "E3041", {"start": v(48.98, -387.98) * mm, "end": v(48.98, -379.32) * mm});
            skLineSegment(sketch, "E3042", {"start": v(48.98, -379.32) * mm, "end": v(37.72, -379.32) * mm});
            skLineSegment(sketch, "E3043", {"start": v(37.72, -379.32) * mm, "end": v(37.72, -362.33) * mm});
            skLineSegment(sketch, "E3044", {"start": v(37.72, -362.33) * mm, "end": v(45.73, -362.33) * mm});
            skLineSegment(sketch, "E3045", {"start": v(45.73, -362.33) * mm, "end": v(45.73, -353.45) * mm});
            skLineSegment(sketch, "E3046", {"start": v(45.73, -353.45) * mm, "end": v(37.72, -353.45) * mm});
            skLineSegment(sketch, "E3047", {"start": v(37.72, -353.45) * mm, "end": v(37.72, -338.08) * mm});
            skLineSegment(sketch, "E3048", {"start": v(37.72, -338.08) * mm, "end": v(48.98, -338.08) * mm});
            skLineSegment(sketch, "E3049", {"start": v(48.98, -338.08) * mm, "end": v(48.98, -328.45) * mm});
            skLineSegment(sketch, "E3050", {"start": v(113.38, -328.45) * mm, "end": v(123.88, -328.45) * mm});
            skLineSegment(sketch, "E3051", {"start": v(118.68, -343.92) * mm, "end": v(122.04, -367.2) * mm});
            skLineSegment(sketch, "E3052", {"start": v(122.04, -367.2) * mm, "end": v(115.22, -367.2) * mm});
            skLineSegment(sketch, "E3053", {"start": v(115.22, -367.2) * mm, "end": v(118.68, -343.92) * mm});
            skLineSegment(sketch, "E3054", {"start": v(123.88, -328.45) * mm, "end": v(113.38, -328.45) * mm});
            skLineSegment(sketch, "E3055", {"start": v(113.38, -328.45) * mm, "end": v(104.72, -387.98) * mm});
            skLineSegment(sketch, "E3056", {"start": v(104.72, -387.98) * mm, "end": v(112.2, -387.98) * mm});
            skLineSegment(sketch, "E3057", {"start": v(112.2, -387.98) * mm, "end": v(113.92, -376.18) * mm});
            skLineSegment(sketch, "E3058", {"start": v(113.92, -376.18) * mm, "end": v(123.34, -376.18) * mm});
            skLineSegment(sketch, "E3059", {"start": v(123.34, -376.18) * mm, "end": v(125.07, -387.98) * mm});
            skLineSegment(sketch, "E3060", {"start": v(125.07, -387.98) * mm, "end": v(132.54, -387.98) * mm});
            skLineSegment(sketch, "E3061", {"start": v(132.54, -387.98) * mm, "end": v(123.88, -328.45) * mm});
            skLineSegment(sketch, "E3062", {"start": v(184.82, -343.92) * mm, "end": v(188.17, -367.2) * mm});
            skLineSegment(sketch, "E3063", {"start": v(188.17, -367.2) * mm, "end": v(181.35, -367.2) * mm});
            skLineSegment(sketch, "E3064", {"start": v(181.35, -367.2) * mm, "end": v(184.82, -343.92) * mm});
            skLineSegment(sketch, "E3065", {"start": v(190, -328.45) * mm, "end": v(179.51, -328.45) * mm});
            skLineSegment(sketch, "E3066", {"start": v(179.51, -328.45) * mm, "end": v(170.85, -387.98) * mm});
            skLineSegment(sketch, "E3067", {"start": v(170.85, -387.98) * mm, "end": v(178.32, -387.98) * mm});
            skLineSegment(sketch, "E3068", {"start": v(178.32, -387.98) * mm, "end": v(180.05, -376.18) * mm});
            skLineSegment(sketch, "E3069", {"start": v(180.05, -376.18) * mm, "end": v(189.47, -376.18) * mm});
            skLineSegment(sketch, "E3070", {"start": v(189.47, -376.18) * mm, "end": v(191.2, -387.98) * mm});
            skLineSegment(sketch, "E3071", {"start": v(191.2, -387.98) * mm, "end": v(198.67, -387.98) * mm});
            skLineSegment(sketch, "E3072", {"start": v(198.67, -387.98) * mm, "end": v(190, -328.45) * mm});
            skLineSegment(sketch, "E3073", {"start": v(-200.18, -338.84) * mm, "end": v(-200.18, -377.15) * mm});
            skLineSegment(sketch, "E3074", {"start": v(-206.24, -377.15) * mm, "end": v(-206.24, -377.8) * mm});
            skLineSegment(sketch, "E3075", {"start": v(-206.24, -377.8) * mm, "end": v(-206.03, -378.34) * mm});
            skLineSegment(sketch, "E3076", {"start": v(-206.03, -378.34) * mm, "end": v(-205.7, -378.89) * mm});
            skLineSegment(sketch, "E3077", {"start": v(-205.7, -378.89) * mm, "end": v(-205.38, -379.32) * mm});
            skLineSegment(sketch, "E3078", {"start": v(-205.38, -379.32) * mm, "end": v(-204.95, -379.75) * mm});
            skLineSegment(sketch, "E3079", {"start": v(-204.95, -379.75) * mm, "end": v(-204.4, -379.97) * mm});
            skLineSegment(sketch, "E3080", {"start": v(-204.4, -379.97) * mm, "end": v(-203.76, -380.18) * mm});
            skLineSegment(sketch, "E3081", {"start": v(-203.76, -380.18) * mm, "end": v(-202.57, -380.18) * mm});
            skLineSegment(sketch, "E3082", {"start": v(-202.57, -380.18) * mm, "end": v(-201.48, -379.75) * mm});
            skLineSegment(sketch, "E3083", {"start": v(-201.48, -379.75) * mm, "end": v(-200.62, -378.89) * mm});
            skLineSegment(sketch, "E3084", {"start": v(-200.62, -378.89) * mm, "end": v(-200.18, -377.8) * mm});
            skLineSegment(sketch, "E3085", {"start": v(-200.18, -377.8) * mm, "end": v(-200.18, -377.15) * mm});
            skLineSegment(sketch, "E3086", {"start": v(-206.24, -377.15) * mm, "end": v(-206.24, -338.84) * mm});
            skLineSegment(sketch, "E3087", {"start": v(-200.18, -338.84) * mm, "end": v(-200.18, -338.3) * mm});
            skLineSegment(sketch, "E3088", {"start": v(-200.18, -338.3) * mm, "end": v(-200.4, -337.65) * mm});
            skLineSegment(sketch, "E3089", {"start": v(-200.4, -337.65) * mm, "end": v(-200.62, -337.21) * mm});
            skLineSegment(sketch, "E3090", {"start": v(-200.62, -337.21) * mm, "end": v(-201.05, -336.67) * mm});
            skLineSegment(sketch, "E3091", {"start": v(-201.05, -336.67) * mm, "end": v(-201.48, -336.35) * mm});
            skLineSegment(sketch, "E3092", {"start": v(-201.48, -336.35) * mm, "end": v(-202.02, -336.02) * mm});
            skLineSegment(sketch, "E3093", {"start": v(-202.02, -336.02) * mm, "end": v(-202.57, -335.91) * mm});
            skLineSegment(sketch, "E3094", {"start": v(-202.57, -335.91) * mm, "end": v(-203.21, -335.8) * mm});
            skLineSegment(sketch, "E3095", {"start": v(-203.21, -335.8) * mm, "end": v(-203.76, -335.91) * mm});
            skLineSegment(sketch, "E3096", {"start": v(-203.76, -335.91) * mm, "end": v(-204.4, -336.02) * mm});
            skLineSegment(sketch, "E3097", {"start": v(-204.4, -336.02) * mm, "end": v(-204.95, -336.35) * mm});
            skLineSegment(sketch, "E3098", {"start": v(-204.95, -336.35) * mm, "end": v(-205.38, -336.67) * mm});
            skLineSegment(sketch, "E3099", {"start": v(-205.38, -336.67) * mm, "end": v(-205.7, -337.21) * mm});
            skLineSegment(sketch, "E3100", {"start": v(-205.7, -337.21) * mm, "end": v(-206.03, -337.65) * mm});
            skLineSegment(sketch, "E3101", {"start": v(-206.03, -337.65) * mm, "end": v(-206.24, -338.3) * mm});
            skLineSegment(sketch, "E3102", {"start": v(-206.24, -338.3) * mm, "end": v(-206.24, -338.84) * mm});
            skLineSegment(sketch, "E3103", {"start": v(-214.15, -339.49) * mm, "end": v(-214.15, -376.5) * mm});
            skLineSegment(sketch, "E3104", {"start": v(-214.15, -376.5) * mm, "end": v(-214.15, -377.7) * mm});
            skLineSegment(sketch, "E3105", {"start": v(-214.15, -377.7) * mm, "end": v(-213.93, -378.89) * mm});
            skLineSegment(sketch, "E3106", {"start": v(-213.93, -378.89) * mm, "end": v(-213.6, -379.97) * mm});
            skLineSegment(sketch, "E3107", {"start": v(-213.6, -379.97) * mm, "end": v(-213.28, -381.05) * mm});
            skLineSegment(sketch, "E3108", {"start": v(-213.28, -381.05) * mm, "end": v(-212.74, -382.02) * mm});
            skLineSegment(sketch, "E3109", {"start": v(-212.74, -382.02) * mm, "end": v(-212.1, -383) * mm});
            skLineSegment(sketch, "E3110", {"start": v(-212.1, -383) * mm, "end": v(-211.33, -383.86) * mm});
            skLineSegment(sketch, "E3111", {"start": v(-211.33, -383.86) * mm, "end": v(-210.57, -384.73) * mm});
            skLineSegment(sketch, "E3112", {"start": v(-210.57, -384.73) * mm, "end": v(-209.7, -385.49) * mm});
            skLineSegment(sketch, "E3113", {"start": v(-209.7, -385.49) * mm, "end": v(-208.73, -386.03) * mm});
            skLineSegment(sketch, "E3114", {"start": v(-208.73, -386.03) * mm, "end": v(-207.65, -386.57) * mm});
            skLineSegment(sketch, "E3115", {"start": v(-207.65, -386.57) * mm, "end": v(-206.57, -387) * mm});
            skLineSegment(sketch, "E3116", {"start": v(-206.57, -387) * mm, "end": v(-205.49, -387.33) * mm});
            skLineSegment(sketch, "E3117", {"start": v(-205.49, -387.33) * mm, "end": v(-204.4, -387.44) * mm});
            skLineSegment(sketch, "E3118", {"start": v(-204.4, -387.44) * mm, "end": v(-203.21, -387.54) * mm});
            skLineSegment(sketch, "E3119", {"start": v(-203.21, -387.54) * mm, "end": v(-202.02, -387.44) * mm});
            skLineSegment(sketch, "E3120", {"start": v(-202.02, -387.44) * mm, "end": v(-200.94, -387.33) * mm});
            skLineSegment(sketch, "E3121", {"start": v(-200.94, -387.33) * mm, "end": v(-199.86, -387) * mm});
            skLineSegment(sketch, "E3122", {"start": v(-199.86, -387) * mm, "end": v(-198.78, -386.57) * mm});
            skLineSegment(sketch, "E3123", {"start": v(-198.78, -386.57) * mm, "end": v(-197.7, -386.03) * mm});
            skLineSegment(sketch, "E3124", {"start": v(-197.7, -386.03) * mm, "end": v(-196.72, -385.49) * mm});
            skLineSegment(sketch, "E3125", {"start": v(-196.72, -385.49) * mm, "end": v(-195.86, -384.73) * mm});
            skLineSegment(sketch, "E3126", {"start": v(-195.86, -384.73) * mm, "end": v(-195.1, -383.86) * mm});
            skLineSegment(sketch, "E3127", {"start": v(-195.1, -383.86) * mm, "end": v(-194.34, -383) * mm});
            skLineSegment(sketch, "E3128", {"start": v(-194.34, -383) * mm, "end": v(-193.69, -382.02) * mm});
            skLineSegment(sketch, "E3129", {"start": v(-193.69, -382.02) * mm, "end": v(-193.15, -381.05) * mm});
            skLineSegment(sketch, "E3130", {"start": v(-193.15, -381.05) * mm, "end": v(-192.72, -379.97) * mm});
            skLineSegment(sketch, "E3131", {"start": v(-192.72, -379.97) * mm, "end": v(-192.5, -378.89) * mm});
            skLineSegment(sketch, "E3132", {"start": v(-192.5, -378.89) * mm, "end": v(-192.28, -377.7) * mm});
            skLineSegment(sketch, "E3133", {"start": v(-192.28, -377.7) * mm, "end": v(-192.17, -376.5) * mm});
            skLineSegment(sketch, "E3134", {"start": v(-192.17, -376.5) * mm, "end": v(-192.17, -339.49) * mm});
            skLineSegment(sketch, "E3135", {"start": v(-192.17, -339.49) * mm, "end": v(-192.28, -338.3) * mm});
            skLineSegment(sketch, "E3136", {"start": v(-192.28, -338.3) * mm, "end": v(-192.72, -336.13) * mm});
            skLineSegment(sketch, "E3137", {"start": v(-192.72, -336.13) * mm, "end": v(-193.15, -335.05) * mm});
            skLineSegment(sketch, "E3138", {"start": v(-193.15, -335.05) * mm, "end": v(-193.69, -333.97) * mm});
            skLineSegment(sketch, "E3139", {"start": v(-193.69, -333.97) * mm, "end": v(-194.34, -333) * mm});
            skLineSegment(sketch, "E3140", {"start": v(-194.34, -333) * mm, "end": v(-195.1, -332.13) * mm});
            skLineSegment(sketch, "E3141", {"start": v(-195.1, -332.13) * mm, "end": v(-195.86, -331.37) * mm});
            skLineSegment(sketch, "E3142", {"start": v(-195.86, -331.37) * mm, "end": v(-196.72, -330.61) * mm});
            skLineSegment(sketch, "E3143", {"start": v(-196.72, -330.61) * mm, "end": v(-197.7, -329.96) * mm});
            skLineSegment(sketch, "E3144", {"start": v(-197.7, -329.96) * mm, "end": v(-198.78, -329.42) * mm});
            skLineSegment(sketch, "E3145", {"start": v(-198.78, -329.42) * mm, "end": v(-199.86, -328.99) * mm});
            skLineSegment(sketch, "E3146", {"start": v(-199.86, -328.99) * mm, "end": v(-200.94, -328.77) * mm});
            skLineSegment(sketch, "E3147", {"start": v(-200.94, -328.77) * mm, "end": v(-202.02, -328.56) * mm});
            skLineSegment(sketch, "E3148", {"start": v(-202.02, -328.56) * mm, "end": v(-203.21, -328.45) * mm});
            skLineSegment(sketch, "E3149", {"start": v(-203.21, -328.45) * mm, "end": v(-204.4, -328.56) * mm});
            skLineSegment(sketch, "E3150", {"start": v(-204.4, -328.56) * mm, "end": v(-205.49, -328.77) * mm});
            skLineSegment(sketch, "E3151", {"start": v(-205.49, -328.77) * mm, "end": v(-206.57, -328.99) * mm});
            skLineSegment(sketch, "E3152", {"start": v(-206.57, -328.99) * mm, "end": v(-207.65, -329.42) * mm});
            skLineSegment(sketch, "E3153", {"start": v(-207.65, -329.42) * mm, "end": v(-208.73, -329.96) * mm});
            skLineSegment(sketch, "E3154", {"start": v(-208.73, -329.96) * mm, "end": v(-209.7, -330.61) * mm});
            skLineSegment(sketch, "E3155", {"start": v(-209.7, -330.61) * mm, "end": v(-210.57, -331.37) * mm});
            skLineSegment(sketch, "E3156", {"start": v(-210.57, -331.37) * mm, "end": v(-211.33, -332.13) * mm});
            skLineSegment(sketch, "E3157", {"start": v(-211.33, -332.13) * mm, "end": v(-212.1, -333) * mm});
            skLineSegment(sketch, "E3158", {"start": v(-212.1, -333) * mm, "end": v(-212.74, -333.97) * mm});
            skLineSegment(sketch, "E3159", {"start": v(-212.74, -333.97) * mm, "end": v(-213.28, -335.05) * mm});
            skLineSegment(sketch, "E3160", {"start": v(-213.28, -335.05) * mm, "end": v(-213.6, -336.13) * mm});
            skLineSegment(sketch, "E3161", {"start": v(-213.6, -336.13) * mm, "end": v(-213.93, -337.21) * mm});
            skLineSegment(sketch, "E3162", {"start": v(-213.93, -337.21) * mm, "end": v(-214.15, -338.3) * mm});
            skLineSegment(sketch, "E3163", {"start": v(-214.15, -338.3) * mm, "end": v(-214.15, -339.49) * mm});
            skLineSegment(sketch, "E3164", {"start": v(222.16, -338.84) * mm, "end": v(222.16, -377.15) * mm});
            skLineSegment(sketch, "E3165", {"start": v(216.1, -377.15) * mm, "end": v(216.1, -377.8) * mm});
            skLineSegment(sketch, "E3166", {"start": v(216.1, -377.8) * mm, "end": v(216.53, -378.89) * mm});
            skLineSegment(sketch, "E3167", {"start": v(216.53, -378.89) * mm, "end": v(217.4, -379.75) * mm});
            skLineSegment(sketch, "E3168", {"start": v(217.4, -379.75) * mm, "end": v(217.94, -379.97) * mm});
            skLineSegment(sketch, "E3169", {"start": v(217.94, -379.97) * mm, "end": v(218.47, -380.18) * mm});
            skLineSegment(sketch, "E3170", {"start": v(218.47, -380.18) * mm, "end": v(219.67, -380.18) * mm});
            skLineSegment(sketch, "E3171", {"start": v(219.67, -380.18) * mm, "end": v(220.32, -379.97) * mm});
            skLineSegment(sketch, "E3172", {"start": v(220.32, -379.97) * mm, "end": v(220.75, -379.75) * mm});
            skLineSegment(sketch, "E3173", {"start": v(220.75, -379.75) * mm, "end": v(221.29, -379.32) * mm});
            skLineSegment(sketch, "E3174", {"start": v(221.29, -379.32) * mm, "end": v(221.61, -378.89) * mm});
            skLineSegment(sketch, "E3175", {"start": v(221.61, -378.89) * mm, "end": v(221.94, -378.34) * mm});
            skLineSegment(sketch, "E3176", {"start": v(221.94, -378.34) * mm, "end": v(222.05, -377.8) * mm});
            skLineSegment(sketch, "E3177", {"start": v(222.05, -377.8) * mm, "end": v(222.16, -377.15) * mm});
            skLineSegment(sketch, "E3178", {"start": v(216.1, -377.15) * mm, "end": v(216.1, -338.84) * mm});
            skLineSegment(sketch, "E3179", {"start": v(222.16, -338.84) * mm, "end": v(222.05, -338.3) * mm});
            skLineSegment(sketch, "E3180", {"start": v(222.05, -338.3) * mm, "end": v(221.94, -337.65) * mm});
            skLineSegment(sketch, "E3181", {"start": v(221.94, -337.65) * mm, "end": v(221.61, -337.21) * mm});
            skLineSegment(sketch, "E3182", {"start": v(221.61, -337.21) * mm, "end": v(221.29, -336.67) * mm});
            skLineSegment(sketch, "E3183", {"start": v(221.29, -336.67) * mm, "end": v(220.75, -336.35) * mm});
            skLineSegment(sketch, "E3184", {"start": v(220.75, -336.35) * mm, "end": v(220.32, -336.02) * mm});
            skLineSegment(sketch, "E3185", {"start": v(220.32, -336.02) * mm, "end": v(219.67, -335.91) * mm});
            skLineSegment(sketch, "E3186", {"start": v(219.67, -335.91) * mm, "end": v(219.13, -335.8) * mm});
            skLineSegment(sketch, "E3187", {"start": v(219.13, -335.8) * mm, "end": v(218.47, -335.91) * mm});
            skLineSegment(sketch, "E3188", {"start": v(218.47, -335.91) * mm, "end": v(217.94, -336.02) * mm});
            skLineSegment(sketch, "E3189", {"start": v(217.94, -336.02) * mm, "end": v(217.4, -336.35) * mm});
            skLineSegment(sketch, "E3190", {"start": v(217.4, -336.35) * mm, "end": v(216.96, -336.67) * mm});
            skLineSegment(sketch, "E3191", {"start": v(216.96, -336.67) * mm, "end": v(216.53, -337.21) * mm});
            skLineSegment(sketch, "E3192", {"start": v(216.53, -337.21) * mm, "end": v(216.31, -337.65) * mm});
            skLineSegment(sketch, "E3193", {"start": v(216.31, -337.65) * mm, "end": v(216.1, -338.3) * mm});
            skLineSegment(sketch, "E3194", {"start": v(216.1, -338.3) * mm, "end": v(216.1, -338.84) * mm});
            skLineSegment(sketch, "E3195", {"start": v(208.09, -339.49) * mm, "end": v(208.09, -376.5) * mm});
            skLineSegment(sketch, "E3196", {"start": v(208.09, -376.5) * mm, "end": v(208.2, -377.7) * mm});
            skLineSegment(sketch, "E3197", {"start": v(208.2, -377.7) * mm, "end": v(208.41, -378.89) * mm});
            skLineSegment(sketch, "E3198", {"start": v(208.41, -378.89) * mm, "end": v(208.63, -379.97) * mm});
            skLineSegment(sketch, "E3199", {"start": v(208.63, -379.97) * mm, "end": v(209.06, -381.05) * mm});
            skLineSegment(sketch, "E3200", {"start": v(209.06, -381.05) * mm, "end": v(209.6, -382.02) * mm});
            skLineSegment(sketch, "E3201", {"start": v(209.6, -382.02) * mm, "end": v(210.25, -383) * mm});
            skLineSegment(sketch, "E3202", {"start": v(210.25, -383) * mm, "end": v(210.9, -383.86) * mm});
            skLineSegment(sketch, "E3203", {"start": v(210.9, -383.86) * mm, "end": v(211.77, -384.73) * mm});
            skLineSegment(sketch, "E3204", {"start": v(211.77, -384.73) * mm, "end": v(212.63, -385.49) * mm});
            skLineSegment(sketch, "E3205", {"start": v(212.63, -385.49) * mm, "end": v(213.6, -386.03) * mm});
            skLineSegment(sketch, "E3206", {"start": v(213.6, -386.03) * mm, "end": v(214.69, -386.57) * mm});
            skLineSegment(sketch, "E3207", {"start": v(214.69, -386.57) * mm, "end": v(215.66, -387) * mm});
            skLineSegment(sketch, "E3208", {"start": v(215.66, -387) * mm, "end": v(216.85, -387.33) * mm});
            skLineSegment(sketch, "E3209", {"start": v(216.85, -387.33) * mm, "end": v(217.94, -387.44) * mm});
            skLineSegment(sketch, "E3210", {"start": v(217.94, -387.44) * mm, "end": v(219.13, -387.54) * mm});
            skLineSegment(sketch, "E3211", {"start": v(219.13, -387.54) * mm, "end": v(220.2, -387.44) * mm});
            skLineSegment(sketch, "E3212", {"start": v(220.2, -387.44) * mm, "end": v(221.4, -387.33) * mm});
            skLineSegment(sketch, "E3213", {"start": v(221.4, -387.33) * mm, "end": v(222.48, -387) * mm});
            skLineSegment(sketch, "E3214", {"start": v(222.48, -387) * mm, "end": v(223.56, -386.57) * mm});
            skLineSegment(sketch, "E3215", {"start": v(223.56, -386.57) * mm, "end": v(224.64, -386.03) * mm});
            skLineSegment(sketch, "E3216", {"start": v(224.64, -386.03) * mm, "end": v(225.51, -385.49) * mm});
            skLineSegment(sketch, "E3217", {"start": v(225.51, -385.49) * mm, "end": v(226.49, -384.73) * mm});
            skLineSegment(sketch, "E3218", {"start": v(226.49, -384.73) * mm, "end": v(227.25, -383.86) * mm});
            skLineSegment(sketch, "E3219", {"start": v(227.25, -383.86) * mm, "end": v(228, -383) * mm});
            skLineSegment(sketch, "E3220", {"start": v(228, -383) * mm, "end": v(228.65, -382.02) * mm});
            skLineSegment(sketch, "E3221", {"start": v(228.65, -382.02) * mm, "end": v(229.09, -381.05) * mm});
            skLineSegment(sketch, "E3222", {"start": v(229.09, -381.05) * mm, "end": v(229.52, -379.97) * mm});
            skLineSegment(sketch, "E3223", {"start": v(229.52, -379.97) * mm, "end": v(229.84, -378.89) * mm});
            skLineSegment(sketch, "E3224", {"start": v(229.84, -378.89) * mm, "end": v(230.06, -377.7) * mm});
            skLineSegment(sketch, "E3225", {"start": v(230.06, -377.7) * mm, "end": v(230.06, -376.5) * mm});
            skLineSegment(sketch, "E3226", {"start": v(230.06, -376.5) * mm, "end": v(230.06, -339.49) * mm});
            skLineSegment(sketch, "E3227", {"start": v(230.06, -339.49) * mm, "end": v(230.06, -338.3) * mm});
            skLineSegment(sketch, "E3228", {"start": v(230.06, -338.3) * mm, "end": v(229.84, -337.21) * mm});
            skLineSegment(sketch, "E3229", {"start": v(229.84, -337.21) * mm, "end": v(229.52, -336.13) * mm});
            skLineSegment(sketch, "E3230", {"start": v(229.52, -336.13) * mm, "end": v(229.09, -335.05) * mm});
            skLineSegment(sketch, "E3231", {"start": v(229.09, -335.05) * mm, "end": v(228.65, -333.97) * mm});
            skLineSegment(sketch, "E3232", {"start": v(228.65, -333.97) * mm, "end": v(228, -333) * mm});
            skLineSegment(sketch, "E3233", {"start": v(228, -333) * mm, "end": v(227.25, -332.13) * mm});
            skLineSegment(sketch, "E3234", {"start": v(227.25, -332.13) * mm, "end": v(226.49, -331.37) * mm});
            skLineSegment(sketch, "E3235", {"start": v(226.49, -331.37) * mm, "end": v(225.51, -330.61) * mm});
            skLineSegment(sketch, "E3236", {"start": v(225.51, -330.61) * mm, "end": v(224.64, -329.96) * mm});
            skLineSegment(sketch, "E3237", {"start": v(224.64, -329.96) * mm, "end": v(223.56, -329.42) * mm});
            skLineSegment(sketch, "E3238", {"start": v(223.56, -329.42) * mm, "end": v(222.48, -328.99) * mm});
            skLineSegment(sketch, "E3239", {"start": v(222.48, -328.99) * mm, "end": v(221.4, -328.77) * mm});
            skLineSegment(sketch, "E3240", {"start": v(221.4, -328.77) * mm, "end": v(220.2, -328.56) * mm});
            skLineSegment(sketch, "E3241", {"start": v(220.2, -328.56) * mm, "end": v(219.13, -328.45) * mm});
            skLineSegment(sketch, "E3242", {"start": v(219.13, -328.45) * mm, "end": v(217.94, -328.56) * mm});
            skLineSegment(sketch, "E3243", {"start": v(217.94, -328.56) * mm, "end": v(216.85, -328.77) * mm});
            skLineSegment(sketch, "E3244", {"start": v(216.85, -328.77) * mm, "end": v(215.66, -328.99) * mm});
            skLineSegment(sketch, "E3245", {"start": v(215.66, -328.99) * mm, "end": v(214.69, -329.42) * mm});
            skLineSegment(sketch, "E3246", {"start": v(214.69, -329.42) * mm, "end": v(213.6, -329.96) * mm});
            skLineSegment(sketch, "E3247", {"start": v(213.6, -329.96) * mm, "end": v(212.63, -330.61) * mm});
            skLineSegment(sketch, "E3248", {"start": v(212.63, -330.61) * mm, "end": v(211.77, -331.37) * mm});
            skLineSegment(sketch, "E3249", {"start": v(211.77, -331.37) * mm, "end": v(210.9, -332.13) * mm});
            skLineSegment(sketch, "E3250", {"start": v(210.9, -332.13) * mm, "end": v(210.25, -333) * mm});
            skLineSegment(sketch, "E3251", {"start": v(210.25, -333) * mm, "end": v(209.6, -333.97) * mm});
            skLineSegment(sketch, "E3252", {"start": v(209.6, -333.97) * mm, "end": v(209.06, -335.05) * mm});
            skLineSegment(sketch, "E3253", {"start": v(209.06, -335.05) * mm, "end": v(208.63, -336.13) * mm});
            skLineSegment(sketch, "E3254", {"start": v(208.63, -336.13) * mm, "end": v(208.2, -338.3) * mm});
            skLineSegment(sketch, "E3255", {"start": v(208.2, -338.3) * mm, "end": v(208.09, -339.49) * mm});
            skLineSegment(sketch, "E3256", {"start": v(75.39, -376.5) * mm, "end": v(75.5, -377.7) * mm});
            skLineSegment(sketch, "E3257", {"start": v(75.5, -377.7) * mm, "end": v(75.6, -378.89) * mm});
            skLineSegment(sketch, "E3258", {"start": v(75.6, -378.89) * mm, "end": v(75.93, -379.97) * mm});
            skLineSegment(sketch, "E3259", {"start": v(75.93, -379.97) * mm, "end": v(76.36, -381.05) * mm});
            skLineSegment(sketch, "E3260", {"start": v(76.36, -381.05) * mm, "end": v(76.9, -382.02) * mm});
            skLineSegment(sketch, "E3261", {"start": v(76.9, -382.02) * mm, "end": v(77.55, -383) * mm});
            skLineSegment(sketch, "E3262", {"start": v(77.55, -383) * mm, "end": v(78.2, -383.86) * mm});
            skLineSegment(sketch, "E3263", {"start": v(78.2, -383.86) * mm, "end": v(79.07, -384.73) * mm});
            skLineSegment(sketch, "E3264", {"start": v(79.07, -384.73) * mm, "end": v(79.94, -385.49) * mm});
            skLineSegment(sketch, "E3265", {"start": v(79.94, -385.49) * mm, "end": v(80.9, -386.03) * mm});
            skLineSegment(sketch, "E3266", {"start": v(80.9, -386.03) * mm, "end": v(81.88, -386.57) * mm});
            skLineSegment(sketch, "E3267", {"start": v(81.88, -386.57) * mm, "end": v(82.97, -387) * mm});
            skLineSegment(sketch, "E3268", {"start": v(82.97, -387) * mm, "end": v(84.15, -387.33) * mm});
            skLineSegment(sketch, "E3269", {"start": v(84.15, -387.33) * mm, "end": v(85.24, -387.44) * mm});
            skLineSegment(sketch, "E3270", {"start": v(85.24, -387.44) * mm, "end": v(86.43, -387.54) * mm});
            skLineSegment(sketch, "E3271", {"start": v(86.43, -387.54) * mm, "end": v(87.5, -387.44) * mm});
            skLineSegment(sketch, "E3272", {"start": v(87.5, -387.44) * mm, "end": v(88.7, -387.33) * mm});
            skLineSegment(sketch, "E3273", {"start": v(88.7, -387.33) * mm, "end": v(89.78, -387) * mm});
            skLineSegment(sketch, "E3274", {"start": v(89.78, -387) * mm, "end": v(90.86, -386.57) * mm});
            skLineSegment(sketch, "E3275", {"start": v(90.86, -386.57) * mm, "end": v(91.84, -386.03) * mm});
            skLineSegment(sketch, "E3276", {"start": v(91.84, -386.03) * mm, "end": v(92.82, -385.49) * mm});
            skLineSegment(sketch, "E3277", {"start": v(92.82, -385.49) * mm, "end": v(93.79, -384.73) * mm});
            skLineSegment(sketch, "E3278", {"start": v(93.79, -384.73) * mm, "end": v(94.54, -383.86) * mm});
            skLineSegment(sketch, "E3279", {"start": v(94.54, -383.86) * mm, "end": v(95.3, -383) * mm});
            skLineSegment(sketch, "E3280", {"start": v(95.3, -383) * mm, "end": v(95.95, -382.02) * mm});
            skLineSegment(sketch, "E3281", {"start": v(95.95, -382.02) * mm, "end": v(96.38, -381.05) * mm});
            skLineSegment(sketch, "E3282", {"start": v(96.38, -381.05) * mm, "end": v(96.82, -379.97) * mm});
            skLineSegment(sketch, "E3283", {"start": v(96.82, -379.97) * mm, "end": v(97.14, -378.89) * mm});
            skLineSegment(sketch, "E3284", {"start": v(97.14, -378.89) * mm, "end": v(97.36, -377.7) * mm});
            skLineSegment(sketch, "E3285", {"start": v(97.36, -377.7) * mm, "end": v(97.36, -376.5) * mm});
            skLineSegment(sketch, "E3286", {"start": v(97.36, -376.5) * mm, "end": v(97.36, -367.3) * mm});
            skLineSegment(sketch, "E3287", {"start": v(97.36, -367.3) * mm, "end": v(89.46, -367.3) * mm});
            skLineSegment(sketch, "E3288", {"start": v(89.46, -367.3) * mm, "end": v(89.46, -377.15) * mm});
            skLineSegment(sketch, "E3289", {"start": v(83.29, -377.15) * mm, "end": v(83.4, -377.8) * mm});
            skLineSegment(sketch, "E3290", {"start": v(83.4, -377.8) * mm, "end": v(83.62, -378.34) * mm});
            skLineSegment(sketch, "E3291", {"start": v(83.62, -378.34) * mm, "end": v(83.83, -378.89) * mm});
            skLineSegment(sketch, "E3292", {"start": v(83.83, -378.89) * mm, "end": v(84.7, -379.75) * mm});
            skLineSegment(sketch, "E3293", {"start": v(84.7, -379.75) * mm, "end": v(85.24, -379.97) * mm});
            skLineSegment(sketch, "E3294", {"start": v(85.24, -379.97) * mm, "end": v(85.78, -380.18) * mm});
            skLineSegment(sketch, "E3295", {"start": v(85.78, -380.18) * mm, "end": v(86.97, -380.18) * mm});
            skLineSegment(sketch, "E3296", {"start": v(86.97, -380.18) * mm, "end": v(88.05, -379.75) * mm});
            skLineSegment(sketch, "E3297", {"start": v(88.05, -379.75) * mm, "end": v(88.6, -379.32) * mm});
            skLineSegment(sketch, "E3298", {"start": v(88.6, -379.32) * mm, "end": v(88.92, -378.89) * mm});
            skLineSegment(sketch, "E3299", {"start": v(88.92, -378.89) * mm, "end": v(89.24, -378.34) * mm});
            skLineSegment(sketch, "E3300", {"start": v(89.24, -378.34) * mm, "end": v(89.35, -377.8) * mm});
            skLineSegment(sketch, "E3301", {"start": v(89.35, -377.8) * mm, "end": v(89.46, -377.15) * mm});
            skLineSegment(sketch, "E3302", {"start": v(83.29, -377.15) * mm, "end": v(83.29, -338.84) * mm});
            skLineSegment(sketch, "E3303", {"start": v(89.46, -338.84) * mm, "end": v(89.35, -338.3) * mm});
            skLineSegment(sketch, "E3304", {"start": v(89.35, -338.3) * mm, "end": v(89.24, -337.65) * mm});
            skLineSegment(sketch, "E3305", {"start": v(89.24, -337.65) * mm, "end": v(88.92, -337.21) * mm});
            skLineSegment(sketch, "E3306", {"start": v(88.92, -337.21) * mm, "end": v(88.6, -336.67) * mm});
            skLineSegment(sketch, "E3307", {"start": v(88.6, -336.67) * mm, "end": v(88.05, -336.35) * mm});
            skLineSegment(sketch, "E3308", {"start": v(88.05, -336.35) * mm, "end": v(87.5, -336.02) * mm});
            skLineSegment(sketch, "E3309", {"start": v(87.5, -336.02) * mm, "end": v(86.97, -335.91) * mm});
            skLineSegment(sketch, "E3310", {"start": v(86.97, -335.91) * mm, "end": v(86.43, -335.8) * mm});
            skLineSegment(sketch, "E3311", {"start": v(86.43, -335.8) * mm, "end": v(85.78, -335.91) * mm});
            skLineSegment(sketch, "E3312", {"start": v(85.78, -335.91) * mm, "end": v(85.24, -336.02) * mm});
            skLineSegment(sketch, "E3313", {"start": v(85.24, -336.02) * mm, "end": v(84.7, -336.35) * mm});
            skLineSegment(sketch, "E3314", {"start": v(84.7, -336.35) * mm, "end": v(84.26, -336.67) * mm});
            skLineSegment(sketch, "E3315", {"start": v(84.26, -336.67) * mm, "end": v(83.83, -337.21) * mm});
            skLineSegment(sketch, "E3316", {"start": v(83.83, -337.21) * mm, "end": v(83.62, -337.65) * mm});
            skLineSegment(sketch, "E3317", {"start": v(83.62, -337.65) * mm, "end": v(83.4, -338.3) * mm});
            skLineSegment(sketch, "E3318", {"start": v(83.4, -338.3) * mm, "end": v(83.29, -338.84) * mm});
            skLineSegment(sketch, "E3319", {"start": v(89.46, -338.84) * mm, "end": v(89.46, -348.69) * mm});
            skLineSegment(sketch, "E3320", {"start": v(89.46, -348.69) * mm, "end": v(97.36, -348.69) * mm});
            skLineSegment(sketch, "E3321", {"start": v(97.36, -348.69) * mm, "end": v(97.36, -339.49) * mm});
            skLineSegment(sketch, "E3322", {"start": v(97.36, -339.49) * mm, "end": v(97.36, -338.3) * mm});
            skLineSegment(sketch, "E3323", {"start": v(97.36, -338.3) * mm, "end": v(97.14, -337.21) * mm});
            skLineSegment(sketch, "E3324", {"start": v(97.14, -337.21) * mm, "end": v(96.82, -336.13) * mm});
            skLineSegment(sketch, "E3325", {"start": v(96.82, -336.13) * mm, "end": v(96.38, -335.05) * mm});
            skLineSegment(sketch, "E3326", {"start": v(96.38, -335.05) * mm, "end": v(95.95, -333.97) * mm});
            skLineSegment(sketch, "E3327", {"start": v(95.95, -333.97) * mm, "end": v(95.3, -333) * mm});
            skLineSegment(sketch, "E3328", {"start": v(95.3, -333) * mm, "end": v(94.54, -332.13) * mm});
            skLineSegment(sketch, "E3329", {"start": v(94.54, -332.13) * mm, "end": v(93.79, -331.37) * mm});
            skLineSegment(sketch, "E3330", {"start": v(93.79, -331.37) * mm, "end": v(92.82, -330.61) * mm});
            skLineSegment(sketch, "E3331", {"start": v(92.82, -330.61) * mm, "end": v(91.84, -329.96) * mm});
            skLineSegment(sketch, "E3332", {"start": v(91.84, -329.96) * mm, "end": v(90.86, -329.42) * mm});
            skLineSegment(sketch, "E3333", {"start": v(90.86, -329.42) * mm, "end": v(89.78, -328.99) * mm});
            skLineSegment(sketch, "E3334", {"start": v(89.78, -328.99) * mm, "end": v(88.7, -328.77) * mm});
            skLineSegment(sketch, "E3335", {"start": v(88.7, -328.77) * mm, "end": v(87.5, -328.56) * mm});
            skLineSegment(sketch, "E3336", {"start": v(87.5, -328.56) * mm, "end": v(86.43, -328.45) * mm});
            skLineSegment(sketch, "E3337", {"start": v(86.43, -328.45) * mm, "end": v(85.24, -328.56) * mm});
            skLineSegment(sketch, "E3338", {"start": v(85.24, -328.56) * mm, "end": v(84.15, -328.77) * mm});
            skLineSegment(sketch, "E3339", {"start": v(84.15, -328.77) * mm, "end": v(82.97, -328.99) * mm});
            skLineSegment(sketch, "E3340", {"start": v(82.97, -328.99) * mm, "end": v(81.88, -329.42) * mm});
            skLineSegment(sketch, "E3341", {"start": v(81.88, -329.42) * mm, "end": v(80.9, -329.96) * mm});
            skLineSegment(sketch, "E3342", {"start": v(80.9, -329.96) * mm, "end": v(79.94, -330.61) * mm});
            skLineSegment(sketch, "E3343", {"start": v(79.94, -330.61) * mm, "end": v(79.07, -331.37) * mm});
            skLineSegment(sketch, "E3344", {"start": v(79.07, -331.37) * mm, "end": v(78.2, -332.13) * mm});
            skLineSegment(sketch, "E3345", {"start": v(78.2, -332.13) * mm, "end": v(77.55, -333) * mm});
            skLineSegment(sketch, "E3346", {"start": v(77.55, -333) * mm, "end": v(76.9, -333.97) * mm});
            skLineSegment(sketch, "E3347", {"start": v(76.9, -333.97) * mm, "end": v(76.36, -335.05) * mm});
            skLineSegment(sketch, "E3348", {"start": v(76.36, -335.05) * mm, "end": v(75.93, -336.13) * mm});
            skLineSegment(sketch, "E3349", {"start": v(75.93, -336.13) * mm, "end": v(75.6, -337.21) * mm});
            skLineSegment(sketch, "E3350", {"start": v(75.6, -337.21) * mm, "end": v(75.5, -338.3) * mm});
            skLineSegment(sketch, "E3351", {"start": v(75.5, -338.3) * mm, "end": v(75.39, -339.49) * mm});
            skLineSegment(sketch, "E3352", {"start": v(75.39, -339.49) * mm, "end": v(75.39, -376.5) * mm});
            skLineSegment(sketch, "E3353", {"start": v(141.63, -376.5) * mm, "end": v(141.74, -377.7) * mm});
            skLineSegment(sketch, "E3354", {"start": v(141.74, -377.7) * mm, "end": v(141.95, -378.89) * mm});
            skLineSegment(sketch, "E3355", {"start": v(141.95, -378.89) * mm, "end": v(142.17, -379.97) * mm});
            skLineSegment(sketch, "E3356", {"start": v(142.17, -379.97) * mm, "end": v(142.6, -381.05) * mm});
            skLineSegment(sketch, "E3357", {"start": v(142.6, -381.05) * mm, "end": v(143.15, -382.02) * mm});
            skLineSegment(sketch, "E3358", {"start": v(143.15, -382.02) * mm, "end": v(143.8, -383) * mm});
            skLineSegment(sketch, "E3359", {"start": v(143.8, -383) * mm, "end": v(144.44, -383.86) * mm});
            skLineSegment(sketch, "E3360", {"start": v(144.44, -383.86) * mm, "end": v(145.3, -384.73) * mm});
            skLineSegment(sketch, "E3361", {"start": v(145.3, -384.73) * mm, "end": v(146.18, -385.49) * mm});
            skLineSegment(sketch, "E3362", {"start": v(146.18, -385.49) * mm, "end": v(147.15, -386.03) * mm});
            skLineSegment(sketch, "E3363", {"start": v(147.15, -386.03) * mm, "end": v(148.23, -386.57) * mm});
            skLineSegment(sketch, "E3364", {"start": v(148.23, -386.57) * mm, "end": v(149.2, -387) * mm});
            skLineSegment(sketch, "E3365", {"start": v(149.2, -387) * mm, "end": v(150.4, -387.33) * mm});
            skLineSegment(sketch, "E3366", {"start": v(150.4, -387.33) * mm, "end": v(151.48, -387.44) * mm});
            skLineSegment(sketch, "E3367", {"start": v(151.48, -387.44) * mm, "end": v(152.67, -387.54) * mm});
            skLineSegment(sketch, "E3368", {"start": v(152.67, -387.54) * mm, "end": v(153.75, -387.44) * mm});
            skLineSegment(sketch, "E3369", {"start": v(153.75, -387.44) * mm, "end": v(154.94, -387.33) * mm});
            skLineSegment(sketch, "E3370", {"start": v(154.94, -387.33) * mm, "end": v(156.02, -387) * mm});
            skLineSegment(sketch, "E3371", {"start": v(156.02, -387) * mm, "end": v(157.1, -386.57) * mm});
            skLineSegment(sketch, "E3372", {"start": v(157.1, -386.57) * mm, "end": v(158.19, -386.03) * mm});
            skLineSegment(sketch, "E3373", {"start": v(158.19, -386.03) * mm, "end": v(159.06, -385.49) * mm});
            skLineSegment(sketch, "E3374", {"start": v(159.06, -385.49) * mm, "end": v(160.03, -384.73) * mm});
            skLineSegment(sketch, "E3375", {"start": v(160.03, -384.73) * mm, "end": v(160.79, -383.86) * mm});
            skLineSegment(sketch, "E3376", {"start": v(160.79, -383.86) * mm, "end": v(161.54, -383) * mm});
            skLineSegment(sketch, "E3377", {"start": v(161.54, -383) * mm, "end": v(162.2, -382.02) * mm});
            skLineSegment(sketch, "E3378", {"start": v(162.2, -382.02) * mm, "end": v(162.74, -381.05) * mm});
            skLineSegment(sketch, "E3379", {"start": v(162.74, -381.05) * mm, "end": v(163.06, -379.97) * mm});
            skLineSegment(sketch, "E3380", {"start": v(163.06, -379.97) * mm, "end": v(163.38, -378.89) * mm});
            skLineSegment(sketch, "E3381", {"start": v(163.38, -378.89) * mm, "end": v(163.6, -377.7) * mm});
            skLineSegment(sketch, "E3382", {"start": v(163.6, -377.7) * mm, "end": v(163.6, -376.5) * mm});
            skLineSegment(sketch, "E3383", {"start": v(163.6, -376.5) * mm, "end": v(163.6, -367.3) * mm});
            skLineSegment(sketch, "E3384", {"start": v(163.6, -367.3) * mm, "end": v(155.7, -367.3) * mm});
            skLineSegment(sketch, "E3385", {"start": v(155.7, -367.3) * mm, "end": v(155.7, -377.15) * mm});
            skLineSegment(sketch, "E3386", {"start": v(149.64, -377.15) * mm, "end": v(149.64, -377.8) * mm});
            skLineSegment(sketch, "E3387", {"start": v(149.64, -377.8) * mm, "end": v(149.86, -378.34) * mm});
            skLineSegment(sketch, "E3388", {"start": v(149.86, -378.34) * mm, "end": v(150.07, -378.89) * mm});
            skLineSegment(sketch, "E3389", {"start": v(150.07, -378.89) * mm, "end": v(150.94, -379.75) * mm});
            skLineSegment(sketch, "E3390", {"start": v(150.94, -379.75) * mm, "end": v(151.48, -379.97) * mm});
            skLineSegment(sketch, "E3391", {"start": v(151.48, -379.97) * mm, "end": v(152.02, -380.18) * mm});
            skLineSegment(sketch, "E3392", {"start": v(152.02, -380.18) * mm, "end": v(153.21, -380.18) * mm});
            skLineSegment(sketch, "E3393", {"start": v(153.21, -380.18) * mm, "end": v(153.86, -379.97) * mm});
            skLineSegment(sketch, "E3394", {"start": v(153.86, -379.97) * mm, "end": v(154.3, -379.75) * mm});
            skLineSegment(sketch, "E3395", {"start": v(154.3, -379.75) * mm, "end": v(154.83, -379.32) * mm});
            skLineSegment(sketch, "E3396", {"start": v(154.83, -379.32) * mm, "end": v(155.16, -378.89) * mm});
            skLineSegment(sketch, "E3397", {"start": v(155.16, -378.89) * mm, "end": v(155.48, -378.34) * mm});
            skLineSegment(sketch, "E3398", {"start": v(155.48, -378.34) * mm, "end": v(155.6, -377.8) * mm});
            skLineSegment(sketch, "E3399", {"start": v(155.6, -377.8) * mm, "end": v(155.7, -377.15) * mm});
            skLineSegment(sketch, "E3400", {"start": v(149.64, -377.15) * mm, "end": v(149.64, -338.84) * mm});
            skLineSegment(sketch, "E3401", {"start": v(155.7, -338.84) * mm, "end": v(155.6, -338.3) * mm});
            skLineSegment(sketch, "E3402", {"start": v(155.6, -338.3) * mm, "end": v(155.48, -337.65) * mm});
            skLineSegment(sketch, "E3403", {"start": v(155.48, -337.65) * mm, "end": v(155.16, -337.21) * mm});
            skLineSegment(sketch, "E3404", {"start": v(155.16, -337.21) * mm, "end": v(154.83, -336.67) * mm});
            skLineSegment(sketch, "E3405", {"start": v(154.83, -336.67) * mm, "end": v(154.3, -336.35) * mm});
            skLineSegment(sketch, "E3406", {"start": v(154.3, -336.35) * mm, "end": v(153.86, -336.02) * mm});
            skLineSegment(sketch, "E3407", {"start": v(153.86, -336.02) * mm, "end": v(153.21, -335.91) * mm});
            skLineSegment(sketch, "E3408", {"start": v(153.21, -335.91) * mm, "end": v(152.67, -335.8) * mm});
            skLineSegment(sketch, "E3409", {"start": v(152.67, -335.8) * mm, "end": v(152.02, -335.91) * mm});
            skLineSegment(sketch, "E3410", {"start": v(152.02, -335.91) * mm, "end": v(151.48, -336.02) * mm});
            skLineSegment(sketch, "E3411", {"start": v(151.48, -336.02) * mm, "end": v(150.94, -336.35) * mm});
            skLineSegment(sketch, "E3412", {"start": v(150.94, -336.35) * mm, "end": v(150.5, -336.67) * mm});
            skLineSegment(sketch, "E3413", {"start": v(150.5, -336.67) * mm, "end": v(150.07, -337.21) * mm});
            skLineSegment(sketch, "E3414", {"start": v(150.07, -337.21) * mm, "end": v(149.86, -337.65) * mm});
            skLineSegment(sketch, "E3415", {"start": v(149.86, -337.65) * mm, "end": v(149.64, -338.3) * mm});
            skLineSegment(sketch, "E3416", {"start": v(149.64, -338.3) * mm, "end": v(149.64, -338.84) * mm});
            skLineSegment(sketch, "E3417", {"start": v(155.7, -338.84) * mm, "end": v(155.7, -348.69) * mm});
            skLineSegment(sketch, "E3418", {"start": v(155.7, -348.69) * mm, "end": v(163.6, -348.69) * mm});
            skLineSegment(sketch, "E3419", {"start": v(163.6, -348.69) * mm, "end": v(163.6, -339.49) * mm});
            skLineSegment(sketch, "E3420", {"start": v(163.6, -339.49) * mm, "end": v(163.6, -338.3) * mm});
            skLineSegment(sketch, "E3421", {"start": v(163.6, -338.3) * mm, "end": v(163.38, -337.21) * mm});
            skLineSegment(sketch, "E3422", {"start": v(163.38, -337.21) * mm, "end": v(163.06, -336.13) * mm});
            skLineSegment(sketch, "E3423", {"start": v(163.06, -336.13) * mm, "end": v(162.74, -335.05) * mm});
            skLineSegment(sketch, "E3424", {"start": v(162.74, -335.05) * mm, "end": v(162.2, -333.97) * mm});
            skLineSegment(sketch, "E3425", {"start": v(162.2, -333.97) * mm, "end": v(161.54, -333) * mm});
            skLineSegment(sketch, "E3426", {"start": v(161.54, -333) * mm, "end": v(160.79, -332.13) * mm});
            skLineSegment(sketch, "E3427", {"start": v(160.79, -332.13) * mm, "end": v(160.03, -331.37) * mm});
            skLineSegment(sketch, "E3428", {"start": v(160.03, -331.37) * mm, "end": v(159.06, -330.61) * mm});
            skLineSegment(sketch, "E3429", {"start": v(159.06, -330.61) * mm, "end": v(158.19, -329.96) * mm});
            skLineSegment(sketch, "E3430", {"start": v(158.19, -329.96) * mm, "end": v(157.1, -329.42) * mm});
            skLineSegment(sketch, "E3431", {"start": v(157.1, -329.42) * mm, "end": v(156.02, -328.99) * mm});
            skLineSegment(sketch, "E3432", {"start": v(156.02, -328.99) * mm, "end": v(154.94, -328.77) * mm});
            skLineSegment(sketch, "E3433", {"start": v(154.94, -328.77) * mm, "end": v(153.75, -328.56) * mm});
            skLineSegment(sketch, "E3434", {"start": v(153.75, -328.56) * mm, "end": v(152.67, -328.45) * mm});
            skLineSegment(sketch, "E3435", {"start": v(152.67, -328.45) * mm, "end": v(151.48, -328.56) * mm});
            skLineSegment(sketch, "E3436", {"start": v(151.48, -328.56) * mm, "end": v(150.4, -328.77) * mm});
            skLineSegment(sketch, "E3437", {"start": v(150.4, -328.77) * mm, "end": v(149.2, -328.99) * mm});
            skLineSegment(sketch, "E3438", {"start": v(149.2, -328.99) * mm, "end": v(148.23, -329.42) * mm});
            skLineSegment(sketch, "E3439", {"start": v(148.23, -329.42) * mm, "end": v(147.15, -329.96) * mm});
            skLineSegment(sketch, "E3440", {"start": v(147.15, -329.96) * mm, "end": v(146.18, -330.61) * mm});
            skLineSegment(sketch, "E3441", {"start": v(146.18, -330.61) * mm, "end": v(145.3, -331.37) * mm});
            skLineSegment(sketch, "E3442", {"start": v(145.3, -331.37) * mm, "end": v(144.44, -332.13) * mm});
            skLineSegment(sketch, "E3443", {"start": v(144.44, -332.13) * mm, "end": v(143.8, -333) * mm});
            skLineSegment(sketch, "E3444", {"start": v(143.8, -333) * mm, "end": v(143.15, -333.97) * mm});
            skLineSegment(sketch, "E3445", {"start": v(143.15, -333.97) * mm, "end": v(142.6, -335.05) * mm});
            skLineSegment(sketch, "E3446", {"start": v(142.6, -335.05) * mm, "end": v(142.17, -336.13) * mm});
            skLineSegment(sketch, "E3447", {"start": v(142.17, -336.13) * mm, "end": v(141.74, -338.3) * mm});
            skLineSegment(sketch, "E3448", {"start": v(141.74, -338.3) * mm, "end": v(141.63, -339.49) * mm});
            skLineSegment(sketch, "E3449", {"start": v(141.63, -339.49) * mm, "end": v(141.63, -376.5) * mm});
            skSolve(sketch);
        }
        {
            var Q0;
            Q0=qSketchRegion(id+"F0",true);
            extrude(context, id + "F1", {"entities" : qUnion([Q0]), "depth" : 25.4 * mm, "offsetDistance" : 25.4 * mm});
        }
        {
            var Q0;
            Q0=qCreatedBy(makeId("Top.planeOp"),FACE);
            var sketch = newSketch(context, id + "F2", { "sketchPlane" : qUnion([Q0])});
            skLineSegment(sketch, "E3450.bottom", {"start": v(-279.84, 429.7) * mm, "end": v(282.03, 429.7) * mm});
            skLineSegment(sketch, "E3450.top", {"start": v(-279.84, -426.73) * mm, "end": v(282.03, -426.73) * mm});
            skLineSegment(sketch, "E3450.left", {"start": v(-279.84, 429.7) * mm, "end": v(-279.84, -426.73) * mm});
            skLineSegment(sketch, "E3450.right", {"start": v(282.03, 429.7) * mm, "end": v(282.03, -426.73) * mm});
            skSolve(sketch);
        }
        {
            var Q0;
            Q0=makeQuery(id+"F2.imprint","IMPRINT",FACE,{"disambiguationData":[TD([[makeQuery(id+"F2.imprint","IMPRINT",EDGE,{"derivedFrom":sQuery(id+"F2.wireOp",EDGE,"E3450.bottom")}),-1.0]])]});
            extrude(context, id + "F3", {"entities" : qUnion([Q0]), "endBound" : BoundingType.SYMMETRIC, "depth" : 25.4 * mm, "offsetDistance" : 25.4 * mm});
        }
        {
            var Q0;
            Q0=makeQuery(id+"F1.opExtrude","CAP_FACE",FACE,{"disambiguationData":[OSD([sQuery(id+"F0.wireOp",EDGE,"E2611"),sQuery(id+"F0.wireOp",EDGE,"E2612"),sQuery(id+"F0.wireOp",EDGE,"E2613"),sQuery(id+"F0.wireOp",EDGE,"E2614"),sQuery(id+"F0.wireOp",EDGE,"E2615"),sQuery(id+"F0.wireOp",EDGE,"E2616"),sQuery(id+"F0.wireOp",EDGE,"E2617")])],"isStart":false});
            var sketch = newSketch(context, id + "F4", { "sketchPlane" : qUnion([Q0])});
            skLineSegment(sketch, "E3451.bottom", {"start": v(-321.57, -251.63) * mm, "end": v(305.97, -251.63) * mm});
            skLineSegment(sketch, "E3451.top", {"start": v(-321.57, 439) * mm, "end": v(305.97, 439) * mm});
            skLineSegment(sketch, "E3451.left", {"start": v(-321.57, -251.63) * mm, "end": v(-321.57, 439) * mm});
            skLineSegment(sketch, "E3451.right", {"start": v(305.97, -251.63) * mm, "end": v(305.97, 439) * mm});
            skSolve(sketch);
        }
        {
            var Q0;
            Q0 = qSketchRegion(id + "F4", true);
            extrude(context, id + "F5", {"entities" : qUnion([Q0]), "operationType" : NewBodyOperationType.REMOVE, "oppositeDirection" : true, "depth" : 119.38 * mm, "offsetDistance" : 25.4 * mm});
        }
    });
